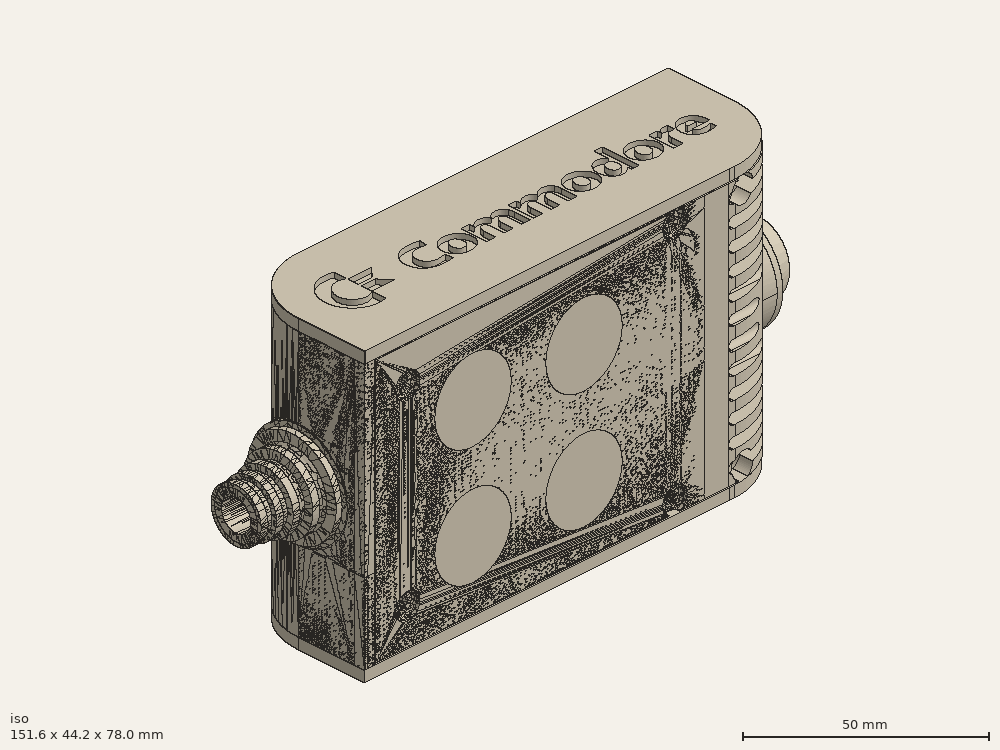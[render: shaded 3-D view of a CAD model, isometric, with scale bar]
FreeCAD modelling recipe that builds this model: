
FCSTD DOCUMENT  (FreeCAD 0.19R0.19.2)
Label: enclosure_224FCStd
License: All rights reserved
LicenseURL: http://en.wikipedia.org/wiki/All_rights_reserved
objects: Part::Revolution×152, Part::MultiFuse×148, Part::Feature×146, Sketcher::SketchObject×94, Part::Extrusion×79, Part::Cut×74, Part::Cylinder×70, Part::Fillet×58, Part::Box×38, App::MeasureDistance×4, Part::Chamfer×4, Part::FeaturePython×2, Image::ImagePlane×1, PartDesign::Body×1, Part::Mirroring×1
note: 867 computed .brp shape members not serialized (recipe doc carries the construction recipe); baked Part::Feature solids carry a one-line shape summary decoded from their .brp

FEATURE [Sketcher::SketchObject] Sketch  label="topSketch"
  FullyConstrained = true
  sketch-geometry (20):
    g0: LineSegment StartX=5.21097e-06 StartY=3 StartZ=0 EndX=5.21097e-06 EndY=19 EndZ=0
    g1: ArcOfCircle CenterX=19 CenterY=19 CenterZ=0 NormalX=0 NormalY=0 NormalZ=1 AngleXU=0 Radius=19 StartAngle=1.5708 EndAngle=3.14159
    g2: ArcOfCircle CenterX=19 CenterY=19 CenterZ=0 NormalX=0 NormalY=0 NormalZ=1 AngleXU=0 Radius=16 StartAngle=1.5708 EndAngle=3.14159
    g3: LineSegment StartX=114 StartY=35 StartZ=0 EndX=19 EndY=35 EndZ=0
    g4: LineSegment StartX=5.21097e-06 StartY=3 StartZ=0 EndX=5.21097e-06 EndY=0 EndZ=0
    g5: LineSegment StartX=3 StartY=0 StartZ=0 EndX=5.21097e-06 EndY=0 EndZ=0
    g6: LineSegment StartX=3 StartY=19 StartZ=0 EndX=3 EndY=0 EndZ=0
    g7: LineSegment StartX=19 StartY=38 StartZ=0 EndX=124 EndY=38 EndZ=0
    g8: Circle CenterX=119 CenterY=35 CenterZ=0 NormalX=0 NormalY=0 NormalZ=1 AngleXU=0 Radius=1
    g9: Circle CenterX=121 CenterY=35 CenterZ=0 NormalX=0 NormalY=0 NormalZ=1 AngleXU=0 Radius=1
    g10: Circle CenterX=121 CenterY=33 CenterZ=0 NormalX=0 NormalY=0 NormalZ=1 AngleXU=0 Radius=1
    g11: BSplineCurve PolesCount=3 KnotsCount=2 Degree=2 IsPeriodic=0
    g12: GeomPoint X=119 Y=35 Z=0
    g13: GeomPoint X=121 Y=33 Z=0
    g14: LineSegment StartX=119 StartY=35 StartZ=0 EndX=114 EndY=35 EndZ=0
    g15: ArcOfCircle CenterX=105 CenterY=19 CenterZ=0 NormalX=0 NormalY=0 NormalZ=1 AngleXU=0 Radius=19 StartAngle=5.7297 EndAngle=6.28319
    g16: ArcOfCircle CenterX=105 CenterY=19 CenterZ=0 NormalX=0 NormalY=0 NormalZ=1 AngleXU=0 Radius=16 StartAngle=5.60905 EndAngle=6.28319
    g17: LineSegment StartX=121 StartY=33 StartZ=0 EndX=121 EndY=19 EndZ=0
    g18: LineSegment StartX=124 StartY=38 StartZ=0 EndX=124 EndY=19 EndZ=0
    g19: LineSegment StartX=117.5 StartY=9.01251 StartZ=0 EndX=121.163 EndY=9.0125 EndZ=0
  constraints (46):
    c: Vertical(g0)
    c: Block(g0)
    c: Coincident(g1,g0)
    c: Block(g1)
    c: Coincident(g2,g1)
    c: Block(g2)
    c: Coincident(g3,g2)
    c: Horizontal(g3)
    c: Tangent(g3,g2)
    c: Coincident(g4,g0)
    c: Distance(g4) = 3
    c: Vertical(g4)
    c: Coincident(g5,g4)
    c: Horizontal(g5)
    c: Coincident(g6,g2)
    c: Coincident(g6,g5)
    c: Vertical(g6)
    c: Horizontal(g7)
    c: Distance(g7) = 105
    c: Coincident(g7,g1)
    c: Block(g3)
    c: Weight(g8) = 1
    c: Equal(g8,g9)
    c: Equal(g8,g10)
    c: InternalAlignment(g8,g11)
    c: InternalAlignment(g9,g11)
    c: InternalAlignment(g10,g11)
    c: InternalAlignment(g12,g11)
    c: InternalAlignment(g13,g11)
    c: Block(g11)
    c: Coincident(g14,g11)
    c: Coincident(g14,g3)
    c: Horizontal(g14)
    c: Block(g15)
    c: Coincident(g16,g15)
    c: Block(g16)
    c: Coincident(g17,g11)
    c: Coincident(g17,g16)
    c: Vertical(g17)
    c: Distance(g17) = 14
    c: Coincident(g18,g7)
    c: Coincident(g18,g15)
    c: Vertical(g18)
    c: Distance(g18) = 19
    c: Coincident(g19,g16)
    c: Coincident(g19,g15)
FEATURE [Sketcher::SketchObject] Sketch001  label="bottomSketch"
  FullyConstrained = true
  sketch-geometry (32):
    g0: LineSegment StartX=3.3 StartY=-6.03275e-07 StartZ=0 EndX=98 EndY=-6.03275e-07 EndZ=0
    g1: ArcOfCircle CenterX=98 CenterY=19 CenterZ=0 NormalX=0 NormalY=0 NormalZ=1 AngleXU=0 Radius=19 StartAngle=4.71239 EndAngle=5.71103
    g2: LineSegment StartX=6.3 StartY=8 StartZ=0 EndX=3.3 EndY=8 EndZ=0
    g3: LineSegment StartX=3.3 StartY=8 StartZ=0 EndX=3.3 EndY=-6.03275e-07 EndZ=0
    g4: ArcOfCircle CenterX=8.3 CenterY=5 CenterZ=0 NormalX=0 NormalY=0 NormalZ=1 AngleXU=0 Radius=2 StartAngle=3.14159 EndAngle=4.71239
    g5: LineSegment StartX=6.3 StartY=8 StartZ=0 EndX=6.3 EndY=5 EndZ=0
    g6: ArcOfCircle CenterX=98 CenterY=19 CenterZ=0 NormalX=0 NormalY=0 NormalZ=1 AngleXU=0 Radius=12.7 StartAngle=4.71239 EndAngle=6.28319
    g7: LineSegment StartX=94.7 StartY=3 StartZ=0 EndX=8.3 EndY=3 EndZ=0
    g8-g12: Circle x5 (B-spline internal-alignment scaffolding for g13; pole/knot coordinates omitted)
    g13: BSplineCurve PolesCount=5 KnotsCount=3 Degree=3 IsPeriodic=0
    g14: GeomPoint X=98 Y=6.3 Z=0
    g15: GeomPoint X=96.3938 Y=4.71946 Z=0
    g16: GeomPoint X=94.7 Y=3 Z=0
    g17-g23: Circle x7 (B-spline internal-alignment scaffolding for g24; pole/knot coordinates omitted)
    g24: BSplineCurve PolesCount=7 KnotsCount=5 Degree=3 IsPeriodic=0
    g25-g29: GeomPoint x5 (B-spline internal-alignment scaffolding for g24; pole/knot coordinates omitted)
    g30: ArcOfCircle CenterX=98 CenterY=19 CenterZ=0 NormalX=0 NormalY=0 NormalZ=1 AngleXU=0 Radius=15.7 StartAngle=5.81226 EndAngle=6.28319
    g31: LineSegment StartX=110.7 StartY=19 StartZ=0 EndX=113.7 EndY=19 EndZ=0
  constraints (41):
    c: Horizontal(g0)
    c: Coincident(g1,g0)
    c: Block(g1)
    c: Horizontal(g2)
    c: Distance(g2) = 3
    c: Coincident(g3,g2)
    c: Vertical(g3)
    c: Coincident(g3,g0)
    c: Block(g4)
    c: Block(g2)
    c: Coincident(g5,g2)
    c: Coincident(g5,g4)
    c: Vertical(g5)
    c: Coincident(g6,g1)
    c: Block(g6)
    c: Coincident(g7,g4)
    c: Horizontal(g7)
    c: Block(g0)
    c: Block(g7)
    c: Block(g3)
    c: Coincident(g13,g6)
    c: Weight(g8) = 1
    c: Equal(g8, g9-g12) x4
    c: Coincident(g13,g7)
    c: InternalAlignment(g8-g12 -> g13) x5
    c: InternalAlignment(g14,g13)
    c: InternalAlignment(g15,g13)
    c: InternalAlignment(g16,g13)
    c: Block(g13)
    c: Weight(g17) = 1
    c: Equal(g17, g18-g23) x6
    c: Coincident(g24,g1)
    c: InternalAlignment(g17-g23 -> g24) x7
    c: InternalAlignment(g25-g29 -> g24) x5
    c: Block(g24)
    c: Coincident(g30,g24)
    c: Coincident(g31,g6)
    c: Coincident(g31,g30)
    c: Horizontal(g31)
    c: Block(g31)
    c: Block(g30)
FEATURE [Part::Extrusion] Extrude  label="top"
  Base = -> Sketch
  Dir = (0,0,1)
  DirMode = 2
  FaceMakerClass = Part::FaceMakerBullseye
  LengthFwd = 72
  LengthRev = 0
  Solid = true
  Symmetric = false
FEATURE [Part::Extrusion] Extrude001  label="bottom"
  Base = -> Sketch001
  Dir = (0,0,1)
  DirMode = 2
  FaceMakerClass = Part::FaceMakerBullseye
  LengthFwd = 71.4
  LengthRev = 0
  Placement = pos=(0,0,0.3) rot=(0,0,1;0rad)
  Solid = true
  Symmetric = false
FEATURE [Sketcher::SketchObject] Sketch002  label="topSketch001"
  FullyConstrained = true
  sketch-geometry (8):
    g0: ArcOfCircle CenterX=19 CenterY=19.0975 CenterZ=0 NormalX=0 NormalY=0 NormalZ=1 AngleXU=0 Radius=18.9025 StartAngle=1.5708 EndAngle=3.14674
    g1: LineSegment StartX=0.0977805 StartY=19.0003 StartZ=0 EndX=0.0977805 EndY=0.000251602 EndZ=0
    g2: LineSegment StartX=19 StartY=38 StartZ=0 EndX=124 EndY=38 EndZ=0
    g3: LineSegment StartX=0.0977805 StartY=0.000251602 StartZ=0 EndX=105.098 EndY=0.000251602 EndZ=0
    g4: LineSegment StartX=124 StartY=38 StartZ=0 EndX=125.616 EndY=38 EndZ=0
    g5: LineSegment StartX=105.098 StartY=0.000251602 StartZ=0 EndX=106.713 EndY=0.000251602 EndZ=0
    g6: ArcOfCircle CenterX=106.616 CenterY=19 CenterZ=0 NormalX=0 NormalY=0 NormalZ=1 AngleXU=0 Radius=19 StartAngle=4.71754 EndAngle=6.28319
    g7: LineSegment StartX=125.616 StartY=38 StartZ=0 EndX=125.616 EndY=19 EndZ=0
  constraints (21):
    c: Block(g0)
    c: Coincident(g1,g0)
    c: Vertical(g1)
    c: Horizontal(g2)
    c: Distance(g2) = 105
    c: Coincident(g2,g0)
    c: Distance(g1) = 19
    c: Coincident(g3,g1)
    c: Horizontal(g3)
    c: Distance(g3) = 105
    c: Coincident(g4,g2)
    c: Horizontal(g4)
    c: Distance(g4) = 1.61553
    c: Horizontal(g5)
    c: Equal(g4,g5) = 1.61553
    c: Coincident(g5,g3)
    c: Block(g6)
    c: Coincident(g6,g5)
    c: Coincident(g7,g4)
    c: Coincident(g7,g6)
    c: Vertical(g7)
FEATURE [Part::Extrusion] Extrude002  label="sideA"
  Base = -> Sketch002
  Dir = (0,0,1)
  DirMode = 2
  FaceMakerClass = Part::FaceMakerBullseye
  LengthFwd = 3
  LengthRev = 0
  Placement = pos=(0,0,-3) rot=(0,0,1;0rad)
  Solid = true
  Symmetric = false
FEATURE [Sketcher::SketchObject] Sketch003  label="topSketch002"
  FullyConstrained = true
  sketch-geometry (6):
    g0: LineSegment StartX=19 StartY=38 StartZ=0 EndX=117 EndY=38 EndZ=0
    g1: ArcOfCircle CenterX=19 CenterY=19 CenterZ=0 NormalX=0 NormalY=0 NormalZ=1 AngleXU=0 Radius=19 StartAngle=1.5708 EndAngle=3.14159
    g2: LineSegment StartX=117 StartY=38 StartZ=0 EndX=117 EndY=19 EndZ=0
    g3: LineSegment StartX=98 StartY=1.0161e-12 StartZ=0 EndX=5.22862e-06 EndY=1.0161e-12 EndZ=0
    g4: LineSegment StartX=5.22862e-06 StartY=19 StartZ=0 EndX=5.22862e-06 EndY=1.0161e-12 EndZ=0
    g5: ArcOfCircle CenterX=98 CenterY=19 CenterZ=0 NormalX=0 NormalY=0 NormalZ=1 AngleXU=0 Radius=19 StartAngle=4.71239 EndAngle=6.28319
  constraints (16):
    c: Horizontal(g0)
    c: Distance(g0) = 98
    c: Coincident(g1,g0)
    c: Block(g1)
    c: Coincident(g2,g0)
    c: Vertical(g2)
    c: Distance(g2) = 19
    c: Horizontal(g3)
    c: Coincident(g4,g1)
    c: Vertical(g4)
    c: Coincident(g3,g4)
    c: Block(g3)
    c: Coincident(g5,g2)
    c: Coincident(g5,g3)
    c: Block(g0)
    c: Block(g5)
FEATURE [Sketcher::SketchObject] Sketch004
  FullyConstrained = true
  MapMode = 3
  Placement = pos=(0,0,0) rot=(1,0,0;1.5708rad)
  Support = -> [Extrude]
  sketch-geometry (8):
    g0: Circle CenterX=80.351 CenterY=-67.6202 CenterZ=0 NormalX=0 NormalY=0 NormalZ=1 AngleXU=0 Radius=2
    g1: Circle CenterX=80.351 CenterY=-67.6202 CenterZ=0 NormalX=0 NormalY=0 NormalZ=1 AngleXU=0 Radius=3
    g2: Circle CenterX=80.351 CenterY=-4.92017 CenterZ=0 NormalX=0 NormalY=0 NormalZ=1 AngleXU=0 Radius=2
    g3: Circle CenterX=80.351 CenterY=-4.92017 CenterZ=0 NormalX=0 NormalY=0 NormalZ=1 AngleXU=0 Radius=3
    g4: Circle CenterX=23.851 CenterY=-4.92017 CenterZ=0 NormalX=0 NormalY=0 NormalZ=1 AngleXU=0 Radius=2
    g5: Circle CenterX=23.851 CenterY=-4.92017 CenterZ=0 NormalX=0 NormalY=0 NormalZ=1 AngleXU=0 Radius=3
    g6: Circle CenterX=23.851 CenterY=-67.6202 CenterZ=0 NormalX=0 NormalY=0 NormalZ=1 AngleXU=0 Radius=2
    g7: Circle CenterX=23.851 CenterY=-67.6202 CenterZ=0 NormalX=0 NormalY=0 NormalZ=1 AngleXU=0 Radius=3
  constraints (8):
    c: Block(g3)
    c: Block(g2)
    c: Block(g1)
    c: Block(g0)
    c: Block(g6)
    c: Block(g7)
    c: Block(g4)
    c: Block(g5)
FEATURE [Part::Extrusion] Extrude004
  Base = -> Sketch004
  Dir = (0,-1,2e-16)
  DirMode = 2
  FaceMakerClass = Part::FaceMakerBullseye
  LengthFwd = 6
  LengthRev = 0
  Placement = pos=(0,9,0) rot=(0,0,1;0rad)
  Solid = true
  Symmetric = false
FEATURE [Sketcher::SketchObject] Sketch005
  FullyConstrained = true
  MapMode = 3
  Placement = pos=(0,0,0) rot=(1,0,0;1.5708rad)
  Support = -> [Extrude]
  sketch-geometry (8):
    g0: Circle CenterX=80.351 CenterY=-67.6202 CenterZ=0 NormalX=0 NormalY=0 NormalZ=1 AngleXU=0 Radius=3
    g1: Circle CenterX=80.351 CenterY=-4.92017 CenterZ=0 NormalX=0 NormalY=0 NormalZ=1 AngleXU=0 Radius=3
    g2: Circle CenterX=23.851 CenterY=-4.92017 CenterZ=0 NormalX=0 NormalY=0 NormalZ=1 AngleXU=0 Radius=3
    g3: Circle CenterX=23.851 CenterY=-67.6202 CenterZ=0 NormalX=0 NormalY=0 NormalZ=1 AngleXU=0 Radius=3
    g4: Circle CenterX=23.851 CenterY=-67.6202 CenterZ=0 NormalX=0 NormalY=0 NormalZ=1 AngleXU=0 Radius=5
    g5: Circle CenterX=80.351 CenterY=-67.6202 CenterZ=0 NormalX=0 NormalY=0 NormalZ=1 AngleXU=0 Radius=5
    g6: Circle CenterX=23.851 CenterY=-4.92017 CenterZ=0 NormalX=0 NormalY=0 NormalZ=1 AngleXU=0 Radius=5
    g7: Circle CenterX=80.351 CenterY=-4.92017 CenterZ=0 NormalX=0 NormalY=0 NormalZ=1 AngleXU=0 Radius=5
  constraints (8):
    c: Block(g1)
    c: Block(g0)
    c: Block(g3)
    c: Block(g2)
    c: Block(g5)
    c: Block(g4)
    c: Block(g6)
    c: Block(g7)
FEATURE [Part::Extrusion] Extrude005
  Base = -> Sketch005
  Dir = (0,-1,2e-16)
  DirMode = 2
  FaceMakerClass = Part::FaceMakerBullseye
  LengthFwd = 2
  LengthRev = 0
  Solid = true
  Symmetric = false
FEATURE [Sketcher::SketchObject] Sketch006
  FullyConstrained = true
  MapMode = 3
  Placement = pos=(0,0,0) rot=(1,0,0;1.5708rad)
  sketch-geometry (8):
    g0: Circle CenterX=80.351 CenterY=-67.6202 CenterZ=0 NormalX=0 NormalY=0 NormalZ=1 AngleXU=0 Radius=3
    g1: Circle CenterX=80.351 CenterY=-4.92017 CenterZ=0 NormalX=0 NormalY=0 NormalZ=1 AngleXU=0 Radius=3
    g2: Circle CenterX=23.851 CenterY=-4.92017 CenterZ=0 NormalX=0 NormalY=0 NormalZ=1 AngleXU=0 Radius=3
    g3: Circle CenterX=23.851 CenterY=-67.6202 CenterZ=0 NormalX=0 NormalY=0 NormalZ=1 AngleXU=0 Radius=3
    g4: Circle CenterX=23.851 CenterY=-67.6202 CenterZ=0 NormalX=0 NormalY=0 NormalZ=1 AngleXU=0 Radius=5
    g5: Circle CenterX=80.351 CenterY=-67.6202 CenterZ=0 NormalX=0 NormalY=0 NormalZ=1 AngleXU=0 Radius=5
    g6: Circle CenterX=23.851 CenterY=-4.92017 CenterZ=0 NormalX=0 NormalY=0 NormalZ=1 AngleXU=0 Radius=5
    g7: Circle CenterX=80.351 CenterY=-4.92017 CenterZ=0 NormalX=0 NormalY=0 NormalZ=1 AngleXU=0 Radius=5
  constraints (8):
    c: Block(g1)
    c: Block(g0)
    c: Block(g3)
    c: Block(g2)
    c: Block(g5)
    c: Block(g4)
    c: Block(g6)
    c: Block(g7)
FEATURE [Part::Extrusion] Extrude007
  Base = -> Sketch006
  Dir = (0,-1,2e-16)
  DirMode = 2
  FaceMakerClass = Part::FaceMakerBullseye
  LengthFwd = 2
  LengthRev = 0
  Solid = true
  Symmetric = false
FEATURE [Part::Fillet] Fillet
  Base = -> Extrude007
  Edges = 4 edges r=1.99: [Edge6,Edge12,Edge18,Edge24]
FEATURE [Part::Cut] Cut
  Base = -> Extrude005
  Placement = pos=(0,5,0) rot=(0,0,1;0rad)
  Tool = -> Fillet
FEATURE [Part::MultiFuse] Fusion  label="pCBScrews"
  Placement = pos=(-2.5,0,72.3) rot=(0,0,1;0rad)
  Shapes = -> [Extrude004,Cut]
FEATURE [App::MeasureDistance] Distance  label="Distance: 0.69 mm"
  Distance = 0.685967
  P1 = (24.0138,2.9647,0.3)
  P2 = (23.8901,3,-0.373787)
FEATURE [App::MeasureDistance] Distance001  label="Distance: 0.53 mm"
  Distance = 0.533607
  P1 = (80.2939,3,72.2334)
  P2 = (80.281,2.99661,71.7)
FEATURE [Part::Fillet] Fillet001
  Base = -> Extrude001
  Edges = 1 edges r=2.4: [Edge17]
FEATURE [Part::Fillet] Fillet002  label="bottom001"
  Base = -> Fillet001
  Edges = 1 edges r=2.4: [Edge36]
FEATURE [Part::Fillet] Fillet003  label="top001"
  Base = -> Extrude
  Edges = 1 edges r=2: [Edge1]
FEATURE [Sketcher::SketchObject] Sketch007
  FullyConstrained = true
  sketch-geometry (16):
    g0: LineSegment StartX=4 StartY=0 StartZ=0 EndX=4 EndY=2.4 EndZ=0
    g1: LineSegment StartX=4 StartY=2.4 StartZ=0 EndX=7 EndY=2.4 EndZ=0
    g2: LineSegment StartX=4 StartY=0 StartZ=0 EndX=5.7 EndY=0 EndZ=0
    g3: LineSegment StartX=5.7 StartY=0 StartZ=0 EndX=5.7 EndY=-5.6 EndZ=0
    g4-g8: Circle x5 (B-spline internal-alignment scaffolding for g9; pole/knot coordinates omitted)
    g9: BSplineCurve PolesCount=5 KnotsCount=3 Degree=3 IsPeriodic=0
    g10: GeomPoint X=7 Y=2.4 Z=0
    g11: GeomPoint X=10.4582 Y=-1.55472 Z=0
    g12: GeomPoint X=14 Y=-5.6 Z=0
    g13: LineSegment StartX=14 StartY=-5.6 StartZ=0 EndX=14 EndY=-14.1 EndZ=0
    g14: LineSegment StartX=14 StartY=-14.1 StartZ=0 EndX=6.5 EndY=-14.1 EndZ=0
    g15: LineSegment StartX=5.7 StartY=-5.6 StartZ=0 EndX=6.5 EndY=-14.1 EndZ=0
  constraints (28):
    c: Distance(g0) = 2.4
    c: Vertical(g0)
    c: Block(g0)
    c: Coincident(g1,g0)
    c: Horizontal(g1)
    c: Distance(g1) = 3
    c: Coincident(g2,g0)
    c: Horizontal(g2)
    c: Distance(g2) = 1.7
    c: Coincident(g3,g2)
    c: Vertical(g3)
    c: Distance(g3) = 5.6
    c: Coincident(g9,g1)
    c: Weight(g4) = 1
    c: Equal(g4, g5-g8) x4
    c: InternalAlignment(g4-g8 -> g9) x5
    c: InternalAlignment(g10,g9)
    c: InternalAlignment(g11,g9)
    c: InternalAlignment(g12,g9)
    c: Block(g9)
    c: Coincident(g13,g9)
    c: Vertical(g13)
    c: Distance(g13) = 8.5
    c: Coincident(g14,g13)
    c: Horizontal(g14)
    c: Distance(g14) = 7.5
    c: Coincident(g15,g3)
    c: Coincident(g15,g14)
FEATURE [Part::Feature] Face
  shape: bbox 10 x 16.5 x 2e-07 mm, 1 faces, 0 solids (baked)
FEATURE [Part::Revolution] Revolve  label="plugHousing"
  Angle = 360
  Axis = (0,1,0)
  Base = (0,0,0)
  FaceMakerClass = Part::FaceMakerBullseye
  Placement = pos=(0,0,36.15) rot=(0,0,1;0rad)
  Solid = false
  Source = -> Face
  Symmetric = false
FEATURE [Part::Feature] Face001
  shape: bbox 10 x 16.5 x 2e-07 mm, 1 faces, 0 solids (baked)
FEATURE [Part::Revolution] Revolve001  label="plugHousing001"
  Angle = 360
  Axis = (0,1,0)
  Base = (0,0,0)
  FaceMakerClass = Part::FaceMakerBullseye
  Placement = pos=(0,0,36.15) rot=(0,0,1;0rad)
  Solid = false
  Source = -> Face001
  Symmetric = false
FEATURE [Part::MultiFuse] Fusion001  label="plugHousing002"
  Placement = pos=(0,0,0) rot=(0,0,1;1.5708rad)
  Shapes = -> [Revolve001,Revolve]
FEATURE [Part::Feature] Face002
  shape: bbox 10 x 16.5 x 2e-07 mm, 1 faces, 0 solids (baked)
FEATURE [Part::Revolution] Revolve003  label="plugHousing005"
  Angle = 360
  Axis = (0,1,0)
  Base = (0,0,0)
  FaceMakerClass = Part::FaceMakerBullseye
  Placement = pos=(0,0,36.15) rot=(0,0,1;0rad)
  Solid = false
  Source = -> Face002
  Symmetric = false
FEATURE [Part::Feature] Face003
  shape: bbox 10 x 16.5 x 2e-07 mm, 1 faces, 0 solids (baked)
FEATURE [Part::Revolution] Revolve002  label="plugHousing003"
  Angle = 360
  Axis = (0,1,0)
  Base = (0,0,0)
  FaceMakerClass = Part::FaceMakerBullseye
  Placement = pos=(0,0,36.15) rot=(0,0,1;0rad)
  Solid = false
  Source = -> Face003
  Symmetric = false
FEATURE [Part::MultiFuse] Fusion002  label="plugHousing004"
  Placement = pos=(0,0,0) rot=(0,0,1;1.5708rad)
  Shapes = -> [Revolve002,Revolve003]
FEATURE [Part::MultiFuse] Fusion003  label="plugHousing006"
  Placement = pos=(0,19,0) rot=(0,0,1;3.14159rad)
  Shapes = -> [Fusion002,Fusion001]
FEATURE [Part::Feature] Face004
  shape: bbox 10 x 16.5 x 2e-07 mm, 1 faces, 0 solids (baked)
FEATURE [Part::Revolution] Revolve006  label="plugHousing010"
  Angle = 360
  Axis = (0,1,0)
  Base = (0,0,0)
  FaceMakerClass = Part::FaceMakerBullseye
  Placement = pos=(0,0,36.15) rot=(0,0,1;0rad)
  Solid = false
  Source = -> Face004
  Symmetric = false
FEATURE [Part::Feature] Face005
  shape: bbox 10 x 16.5 x 2e-07 mm, 1 faces, 0 solids (baked)
FEATURE [Part::Revolution] Revolve007  label="plugHousing011"
  Angle = 360
  Axis = (0,1,0)
  Base = (0,0,0)
  FaceMakerClass = Part::FaceMakerBullseye
  Placement = pos=(0,0,36.15) rot=(0,0,1;0rad)
  Solid = false
  Source = -> Face005
  Symmetric = false
FEATURE [Part::Feature] Face006
  shape: bbox 10 x 16.5 x 2e-07 mm, 1 faces, 0 solids (baked)
FEATURE [Part::Revolution] Revolve004  label="plugHousing007"
  Angle = 360
  Axis = (0,1,0)
  Base = (0,0,0)
  FaceMakerClass = Part::FaceMakerBullseye
  Placement = pos=(0,0,36.15) rot=(0,0,1;0rad)
  Solid = false
  Source = -> Face006
  Symmetric = false
FEATURE [Part::MultiFuse] Fusion004  label="plugHousing009"
  Placement = pos=(0,0,0) rot=(0,0,1;1.5708rad)
  Shapes = -> [Revolve004,Revolve007]
FEATURE [Part::Feature] Face007
  shape: bbox 10 x 16.5 x 2e-07 mm, 1 faces, 0 solids (baked)
FEATURE [Part::Revolution] Revolve005  label="plugHousing008"
  Angle = 360
  Axis = (0,1,0)
  Base = (0,0,0)
  FaceMakerClass = Part::FaceMakerBullseye
  Placement = pos=(0,0,36.15) rot=(0,0,1;0rad)
  Solid = false
  Source = -> Face007
  Symmetric = false
FEATURE [Part::MultiFuse] Fusion005  label="plugHousing012"
  Placement = pos=(0,0,0) rot=(0,0,1;1.5708rad)
  Shapes = -> [Revolve006,Revolve005]
FEATURE [Part::MultiFuse] Fusion006  label="plugHousing013"
  Placement = pos=(0,19,0) rot=(0,0,1;3.14159rad)
  Shapes = -> [Fusion005,Fusion004]
FEATURE [Part::MultiFuse] Fusion007  label="plugHousing014"
  Placement = pos=(122.621,0,-0.15) rot=(0,0,1;0rad)
  Shapes = -> [Fusion003,Fusion006]
FEATURE [Part::Cylinder] Cylinder002
  Angle = 360
  AttacherType = Attacher::AttachEngine3D
  Height = 20
  Placement = pos=(0,0,36.15) rot=(0,0,1;0rad)
  Radius = 4
FEATURE [Part::Cylinder] Cylinder003
  Angle = 360
  AttacherType = Attacher::AttachEngine3D
  Height = 10
  Placement = pos=(0,0,36.15) rot=(0,0,1;0rad)
  Radius = 4
FEATURE [Part::MultiFuse] Fusion009  label="removeToCreateHoleForPlugHousing"
  Placement = pos=(70,19,36.15) rot=(0,1,0;1.5708rad)
  Shapes = -> [Cylinder002,Cylinder003]
FEATURE [Part::Cylinder] Cylinder004
  Angle = 360
  AttacherType = Attacher::AttachEngine3D
  Height = 20
  Placement = pos=(0,0,36.15) rot=(0,0,1;0rad)
  Radius = 4
FEATURE [Part::Cylinder] Cylinder005
  Angle = 360
  AttacherType = Attacher::AttachEngine3D
  Height = 10
  Placement = pos=(0,0,36.15) rot=(0,0,1;0rad)
  Radius = 4
FEATURE [Part::MultiFuse] Fusion010  label="removeToCreateHoleForPlugHousing001"
  Placement = pos=(70,19,36.15) rot=(0,1,0;1.5708rad)
  Shapes = -> [Cylinder004,Cylinder005]
FEATURE [Part::Cut] Cut001
  Base = -> Fillet003
  Tool = -> Fusion010
FEATURE [Part::Cut] Cut002  label="Bottom"
  Base = -> Fillet002
  Tool = -> Fusion009
FEATURE [Part::Feature] Face008
  shape: bbox 10 x 16.5 x 2e-07 mm, 1 faces, 0 solids (baked)
FEATURE [Part::Revolution] Revolve011  label="plugHousing021"
  Angle = 360
  Axis = (0,1,0)
  Base = (0,0,0)
  FaceMakerClass = Part::FaceMakerBullseye
  Placement = pos=(0,0,36.15) rot=(0,0,1;0rad)
  Solid = false
  Source = -> Face008
  Symmetric = false
FEATURE [Part::Feature] Face009
  shape: bbox 10 x 16.5 x 2e-07 mm, 1 faces, 0 solids (baked)
FEATURE [Part::Revolution] Revolve012  label="plugHousing022"
  Angle = 360
  Axis = (0,1,0)
  Base = (0,0,0)
  FaceMakerClass = Part::FaceMakerBullseye
  Placement = pos=(0,0,36.15) rot=(0,0,1;0rad)
  Solid = false
  Source = -> Face009
  Symmetric = false
FEATURE [Part::Feature] Face010 .. Face013  x4 (patterned run collapsed; names and placements below)
  shape: bbox 10 x 16.5 x 2e-07 mm, 1 faces, 0 solids (baked)
FEATURE [Part::Revolution] Revolve015  label="plugHousing027"
  Angle = 360
  Axis = (0,1,0)
  Base = (0,0,0)
  FaceMakerClass = Part::FaceMakerBullseye
  Placement = pos=(0,0,36.15) rot=(0,0,1;0rad)
  Solid = false
  Source = -> Face013
  Symmetric = false
FEATURE [Part::Feature] Face014
  shape: bbox 10 x 16.5 x 2e-07 mm, 1 faces, 0 solids (baked)
FEATURE [Part::Feature] Face015
  shape: bbox 10 x 16.5 x 2e-07 mm, 1 faces, 0 solids (baked)
FEATURE [Part::Feature] Face016
  shape: bbox 10 x 16.5 x 2e-07 mm, 1 faces, 0 solids (baked)
FEATURE [Part::Revolution] Revolve019  label="plugHousing033"
  Angle = 360
  Axis = (0,1,0)
  Base = (0,0,0)
  FaceMakerClass = Part::FaceMakerBullseye
  Placement = pos=(0,0,36.15) rot=(0,0,1;0rad)
  Solid = false
  Source = -> Face016
  Symmetric = false
FEATURE [Part::Feature] Face017
  shape: bbox 10 x 16.5 x 2e-07 mm, 1 faces, 0 solids (baked)
FEATURE [Part::Revolution] Revolve020  label="plugHousing034"
  Angle = 360
  Axis = (0,1,0)
  Base = (0,0,0)
  FaceMakerClass = Part::FaceMakerBullseye
  Placement = pos=(0,0,36.15) rot=(0,0,1;0rad)
  Solid = false
  Source = -> Face017
  Symmetric = false
FEATURE [Part::Feature] Face018
  shape: bbox 10 x 16.5 x 2e-07 mm, 1 faces, 0 solids (baked)
FEATURE [Part::Revolution] Revolve016  label="plugHousing030"
  Angle = 360
  Axis = (0,1,0)
  Base = (0,0,0)
  FaceMakerClass = Part::FaceMakerBullseye
  Placement = pos=(0,0,36.15) rot=(0,0,1;0rad)
  Solid = false
  Source = -> Face018
  Symmetric = false
FEATURE [Part::MultiFuse] Fusion020  label="plugHousing038"
  Placement = pos=(0,0,0) rot=(0,0,1;1.5708rad)
  Shapes = -> [Revolve016,Revolve020]
FEATURE [Part::Feature] Face019
  shape: bbox 10 x 16.5 x 2e-07 mm, 1 faces, 0 solids (baked)
FEATURE [Part::Feature] Face020
  shape: bbox 10 x 16.5 x 2e-07 mm, 1 faces, 0 solids (baked)
FEATURE [Part::Revolution] Revolve017  label="plugHousing031"
  Angle = 360
  Axis = (0,1,0)
  Base = (0,0,0)
  FaceMakerClass = Part::FaceMakerBullseye
  Placement = pos=(0,0,36.15) rot=(0,0,1;0rad)
  Solid = false
  Source = -> Face020
  Symmetric = false
FEATURE [Part::MultiFuse] Fusion021  label="plugHousing039"
  Placement = pos=(0,0,0) rot=(0,0,1;1.5708rad)
  Shapes = -> [Revolve019,Revolve017]
FEATURE [Part::MultiFuse] Fusion023  label="plugHousing041"
  Placement = pos=(0,19,0) rot=(0,0,1;3.14159rad)
  Shapes = -> [Fusion021,Fusion020]
FEATURE [Part::Revolution] Revolve022  label="plugHousing043"
  Angle = 360
  Axis = (0,1,0)
  Base = (0,0,0)
  FaceMakerClass = Part::FaceMakerBullseye
  Placement = pos=(0,0,36.15) rot=(0,0,1;0rad)
  Solid = false
  Source = -> Face019
  Symmetric = false
FEATURE [Part::Feature] Face021
  shape: bbox 10 x 16.5 x 2e-07 mm, 1 faces, 0 solids (baked)
FEATURE [Part::Revolution] Revolve023  label="plugHousing044"
  Angle = 360
  Axis = (0,1,0)
  Base = (0,0,0)
  FaceMakerClass = Part::FaceMakerBullseye
  Placement = pos=(0,0,36.15) rot=(0,0,1;0rad)
  Solid = false
  Source = -> Face021
  Symmetric = false
FEATURE [Part::Feature] Face022
  shape: bbox 10 x 16.5 x 2e-07 mm, 1 faces, 0 solids (baked)
FEATURE [Part::Revolution] Revolve018  label="plugHousing032"
  Angle = 360
  Axis = (0,1,0)
  Base = (0,0,0)
  FaceMakerClass = Part::FaceMakerBullseye
  Placement = pos=(0,0,36.15) rot=(0,0,1;0rad)
  Solid = false
  Source = -> Face022
  Symmetric = false
FEATURE [Part::MultiFuse] Fusion022  label="plugHousing040"
  Placement = pos=(0,0,0) rot=(0,0,1;1.5708rad)
  Shapes = -> [Revolve018,Revolve023]
FEATURE [Part::Feature] Face023
  shape: bbox 10 x 16.5 x 2e-07 mm, 1 faces, 0 solids (baked)
FEATURE [Part::Revolution] Revolve021  label="plugHousing035"
  Angle = 360
  Axis = (0,1,0)
  Base = (0,0,0)
  FaceMakerClass = Part::FaceMakerBullseye
  Placement = pos=(0,0,36.15) rot=(0,0,1;0rad)
  Solid = false
  Source = -> Face023
  Symmetric = false
FEATURE [Part::MultiFuse] Fusion018  label="plugHousing036"
  Placement = pos=(0,0,0) rot=(0,0,1;1.5708rad)
  Shapes = -> [Revolve022,Revolve021]
FEATURE [Part::MultiFuse] Fusion019  label="plugHousing037"
  Placement = pos=(0,19,0) rot=(0,0,1;3.14159rad)
  Shapes = -> [Fusion018,Fusion022]
FEATURE [Part::MultiFuse] Fusion024  label="plugHousing042"
  Placement = pos=(122.621,0,-0.15) rot=(0,0,1;0rad)
  Shapes = -> [Fusion023,Fusion019]
FEATURE [Part::Cylinder] Cylinder006
  Angle = 360
  AttacherType = Attacher::AttachEngine3D
  Height = 20
  Placement = pos=(0,0,36.15) rot=(0,0,1;0rad)
  Radius = 14.3
FEATURE [Part::Cylinder] Cylinder007
  Angle = 360
  AttacherType = Attacher::AttachEngine3D
  Height = 10
  Placement = pos=(0,0,36.15) rot=(0,0,1;0rad)
  Radius = 4
FEATURE [Part::MultiFuse] Fusion026  label="removeToCreteHoleForPlugHousing"
  Placement = pos=(70,19,36) rot=(0,1,0;1.5708rad)
  Shapes = -> [Cylinder006,Cylinder007]
FEATURE [Part::Box] Box001  label="Cube001"
  AttacherType = Attacher::AttachEngine3D
  Height = 28
  Length = 3
  Placement = pos=(110.7,19,22) rot=(0,0,1;0rad)
  Width = 15.7
FEATURE [Part::Cut] Cut003  label="top002"
  Base = -> Cut001
  Tool = -> Fusion007
FEATURE [Part::Revolution] Revolve008  label="plugHousing015"
  Angle = 360
  Axis = (0,1,0)
  Base = (0,0,0)
  FaceMakerClass = Part::FaceMakerBullseye
  Placement = pos=(0,0,36.15) rot=(0,0,1;0rad)
  Solid = false
  Source = -> Face010
  Symmetric = false
FEATURE [Part::MultiFuse] Fusion013  label="plugHousing020"
  Placement = pos=(0,0,0) rot=(0,0,1;1.5708rad)
  Shapes = -> [Revolve008,Revolve012]
FEATURE [Part::Cut] Cut004  label="top003"
  Base = -> Cut003
  Placement = pos=(1,0,0) rot=(0,0,1;0rad)
  Tool = -> Fusion026
FEATURE [Part::Cylinder] Cylinder008
  Angle = 360
  AttacherType = Attacher::AttachEngine3D
  Height = 20
  Placement = pos=(0,0,36.15) rot=(0,0,1;0rad)
  Radius = 10.3
FEATURE [Part::Cylinder] Cylinder009
  Angle = 360
  AttacherType = Attacher::AttachEngine3D
  Height = 10
  Placement = pos=(0,0,36.15) rot=(0,0,1;0rad)
  Radius = 4
FEATURE [Part::MultiFuse] Fusion027  label="removeToCreteHoleForPlugHousing001"
  Placement = pos=(70,19,36) rot=(0,1,0;1.5708rad)
  Shapes = -> [Cylinder008,Cylinder009]
FEATURE [Part::Cut] Cut005  label="plugHousingTab"
  Base = -> Box001
  Tool = -> Fusion027
FEATURE [Part::MultiFuse] Fusion028  label="plugHousing045"
  Shapes = -> [Fusion024,Cut005]
FEATURE [Part::Box] Box002  label="Cube002"
  AttacherType = Attacher::AttachEngine3D
  Height = 28.8
  Length = 3
  Placement = pos=(107.3,28,21.6) rot=(0,0,1;0rad)
  Width = 7
FEATURE [Part::Box] Box003  label="Cube003"
  AttacherType = Attacher::AttachEngine3D
  Height = 3
  Length = 6.4
  Placement = pos=(107.3,28,18.6) rot=(0,0,1;0rad)
  Width = 7
FEATURE [Part::Box] Box004  label="Cube004"
  AttacherType = Attacher::AttachEngine3D
  Height = 3
  Length = 6.4
  Placement = pos=(107.3,28,50.4) rot=(0,0,1;0rad)
  Width = 7
FEATURE [Part::MultiFuse] Fusion029  label="plugHousingBracketHolder"
  Shapes = -> [Box004,Box002,Box003]
FEATURE [Part::Cylinder] Cylinder010
  Angle = 360
  AttacherType = Attacher::AttachEngine3D
  Height = 20
  Placement = pos=(0,0,36.15) rot=(0,0,1;0rad)
  Radius = 14.3
FEATURE [Part::Cylinder] Cylinder011
  Angle = 360
  AttacherType = Attacher::AttachEngine3D
  Height = 10
  Placement = pos=(0,0,36.15) rot=(0,0,1;0rad)
  Radius = 4
FEATURE [Part::MultiFuse] Fusion030  label="removeToCreteHoleForPlugHousing002"
  Placement = pos=(70,19,36) rot=(0,1,0;1.5708rad)
  Shapes = -> [Cylinder010,Cylinder011]
FEATURE [Part::Cut] Cut006  label="plugHousingBracketHolder001"
  Base = -> Fusion029
  Tool = -> Fusion030
FEATURE [Part::Cylinder] Cylinder012
  Angle = 360
  AttacherType = Attacher::AttachEngine3D
  Height = 20
  Placement = pos=(0,0,36.15) rot=(0,0,1;0rad)
  Radius = 7
FEATURE [Part::Cylinder] Cylinder013
  Angle = 360
  AttacherType = Attacher::AttachEngine3D
  Height = 10
  Placement = pos=(0,0,36.15) rot=(0,0,1;0rad)
  Radius = 4
FEATURE [Part::MultiFuse] Fusion032  label="removeToCreteHoleForPlugHousing003"
  Placement = pos=(70,19,36) rot=(0,1,0;1.5708rad)
  Shapes = -> [Cylinder012,Cylinder013]
FEATURE [Part::Cut] Cut007  label="bottom002"
  Base = -> Cut002
  Tool = -> Fusion032
FEATURE [Sketcher::SketchObject] Sketch008
  FullyConstrained = true
  sketch-geometry (54):
    g0: LineSegment StartX=-4.2 StartY=0 StartZ=0 EndX=-6.2 EndY=0 EndZ=0
    g1: LineSegment StartX=-14 StartY=-18 StartZ=0 EndX=-14 EndY=-26.5 EndZ=0
    g2: LineSegment StartX=-4.2 StartY=0 StartZ=0 EndX=-4.2 EndY=-13.4877 EndZ=0
    g3: Circle CenterX=-4.2 CenterY=-13.4877 CenterZ=0 NormalX=0 NormalY=0 NormalZ=1 AngleXU=0 Radius=1
    g4: Circle CenterX=-4.2 CenterY=-26.5 CenterZ=0 NormalX=0 NormalY=0 NormalZ=1 AngleXU=0 Radius=1
    g5: Circle CenterX=-8.2 CenterY=-26.5 CenterZ=0 NormalX=0 NormalY=0 NormalZ=1 AngleXU=0 Radius=1
    g6: BSplineCurve PolesCount=3 KnotsCount=2 Degree=2 IsPeriodic=0
    g7: GeomPoint X=-4.2 Y=-13.4877 Z=0
    g8: GeomPoint X=-8.2 Y=-26.5 Z=0
    g9: LineSegment StartX=-14 StartY=-26.5 StartZ=0 EndX=-8.2 EndY=-26.5 EndZ=0
    g10: LineSegment StartX=-10.15 StartY=-12 StartZ=0 EndX=-10.15 EndY=-14 EndZ=0
    g11: LineSegment StartX=-12.8401 StartY=-16 StartZ=0 EndX=-10.1571 EndY=-16 EndZ=0
    g12: LineSegment StartX=-10.15 StartY=-14 StartZ=0 EndX=-8.70761 EndY=-14 EndZ=0
    g13: LineSegment StartX=-12.8401 StartY=-16 StartZ=0 EndX=-12.8401 EndY=-17.6958 EndZ=0
    g14: LineSegment StartX=-10.15 StartY=-12 StartZ=0 EndX=-7.79258 EndY=-12 EndZ=0
    g15: Circle CenterX=-6.2215 CenterY=-2 CenterZ=0 NormalX=0 NormalY=0 NormalZ=1 AngleXU=0 Radius=1
    g16: Circle CenterX=-6.22762 CenterY=-2.58724 CenterZ=0 NormalX=0 NormalY=0 NormalZ=1 AngleXU=0 Radius=1
    g17: Circle CenterX=-6.32538 CenterY=-4 CenterZ=0 NormalX=0 NormalY=0 NormalZ=1 AngleXU=0 Radius=1
    g18: BSplineCurve PolesCount=3 KnotsCount=2 Degree=2 IsPeriodic=0
    g19: GeomPoint X=-6.2215 Y=-2 Z=0
    g20: GeomPoint X=-6.32538 Y=-4 Z=0
    g21: Circle CenterX=-6.48644 CenterY=-5.99526 CenterZ=0 NormalX=0 NormalY=0 NormalZ=1 AngleXU=0 Radius=1
    g22: Circle CenterX=-6.58486 CenterY=-6.99526 CenterZ=0 NormalX=0 NormalY=0 NormalZ=1 AngleXU=0 Radius=1
    g23: Circle CenterX=-6.77343 CenterY=-8 CenterZ=0 NormalX=0 NormalY=0 NormalZ=1 AngleXU=0 Radius=1
    g24: BSplineCurve PolesCount=3 KnotsCount=2 Degree=2 IsPeriodic=0
    g25: GeomPoint X=-6.48644 Y=-5.99526 Z=0
    g26: GeomPoint X=-6.77343 Y=-8 Z=0
    g27: Circle CenterX=-7.19003 CenterY=-10 CenterZ=0 NormalX=0 NormalY=0 NormalZ=1 AngleXU=0 Radius=1
    g28: Circle CenterX=-7.44407 CenterY=-11.0915 CenterZ=0 NormalX=0 NormalY=0 NormalZ=1 AngleXU=0 Radius=1
    g29: Circle CenterX=-7.79258 CenterY=-12 CenterZ=0 NormalX=0 NormalY=0 NormalZ=1 AngleXU=0 Radius=1
    g30: BSplineCurve PolesCount=3 KnotsCount=2 Degree=2 IsPeriodic=0
    g31: GeomPoint X=-7.19003 Y=-10 Z=0
    g32: GeomPoint X=-7.79258 Y=-12 Z=0
    g33: Circle CenterX=-8.70761 CenterY=-14 CenterZ=0 NormalX=0 NormalY=0 NormalZ=1 AngleXU=0 Radius=1
    g34: Circle CenterX=-9.33087 CenterY=-15.1837 CenterZ=0 NormalX=0 NormalY=0 NormalZ=1 AngleXU=0 Radius=1
    g35: Circle CenterX=-10.1571 CenterY=-16 CenterZ=0 NormalX=0 NormalY=0 NormalZ=1 AngleXU=0 Radius=1
    g36: BSplineCurve PolesCount=3 KnotsCount=2 Degree=2 IsPeriodic=0
    g37: GeomPoint X=-8.70761 Y=-14 Z=0
    g38: GeomPoint X=-10.1571 Y=-16 Z=0
    g39: Circle CenterX=-12.8401 CenterY=-17.6958 CenterZ=0 NormalX=0 NormalY=0 NormalZ=1 AngleXU=0 Radius=1
    g40: Circle CenterX=-13.3521 CenterY=-17.9027 CenterZ=0 NormalX=0 NormalY=0 NormalZ=1 AngleXU=0 Radius=1
    g41: Circle CenterX=-14 CenterY=-18 CenterZ=0 NormalX=0 NormalY=0 NormalZ=1 AngleXU=0 Radius=1
    g42: BSplineCurve PolesCount=3 KnotsCount=2 Degree=2 IsPeriodic=0
    g43: GeomPoint X=-12.8401 Y=-17.6958 Z=0
    g44: GeomPoint X=-14 Y=-18 Z=0
    g45: LineSegment StartX=-6.2 StartY=0 StartZ=0 EndX=-7.2 EndY=0 EndZ=0
    g46: LineSegment StartX=-7.2 StartY=0 StartZ=0 EndX=-7.2 EndY=-2 EndZ=0
    g47: LineSegment StartX=-7.2 StartY=-2 StartZ=0 EndX=-6.2215 EndY=-2 EndZ=0
    g48: LineSegment StartX=-6.32538 StartY=-4 StartZ=0 EndX=-7.65538 EndY=-4 EndZ=0
    g49: LineSegment StartX=-7.65538 StartY=-4 StartZ=0 EndX=-7.65538 EndY=-5.99526 EndZ=0
    g50: LineSegment StartX=-7.65538 StartY=-5.99526 StartZ=0 EndX=-6.48644 EndY=-5.99526 EndZ=0
    g51: LineSegment StartX=-6.77343 StartY=-8 StartZ=0 EndX=-8.43343 EndY=-8 EndZ=0
    g52: LineSegment StartX=-8.43343 StartY=-8 StartZ=0 EndX=-8.43343 EndY=-10 EndZ=0
    g53: LineSegment StartX=-8.43343 StartY=-10 StartZ=0 EndX=-7.19003 EndY=-10 EndZ=0
  constraints (112):
    c: Horizontal(g0)
    c: Distance(g0) = 2
    c: Block(g0)
    c: Vertical(g1)
    c: Coincident(g2,g0)
    c: Vertical(g2)
    c: Block(g2)
    c: Coincident(g6,g2)
    c: Weight(g3) = 1
    c: Equal(g3,g4)
    c: Equal(g3,g5)
    c: InternalAlignment(g3,g6)
    c: InternalAlignment(g4,g6)
    c: InternalAlignment(g5,g6)
    c: InternalAlignment(g7,g6)
    c: InternalAlignment(g8,g6)
    c: Block(g6)
    c: Coincident(g9,g1)
    c: Coincident(g9,g6)
    c: Horizontal(g9)
    c: Vertical(g10)
    c: Block(g10)
    c: Horizontal(g11)
    c: Block(g11)
    c: Coincident(g12,g10)
    c: Horizontal(g12)
    c: Block(g12)
    c: Coincident(g13,g11)
    c: Vertical(g13)
    c: Block(g13)
    c: Coincident(g14,g10)
    c: Horizontal(g14)
    c: Block(g14)
    c: Block(g9)
    c: Block(g1)
    c: Weight(g15) = 1
    c: Equal(g15,g16)
    c: Equal(g15,g17)
    c: InternalAlignment(g15,g18)
    c: InternalAlignment(g16,g18)
    c: InternalAlignment(g17,g18)
    c: InternalAlignment(g19,g18)
    c: InternalAlignment(g20,g18)
    c: Weight(g21) = 1
    c: Equal(g21,g22)
    c: Equal(g21,g23)
    c: InternalAlignment(g21,g24)
    c: InternalAlignment(g22,g24)
    c: InternalAlignment(g23,g24)
    c: InternalAlignment(g25,g24)
    c: InternalAlignment(g26,g24)
    c: Weight(g27) = 1
    c: Equal(g27,g28)
    c: Equal(g27,g29)
    c: Coincident(g30,g14)
    c: InternalAlignment(g27,g30)
    c: InternalAlignment(g28,g30)
    c: InternalAlignment(g29,g30)
    c: InternalAlignment(g31,g30)
    c: InternalAlignment(g32,g30)
    c: Coincident(g36,g12)
    c: Weight(g33) = 1
    c: Equal(g33,g34)
    c: Equal(g33,g35)
    c: Coincident(g36,g11)
    c: InternalAlignment(g33,g36)
    c: InternalAlignment(g34,g36)
    c: InternalAlignment(g35,g36)
    c: InternalAlignment(g37,g36)
    c: InternalAlignment(g38,g36)
    c: Coincident(g42,g13)
    c: Weight(g39) = 1
    c: Equal(g39,g40)
    c: Equal(g39,g41)
    c: Coincident(g42,g1)
    c: InternalAlignment(g39,g42)
    c: InternalAlignment(g40,g42)
    c: InternalAlignment(g41,g42)
    c: InternalAlignment(g43,g42)
    c: InternalAlignment(g44,g42)
    c: Block(g18)
    c: Block(g24)
    c: Block(g30)
    c: Block(g36)
    c: Block(g42)
    c: Horizontal(g45)
    c: Coincident(g45,g0)
    c: Vertical(g46)
    c: Coincident(g46,g45)
    c: Coincident(g47,g46)
    c: Coincident(g47,g18)
    c: Horizontal(g47)
    c: Block(g46)
    c: Coincident(g48,g18)
    c: Horizontal(g48)
    c: Distance(g48) = 1.33
    c: Vertical(g49)
    c: Coincident(g49,g48)
    c: Coincident(g50,g49)
    c: Coincident(g50,g24)
    c: Horizontal(g50)
    c: Tangent(g50,g22)
    c: Horizontal(g51)
    c: Coincident(g51,g24)
    c: Block(g51)
    c: Vertical(g52)
    c: Block(g52)
    c: Coincident(g52,g51)
    c: Coincident(g53,g52)
    c: Coincident(g53,g30)
    c: Horizontal(g53)
    c: Distance(g1) = 8.5
FEATURE [Part::Feature] Face024
  shape: bbox 9.8 x 26.5 x 2e-07 mm, 1 faces, 0 solids (baked)
FEATURE [Part::Revolution] Revolve024
  Angle = 360
  Axis = (0,1,0)
  Base = (0,0,0)
  FaceMakerClass = Part::FaceMakerBullseye
  Placement = pos=(0,0,0) rot=(0,0,1;1.5708rad)
  Solid = false
  Source = -> Face024
  Symmetric = false
FEATURE [Part::Feature] Face025
  shape: bbox 9.8 x 26.5 x 2e-07 mm, 1 faces, 0 solids (baked)
FEATURE [Part::Revolution] Revolve025
  Angle = 360
  Axis = (0,1,0)
  Base = (0,0,0)
  FaceMakerClass = Part::FaceMakerBullseye
  Placement = pos=(0,0,0) rot=(0,0,1;1.5708rad)
  Solid = false
  Source = -> Face025
  Symmetric = false
FEATURE [Part::MultiFuse] Fusion033
  Placement = pos=(-18,19,36) rot=(0,0,1;0rad)
  Shapes = -> [Revolve025,Revolve024]
FEATURE [Part::Cylinder] Cylinder014
  Angle = 360
  AttacherType = Attacher::AttachEngine3D
  Height = 20
  Placement = pos=(0,0,36.15) rot=(0,0,1;0rad)
  Radius = 14.3
FEATURE [Part::Cylinder] Cylinder015
  Angle = 360
  AttacherType = Attacher::AttachEngine3D
  Height = 10
  Placement = pos=(0,0,36.15) rot=(0,0,1;0rad)
  Radius = 4
FEATURE [Part::MultiFuse] Fusion034  label="removeToCreteHoleForPlugHousing004"
  Placement = pos=(-42,19,36) rot=(0,1,0;1.5708rad)
  Shapes = -> [Cylinder014,Cylinder015]
FEATURE [Part::Cut] Cut008  label="top004"
  Base = -> Cut004
  Placement = pos=(-1,0,0) rot=(0,0,1;0rad)
  Tool = -> Fusion034
FEATURE [Part::Box] Box005  label="Cube005"
  AttacherType = Attacher::AttachEngine3D
  Height = 28
  Length = 3
  Placement = pos=(110.7,19,22) rot=(0,0,1;0rad)
  Width = 15.7
FEATURE [Part::Cylinder] Cylinder016
  Angle = 360
  AttacherType = Attacher::AttachEngine3D
  Height = 10
  Placement = pos=(0,0,36.15) rot=(0,0,1;0rad)
  Radius = 4
FEATURE [Part::Cylinder] Cylinder017
  Angle = 360
  AttacherType = Attacher::AttachEngine3D
  Height = 20
  Placement = pos=(0,0,36.15) rot=(0,0,1;0rad)
  Radius = 10.3
FEATURE [Part::MultiFuse] Fusion035  label="removeToCreteHoleForPlugHousing005"
  Placement = pos=(70,19,36) rot=(0,1,0;1.5708rad)
  Shapes = -> [Cylinder017,Cylinder016]
FEATURE [Part::Cut] Cut009  label="plugHousingTab001"
  Base = -> Box005
  Placement = pos=(-107.4,-14,0) rot=(0,0,1;0rad)
  Tool = -> Fusion035
FEATURE [Part::Box] Box006  label="Cube006"
  AttacherType = Attacher::AttachEngine3D
  Height = 28
  Length = 3
  Placement = pos=(110.7,19,22) rot=(0,0,1;0rad)
  Width = 15.7
FEATURE [Part::Cylinder] Cylinder018
  Angle = 360
  AttacherType = Attacher::AttachEngine3D
  Height = 10
  Placement = pos=(0,0,36.15) rot=(0,0,1;0rad)
  Radius = 4
FEATURE [Part::Cylinder] Cylinder019
  Angle = 360
  AttacherType = Attacher::AttachEngine3D
  Height = 20
  Placement = pos=(0,0,36.15) rot=(0,0,1;0rad)
  Radius = 10.3
FEATURE [Part::MultiFuse] Fusion036  label="removeToCreteHoleForPlugHousing006"
  Placement = pos=(70,19,36) rot=(0,1,0;1.5708rad)
  Shapes = -> [Cylinder019,Cylinder018]
FEATURE [Part::Cut] Cut010  label="plugHousingTab002"
  Base = -> Box006
  Placement = pos=(-107.4,-14,0) rot=(0,0,1;0rad)
  Tool = -> Fusion036
FEATURE [Part::MultiFuse] Fusion037
  Placement = pos=(9.6,23,0) rot=(0,0,1;3.14159rad)
  Shapes = -> [Cut009,Cut010]
FEATURE [Part::Box] Box  label="Cube"
  AttacherType = Attacher::AttachEngine3D
  Height = 10
  Length = 3
  Placement = pos=(3.3,4,12) rot=(0,0,1;0rad)
  Width = 10
FEATURE [Part::Fillet] Fillet004
  Base = -> Fusion028
  Edges = 1 edges r=2: [Edge25]
FEATURE [Part::Fillet] Fillet005  label="plugHousing046"
  Base = -> Fillet004
  Edges = 1 edges r=2: [Edge8]
FEATURE [Part::Fillet] Fillet006
  Base = -> Box
  Edges = 1 edges r=2: [Edge11]
FEATURE [Part::Box] Box007  label="Cube007"
  AttacherType = Attacher::AttachEngine3D
  Height = 10
  Length = 3
  Placement = pos=(3.3,4,50) rot=(0,0,1;0rad)
  Width = 10
FEATURE [Part::Fillet] Fillet007
  Base = -> Box007
  Edges = 1 edges r=2: [Edge12]
FEATURE [Part::Box] Box008  label="Cube008"
  AttacherType = Attacher::AttachEngine3D
  Height = 28
  Length = 4
  Placement = pos=(5,0,22) rot=(0,0,1;0rad)
  Width = 10
FEATURE [Part::Fillet] Fillet008
  Base = -> Box008
  Edges = 1 edges r=1: [Edge7]
FEATURE [Part::Fillet] Fillet009
  Base = -> Fillet008
  Edges = 1 edges r=2: [Edge5]
FEATURE [Part::Fillet] Fillet010
  Base = -> Fillet009
  Edges = 1 edges r=2: [Edge2]
FEATURE [Sketcher::SketchObject] Sketch009  label="topSketch003"
  FullyConstrained = true
  sketch-geometry (4):
    g0: LineSegment StartX=16.8446 StartY=31.512 StartZ=0 EndX=16.3251 EndY=34.4666 EndZ=0
    g1: ArcOfCircle CenterX=19 CenterY=19.2524 CenterZ=0 NormalX=0 NormalY=0 NormalZ=1 AngleXU=0 Radius=15.4476 StartAngle=1.74483 EndAngle=2.72717
    g2: ArcOfCircle CenterX=19 CenterY=19.2524 CenterZ=0 NormalX=0 NormalY=0 NormalZ=1 AngleXU=0 Radius=12.4476 StartAngle=1.74483 EndAngle=2.73189
    g3: LineSegment StartX=4.86004 StartY=25.4725 StartZ=0 EndX=7.58253 EndY=24.2107 EndZ=0
  constraints (7):
    c: Block(g0)
    c: Coincident(g1,g0)
    c: Coincident(g2,g0)
    c: Coincident(g3,g1)
    c: Coincident(g3,g2)
    c: Block(g1)
    c: Block(g2)
FEATURE [Part::Extrusion] Extrude008
  Base = -> Sketch009
  Dir = (0,0,1)
  DirMode = 2
  FaceMakerClass = Part::FaceMakerBullseye
  LengthFwd = 10
  LengthRev = 0
  Placement = pos=(0,0,31) rot=(0,0,1;0rad)
  Solid = true
  Symmetric = false
FEATURE [Part::Cylinder] Cylinder020
  Angle = 360
  AttacherType = Attacher::AttachEngine3D
  Height = 20
  Placement = pos=(0,0,36.15) rot=(0,0,1;0rad)
  Radius = 8.2
FEATURE [Part::Cylinder] Cylinder021
  Angle = 360
  AttacherType = Attacher::AttachEngine3D
  Height = 10
  Placement = pos=(0,0,36.15) rot=(0,0,1;0rad)
  Radius = 4
FEATURE [Part::MultiFuse] Fusion038  label="removeToCreteHoleForPlugHousing007"
  Placement = pos=(-42,19,36) rot=(0,1,0;1.5708rad)
  Shapes = -> [Cylinder020,Cylinder021]
FEATURE [Part::Cut] Cut011
  Base = -> Extrude008
  Tool = -> Fusion038
FEATURE [Part::Fillet] Fillet011
  Base = -> Cut011
  Edges = 1 edges r=2: [Edge1]
FEATURE [Part::Fillet] Fillet012
  Base = -> Fillet011
  Edges = 1 edges r=2.5: [Edge1]
FEATURE [Part::Fillet] Fillet013
  Base = -> Fillet012
  Edges = 1 edges r=2.5: [Edge2]
FEATURE [Part::Box] Box010  label="Cube010"
  AttacherType = Attacher::AttachEngine3D
  Height = 16
  Length = 8
  Placement = pos=(12.7,31.52,28) rot=(0,0,1;0rad)
  Width = 4
FEATURE [Sketcher::SketchObject] Sketch010  label="topSketch004"
  FullyConstrained = true
  sketch-geometry (4):
    g0: LineSegment StartX=16.8446 StartY=31.512 StartZ=0 EndX=16.3251 EndY=34.4666 EndZ=0
    g1: ArcOfCircle CenterX=19 CenterY=19.2524 CenterZ=0 NormalX=0 NormalY=0 NormalZ=1 AngleXU=0 Radius=15.4476 StartAngle=1.74483 EndAngle=2.72717
    g2: ArcOfCircle CenterX=19 CenterY=19.2524 CenterZ=0 NormalX=0 NormalY=0 NormalZ=1 AngleXU=0 Radius=12.4476 StartAngle=1.74483 EndAngle=2.73189
    g3: LineSegment StartX=4.86004 StartY=25.4725 StartZ=0 EndX=7.58253 EndY=24.2107 EndZ=0
  constraints (7):
    c: Block(g0)
    c: Coincident(g1,g0)
    c: Coincident(g2,g0)
    c: Coincident(g3,g1)
    c: Coincident(g3,g2)
    c: Block(g1)
    c: Block(g2)
FEATURE [Part::Cylinder] Cylinder022
  Angle = 360
  AttacherType = Attacher::AttachEngine3D
  Height = 10
  Placement = pos=(0,0,36.15) rot=(0,0,1;0rad)
  Radius = 4
FEATURE [Sketcher::SketchObject] Sketch011  label="topSketch005"
  FullyConstrained = true
  sketch-geometry (4):
    g0: LineSegment StartX=16.8446 StartY=31.512 StartZ=0 EndX=16.3251 EndY=34.4666 EndZ=0
    g1: ArcOfCircle CenterX=19 CenterY=19.2524 CenterZ=0 NormalX=0 NormalY=0 NormalZ=1 AngleXU=0 Radius=15.4476 StartAngle=1.74483 EndAngle=2.72717
    g2: ArcOfCircle CenterX=19 CenterY=19.2524 CenterZ=0 NormalX=0 NormalY=0 NormalZ=1 AngleXU=0 Radius=12.4476 StartAngle=1.74483 EndAngle=2.73189
    g3: LineSegment StartX=4.86004 StartY=25.4725 StartZ=0 EndX=7.58253 EndY=24.2107 EndZ=0
  constraints (7):
    c: Block(g0)
    c: Coincident(g1,g0)
    c: Coincident(g2,g0)
    c: Coincident(g3,g1)
    c: Coincident(g3,g2)
    c: Block(g1)
    c: Block(g2)
FEATURE [Part::Extrusion] Extrude010
  Base = -> Sketch011
  Dir = (0,0,1)
  DirMode = 2
  FaceMakerClass = Part::FaceMakerBullseye
  LengthFwd = 10.6
  LengthRev = 0
  Placement = pos=(0,0,31) rot=(0,0,1;0rad)
  Solid = true
  Symmetric = false
FEATURE [Part::Cylinder] Cylinder023
  Angle = 360
  AttacherType = Attacher::AttachEngine3D
  Height = 20
  Placement = pos=(0,0,36.15) rot=(0,0,1;0rad)
  Radius = 8.2
FEATURE [Part::MultiFuse] Fusion039  label="removeToCreteHoleForPlugHousing008"
  Placement = pos=(-42,19,36) rot=(0,1,0;1.5708rad)
  Shapes = -> [Cylinder023,Cylinder022]
FEATURE [Part::Cut] Cut012
  Base = -> Extrude010
  Placement = pos=(0,0,-0.3) rot=(0,0,1;0rad)
  Tool = -> Fusion039
FEATURE [Part::Cut] Cut013
  Base = -> Box010
  Tool = -> Cut012
FEATURE [Part::Fillet] Fillet014
  Base = -> Cut013
  Edges = 1 edges r=0.7: [Edge13]
FEATURE [Part::Fillet] Fillet015
  Base = -> Fillet014
  Edges = 1 edges r=0.7: [Edge13]
FEATURE [Part::Fillet] Fillet016
  Base = -> Fillet015
  Edges = 1 edges r=0.7: [Edge16]
FEATURE [Part::Fillet] Fillet017
  Base = -> Fillet016
  Edges = 1 edges r=0.7: [Edge11]
FEATURE [Part::Fillet] Fillet018
  Base = -> Fillet017
  Edges = 1 edges r=0.7: [Edge10]
FEATURE [Part::Fillet] Fillet019
  Base = -> Fillet018
  Edges = 1 edges r=1.2: [Edge5]
FEATURE [Part::Fillet] Fillet020
  Base = -> Fillet019
  Edges = 1 edges r=1.2: [Edge12]
FEATURE [Part::Fillet] Fillet021
  Base = -> Fillet020
  Edges = 1 edges r=2: [Edge1]
  Placement = pos=(0.3,0,0) rot=(0,0,1;0rad)
FEATURE [Part::MultiFuse] Fusion040  label="top005"
  Shapes = -> [Cut008,Fillet021]
FEATURE [Part::MultiFuse] Fusion041  label="wireHolder"
  Shapes = -> [Fusion033,Fillet013]
FEATURE [Part::MultiFuse] Fusion042
  Shapes = -> [Fillet007,Fusion041]
FEATURE [Part::MultiFuse] Fusion043  label="wireHolder001"
  Shapes = -> [Fusion042,Fillet010]
FEATURE [Part::MultiFuse] Fusion044  label="wireHolder002"
  Shapes = -> [Fillet006,Fusion037,Fusion043]
FEATURE [Part::Feature] Face026
  shape: bbox 11 x 6 x 2e-07 mm, 1 faces, 0 solids (baked)
FEATURE [Part::Revolution] Revolve026
  Angle = 360
  Axis = (0,1,0)
  Base = (0,0,0)
  FaceMakerClass = Part::FaceMakerBullseye
  Placement = pos=(30.3,-1,19.7) rot=(0,0,1;0rad)
  Solid = false
  Source = -> Face026
  Symmetric = false
FEATURE [Sketcher::SketchObject] Sketch013  label="topSketch006"
  FullyConstrained = true
  sketch-geometry (13):
    g0: LineSegment StartX=117 StartY=19 StartZ=0 EndX=117 EndY=38 EndZ=0
    g1: ArcOfCircle CenterX=98 CenterY=19 CenterZ=0 NormalX=0 NormalY=0 NormalZ=1 AngleXU=0 Radius=19 StartAngle=5.7297 EndAngle=6.28319
    g2: LineSegment StartX=0 StartY=3 StartZ=0 EndX=0 EndY=19 EndZ=0
    g3: LineSegment StartX=19 StartY=38 StartZ=0 EndX=117 EndY=38 EndZ=0
    g4: ArcOfCircle CenterX=19 CenterY=19 CenterZ=0 NormalX=0 NormalY=0 NormalZ=1 AngleXU=0 Radius=19 StartAngle=1.5708 EndAngle=3.14159
    g5: ArcOfCircle CenterX=19 CenterY=19 CenterZ=0 NormalX=0 NormalY=0 NormalZ=1 AngleXU=0 Radius=16 StartAngle=1.5708 EndAngle=3.14159
    g6: ArcOfCircle CenterX=98 CenterY=19 CenterZ=0 NormalX=0 NormalY=0 NormalZ=1 AngleXU=0 Radius=16 StartAngle=5.60905 EndAngle=6.28319
    g7: LineSegment StartX=114 StartY=19 StartZ=0 EndX=114 EndY=35 EndZ=0
    g8: LineSegment StartX=110.5 StartY=9.01251 StartZ=0 EndX=114.163 EndY=9.01251 EndZ=0
    g9: LineSegment StartX=114 StartY=35 StartZ=0 EndX=19 EndY=35 EndZ=0
    g10: LineSegment StartX=0 StartY=3 StartZ=0 EndX=0 EndY=0 EndZ=0
    g11: LineSegment StartX=3 StartY=0 StartZ=0 EndX=0 EndY=0 EndZ=0
    g12: LineSegment StartX=3 StartY=19 StartZ=0 EndX=3 EndY=0 EndZ=0
  constraints (33):
    c: Vertical(g0)
    c: Distance(g0) = 19
    c: Block(g0)
    c: Coincident(g1,g0)
    c: Block(g1)
    c: Vertical(g2)
    c: Block(g2)
    c: Coincident(g3,g0)
    c: Horizontal(g3)
    c: Distance(g3) = 98
    c: Coincident(g4,g3)
    c: Coincident(g4,g2)
    c: Block(g4)
    c: Coincident(g5,g4)
    c: Coincident(g6,g1)
    c: Block(g6)
    c: Block(g5)
    c: Coincident(g7,g6)
    c: Vertical(g7)
    c: Coincident(g8,g6)
    c: Coincident(g8,g1)
    c: Coincident(g9,g7)
    c: Coincident(g9,g5)
    c: Horizontal(g9)
    c: Tangent(g9,g5)
    c: Coincident(g10,g2)
    c: Distance(g10) = 3
    c: Vertical(g10)
    c: Coincident(g11,g10)
    c: Horizontal(g11)
    c: Coincident(g12,g5)
    c: Coincident(g12,g11)
    c: Vertical(g12)
FEATURE [Part::Extrusion] Extrude011  label="top006"
  Base = -> Sketch013
  Dir = (0,0,1)
  DirMode = 2
  FaceMakerClass = Part::FaceMakerBullseye
  LengthFwd = 72
  LengthRev = 0
  Solid = true
  Symmetric = false
FEATURE [Sketcher::SketchObject] Sketch014
  FullyConstrained = true
  MapMode = 3
  Placement = pos=(0,0,0) rot=(1,0,0;1.5708rad)
  Support = -> [Extrude011]
  sketch-geometry (8):
    g0: Circle CenterX=80.351 CenterY=-67.6202 CenterZ=0 NormalX=0 NormalY=0 NormalZ=1 AngleXU=0 Radius=2
    g1: Circle CenterX=80.351 CenterY=-67.6202 CenterZ=0 NormalX=0 NormalY=0 NormalZ=1 AngleXU=0 Radius=3
    g2: Circle CenterX=80.351 CenterY=-4.92017 CenterZ=0 NormalX=0 NormalY=0 NormalZ=1 AngleXU=0 Radius=2
    g3: Circle CenterX=80.351 CenterY=-4.92017 CenterZ=0 NormalX=0 NormalY=0 NormalZ=1 AngleXU=0 Radius=3
    g4: Circle CenterX=23.851 CenterY=-4.92017 CenterZ=0 NormalX=0 NormalY=0 NormalZ=1 AngleXU=0 Radius=2
    g5: Circle CenterX=23.851 CenterY=-4.92017 CenterZ=0 NormalX=0 NormalY=0 NormalZ=1 AngleXU=0 Radius=3
    g6: Circle CenterX=23.851 CenterY=-67.6202 CenterZ=0 NormalX=0 NormalY=0 NormalZ=1 AngleXU=0 Radius=2
    g7: Circle CenterX=23.851 CenterY=-67.6202 CenterZ=0 NormalX=0 NormalY=0 NormalZ=1 AngleXU=0 Radius=3
  constraints (8):
    c: Block(g3)
    c: Block(g2)
    c: Block(g1)
    c: Block(g0)
    c: Block(g6)
    c: Block(g7)
    c: Block(g4)
    c: Block(g5)
FEATURE [Part::Feature] Face027
  shape: bbox 11 x 6 x 2e-07 mm, 1 faces, 0 solids (baked)
FEATURE [Part::Revolution] Revolve027
  Angle = 360
  Axis = (0,1,0)
  Base = (0,0,0)
  FaceMakerClass = Part::FaceMakerBullseye
  Placement = pos=(30.3,-1,51.7) rot=(0,0,1;0rad)
  Solid = false
  Source = -> Face027
  Symmetric = false
FEATURE [Part::Feature] Face028
  shape: bbox 11 x 6 x 2e-07 mm, 1 faces, 0 solids (baked)
FEATURE [Part::Revolution] Revolve028
  Angle = 360
  Axis = (0,1,0)
  Base = (0,0,0)
  FaceMakerClass = Part::FaceMakerBullseye
  Placement = pos=(62.3,-1,19.7) rot=(0,0,1;0rad)
  Solid = false
  Source = -> Face028
  Symmetric = false
FEATURE [Part::Feature] Face029
  shape: bbox 11 x 6 x 2e-07 mm, 1 faces, 0 solids (baked)
FEATURE [Part::Revolution] Revolve029
  Angle = 360
  Axis = (0,1,0)
  Base = (0,0,0)
  FaceMakerClass = Part::FaceMakerBullseye
  Placement = pos=(62.3,-1,51.7) rot=(0,0,1;0rad)
  Solid = false
  Source = -> Face029
  Symmetric = false
FEATURE [Part::Feature] Wire
  shape: bbox 11 x 5.2 x 2e-07 mm, 0 faces, 0 solids (baked)
FEATURE [Part::Revolution] Revolve030
  Angle = 360
  Axis = (0,1,0)
  Base = (0,0,0)
  FaceMakerClass = Part::FaceMakerBullseye
  Placement = pos=(30.3,38,19.7) rot=(0,0,1;0rad)
  Solid = true
  Source = -> Wire
  Symmetric = false
FEATURE [Part::Feature] Wire001
  shape: bbox 11 x 5.2 x 2e-07 mm, 0 faces, 0 solids (baked)
FEATURE [Part::Revolution] Revolve031
  Angle = 360
  Axis = (0,1,0)
  Base = (0,0,0)
  FaceMakerClass = Part::FaceMakerBullseye
  Placement = pos=(30.3,38,51.7) rot=(0,0,1;0rad)
  Solid = true
  Source = -> Wire001
  Symmetric = false
FEATURE [Part::Feature] Wire002
  shape: bbox 11 x 5.2 x 2e-07 mm, 0 faces, 0 solids (baked)
FEATURE [Part::Revolution] Revolve032
  Angle = 360
  Axis = (0,1,0)
  Base = (0,0,0)
  FaceMakerClass = Part::FaceMakerBullseye
  Placement = pos=(62.3,38,51.7) rot=(0,0,1;0rad)
  Solid = true
  Source = -> Wire002
  Symmetric = false
FEATURE [Part::Feature] Wire003
  shape: bbox 11 x 5.2 x 2e-07 mm, 0 faces, 0 solids (baked)
FEATURE [Part::Revolution] Revolve033
  Angle = 360
  Axis = (0,1,0)
  Base = (0,0,0)
  FaceMakerClass = Part::FaceMakerBullseye
  Placement = pos=(62.3,38,19.7) rot=(0,0,1;0rad)
  Solid = true
  Source = -> Wire003
  Symmetric = false
FEATURE [Part::MultiFuse] Fusion045  label="altRandScrewHousing"
  Shapes = -> [Revolve029,Revolve027,Revolve028,Revolve026]
FEATURE [Part::MultiFuse] Fusion046  label="fanScrewHousing"
  Shapes = -> [Revolve033,Revolve032,Revolve031,Revolve030]
FEATURE [Sketcher::SketchObject] Sketch015
  FullyConstrained = true
  sketch-geometry (17):
    g0: Circle CenterX=-3.5 CenterY=23.5 CenterZ=0 NormalX=0 NormalY=0 NormalZ=1 AngleXU=0 Radius=1
    g1: Circle CenterX=-1 CenterY=15.25 CenterZ=0 NormalX=0 NormalY=0 NormalZ=1 AngleXU=0 Radius=1
    g2: Circle CenterX=-3.5 CenterY=7 CenterZ=0 NormalX=0 NormalY=0 NormalZ=1 AngleXU=0 Radius=1
    g3: BSplineCurve PolesCount=3 KnotsCount=2 Degree=2 IsPeriodic=0
    g4: GeomPoint X=-3.5 Y=23.5 Z=0
    g5: GeomPoint X=-3.5 Y=7 Z=0
    g6: Circle CenterX=-4.8 CenterY=30.5 CenterZ=0 NormalX=0 NormalY=0 NormalZ=1 AngleXU=0 Radius=1
    g7: Circle CenterX=-3.5 CenterY=30.5 CenterZ=0 NormalX=0 NormalY=0 NormalZ=1 AngleXU=0 Radius=1
    g8: Circle CenterX=-3.5 CenterY=29.2 CenterZ=0 NormalX=0 NormalY=0 NormalZ=1 AngleXU=0 Radius=1
    g9: BSplineCurve PolesCount=3 KnotsCount=2 Degree=2 IsPeriodic=0
    g10: GeomPoint X=-4.8 Y=30.5 Z=0
    g11: GeomPoint X=-3.5 Y=29.2 Z=0
    g12: LineSegment StartX=-3.5 StartY=29.2 StartZ=0 EndX=-3.5 EndY=23.5 EndZ=0
    g13: LineSegment StartX=-4.8 StartY=30.5 StartZ=0 EndX=0 EndY=30.5 EndZ=0
    g14: LineSegment StartX=-3.5 StartY=0.3 StartZ=0 EndX=0 EndY=0.3 EndZ=0
    g15: LineSegment StartX=-3.5 StartY=0.3 StartZ=0 EndX=-3.5 EndY=7 EndZ=0
    g16: LineSegment StartX=0 StartY=0.3 StartZ=0 EndX=0 EndY=30.5 EndZ=0
  constraints (34):
    c: Weight(g0) = 1
    c: Equal(g0,g1)
    c: Equal(g0,g2)
    c: InternalAlignment(g0,g3)
    c: InternalAlignment(g1,g3)
    c: InternalAlignment(g2,g3)
    c: InternalAlignment(g4,g3)
    c: InternalAlignment(g5,g3)
    c: Block(g3)
    c: Weight(g6) = 1
    c: Equal(g6,g7)
    c: Equal(g6,g8)
    c: InternalAlignment(g6,g9)
    c: InternalAlignment(g7,g9)
    c: InternalAlignment(g8,g9)
    c: InternalAlignment(g10,g9)
    c: InternalAlignment(g11,g9)
    c: Block(g9)
    c: Coincident(g12,g9)
    c: Coincident(g12,g3)
    c: Vertical(g12)
    c: Coincident(g13,g9)
    c: Horizontal(g13)
    c: Distance(g13) = 4.8
    c: Horizontal(g14)
    c: Block(g14)
    c: Coincident(g15,g14)
    c: Coincident(g15,g3)
    c: Vertical(g15)
    c: Coincident(g16,g14)
    c: Coincident(g16,g13)
    c: Vertical(g16)
    c: Tangent(g16,g1)
    c: Distance(g14) = 3.5
FEATURE [Sketcher::SketchObject] Sketch016
  FullyConstrained = true
  sketch-geometry (16):
    g0: Circle CenterX=-3.5 CenterY=23.5 CenterZ=0 NormalX=0 NormalY=0 NormalZ=1 AngleXU=0 Radius=1
    g1: Circle CenterX=-1 CenterY=15.25 CenterZ=0 NormalX=0 NormalY=0 NormalZ=1 AngleXU=0 Radius=1
    g2: Circle CenterX=-3.5 CenterY=7 CenterZ=0 NormalX=0 NormalY=0 NormalZ=1 AngleXU=0 Radius=1
    g3: BSplineCurve PolesCount=3 KnotsCount=2 Degree=2 IsPeriodic=0
    g4: GeomPoint X=-3.5 Y=23.5 Z=0
    g5: GeomPoint X=-3.5 Y=7 Z=0
    g6: LineSegment StartX=-3.5 StartY=28.2 StartZ=0 EndX=-3.5 EndY=23.5 EndZ=0
    g7: LineSegment StartX=0 StartY=29.5 StartZ=0 EndX=0 EndY=30 EndZ=0
    g8: LineSegment StartX=-3.5 StartY=28.2 StartZ=0 EndX=-3.5 EndY=30 EndZ=0
    g9: LineSegment StartX=0 StartY=30 StartZ=0 EndX=0 EndY=30.5 EndZ=0
    g10: LineSegment StartX=0 StartY=30.5 StartZ=0 EndX=-3.5 EndY=30.5 EndZ=0
    g11: LineSegment StartX=-3.5 StartY=30.5 StartZ=0 EndX=-3.5 EndY=30 EndZ=0
    g12: LineSegment StartX=0 StartY=29.5 StartZ=0 EndX=0 EndY=5 EndZ=0
    g13: LineSegment StartX=-3.5 StartY=0.3 StartZ=0 EndX=-3.5 EndY=7 EndZ=0
    g14: LineSegment StartX=-3.5 StartY=0.3 StartZ=0 EndX=0 EndY=0.3 EndZ=0
    g15: LineSegment StartX=0 StartY=5 StartZ=0 EndX=0 EndY=0.3 EndZ=0
  constraints (39):
    c: Weight(g0) = 1
    c: Equal(g0,g1)
    c: Equal(g0,g2)
    c: InternalAlignment(g0,g3)
    c: InternalAlignment(g1,g3)
    c: InternalAlignment(g2,g3)
    c: InternalAlignment(g4,g3)
    c: InternalAlignment(g5,g3)
    c: Block(g3)
    c: Coincident(g6,g3)
    c: Vertical(g6)
    c: Vertical(g7)
    c: Distance(g7) = 0.5
    c: Coincident(g8,g6)
    c: Vertical(g8)
    c: Block(g6)
    c: Block(g7)
    c: Vertical(g9)
    c: Equal(g7,g9) = 0.5
    c: Block(g9)
    c: Coincident(g9,g7)
    c: Horizontal(g10)
    c: Coincident(g10,g9)
    c: Coincident(g11,g10)
    c: Coincident(g11,g8)
    c: Vertical(g11)
    c: Block(g11)
    c: Coincident(g12,g7)
    c: Vertical(g12)
    c: Coincident(g13,g3)
    c: Vertical(g13)
    c: Distance(g13) = 6.7
    c: Coincident(g14,g13)
    c: Horizontal(g14)
    c: Block(g14)
    c: Coincident(g15,g12)
    c: Coincident(g15,g14)
    c: Vertical(g15)
    c: Block(g15)
FEATURE [Sketcher::SketchObject] Sketch017
  FullyConstrained = true
  sketch-geometry (11):
    g0: LineSegment StartX=-3.5 StartY=1e-16 StartZ=0 EndX=-1.6 EndY=1e-16 EndZ=0
    g1: LineSegment StartX=-1.6 StartY=1e-16 StartZ=0 EndX=-1.6 EndY=1.5 EndZ=0
    g2: LineSegment StartX=-3.5 StartY=1.5 StartZ=0 EndX=-1.6 EndY=1.5 EndZ=0
    g3: LineSegment StartX=-3.5 StartY=1e-16 StartZ=0 EndX=-4.8 EndY=1e-16 EndZ=0
    g4: Circle CenterX=-3.5 CenterY=1.3 CenterZ=0 NormalX=0 NormalY=0 NormalZ=1 AngleXU=0 Radius=1
    g5: Circle CenterX=-3.5 CenterY=1e-16 CenterZ=0 NormalX=0 NormalY=0 NormalZ=1 AngleXU=0 Radius=1
    g6: Circle CenterX=-4.8 CenterY=1e-16 CenterZ=0 NormalX=0 NormalY=0 NormalZ=1 AngleXU=0 Radius=1
    g7: BSplineCurve PolesCount=3 KnotsCount=2 Degree=2 IsPeriodic=0
    g8: GeomPoint X=-3.5 Y=1.3 Z=0
    g9: GeomPoint X=-4.8 Y=1e-16 Z=0
    g10: LineSegment StartX=-3.5 StartY=1.3 StartZ=0 EndX=-3.5 EndY=1.5 EndZ=0
  constraints (24):
    c: Horizontal(g0)
    c: Distance(g0) = 1.9
    c: Block(g0)
    c: Coincident(g1,g0)
    c: Vertical(g1)
    c: Coincident(g2,g1)
    c: Horizontal(g2)
    c: Coincident(g3,g0)
    c: Horizontal(g3)
    c: Distance(g3) = 1.3
    c: Weight(g4) = 1
    c: Equal(g4,g5)
    c: Coincident(g5,g0)
    c: Equal(g4,g6)
    c: Coincident(g7,g3)
    c: InternalAlignment(g4,g7)
    c: InternalAlignment(g5,g7)
    c: InternalAlignment(g6,g7)
    c: InternalAlignment(g8,g7)
    c: InternalAlignment(g9,g7)
    c: Coincident(g10,g7)
    c: Coincident(g10,g2)
    c: Vertical(g10)
    c: Block(g10)
FEATURE [Part::Feature] Face035
  shape: bbox 3.2 x 1.5 x 2e-07 mm, 1 faces, 0 solids (baked)
FEATURE [Part::Revolution] Revolve039  label="backCaseScrewRetainer"
  Angle = 360
  Axis = (0,1,0)
  Base = (0,0,0)
  FaceMakerClass = Part::FaceMakerBullseye
  Placement = pos=(12.5,3,62) rot=(0,0,1;0rad)
  Solid = false
  Source = -> Face035
  Symmetric = false
FEATURE [Part::Feature] Face036
  shape: bbox 3.2 x 1.5 x 2e-07 mm, 1 faces, 0 solids (baked)
FEATURE [Part::Feature] Face039
  shape: bbox 4.8 x 30.2 x 2e-07 mm, 1 faces, 0 solids (baked)
FEATURE [Part::Revolution] Revolve043  label="frontCaseScrewPost002"
  Angle = 360
  Axis = (0,1,0)
  Base = (0,0,0)
  FaceMakerClass = Part::FaceMakerBullseye
  Placement = pos=(89.5,4.5,3.5) rot=(0,0,1;0rad)
  Solid = false
  Source = -> Face039
  Symmetric = false
FEATURE [Part::Feature] Face042
  shape: bbox 4.8 x 30.2 x 2e-07 mm, 1 faces, 0 solids (baked)
FEATURE [Part::Revolution] Revolve046  label="frontCaseScrewPost003"
  Angle = 360
  Axis = (0,1,0)
  Base = (0,0,0)
  FaceMakerClass = Part::FaceMakerBullseye
  Placement = pos=(89.5,4.5,68.5) rot=(0,0,1;0rad)
  Solid = false
  Source = -> Face042
  Symmetric = false
FEATURE [Part::Feature] Face043
  shape: bbox 3.2 x 1.5 x 2e-07 mm, 1 faces, 0 solids (baked)
FEATURE [Part::Revolution] Revolve047  label="frontCaseScrewRetainer002"
  Angle = 360
  Axis = (0,1,0)
  Base = (0,0,0)
  FaceMakerClass = Part::FaceMakerBullseye
  Placement = pos=(89.5,3,68.5) rot=(0,0,1;0rad)
  Solid = false
  Source = -> Face043
  Symmetric = false
FEATURE [Part::Feature] Face044
  shape: bbox 3.2 x 1.5 x 2e-07 mm, 1 faces, 0 solids (baked)
FEATURE [Part::Revolution] Revolve048  label="frontCaseScrewRetainer003"
  Angle = 360
  Axis = (0,1,0)
  Base = (0,0,0)
  FaceMakerClass = Part::FaceMakerBullseye
  Placement = pos=(89.5,3,3.5) rot=(0,0,1;0rad)
  Solid = false
  Source = -> Face044
  Symmetric = false
FEATURE [App::MeasureDistance] Distance002  label="Distance: 1.67 mm"
  Distance = 1.66921
  P1 = (99.2361,4.7524,71.7)
  P2 = (99.2347,6.42161,71.7)
FEATURE [Sketcher::SketchObject] Sketch018
  FullyConstrained = true
  sketch-geometry (7):
    g0: LineSegment StartX=0 StartY=0 StartZ=0 EndX=0 EndY=6 EndZ=0
    g1: Circle CenterX=0 CenterY=0 CenterZ=0 NormalX=0 NormalY=0 NormalZ=1 AngleXU=0 Radius=1
    g2: Circle CenterX=8 CenterY=6 CenterZ=0 NormalX=0 NormalY=0 NormalZ=1 AngleXU=0 Radius=1
    g3: BSplineCurve PolesCount=3 KnotsCount=2 Degree=2 IsPeriodic=0
    g4: GeomPoint X=0 Y=0 Z=0
    g5: GeomPoint X=8 Y=6 Z=0
    g6: LineSegment StartX=0 StartY=6 StartZ=0 EndX=8 EndY=6 EndZ=0
  constraints (14):
    c: Coincident(g0,g-1)
    c: Distance(g0) = 6
    c: Vertical(g0)
    c: Coincident(g3,g0)
    c: Weight(g1) = 1
    c: Equal(g1,g2)
    c: InternalAlignment(g1,g3)
    c: InternalAlignment(g2,g3)
    c: InternalAlignment(g4,g3)
    c: InternalAlignment(g5,g3)
    c: Block(g3)
    c: Coincident(g6,g0)
    c: Coincident(g6,g3)
    c: Horizontal(g6)
FEATURE [Part::Extrusion] Extrude012  label="caseScrewPillarBracket"
  Base = -> Sketch018
  Dir = (0,0,1)
  DirMode = 2
  FaceMakerClass = Part::FaceMakerBullseye
  LengthFwd = 2.4
  LengthRev = 0
  Placement = pos=(15.76,29,8.8) rot=(0,1,0;0rad)
  Solid = true
  Symmetric = false
FEATURE [Sketcher::SketchObject] Sketch019
  FullyConstrained = true
  sketch-geometry (7):
    g0: LineSegment StartX=0 StartY=0 StartZ=0 EndX=0 EndY=6 EndZ=0
    g1: Circle CenterX=0 CenterY=0 CenterZ=0 NormalX=0 NormalY=0 NormalZ=1 AngleXU=0 Radius=1
    g2: Circle CenterX=8 CenterY=6 CenterZ=0 NormalX=0 NormalY=0 NormalZ=1 AngleXU=0 Radius=1
    g3: BSplineCurve PolesCount=3 KnotsCount=2 Degree=2 IsPeriodic=0
    g4: GeomPoint X=0 Y=0 Z=0
    g5: GeomPoint X=8 Y=6 Z=0
    g6: LineSegment StartX=0 StartY=6 StartZ=0 EndX=8 EndY=6 EndZ=0
  constraints (14):
    c: Coincident(g0,g-1)
    c: Distance(g0) = 6
    c: Vertical(g0)
    c: Coincident(g3,g0)
    c: Weight(g1) = 1
    c: Equal(g1,g2)
    c: InternalAlignment(g1,g3)
    c: InternalAlignment(g2,g3)
    c: InternalAlignment(g4,g3)
    c: InternalAlignment(g5,g3)
    c: Block(g3)
    c: Coincident(g6,g0)
    c: Coincident(g6,g3)
    c: Horizontal(g6)
FEATURE [Part::Extrusion] Extrude013  label="caseScrewPillarBracket001"
  Base = -> Sketch019
  Dir = (0,0,1)
  DirMode = 2
  FaceMakerClass = Part::FaceMakerBullseye
  LengthFwd = 2.4
  LengthRev = 0
  Placement = pos=(15.76,29,60.8) rot=(0,0,1;0rad)
  Solid = true
  Symmetric = false
FEATURE [Sketcher::SketchObject] Sketch020
  FullyConstrained = true
  sketch-geometry (7):
    g0: LineSegment StartX=0 StartY=0 StartZ=0 EndX=0 EndY=6 EndZ=0
    g1: Circle CenterX=0 CenterY=0 CenterZ=0 NormalX=0 NormalY=0 NormalZ=1 AngleXU=0 Radius=1
    g2: Circle CenterX=8 CenterY=6 CenterZ=0 NormalX=0 NormalY=0 NormalZ=1 AngleXU=0 Radius=1
    g3: BSplineCurve PolesCount=3 KnotsCount=2 Degree=2 IsPeriodic=0
    g4: GeomPoint X=0 Y=0 Z=0
    g5: GeomPoint X=8 Y=6 Z=0
    g6: LineSegment StartX=0 StartY=6 StartZ=0 EndX=8 EndY=6 EndZ=0
  constraints (14):
    c: Coincident(g0,g-1)
    c: Distance(g0) = 6
    c: Vertical(g0)
    c: Coincident(g3,g0)
    c: Weight(g1) = 1
    c: Equal(g1,g2)
    c: InternalAlignment(g1,g3)
    c: InternalAlignment(g2,g3)
    c: InternalAlignment(g4,g3)
    c: InternalAlignment(g5,g3)
    c: Block(g3)
    c: Coincident(g6,g0)
    c: Coincident(g6,g3)
    c: Horizontal(g6)
FEATURE [Part::Extrusion] Extrude014  label="caseScrewPillarBracket002"
  Base = -> Sketch020
  Dir = (0,0,1)
  DirMode = 2
  FaceMakerClass = Part::FaceMakerBullseye
  LengthFwd = 2.4
  LengthRev = 0
  Placement = pos=(13.7,29,13.26) rot=(0,-1,0;1.5708rad)
  Solid = true
  Symmetric = false
FEATURE [Sketcher::SketchObject] Sketch021
  FullyConstrained = true
  sketch-geometry (7):
    g0: LineSegment StartX=0 StartY=0 StartZ=0 EndX=0 EndY=6 EndZ=0
    g1: Circle CenterX=0 CenterY=0 CenterZ=0 NormalX=0 NormalY=0 NormalZ=1 AngleXU=0 Radius=1
    g2: Circle CenterX=8 CenterY=6 CenterZ=0 NormalX=0 NormalY=0 NormalZ=1 AngleXU=0 Radius=1
    g3: BSplineCurve PolesCount=3 KnotsCount=2 Degree=2 IsPeriodic=0
    g4: GeomPoint X=0 Y=0 Z=0
    g5: GeomPoint X=8 Y=6 Z=0
    g6: LineSegment StartX=0 StartY=6 StartZ=0 EndX=8 EndY=6 EndZ=0
  constraints (14):
    c: Coincident(g0,g-1)
    c: Distance(g0) = 6
    c: Vertical(g0)
    c: Coincident(g3,g0)
    c: Weight(g1) = 1
    c: Equal(g1,g2)
    c: InternalAlignment(g1,g3)
    c: InternalAlignment(g2,g3)
    c: InternalAlignment(g4,g3)
    c: InternalAlignment(g5,g3)
    c: Block(g3)
    c: Coincident(g6,g0)
    c: Coincident(g6,g3)
    c: Horizontal(g6)
FEATURE [Part::Extrusion] Extrude015  label="caseScrewPillarBracket003"
  Base = -> Sketch021
  Dir = (0,0,1)
  DirMode = 2
  FaceMakerClass = Part::FaceMakerBullseye
  LengthFwd = 2.4
  LengthRev = 0
  Placement = pos=(11.3,29,58.74) rot=(0,1,0;1.5708rad)
  Solid = true
  Symmetric = false
FEATURE [Sketcher::SketchObject] Sketch022
  FullyConstrained = true
  sketch-geometry (7):
    g0: LineSegment StartX=0 StartY=0 StartZ=0 EndX=0 EndY=6 EndZ=0
    g1: Circle CenterX=0 CenterY=0 CenterZ=0 NormalX=0 NormalY=0 NormalZ=1 AngleXU=0 Radius=1
    g2: Circle CenterX=8 CenterY=6 CenterZ=0 NormalX=0 NormalY=0 NormalZ=1 AngleXU=0 Radius=1
    g3: BSplineCurve PolesCount=3 KnotsCount=2 Degree=2 IsPeriodic=0
    g4: GeomPoint X=0 Y=0 Z=0
    g5: GeomPoint X=8 Y=6 Z=0
    g6: LineSegment StartX=0 StartY=6 StartZ=0 EndX=8 EndY=6 EndZ=0
  constraints (14):
    c: Coincident(g0,g-1)
    c: Distance(g0) = 6
    c: Vertical(g0)
    c: Coincident(g3,g0)
    c: Weight(g1) = 1
    c: Equal(g1,g2)
    c: InternalAlignment(g1,g3)
    c: InternalAlignment(g2,g3)
    c: InternalAlignment(g4,g3)
    c: InternalAlignment(g5,g3)
    c: Block(g3)
    c: Coincident(g6,g0)
    c: Coincident(g6,g3)
    c: Horizontal(g6)
FEATURE [Part::Extrusion] Extrude016  label="caseScrewPillarBracket004"
  Base = -> Sketch022
  Dir = (0,0,1)
  DirMode = 2
  FaceMakerClass = Part::FaceMakerBullseye
  LengthFwd = 2.4
  LengthRev = 0
  Placement = pos=(88.3,29,65.23) rot=(0,1,0;1.5708rad)
  Solid = true
  Symmetric = false
FEATURE [Sketcher::SketchObject] Sketch023
  FullyConstrained = true
  sketch-geometry (7):
    g0: LineSegment StartX=0 StartY=0 StartZ=0 EndX=0 EndY=6 EndZ=0
    g1: Circle CenterX=0 CenterY=0 CenterZ=0 NormalX=0 NormalY=0 NormalZ=1 AngleXU=0 Radius=1
    g2: Circle CenterX=8 CenterY=6 CenterZ=0 NormalX=0 NormalY=0 NormalZ=1 AngleXU=0 Radius=1
    g3: BSplineCurve PolesCount=3 KnotsCount=2 Degree=2 IsPeriodic=0
    g4: GeomPoint X=0 Y=0 Z=0
    g5: GeomPoint X=8 Y=6 Z=0
    g6: LineSegment StartX=0 StartY=6 StartZ=0 EndX=8 EndY=6 EndZ=0
  constraints (14):
    c: Coincident(g0,g-1)
    c: Distance(g0) = 6
    c: Vertical(g0)
    c: Coincident(g3,g0)
    c: Weight(g1) = 1
    c: Equal(g1,g2)
    c: InternalAlignment(g1,g3)
    c: InternalAlignment(g2,g3)
    c: InternalAlignment(g4,g3)
    c: InternalAlignment(g5,g3)
    c: Block(g3)
    c: Coincident(g6,g0)
    c: Coincident(g6,g3)
    c: Horizontal(g6)
FEATURE [Part::Extrusion] Extrude017  label="caseScrewPillarBracket005"
  Base = -> Sketch023
  Dir = (0,0,1)
  DirMode = 2
  FaceMakerClass = Part::FaceMakerBullseye
  LengthFwd = 2.4
  LengthRev = 0
  Placement = pos=(90.7,29,6.77) rot=(0,-1,0;1.5708rad)
  Solid = true
  Symmetric = false
FEATURE [Sketcher::SketchObject] Sketch024
  FullyConstrained = true
  sketch-geometry (7):
    g0: LineSegment StartX=0 StartY=0 StartZ=0 EndX=0 EndY=6 EndZ=0
    g1: Circle CenterX=0 CenterY=0 CenterZ=0 NormalX=0 NormalY=0 NormalZ=1 AngleXU=0 Radius=1
    g2: Circle CenterX=8 CenterY=6 CenterZ=0 NormalX=0 NormalY=0 NormalZ=1 AngleXU=0 Radius=1
    g3: BSplineCurve PolesCount=3 KnotsCount=2 Degree=2 IsPeriodic=0
    g4: GeomPoint X=0 Y=0 Z=0
    g5: GeomPoint X=8 Y=6 Z=0
    g6: LineSegment StartX=0 StartY=6 StartZ=0 EndX=8 EndY=6 EndZ=0
  constraints (14):
    c: Coincident(g0,g-1)
    c: Distance(g0) = 6
    c: Vertical(g0)
    c: Coincident(g3,g0)
    c: Weight(g1) = 1
    c: Equal(g1,g2)
    c: InternalAlignment(g1,g3)
    c: InternalAlignment(g2,g3)
    c: InternalAlignment(g4,g3)
    c: InternalAlignment(g5,g3)
    c: Block(g3)
    c: Coincident(g6,g0)
    c: Coincident(g6,g3)
    c: Horizontal(g6)
FEATURE [Part::Extrusion] Extrude018  label="caseScrewPillarBracket006"
  Base = -> Sketch024
  Dir = (0,0,1)
  DirMode = 2
  FaceMakerClass = Part::FaceMakerBullseye
  LengthFwd = 2.4
  LengthRev = 0
  Placement = pos=(103.7,29,6.77) rot=(0,-1,0;1.5708rad)
  Solid = true
  Symmetric = false
FEATURE [Sketcher::SketchObject] Sketch025
  FullyConstrained = true
  sketch-geometry (7):
    g0: LineSegment StartX=0 StartY=0 StartZ=0 EndX=0 EndY=6 EndZ=0
    g1: Circle CenterX=0 CenterY=0 CenterZ=0 NormalX=0 NormalY=0 NormalZ=1 AngleXU=0 Radius=1
    g2: Circle CenterX=8 CenterY=6 CenterZ=0 NormalX=0 NormalY=0 NormalZ=1 AngleXU=0 Radius=1
    g3: BSplineCurve PolesCount=3 KnotsCount=2 Degree=2 IsPeriodic=0
    g4: GeomPoint X=0 Y=0 Z=0
    g5: GeomPoint X=8 Y=6 Z=0
    g6: LineSegment StartX=0 StartY=6 StartZ=0 EndX=8 EndY=6 EndZ=0
  constraints (14):
    c: Coincident(g0,g-1)
    c: Distance(g0) = 6
    c: Vertical(g0)
    c: Coincident(g3,g0)
    c: Weight(g1) = 1
    c: Equal(g1,g2)
    c: InternalAlignment(g1,g3)
    c: InternalAlignment(g2,g3)
    c: InternalAlignment(g4,g3)
    c: InternalAlignment(g5,g3)
    c: Block(g3)
    c: Coincident(g6,g0)
    c: Coincident(g6,g3)
    c: Horizontal(g6)
FEATURE [Part::Extrusion] Extrude019  label="caseScrewPillarBracket007"
  Base = -> Sketch025
  Dir = (0,0,1)
  DirMode = 2
  FaceMakerClass = Part::FaceMakerBullseye
  LengthFwd = 2.4
  LengthRev = 0
  Placement = pos=(101.3,29,65.23) rot=(0,1,0;1.5708rad)
  Solid = true
  Symmetric = false
FEATURE [Part::Box] Box011  label="frontCaseScrewPillarBracket"
  AttacherType = Attacher::AttachEngine3D
  Height = 2.4
  Length = 16
  Placement = pos=(87,28,2.3) rot=(0,0,1;0rad)
  Width = 7
FEATURE [Part::Box] Box012  label="frontCaseScrewPillarBracket001"
  AttacherType = Attacher::AttachEngine3D
  Height = 2.4
  Length = 16
  Placement = pos=(87,28,67.3) rot=(0,0,1;0rad)
  Width = 7
FEATURE [Sketcher::SketchObject] Sketch026
  FullyConstrained = true
  sketch-geometry (17):
    g0: Circle CenterX=-3.5 CenterY=23.5 CenterZ=0 NormalX=0 NormalY=0 NormalZ=1 AngleXU=0 Radius=1
    g1: Circle CenterX=-1 CenterY=15.25 CenterZ=0 NormalX=0 NormalY=0 NormalZ=1 AngleXU=0 Radius=1
    g2: Circle CenterX=-3.5 CenterY=7 CenterZ=0 NormalX=0 NormalY=0 NormalZ=1 AngleXU=0 Radius=1
    g3: BSplineCurve PolesCount=3 KnotsCount=2 Degree=2 IsPeriodic=0
    g4: GeomPoint X=-3.5 Y=23.5 Z=0
    g5: GeomPoint X=-3.5 Y=7 Z=0
    g6: Circle CenterX=-4.8 CenterY=30.5 CenterZ=0 NormalX=0 NormalY=0 NormalZ=1 AngleXU=0 Radius=1
    g7: Circle CenterX=-3.5 CenterY=30.5 CenterZ=0 NormalX=0 NormalY=0 NormalZ=1 AngleXU=0 Radius=1
    g8: Circle CenterX=-3.5 CenterY=29.2 CenterZ=0 NormalX=0 NormalY=0 NormalZ=1 AngleXU=0 Radius=1
    g9: BSplineCurve PolesCount=3 KnotsCount=2 Degree=2 IsPeriodic=0
    g10: GeomPoint X=-4.8 Y=30.5 Z=0
    g11: GeomPoint X=-3.5 Y=29.2 Z=0
    g12: LineSegment StartX=-3.5 StartY=29.2 StartZ=0 EndX=-3.5 EndY=23.5 EndZ=0
    g13: LineSegment StartX=-4.8 StartY=30.5 StartZ=0 EndX=0 EndY=30.5 EndZ=0
    g14: LineSegment StartX=-3.5 StartY=5 StartZ=0 EndX=-3.5 EndY=7 EndZ=0
    g15: LineSegment StartX=0 StartY=5 StartZ=0 EndX=0 EndY=30.5 EndZ=0
    g16: LineSegment StartX=-3.5 StartY=5 StartZ=0 EndX=0 EndY=5 EndZ=0
  constraints (33):
    c: Weight(g0) = 1
    c: Equal(g0,g1)
    c: Equal(g0,g2)
    c: InternalAlignment(g0,g3)
    c: InternalAlignment(g1,g3)
    c: InternalAlignment(g2,g3)
    c: InternalAlignment(g4,g3)
    c: InternalAlignment(g5,g3)
    c: Block(g3)
    c: Weight(g6) = 1
    c: Equal(g6,g7)
    c: Equal(g6,g8)
    c: InternalAlignment(g6,g9)
    c: InternalAlignment(g7,g9)
    c: InternalAlignment(g8,g9)
    c: InternalAlignment(g10,g9)
    c: InternalAlignment(g11,g9)
    c: Block(g9)
    c: Coincident(g12,g9)
    c: Coincident(g12,g3)
    c: Vertical(g12)
    c: Coincident(g13,g9)
    c: Horizontal(g13)
    c: Distance(g13) = 4.8
    c: Coincident(g14,g3)
    c: Vertical(g14)
    c: Coincident(g15,g13)
    c: Vertical(g15)
    c: Tangent(g15,g1)
    c: Distance(g14) = 2
    c: Coincident(g16,g14)
    c: Horizontal(g16)
    c: Coincident(g15,g16)
FEATURE [Part::Feature] Face050
  shape: bbox 4.8 x 25.5 x 2e-07 mm, 1 faces, 0 solids (baked)
FEATURE [Part::Revolution] Revolve054  label="moreFrontCaseScrewPost001"
  Angle = 360
  Axis = (0,1,0)
  Base = (0,0,0)
  FaceMakerClass = Part::FaceMakerBullseye
  Placement = pos=(102.5,4.5,3.5) rot=(0,0,1;0rad)
  Solid = false
  Source = -> Face050
  Symmetric = false
FEATURE [Part::Feature] Face051
  shape: bbox 4.8 x 25.5 x 2e-07 mm, 1 faces, 0 solids (baked)
FEATURE [Part::Revolution] Revolve055  label="moreFrontCaseScrewPost002"
  Angle = 360
  Axis = (0,1,0)
  Base = (0,0,0)
  FaceMakerClass = Part::FaceMakerBullseye
  Placement = pos=(102.5,4.5,68.5) rot=(0,0,1;0rad)
  Solid = false
  Source = -> Face051
  Symmetric = false
FEATURE [Sketcher::SketchObject] Sketch027
  FullyConstrained = true
  sketch-geometry (10):
    g0: LineSegment StartX=-1.6 StartY=4.7 StartZ=0 EndX=-1.6 EndY=1.7 EndZ=0
    g1: LineSegment StartX=-3.5 StartY=4.7 StartZ=0 EndX=-1.6 EndY=4.7 EndZ=0
    g2: LineSegment StartX=-1.6 StartY=1.7 StartZ=0 EndX=-1.6 EndY=1.5 EndZ=0
    g3: LineSegment StartX=-1.6 StartY=1.5 StartZ=0 EndX=-5.2 EndY=1.5 EndZ=0
    g4: Circle CenterX=-3.5 CenterY=4.7 CenterZ=0 NormalX=0 NormalY=0 NormalZ=1 AngleXU=0 Radius=1
    g5: Circle CenterX=-3.59627 CenterY=2.99743 CenterZ=0 NormalX=0 NormalY=0 NormalZ=1 AngleXU=0 Radius=1
    g6: Circle CenterX=-5.2 CenterY=1.5 CenterZ=0 NormalX=0 NormalY=0 NormalZ=1 AngleXU=0 Radius=1
    g7: BSplineCurve PolesCount=3 KnotsCount=2 Degree=2 IsPeriodic=0
    g8: GeomPoint X=-3.5 Y=4.7 Z=0
    g9: GeomPoint X=-5.2 Y=1.5 Z=0
  constraints (23):
    c: Vertical(g0)
    c: Distance(g0) = 3
    c: Coincident(g1,g0)
    c: Horizontal(g1)
    c: Block(g0)
    c: Block(g1)
    c: Coincident(g2,g0)
    c: Vertical(g2)
    c: Distance(g2) = 0.2
    c: Coincident(g3,g2)
    c: Horizontal(g3)
    c: Block(g3)
    c: Coincident(g7,g1)
    c: Weight(g4) = 1
    c: Equal(g4,g5)
    c: Equal(g4,g6)
    c: Coincident(g7,g3)
    c: InternalAlignment(g4,g7)
    c: InternalAlignment(g5,g7)
    c: InternalAlignment(g6,g7)
    c: InternalAlignment(g8,g7)
    c: InternalAlignment(g9,g7)
    c: Block(g7)
FEATURE [Sketcher::SketchObject] Sketch028
  FullyConstrained = true
  sketch-geometry (18):
    g0: LineSegment StartX=0 StartY=3e-16 StartZ=0 EndX=0 EndY=1.7 EndZ=0
    g1: LineSegment StartX=-3.5 StartY=0 StartZ=0 EndX=-3.5 EndY=0.9 EndZ=0
    g2: Circle CenterX=-2.7 CenterY=1.7 CenterZ=0 NormalX=0 NormalY=0 NormalZ=1 AngleXU=0 Radius=1
    g3: Circle CenterX=-3.5 CenterY=1.7 CenterZ=0 NormalX=0 NormalY=0 NormalZ=1 AngleXU=0 Radius=1
    g4: Circle CenterX=-3.5 CenterY=0.9 CenterZ=0 NormalX=0 NormalY=0 NormalZ=1 AngleXU=0 Radius=1
    g5: BSplineCurve PolesCount=3 KnotsCount=2 Degree=2 IsPeriodic=0
    g6: GeomPoint X=-2.7 Y=1.7 Z=0
    g7: GeomPoint X=-3.5 Y=0.9 Z=0
    g8: LineSegment StartX=-3.5 StartY=0 StartZ=0 EndX=-3.5 EndY=-7 EndZ=0
    g9: LineSegment StartX=0 StartY=3e-16 StartZ=0 EndX=0 EndY=-7 EndZ=0
    g10: LineSegment StartX=-3.5 StartY=-7 StartZ=0 EndX=0 EndY=-7 EndZ=0
    g11: LineSegment StartX=-2.7 StartY=1.7 StartZ=0 EndX=-1.6 EndY=1.7 EndZ=0
    g12: LineSegment StartX=0 StartY=1.7 StartZ=0 EndX=0 EndY=4.5 EndZ=0
    g13: LineSegment StartX=0 StartY=4.5 StartZ=0 EndX=0 EndY=10.8 EndZ=0
    g14: LineSegment StartX=0 StartY=10.8 StartZ=0 EndX=-2 EndY=10.8 EndZ=0
    g15: LineSegment StartX=-1.6 StartY=4.7 StartZ=0 EndX=-1.6 EndY=1.7 EndZ=0
    g16: LineSegment StartX=-1.6 StartY=4.7 StartZ=0 EndX=-2 EndY=4.7 EndZ=0
    g17: LineSegment StartX=-2 StartY=4.7 StartZ=0 EndX=-2 EndY=10.8 EndZ=0
  constraints (44):
    c: Vertical(g0)
    c: Vertical(g1)
    c: Distance(g1) = 0.9
    c: Block(g0)
    c: Distance(g0) = 1.7
    c: Weight(g2) = 1
    c: Equal(g2,g3)
    c: Equal(g2,g4)
    c: Coincident(g5,g1)
    c: InternalAlignment(g2,g5)
    c: InternalAlignment(g3,g5)
    c: InternalAlignment(g4,g5)
    c: InternalAlignment(g6,g5)
    c: InternalAlignment(g7,g5)
    c: Block(g5)
    c: Coincident(g8,g1)
    c: Vertical(g8)
    c: Distance(g8) = 7
    c: Vertical(g9)
    c: Equal(g8,g9) = 7
    c: Coincident(g9,g0)
    c: Coincident(g10,g8)
    c: Coincident(g10,g9)
    c: Horizontal(g10)
    c: Coincident(g11,g5)
    c: Horizontal(g11)
    c: Coincident(g12,g0)
    c: Vertical(g12)
    c: Distance(g12) = 2.8
    c: Coincident(g13,g12)
    c: Vertical(g13)
    c: Distance(g13) = 6.3
    c: Coincident(g14,g13)
    c: Horizontal(g14)
    c: Distance(g14) = 2
    c: Vertical(g15)
    c: Distance(g15) = 3
    c: Block(g11)
    c: Coincident(g15,g11)
    c: Coincident(g16,g15)
    c: Horizontal(g16)
    c: Coincident(g17,g16)
    c: Coincident(g17,g14)
    c: Vertical(g17)
FEATURE [Part::Revolution] Revolve040  label="backCaseScrewRetainer001"
  Angle = 360
  Axis = (0,1,0)
  Base = (0,0,0)
  FaceMakerClass = Part::FaceMakerBullseye
  Placement = pos=(12.5,3,10) rot=(0,0,1;0rad)
  Solid = false
  Source = -> Face036
  Symmetric = false
FEATURE [Part::Feature] Face055
  shape: bbox 3.5 x 30.2 x 2e-07 mm, 1 faces, 0 solids (baked)
FEATURE [Part::Revolution] Revolve059  label="backCaseScrewPost"
  Angle = 360
  Axis = (0,1,0)
  Base = (0,0,0)
  FaceMakerClass = Part::FaceMakerBullseye
  Placement = pos=(12.5,4.5,10) rot=(0,0,1;0rad)
  Solid = false
  Source = -> Face055
  Symmetric = false
FEATURE [Part::Feature] Face056
  shape: bbox 3.5 x 30.2 x 2e-07 mm, 1 faces, 0 solids (baked)
FEATURE [Part::Revolution] Revolve060  label="backCaseScrewPost001"
  Angle = 360
  Axis = (0,1,0)
  Base = (0,0,0)
  FaceMakerClass = Part::FaceMakerBullseye
  Placement = pos=(12.5,4.5,62) rot=(0,0,1;0rad)
  Solid = false
  Source = -> Face056
  Symmetric = false
FEATURE [Part::Feature] Face057
  shape: bbox 3.5 x 17.8 x 2e-07 mm, 1 faces, 0 solids (baked)
FEATURE [Part::Revolution] Revolve061  label="removeToCreateScrewAndThreadedInsertHole"
  Angle = 360
  Axis = (0,1,0)
  Base = (0,0,0)
  FaceMakerClass = Part::FaceMakerBullseye
  Placement = pos=(12.5,0,10) rot=(0,0,1;0rad)
  Solid = false
  Source = -> Face057
  Symmetric = false
FEATURE [Part::Feature] Face058
  shape: bbox 3.5 x 17.8 x 2e-07 mm, 1 faces, 0 solids (baked)
FEATURE [Part::Revolution] Revolve062  label="removeToCreateScrewAndThreadedInsertHole001"
  Angle = 360
  Axis = (0,1,0)
  Base = (0,0,0)
  FaceMakerClass = Part::FaceMakerBullseye
  Placement = pos=(12.5,0,62) rot=(0,0,1;0rad)
  Solid = false
  Source = -> Face058
  Symmetric = false
FEATURE [Part::Feature] Face059
  shape: bbox 3.5 x 17.8 x 2e-07 mm, 1 faces, 0 solids (baked)
FEATURE [Part::Revolution] Revolve063  label="removeToCreateScrewAndThreadedInsertHole002"
  Angle = 360
  Axis = (0,1,0)
  Base = (0,0,0)
  FaceMakerClass = Part::FaceMakerBullseye
  Placement = pos=(89.5,0,68.5) rot=(0,0,1;0rad)
  Solid = false
  Source = -> Face059
  Symmetric = false
FEATURE [Part::Feature] Face060
  shape: bbox 3.5 x 17.8 x 2e-07 mm, 1 faces, 0 solids (baked)
FEATURE [Part::Revolution] Revolve064  label="removeToCreateScrewAndThreadedInsertHole003"
  Angle = 360
  Axis = (0,1,0)
  Base = (0,0,0)
  FaceMakerClass = Part::FaceMakerBullseye
  Placement = pos=(89.5,0,3.5) rot=(0,0,1;0rad)
  Solid = false
  Source = -> Face060
  Symmetric = false
FEATURE [Part::Feature] Face061
  shape: bbox 3.5 x 17.8 x 2e-07 mm, 1 faces, 0 solids (baked)
FEATURE [Part::Revolution] Revolve065  label="removeToCreateScrewAndThreadedInsertHole004"
  Angle = 360
  Axis = (0,1,0)
  Base = (0,0,0)
  FaceMakerClass = Part::FaceMakerBullseye
  Placement = pos=(102.5,4.7,3.5) rot=(0,0,1;0rad)
  Solid = false
  Source = -> Face061
  Symmetric = false
FEATURE [Part::Feature] Face062
  shape: bbox 3.5 x 17.8 x 2e-07 mm, 1 faces, 0 solids (baked)
FEATURE [Part::Revolution] Revolve066  label="removeToCreateScrewAndThreadedInsertHole005"
  Angle = 360
  Axis = (0,1,0)
  Base = (0,0,0)
  FaceMakerClass = Part::FaceMakerBullseye
  Placement = pos=(102.5,4.7,68.5) rot=(0,0,1;0rad)
  Solid = false
  Source = -> Face062
  Symmetric = false
FEATURE [Part::MultiFuse] Fusion047  label="makeHoles"
  Shapes = -> [Revolve066,Revolve065,Revolve064,Revolve063,Revolve062,Revolve061]
FEATURE [Part::Feature] Face063
  shape: bbox 3.6 x 3.2 x 2e-07 mm, 1 faces, 0 solids (baked)
FEATURE [Part::Revolution] Revolve067  label="moreFrontCaseScrewRetainer002"
  Angle = 360
  Axis = (0,1,0)
  Base = (0,0,0)
  FaceMakerClass = Part::FaceMakerBullseye
  Placement = pos=(102.5,4.5,68.5) rot=(0,0,1;0rad)
  Solid = false
  Source = -> Face063
  Symmetric = false
FEATURE [Part::Feature] Face064
  shape: bbox 3.6 x 3.2 x 2e-07 mm, 1 faces, 0 solids (baked)
FEATURE [Part::Revolution] Revolve068  label="moreFrontCaseScrewRetainer003"
  Angle = 360
  Axis = (0,1,0)
  Base = (0,0,0)
  FaceMakerClass = Part::FaceMakerBullseye
  Placement = pos=(102.5,4.5,3.5) rot=(0,0,1;0rad)
  Solid = false
  Source = -> Face064
  Symmetric = false
FEATURE [Part::Feature] Face065
  shape: bbox 3.5 x 17.8 x 2e-07 mm, 1 faces, 0 solids (baked)
FEATURE [Part::Revolution] Revolve069  label="removeToCreateScrewAndThreadedInsertHole006"
  Angle = 360
  Axis = (0,1,0)
  Base = (0,0,0)
  FaceMakerClass = Part::FaceMakerBullseye
  Placement = pos=(12.5,0,10) rot=(0,0,1;0rad)
  Solid = false
  Source = -> Face065
  Symmetric = false
FEATURE [Part::Feature] Face066
  shape: bbox 3.5 x 17.8 x 2e-07 mm, 1 faces, 0 solids (baked)
FEATURE [Part::Revolution] Revolve070  label="removeToCreateScrewAndThreadedInsertHole007"
  Angle = 360
  Axis = (0,1,0)
  Base = (0,0,0)
  FaceMakerClass = Part::FaceMakerBullseye
  Placement = pos=(12.5,0,62) rot=(0,0,1;0rad)
  Solid = false
  Source = -> Face066
  Symmetric = false
FEATURE [Part::Feature] Face067
  shape: bbox 3.5 x 17.8 x 2e-07 mm, 1 faces, 0 solids (baked)
FEATURE [Part::Revolution] Revolve071  label="removeToCreateScrewAndThreadedInsertHole008"
  Angle = 360
  Axis = (0,1,0)
  Base = (0,0,0)
  FaceMakerClass = Part::FaceMakerBullseye
  Placement = pos=(89.5,0,68.5) rot=(0,0,1;0rad)
  Solid = false
  Source = -> Face067
  Symmetric = false
FEATURE [Part::Feature] Face068
  shape: bbox 3.5 x 17.8 x 2e-07 mm, 1 faces, 0 solids (baked)
FEATURE [Part::Revolution] Revolve072  label="removeToCreateScrewAndThreadedInsertHole009"
  Angle = 360
  Axis = (0,1,0)
  Base = (0,0,0)
  FaceMakerClass = Part::FaceMakerBullseye
  Placement = pos=(89.5,0,3.5) rot=(0,0,1;0rad)
  Solid = false
  Source = -> Face068
  Symmetric = false
FEATURE [Part::Feature] Face069
  shape: bbox 3.5 x 17.8 x 2e-07 mm, 1 faces, 0 solids (baked)
FEATURE [Part::Feature] Face070
  shape: bbox 3.5 x 17.8 x 2e-07 mm, 1 faces, 0 solids (baked)
FEATURE [Part::Revolution] Revolve073  label="removeToCreateScrewAndThreadedInsertHole010"
  Angle = 360
  Axis = (0,1,0)
  Base = (0,0,0)
  FaceMakerClass = Part::FaceMakerBullseye
  Placement = pos=(102.5,4.7,3.5) rot=(0,0,1;0rad)
  Solid = false
  Source = -> Face069
  Symmetric = false
FEATURE [Part::Revolution] Revolve074  label="removeToCreateScrewAndThreadedInsertHole011"
  Angle = 360
  Axis = (0,1,0)
  Base = (0,0,0)
  FaceMakerClass = Part::FaceMakerBullseye
  Placement = pos=(102.5,4.7,68.5) rot=(0,0,1;0rad)
  Solid = false
  Source = -> Face070
  Symmetric = false
FEATURE [Part::MultiFuse] Fusion048  label="makeHoles001"
  Shapes = -> [Revolve074,Revolve073,Revolve072,Revolve071,Revolve070,Revolve069]
FEATURE [Part::MultiFuse] Fusion049  label="caseScrewRetainers"
  Shapes = -> [Revolve067,Revolve068,Revolve048,Revolve047,Revolve039,Revolve040]
FEATURE [Part::Cut] Cut015  label="caseScrewRetainers001"
  Base = -> Fusion049
  Tool = -> Fusion048
FEATURE [Part::MultiFuse] Fusion050  label="casePillars"
  Shapes = -> [Revolve055,Revolve054,Revolve043,Revolve046,Revolve059,Revolve060]
FEATURE [Part::Feature] Face071 .. Face076  x6 (patterned run collapsed; names and placements below)
  shape: bbox 3.5 x 17.8 x 2e-07 mm, 1 faces, 0 solids (baked)
FEATURE [Part::Revolution] Revolve075  label="removeToCreateScrewAndThreadedInsertHole012"
  Angle = 360
  Axis = (0,1,0)
  Base = (0,0,0)
  FaceMakerClass = Part::FaceMakerBullseye
  Placement = pos=(12.5,0,10) rot=(0,0,1;0rad)
  Solid = false
  Source = -> Face071
  Symmetric = false
FEATURE [Part::Revolution] Revolve076  label="removeToCreateScrewAndThreadedInsertHole013"
  Angle = 360
  Axis = (0,1,0)
  Base = (0,0,0)
  FaceMakerClass = Part::FaceMakerBullseye
  Placement = pos=(12.5,0,62) rot=(0,0,1;0rad)
  Solid = false
  Source = -> Face072
  Symmetric = false
FEATURE [Part::Revolution] Revolve077  label="removeToCreateScrewAndThreadedInsertHole014"
  Angle = 360
  Axis = (0,1,0)
  Base = (0,0,0)
  FaceMakerClass = Part::FaceMakerBullseye
  Placement = pos=(89.5,0,68.5) rot=(0,0,1;0rad)
  Solid = false
  Source = -> Face073
  Symmetric = false
FEATURE [Part::Revolution] Revolve078  label="removeToCreateScrewAndThreadedInsertHole015"
  Angle = 360
  Axis = (0,1,0)
  Base = (0,0,0)
  FaceMakerClass = Part::FaceMakerBullseye
  Placement = pos=(89.5,0,3.5) rot=(0,0,1;0rad)
  Solid = false
  Source = -> Face074
  Symmetric = false
FEATURE [Part::Revolution] Revolve079  label="removeToCreateScrewAndThreadedInsertHole016"
  Angle = 360
  Axis = (0,1,0)
  Base = (0,0,0)
  FaceMakerClass = Part::FaceMakerBullseye
  Placement = pos=(102.5,4.7,3.5) rot=(0,0,1;0rad)
  Solid = false
  Source = -> Face075
  Symmetric = false
FEATURE [Part::Revolution] Revolve080  label="removeToCreateScrewAndThreadedInsertHole017"
  Angle = 360
  Axis = (0,1,0)
  Base = (0,0,0)
  FaceMakerClass = Part::FaceMakerBullseye
  Placement = pos=(102.5,4.7,68.5) rot=(0,0,1;0rad)
  Solid = false
  Source = -> Face076
  Symmetric = false
FEATURE [Part::MultiFuse] Fusion051  label="makeHoles002"
  Shapes = -> [Revolve080,Revolve079,Revolve078,Revolve077,Revolve076,Revolve075]
FEATURE [Part::Cut] Cut016  label="caesPillars"
  Base = -> Fusion050
  Tool = -> Fusion051
FEATURE [Part::Revolution] Revolve009  label="plugHousing016"
  Angle = 360
  Axis = (0,1,0)
  Base = (0,0,0)
  FaceMakerClass = Part::FaceMakerBullseye
  Placement = pos=(0,0,36.15) rot=(0,0,1;0rad)
  Solid = false
  Source = -> Face012
  Symmetric = false
FEATURE [Part::MultiFuse] Fusion014  label="plugHousing023"
  Placement = pos=(0,0,0) rot=(0,0,1;1.5708rad)
  Shapes = -> [Revolve011,Revolve009]
FEATURE [Part::Revolution] Revolve010  label="plugHousing017"
  Angle = 360
  Axis = (0,1,0)
  Base = (0,0,0)
  FaceMakerClass = Part::FaceMakerBullseye
  Placement = pos=(0,0,36.15) rot=(0,0,1;0rad)
  Solid = false
  Source = -> Face014
  Symmetric = false
FEATURE [Part::MultiFuse] Fusion015  label="plugHousing024"
  Placement = pos=(0,0,0) rot=(0,0,1;1.5708rad)
  Shapes = -> [Revolve010,Revolve015]
FEATURE [Part::Revolution] Revolve014  label="plugHousing026"
  Angle = 360
  Axis = (0,1,0)
  Base = (0,0,0)
  FaceMakerClass = Part::FaceMakerBullseye
  Placement = pos=(0,0,36.15) rot=(0,0,1;0rad)
  Solid = false
  Source = -> Face011
  Symmetric = false
FEATURE [Part::Revolution] Revolve013  label="plugHousing025"
  Angle = 360
  Axis = (0,1,0)
  Base = (0,0,0)
  FaceMakerClass = Part::FaceMakerBullseye
  Placement = pos=(0,0,36.15) rot=(0,0,1;0rad)
  Solid = false
  Source = -> Face015
  Symmetric = false
FEATURE [Part::MultiFuse] Fusion016  label="plugHousing028"
  Placement = pos=(0,19,0) rot=(0,0,1;3.14159rad)
  Shapes = -> [Fusion014,Fusion013]
FEATURE [Part::MultiFuse] Fusion011  label="plugHousing018"
  Placement = pos=(0,0,0) rot=(0,0,1;1.5708rad)
  Shapes = -> [Revolve014,Revolve013]
FEATURE [Part::MultiFuse] Fusion012  label="plugHousing019"
  Placement = pos=(0,19,0) rot=(0,0,1;3.14159rad)
  Shapes = -> [Fusion011,Fusion015]
FEATURE [Part::MultiFuse] Fusion017  label="plugHousing029"
  Placement = pos=(122.621,0,-0.15) rot=(0,0,1;0rad)
  Shapes = -> [Fusion016,Fusion012]
FEATURE [Part::MultiFuse] Fusion052  label="casePillarRetainers"
  Shapes = -> [Extrude012,Extrude013,Extrude014,Extrude015,Extrude016,Extrude017,Extrude018,Extrude019,Box011,Box012]
FEATURE [Part::Feature] Face077
  shape: bbox 3.5 x 17.8 x 2e-07 mm, 1 faces, 0 solids (baked)
FEATURE [Part::Revolution] Revolve081  label="removeToCreateScrewAndThreadedInsertHole018"
  Angle = 360
  Axis = (0,1,0)
  Base = (0,0,0)
  FaceMakerClass = Part::FaceMakerBullseye
  Placement = pos=(62.3,30.3,19.7) rot=(0,0,1;0rad)
  Solid = false
  Source = -> Face077
  Symmetric = false
FEATURE [Part::Feature] Face078
  shape: bbox 3.5 x 17.8 x 2e-07 mm, 1 faces, 0 solids (baked)
FEATURE [Part::Revolution] Revolve082  label="removeToCreateScrewAndThreadedInsertHole019"
  Angle = 360
  Axis = (0,1,0)
  Base = (0,0,0)
  FaceMakerClass = Part::FaceMakerBullseye
  Placement = pos=(62.3,30.3,51.7) rot=(0,0,1;0rad)
  Solid = false
  Source = -> Face078
  Symmetric = false
FEATURE [Part::Feature] Face079
  shape: bbox 3.5 x 17.8 x 2e-07 mm, 1 faces, 0 solids (baked)
FEATURE [Part::Revolution] Revolve083  label="removeToCreateScrewAndThreadedInsertHole020"
  Angle = 360
  Axis = (0,1,0)
  Base = (0,0,0)
  FaceMakerClass = Part::FaceMakerBullseye
  Placement = pos=(30.3,30.3,19.7) rot=(0,0,1;0rad)
  Solid = false
  Source = -> Face079
  Symmetric = false
FEATURE [Part::Feature] Face080
  shape: bbox 3.5 x 17.8 x 2e-07 mm, 1 faces, 0 solids (baked)
FEATURE [Part::Revolution] Revolve084  label="removeToCreateScrewAndThreadedInsertHole021"
  Angle = 360
  Axis = (0,1,0)
  Base = (0,0,0)
  FaceMakerClass = Part::FaceMakerBullseye
  Placement = pos=(30.3,30.3,51.7) rot=(0,0,1;0rad)
  Solid = false
  Source = -> Face080
  Symmetric = false
FEATURE [Part::MultiFuse] Fusion053  label="createThreadedInsertHolesForFan"
  Shapes = -> [Revolve081,Revolve082,Revolve083,Revolve084]
FEATURE [Part::Cut] Cut017  label="fanScrewHousing001"
  Base = -> Fusion046
  Tool = -> Fusion053
FEATURE [Part::Feature] Face081
  shape: bbox 3.5 x 17.8 x 2e-07 mm, 1 faces, 0 solids (baked)
FEATURE [Part::Revolution] Revolve085  label="removeToCreateScrewAndThreadedInsertHole022"
  Angle = 360
  Axis = (0,1,0)
  Base = (0,0,0)
  FaceMakerClass = Part::FaceMakerBullseye
  Placement = pos=(62.3,30.3,19.7) rot=(0,0,1;0rad)
  Solid = false
  Source = -> Face081
  Symmetric = false
FEATURE [Part::Feature] Face082
  shape: bbox 3.5 x 17.8 x 2e-07 mm, 1 faces, 0 solids (baked)
FEATURE [Part::Revolution] Revolve086  label="removeToCreateScrewAndThreadedInsertHole023"
  Angle = 360
  Axis = (0,1,0)
  Base = (0,0,0)
  FaceMakerClass = Part::FaceMakerBullseye
  Placement = pos=(62.3,30.3,51.7) rot=(0,0,1;0rad)
  Solid = false
  Source = -> Face082
  Symmetric = false
FEATURE [Part::Feature] Face083
  shape: bbox 3.5 x 17.8 x 2e-07 mm, 1 faces, 0 solids (baked)
FEATURE [Part::Revolution] Revolve087  label="removeToCreateScrewAndThreadedInsertHole024"
  Angle = 360
  Axis = (0,1,0)
  Base = (0,0,0)
  FaceMakerClass = Part::FaceMakerBullseye
  Placement = pos=(30.3,30.3,19.7) rot=(0,0,1;0rad)
  Solid = false
  Source = -> Face083
  Symmetric = false
FEATURE [Part::Feature] Face084
  shape: bbox 3.5 x 17.8 x 2e-07 mm, 1 faces, 0 solids (baked)
FEATURE [Part::Revolution] Revolve088  label="removeToCreateScrewAndThreadedInsertHole025"
  Angle = 360
  Axis = (0,1,0)
  Base = (0,0,0)
  FaceMakerClass = Part::FaceMakerBullseye
  Placement = pos=(30.3,30.3,51.7) rot=(0,0,1;0rad)
  Solid = false
  Source = -> Face084
  Symmetric = false
FEATURE [Part::MultiFuse] Fusion054  label="createThreadedInsertHolesForFan001"
  Shapes = -> [Revolve085,Revolve086,Revolve087,Revolve088]
FEATURE [Part::Cut] Cut018  label="top007"
  Base = -> Fusion040
  Tool = -> Fusion054
FEATURE [Sketcher::SketchObject] Sketch029
  FullyConstrained = false
  Placement = pos=(0,0,0) rot=(1,0,0;1.5708rad)
  sketch-geometry (24):
    g0: ArcOfCircle CenterX=-4 CenterY=-10.5 CenterZ=0 NormalX=0 NormalY=0 NormalZ=1 AngleXU=0 Radius=1.5 StartAngle=6e-16 EndAngle=3.14159
    g1: ArcOfCircle CenterX=-34.2 CenterY=-10.5 CenterZ=0 NormalX=0 NormalY=0 NormalZ=1 AngleXU=0 Radius=1.5 StartAngle=0 EndAngle=3.14159
    g2: ArcOfCircle CenterX=-34.2 CenterY=-27.7 CenterZ=0 NormalX=0 NormalY=0 NormalZ=1 AngleXU=0 Radius=1.5 StartAngle=3.14159 EndAngle=6.28319
    g3: ArcOfCircle CenterX=-4 CenterY=-27.7 CenterZ=0 NormalX=0 NormalY=0 NormalZ=1 AngleXU=0 Radius=1.5 StartAngle=3.1416 EndAngle=6.28319
    g4: ArcOfCircle CenterX=-10 CenterY=-4.3 CenterZ=0 NormalX=0 NormalY=0 NormalZ=1 AngleXU=0 Radius=1.5 StartAngle=2e-16 EndAngle=3.14159
    g5: ArcOfCircle CenterX=-16.1 CenterY=-1.8 CenterZ=0 NormalX=0 NormalY=0 NormalZ=1 AngleXU=0 Radius=1.5 StartAngle=5e-16 EndAngle=3.14159
    g6: ArcOfCircle CenterX=-22.1 CenterY=-1.8 CenterZ=0 NormalX=0 NormalY=0 NormalZ=1 AngleXU=0 Radius=1.5 StartAngle=5e-16 EndAngle=3.14159
    g7: ArcOfCircle CenterX=-28.2 CenterY=-4.3 CenterZ=0 NormalX=0 NormalY=0 NormalZ=1 AngleXU=0 Radius=1.5 StartAngle=2e-16 EndAngle=3.14159
    g8: ArcOfCircle CenterX=-10 CenterY=-33.9 CenterZ=0 NormalX=0 NormalY=0 NormalZ=1 AngleXU=0 Radius=1.5 StartAngle=3.14159 EndAngle=6.28319
    g9: ArcOfCircle CenterX=-16.1 CenterY=-36.4 CenterZ=0 NormalX=0 NormalY=0 NormalZ=1 AngleXU=0 Radius=1.5 StartAngle=3.14159 EndAngle=6.28319
    g10: ArcOfCircle CenterX=-22.1 CenterY=-36.4 CenterZ=0 NormalX=0 NormalY=0 NormalZ=1 AngleXU=0 Radius=1.5 StartAngle=3.14159 EndAngle=6.28319
    g11: ArcOfCircle CenterX=-28.2 CenterY=-33.9 CenterZ=0 NormalX=0 NormalY=0 NormalZ=1 AngleXU=0 Radius=1.5 StartAngle=3.14159 EndAngle=6.28319
    g12: LineSegment StartX=-35.7 StartY=-10.5 StartZ=0 EndX=-35.7 EndY=-27.7 EndZ=0
    g13: LineSegment StartX=-32.7 StartY=-10.5 StartZ=0 EndX=-32.7 EndY=-27.7 EndZ=0
    g14: LineSegment StartX=-29.7 StartY=-33.9 StartZ=0 EndX=-29.7 EndY=-4.3 EndZ=0
    g15: LineSegment StartX=-26.7 StartY=-33.9 StartZ=0 EndX=-26.7 EndY=-4.3 EndZ=0
    g16: LineSegment StartX=-2.5 StartY=-10.5 StartZ=0 EndX=-2.5 EndY=-27.7 EndZ=0
    g17: LineSegment StartX=-8.5 StartY=-4.3 StartZ=0 EndX=-8.5 EndY=-33.9 EndZ=0
    g18: LineSegment StartX=-5.5 StartY=-10.5 StartZ=0 EndX=-5.5 EndY=-27.7 EndZ=0
    g19: LineSegment StartX=-11.5 StartY=-4.3 StartZ=0 EndX=-11.5 EndY=-33.9 EndZ=0
    g20: LineSegment StartX=-14.6 StartY=-1.8 StartZ=0 EndX=-14.6 EndY=-36.4 EndZ=0
    g21: LineSegment StartX=-17.6 StartY=-1.8 StartZ=0 EndX=-17.6 EndY=-36.4 EndZ=0
    g22: LineSegment StartX=-20.6 StartY=-36.4 StartZ=0 EndX=-20.6 EndY=-1.8 EndZ=0
    g23: LineSegment StartX=-23.6 StartY=-1.8 StartZ=0 EndX=-23.6 EndY=-36.4 EndZ=0
  constraints (48):
    c: Block(g0)
    c: Block(g1)
    c: Block(g2)
    c: Block(g3)
    c: Block(g4)
    c: Block(g5)
    c: Block(g6)
    c: Block(g7)
    c: Block(g8)
    c: Block(g9)
    c: Block(g10)
    c: Block(g11)
    c: Coincident(g12,g1)
    c: Coincident(g12,g2)
    c: Vertical(g12)
    c: Coincident(g13,g1)
    c: Coincident(g13,g2)
    c: Vertical(g13)
    c: Coincident(g14,g11)
    c: Coincident(g14,g7)
    c: Vertical(g14)
    c: Coincident(g15,g11)
    c: Coincident(g15,g7)
    c: Vertical(g15)
    c: Coincident(g16,g0)
    c: Coincident(g16,g3)
    c: Vertical(g16)
    c: Coincident(g17,g4)
    c: Coincident(g17,g8)
    c: Vertical(g17)
    c: Coincident(g18,g0)
    c: Coincident(g18,g3)
    c: Vertical(g18)
    c: Coincident(g19,g4)
    c: Coincident(g19,g8)
    c: Vertical(g19)
    c: Coincident(g20,g5)
    c: Coincident(g20,g9)
    c: Vertical(g20)
    c: Coincident(g21,g5)
    c: Coincident(g21,g9)
    c: Vertical(g21)
    c: Coincident(g22,g10)
    c: Coincident(g22,g6)
    c: Vertical(g22)
    c: Coincident(g23,g6)
    c: Coincident(g23,g10)
    c: Vertical(g23)
FEATURE [Part::Extrusion] Extrude020  label="removeToCreateFanGrillHoles"
  Base = -> Sketch029
  Dir = (0,-1,6e-16)
  DirMode = 2
  FaceMakerClass = Part::FaceMakerBullseye
  LengthFwd = 10
  LengthRev = 0
  Placement = pos=(65.4,44,54.82) rot=(0,0,1;0rad)
  Solid = true
  Symmetric = false
FEATURE [Part::MultiFuse] Fusion055  label="top008"
  Shapes = -> [Cut017,Cut018]
FEATURE [Part::Cut] Cut019  label="top009"
  Base = -> Fusion055
  Tool = -> Extrude020
FEATURE [App::MeasureDistance] Distance003  label="Distance: 71.95 mm"
  Distance = 71.9513
  P1 = (117,38,72)
  P2 = (117,38,0.0487319)
FEATURE [Sketcher::SketchObject] Sketch030
  FullyConstrained = true
  Placement = pos=(117,19,0) rot=(0.57735,0.57735,0.57735;2.0944rad)
  sketch-geometry (48):
    g0: LineSegment StartX=-49.19 StartY=69.25 StartZ=0 EndX=-49.19 EndY=66.25 EndZ=0
    g1: LineSegment StartX=-49.19 StartY=63.5 StartZ=0 EndX=-49.19 EndY=60.5 EndZ=0
    g2: LineSegment StartX=-49.19 StartY=57.75 StartZ=0 EndX=-49.19 EndY=54.75 EndZ=0
    g3: LineSegment StartX=-49.19 StartY=52 StartZ=0 EndX=-49.19 EndY=49 EndZ=0
    g4: LineSegment StartX=-49.19 StartY=46.25 StartZ=0 EndX=-49.19 EndY=43.25 EndZ=0
    g5: LineSegment StartX=-49.19 StartY=40.5 StartZ=0 EndX=-49.19 EndY=37.5 EndZ=0
    g6: LineSegment StartX=-49.19 StartY=34.5 StartZ=0 EndX=-49.19 EndY=31.5 EndZ=0
    g7: LineSegment StartX=-49.19 StartY=28.75 StartZ=0 EndX=-49.19 EndY=25.75 EndZ=0
    g8: LineSegment StartX=-49.19 StartY=23 StartZ=0 EndX=-49.19 EndY=20 EndZ=0
    g9: LineSegment StartX=-49.19 StartY=17.25 StartZ=0 EndX=-49.19 EndY=14.25 EndZ=0
    g10: LineSegment StartX=-49.19 StartY=11.5 StartZ=0 EndX=-49.19 EndY=8.5 EndZ=0
    g11: LineSegment StartX=-49.19 StartY=5.75 StartZ=0 EndX=-49.19 EndY=2.75 EndZ=0
    g12: ArcOfCircle CenterX=-1.5 CenterY=67.75 CenterZ=0 NormalX=0 NormalY=0 NormalZ=1 AngleXU=0 Radius=1.5 StartAngle=4.71239 EndAngle=7.85398
    g13: ArcOfCircle CenterX=-1.5 CenterY=62 CenterZ=0 NormalX=0 NormalY=0 NormalZ=1 AngleXU=0 Radius=1.5 StartAngle=4.71239 EndAngle=7.85398
    g14: ArcOfCircle CenterX=-1.5 CenterY=56.25 CenterZ=0 NormalX=0 NormalY=0 NormalZ=1 AngleXU=0 Radius=1.5 StartAngle=4.71239 EndAngle=7.85398
    g15: ArcOfCircle CenterX=-11.49 CenterY=50.5 CenterZ=0 NormalX=0 NormalY=0 NormalZ=1 AngleXU=0 Radius=1.5 StartAngle=4.71239 EndAngle=7.85398
    g16: ArcOfCircle CenterX=-16.28 CenterY=44.75 CenterZ=0 NormalX=0 NormalY=0 NormalZ=1 AngleXU=0 Radius=1.5 StartAngle=4.71239 EndAngle=7.85398
    g17: ArcOfCircle CenterX=-18.2337 CenterY=39 CenterZ=0 NormalX=0 NormalY=0 NormalZ=1 AngleXU=0 Radius=1.5 StartAngle=4.71485 EndAngle=7.85398
    g18: ArcOfCircle CenterX=-16.2837 CenterY=27.25 CenterZ=0 NormalX=0 NormalY=0 NormalZ=1 AngleXU=0 Radius=1.5 StartAngle=4.71485 EndAngle=7.85398
    g19: ArcOfCircle CenterX=-18.2337 CenterY=33 CenterZ=0 NormalX=0 NormalY=0 NormalZ=1 AngleXU=0 Radius=1.5 StartAngle=4.71485 EndAngle=7.85398
    g20: ArcOfCircle CenterX=-11.49 CenterY=21.5 CenterZ=0 NormalX=0 NormalY=0 NormalZ=1 AngleXU=0 Radius=1.5 StartAngle=4.71239 EndAngle=7.85398
    g21: ArcOfCircle CenterX=-1.5 CenterY=4.25 CenterZ=0 NormalX=0 NormalY=0 NormalZ=1 AngleXU=0 Radius=1.5 StartAngle=4.71239 EndAngle=7.85398
    g22: ArcOfCircle CenterX=-1.5 CenterY=10 CenterZ=0 NormalX=0 NormalY=0 NormalZ=1 AngleXU=0 Radius=1.5 StartAngle=4.71239 EndAngle=7.85398
    g23: ArcOfCircle CenterX=-1.5 CenterY=15.75 CenterZ=0 NormalX=0 NormalY=0 NormalZ=1 AngleXU=0 Radius=1.5 StartAngle=4.71239 EndAngle=7.85398
    g24: LineSegment StartX=-49.19 StartY=69.25 StartZ=0 EndX=-1.5 EndY=69.25 EndZ=0
    g25: LineSegment StartX=-49.19 StartY=66.25 StartZ=0 EndX=-1.5 EndY=66.25 EndZ=0
    g26: LineSegment StartX=-49.19 StartY=63.5 StartZ=0 EndX=-1.5 EndY=63.5 EndZ=0
    g27: LineSegment StartX=-49.19 StartY=60.5 StartZ=0 EndX=-1.5 EndY=60.5 EndZ=0
    g28: LineSegment StartX=-49.19 StartY=57.75 StartZ=0 EndX=-1.5 EndY=57.75 EndZ=0
    g29: LineSegment StartX=-49.19 StartY=54.75 StartZ=0 EndX=-1.5 EndY=54.75 EndZ=0
    g30: LineSegment StartX=-49.19 StartY=52 StartZ=0 EndX=-11.49 EndY=52 EndZ=0
    g31: LineSegment StartX=-49.19 StartY=49 StartZ=0 EndX=-11.49 EndY=49 EndZ=0
    g32: LineSegment StartX=-49.19 StartY=46.25 StartZ=0 EndX=-16.28 EndY=46.25 EndZ=0
    g33: LineSegment StartX=-49.19 StartY=43.25 StartZ=0 EndX=-16.28 EndY=43.25 EndZ=0
    g34: LineSegment StartX=-49.19 StartY=40.5 StartZ=0 EndX=-18.2337 EndY=40.5 EndZ=0
    g35: LineSegment StartX=-49.19 StartY=37.5 StartZ=0 EndX=-18.23 EndY=37.5 EndZ=0
    g36: LineSegment StartX=-49.19 StartY=34.5 StartZ=0 EndX=-18.2337 EndY=34.5 EndZ=0
    g37: LineSegment StartX=-49.19 StartY=31.5 StartZ=0 EndX=-18.23 EndY=31.5 EndZ=0
    g38: LineSegment StartX=-49.19 StartY=28.75 StartZ=0 EndX=-16.2837 EndY=28.75 EndZ=0
    g39: LineSegment StartX=-49.19 StartY=25.75 StartZ=0 EndX=-16.28 EndY=25.75 EndZ=0
    g40: LineSegment StartX=-49.19 StartY=23 StartZ=0 EndX=-11.49 EndY=23 EndZ=0
    g41: LineSegment StartX=-49.19 StartY=20 StartZ=0 EndX=-11.49 EndY=20 EndZ=0
    g42: LineSegment StartX=-49.19 StartY=17.25 StartZ=0 EndX=-1.5 EndY=17.25 EndZ=0
    g43: LineSegment StartX=-49.19 StartY=14.25 StartZ=0 EndX=-1.5 EndY=14.25 EndZ=0
    g44: LineSegment StartX=-49.19 StartY=11.5 StartZ=0 EndX=-1.5 EndY=11.5 EndZ=0
    g45: LineSegment StartX=-49.19 StartY=8.5 StartZ=0 EndX=-1.5 EndY=8.5 EndZ=0
    g46: LineSegment StartX=-49.19 StartY=5.75 StartZ=0 EndX=-1.5 EndY=5.75 EndZ=0
    g47: LineSegment StartX=-49.19 StartY=2.75 StartZ=0 EndX=-1.5 EndY=2.75 EndZ=0
  constraints (120):
    c: Vertical(g0)
    c: Distance(g0) = 3
    c: Block(g0)
    c: Vertical(g1)
    c: Distance(g1) = 3
    c: Vertical(g2)
    c: Equal(g0,g2) = 3
    c: Block(g2)
    c: Vertical(g3)
    c: Equal(g1,g3) = 3
    c: Vertical(g4)
    c: Equal(g0,g4) = 3
    c: Block(g4)
    c: Vertical(g5)
    c: Equal(g1,g5) = 3
    c: Vertical(g6)
    c: Equal(g0,g6) = 3
    c: Block(g6)
    c: Vertical(g7)
    c: Equal(g1,g7) = 3
    c: Vertical(g8)
    c: Equal(g0,g8) = 3
    c: Block(g8)
    c: Vertical(g9)
    c: Equal(g1,g9) = 3
    c: Vertical(g10)
    c: Equal(g0,g10) = 3
    c: Block(g10)
    c: Vertical(g11)
    c: Equal(g1,g11) = 3
    c: Block(g12)
    c: Block(g13)
    c: Block(g14)
    c: Block(g15)
    c: Block(g16)
    c: Block(g17)
    c: Block(g18)
    c: Block(g19)
    c: Block(g20)
    c: Block(g21)
    c: Block(g22)
    c: Block(g23)
    c: Block(g11)
    c: Block(g9)
    c: Block(g7)
    c: Block(g5)
    c: Block(g3)
    c: Block(g1)
    c: Coincident(g24,g0)
    c: Coincident(g24,g12)
    c: Horizontal(g24)
    c: Coincident(g25,g0)
    c: Coincident(g25,g12)
    c: Horizontal(g25)
    c: Coincident(g26,g1)
    c: Coincident(g26,g13)
    c: Horizontal(g26)
    c: Coincident(g27,g1)
    c: Coincident(g27,g13)
    c: Horizontal(g27)
    c: Coincident(g28,g2)
    c: Coincident(g28,g14)
    c: Horizontal(g28)
    c: Coincident(g29,g2)
    c: Coincident(g29,g14)
    c: Horizontal(g29)
    c: Coincident(g30,g3)
    c: Coincident(g30,g15)
    c: Horizontal(g30)
    c: Coincident(g31,g3)
    c: Coincident(g31,g15)
    c: Horizontal(g31)
    c: Coincident(g32,g4)
    c: Coincident(g32,g16)
    c: Horizontal(g32)
    c: Coincident(g33,g4)
    c: Coincident(g33,g16)
    c: Horizontal(g33)
    c: Coincident(g34,g5)
    c: Coincident(g34,g17)
    c: Horizontal(g34)
    c: Coincident(g35,g5)
    c: Coincident(g35,g17)
    c: Horizontal(g35)
    c: Coincident(g36,g6)
    c: Coincident(g36,g19)
    c: Horizontal(g36)
    c: Coincident(g37,g6)
    c: Coincident(g37,g19)
    c: Horizontal(g37)
    c: Coincident(g38,g7)
    c: Coincident(g38,g18)
    c: Horizontal(g38)
    c: Coincident(g39,g7)
    c: Coincident(g39,g18)
    c: Horizontal(g39)
    c: Coincident(g40,g8)
    c: Coincident(g40,g20)
    c: Horizontal(g40)
    c: Coincident(g41,g8)
    c: Coincident(g41,g20)
    c: Horizontal(g41)
    c: Coincident(g42,g9)
    c: Coincident(g42,g23)
    c: Horizontal(g42)
    c: Coincident(g43,g9)
    c: Coincident(g43,g23)
    c: Horizontal(g43)
    c: Coincident(g44,g10)
    c: Coincident(g44,g22)
    c: Horizontal(g44)
    c: Coincident(g45,g10)
    c: Coincident(g45,g22)
    c: Horizontal(g45)
    c: Coincident(g46,g11)
    c: Coincident(g46,g21)
    c: Horizontal(g46)
    c: Coincident(g47,g11)
    c: Coincident(g47,g21)
    c: Horizontal(g47)
FEATURE [Sketcher::SketchObject] Sketch031
  FullyConstrained = true
  Placement = pos=(117,19,0) rot=(0.57735,0.57735,0.57735;2.0944rad)
  sketch-geometry (24):
    g0: ArcOfCircle CenterX=-49.19 CenterY=67.75 CenterZ=0 NormalX=0 NormalY=0 NormalZ=1 AngleXU=0 Radius=1.5 StartAngle=1.5708 EndAngle=4.71239
    g1: ArcOfCircle CenterX=-49.19 CenterY=62 CenterZ=0 NormalX=0 NormalY=0 NormalZ=1 AngleXU=0 Radius=1.5 StartAngle=1.5708 EndAngle=4.71239
    g2: ArcOfCircle CenterX=-49.19 CenterY=56.25 CenterZ=0 NormalX=0 NormalY=0 NormalZ=1 AngleXU=0 Radius=1.5 StartAngle=1.5708 EndAngle=4.71239
    g3: ArcOfCircle CenterX=-49.19 CenterY=50.5 CenterZ=0 NormalX=0 NormalY=0 NormalZ=1 AngleXU=0 Radius=1.5 StartAngle=1.5708 EndAngle=4.71239
    g4: ArcOfCircle CenterX=-49.19 CenterY=44.75 CenterZ=0 NormalX=0 NormalY=0 NormalZ=1 AngleXU=0 Radius=1.5 StartAngle=1.5708 EndAngle=4.71239
    g5: ArcOfCircle CenterX=-49.19 CenterY=39 CenterZ=0 NormalX=0 NormalY=0 NormalZ=1 AngleXU=0 Radius=1.5 StartAngle=1.5708 EndAngle=4.71239
    g6: ArcOfCircle CenterX=-49.19 CenterY=33 CenterZ=0 NormalX=0 NormalY=0 NormalZ=1 AngleXU=0 Radius=1.5 StartAngle=1.5708 EndAngle=4.71239
    g7: ArcOfCircle CenterX=-49.19 CenterY=27.25 CenterZ=0 NormalX=0 NormalY=0 NormalZ=1 AngleXU=0 Radius=1.5 StartAngle=1.5708 EndAngle=4.71239
    g8: ArcOfCircle CenterX=-49.19 CenterY=21.5 CenterZ=0 NormalX=0 NormalY=0 NormalZ=1 AngleXU=0 Radius=1.5 StartAngle=1.5708 EndAngle=4.71239
    g9: ArcOfCircle CenterX=-49.19 CenterY=15.75 CenterZ=0 NormalX=0 NormalY=0 NormalZ=1 AngleXU=0 Radius=1.5 StartAngle=1.5708 EndAngle=4.71239
    g10: ArcOfCircle CenterX=-49.19 CenterY=10 CenterZ=0 NormalX=0 NormalY=0 NormalZ=1 AngleXU=0 Radius=1.5 StartAngle=1.5708 EndAngle=4.71239
    g11: ArcOfCircle CenterX=-49.19 CenterY=4.25 CenterZ=0 NormalX=0 NormalY=0 NormalZ=1 AngleXU=0 Radius=1.5 StartAngle=1.5708 EndAngle=4.71239
    g12: LineSegment StartX=-49.19 StartY=69.25 StartZ=0 EndX=-49.19 EndY=66.25 EndZ=0
    g13: LineSegment StartX=-49.19 StartY=63.5 StartZ=0 EndX=-49.19 EndY=60.5 EndZ=0
    g14: LineSegment StartX=-49.19 StartY=57.75 StartZ=0 EndX=-49.19 EndY=54.75 EndZ=0
    g15: LineSegment StartX=-49.19 StartY=52 StartZ=0 EndX=-49.19 EndY=49 EndZ=0
    g16: LineSegment StartX=-49.19 StartY=46.25 StartZ=0 EndX=-49.19 EndY=43.25 EndZ=0
    g17: LineSegment StartX=-49.19 StartY=40.5 StartZ=0 EndX=-49.19 EndY=37.5 EndZ=0
    g18: LineSegment StartX=-49.19 StartY=34.5 StartZ=0 EndX=-49.19 EndY=31.5 EndZ=0
    g19: LineSegment StartX=-49.19 StartY=28.75 StartZ=0 EndX=-49.19 EndY=25.75 EndZ=0
    g20: LineSegment StartX=-49.19 StartY=23 StartZ=0 EndX=-49.19 EndY=20 EndZ=0
    g21: LineSegment StartX=-49.19 StartY=17.25 StartZ=0 EndX=-49.19 EndY=14.25 EndZ=0
    g22: LineSegment StartX=-49.19 StartY=11.5 StartZ=0 EndX=-49.19 EndY=8.5 EndZ=0
    g23: LineSegment StartX=-49.19 StartY=5.75 StartZ=0 EndX=-49.19 EndY=2.75 EndZ=0
  constraints (48):
    c: Block(g0)
    c: Block(g1)
    c: Block(g2)
    c: Block(g3)
    c: Block(g4)
    c: Block(g5)
    c: Block(g6)
    c: Block(g7)
    c: Block(g8)
    c: Block(g9)
    c: Block(g10)
    c: Block(g11)
    c: Coincident(g12,g0)
    c: Coincident(g12,g0)
    c: Vertical(g12)
    c: Vertical(g13)
    c: Coincident(g13,g1)
    c: Vertical(g14)
    c: Coincident(g14,g2)
    c: Vertical(g15)
    c: Coincident(g15,g3)
    c: Vertical(g16)
    c: Coincident(g16,g4)
    c: Vertical(g17)
    c: Coincident(g17,g5)
    c: Vertical(g18)
    c: Coincident(g18,g6)
    c: Vertical(g19)
    c: Coincident(g19,g7)
    c: Vertical(g20)
    c: Coincident(g20,g8)
    c: Vertical(g21)
    c: Coincident(g21,g9)
    c: Vertical(g22)
    c: Coincident(g22,g10)
    c: Vertical(g23)
    c: Coincident(g23,g11)
    c: Block(g23)
    c: Block(g22)
    c: Block(g21)
    c: Block(g20)
    c: Block(g13)
    c: Block(g14)
    c: Block(g15)
    c: Block(g16)
    c: Block(g17)
    c: Block(g18)
    c: Block(g19)
FEATURE [Part::Extrusion] Extrude022
  Base = -> Sketch030
  Dir = (1,-2e-16,2e-16)
  DirMode = 2
  FaceMakerClass = Part::FaceMakerBullseye
  LengthFwd = 19
  LengthRev = 0
  Placement = pos=(-19,0,0) rot=(0,0,1;0rad)
  Solid = true
  Symmetric = false
FEATURE [Part::Fillet] Fillet022
  Base = -> Extrude022
  Edges = 24 edges r=1.49: [Edge6,Edge11,Edge18,Edge23,Edge30,Edge35,Edge42,Edge47,Edge54,Edge59,Edge66,Edge71,Edge78,Edge83,Edge90,Edge95,Edge102,Edge107,Edge114,Edge119,Edge126,Edge131,Edge138,Edge143]
FEATURE [Part::Cut] Cut020  label="top010"
  Base = -> Cut019
  Tool = -> Fillet022
FEATURE [Sketcher::SketchObject] Sketch032
  FullyConstrained = true
  Placement = pos=(117,19,0) rot=(0.57735,0.57735,0.57735;2.0944rad)
  sketch-geometry (48):
    g0: LineSegment StartX=-49.19 StartY=69.25 StartZ=0 EndX=-49.19 EndY=66.25 EndZ=0
    g1: LineSegment StartX=-49.19 StartY=63.5 StartZ=0 EndX=-49.19 EndY=60.5 EndZ=0
    g2: LineSegment StartX=-49.19 StartY=57.75 StartZ=0 EndX=-49.19 EndY=54.75 EndZ=0
    g3: LineSegment StartX=-49.19 StartY=52 StartZ=0 EndX=-49.19 EndY=49 EndZ=0
    g4: LineSegment StartX=-49.19 StartY=46.25 StartZ=0 EndX=-49.19 EndY=43.25 EndZ=0
    g5: LineSegment StartX=-49.19 StartY=40.5 StartZ=0 EndX=-49.19 EndY=37.5 EndZ=0
    g6: LineSegment StartX=-49.19 StartY=34.5 StartZ=0 EndX=-49.19 EndY=31.5 EndZ=0
    g7: LineSegment StartX=-49.19 StartY=28.75 StartZ=0 EndX=-49.19 EndY=25.75 EndZ=0
    g8: LineSegment StartX=-49.19 StartY=23 StartZ=0 EndX=-49.19 EndY=20 EndZ=0
    g9: LineSegment StartX=-49.19 StartY=17.25 StartZ=0 EndX=-49.19 EndY=14.25 EndZ=0
    g10: LineSegment StartX=-49.19 StartY=11.5 StartZ=0 EndX=-49.19 EndY=8.5 EndZ=0
    g11: LineSegment StartX=-49.19 StartY=5.75 StartZ=0 EndX=-49.19 EndY=2.75 EndZ=0
    g12: ArcOfCircle CenterX=-1.5 CenterY=67.75 CenterZ=0 NormalX=0 NormalY=0 NormalZ=1 AngleXU=0 Radius=1.5 StartAngle=4.71239 EndAngle=7.85398
    g13: ArcOfCircle CenterX=-1.5 CenterY=62 CenterZ=0 NormalX=0 NormalY=0 NormalZ=1 AngleXU=0 Radius=1.5 StartAngle=4.71239 EndAngle=7.85398
    g14: ArcOfCircle CenterX=-1.5 CenterY=56.25 CenterZ=0 NormalX=0 NormalY=0 NormalZ=1 AngleXU=0 Radius=1.5 StartAngle=4.71239 EndAngle=7.85398
    g15: ArcOfCircle CenterX=-11.49 CenterY=50.5 CenterZ=0 NormalX=0 NormalY=0 NormalZ=1 AngleXU=0 Radius=1.5 StartAngle=4.71239 EndAngle=7.85398
    g16: ArcOfCircle CenterX=-16.28 CenterY=44.75 CenterZ=0 NormalX=0 NormalY=0 NormalZ=1 AngleXU=0 Radius=1.5 StartAngle=4.71239 EndAngle=7.85398
    g17: ArcOfCircle CenterX=-18.2337 CenterY=39 CenterZ=0 NormalX=0 NormalY=0 NormalZ=1 AngleXU=0 Radius=1.5 StartAngle=4.71485 EndAngle=7.85398
    g18: ArcOfCircle CenterX=-16.2837 CenterY=27.25 CenterZ=0 NormalX=0 NormalY=0 NormalZ=1 AngleXU=0 Radius=1.5 StartAngle=4.71485 EndAngle=7.85398
    g19: ArcOfCircle CenterX=-18.2337 CenterY=33 CenterZ=0 NormalX=0 NormalY=0 NormalZ=1 AngleXU=0 Radius=1.5 StartAngle=4.71485 EndAngle=7.85398
    g20: ArcOfCircle CenterX=-11.49 CenterY=21.5 CenterZ=0 NormalX=0 NormalY=0 NormalZ=1 AngleXU=0 Radius=1.5 StartAngle=4.71239 EndAngle=7.85398
    g21: ArcOfCircle CenterX=-1.5 CenterY=4.25 CenterZ=0 NormalX=0 NormalY=0 NormalZ=1 AngleXU=0 Radius=1.5 StartAngle=4.71239 EndAngle=7.85398
    g22: ArcOfCircle CenterX=-1.5 CenterY=10 CenterZ=0 NormalX=0 NormalY=0 NormalZ=1 AngleXU=0 Radius=1.5 StartAngle=4.71239 EndAngle=7.85398
    g23: ArcOfCircle CenterX=-1.5 CenterY=15.75 CenterZ=0 NormalX=0 NormalY=0 NormalZ=1 AngleXU=0 Radius=1.5 StartAngle=4.71239 EndAngle=7.85398
    g24: LineSegment StartX=-49.19 StartY=69.25 StartZ=0 EndX=-1.5 EndY=69.25 EndZ=0
    g25: LineSegment StartX=-49.19 StartY=66.25 StartZ=0 EndX=-1.5 EndY=66.25 EndZ=0
    g26: LineSegment StartX=-49.19 StartY=63.5 StartZ=0 EndX=-1.5 EndY=63.5 EndZ=0
    g27: LineSegment StartX=-49.19 StartY=60.5 StartZ=0 EndX=-1.5 EndY=60.5 EndZ=0
    g28: LineSegment StartX=-49.19 StartY=57.75 StartZ=0 EndX=-1.5 EndY=57.75 EndZ=0
    g29: LineSegment StartX=-49.19 StartY=54.75 StartZ=0 EndX=-1.5 EndY=54.75 EndZ=0
    g30: LineSegment StartX=-49.19 StartY=52 StartZ=0 EndX=-11.49 EndY=52 EndZ=0
    g31: LineSegment StartX=-49.19 StartY=49 StartZ=0 EndX=-11.49 EndY=49 EndZ=0
    g32: LineSegment StartX=-49.19 StartY=46.25 StartZ=0 EndX=-16.28 EndY=46.25 EndZ=0
    g33: LineSegment StartX=-49.19 StartY=43.25 StartZ=0 EndX=-16.28 EndY=43.25 EndZ=0
    g34: LineSegment StartX=-49.19 StartY=40.5 StartZ=0 EndX=-18.2337 EndY=40.5 EndZ=0
    g35: LineSegment StartX=-49.19 StartY=37.5 StartZ=0 EndX=-18.23 EndY=37.5 EndZ=0
    g36: LineSegment StartX=-49.19 StartY=34.5 StartZ=0 EndX=-18.2337 EndY=34.5 EndZ=0
    g37: LineSegment StartX=-49.19 StartY=31.5 StartZ=0 EndX=-18.23 EndY=31.5 EndZ=0
    g38: LineSegment StartX=-49.19 StartY=28.75 StartZ=0 EndX=-16.2837 EndY=28.75 EndZ=0
    g39: LineSegment StartX=-49.19 StartY=25.75 StartZ=0 EndX=-16.28 EndY=25.75 EndZ=0
    g40: LineSegment StartX=-49.19 StartY=23 StartZ=0 EndX=-11.49 EndY=23 EndZ=0
    g41: LineSegment StartX=-49.19 StartY=20 StartZ=0 EndX=-11.49 EndY=20 EndZ=0
    g42: LineSegment StartX=-49.19 StartY=17.25 StartZ=0 EndX=-1.5 EndY=17.25 EndZ=0
    g43: LineSegment StartX=-49.19 StartY=14.25 StartZ=0 EndX=-1.5 EndY=14.25 EndZ=0
    g44: LineSegment StartX=-49.19 StartY=11.5 StartZ=0 EndX=-1.5 EndY=11.5 EndZ=0
    g45: LineSegment StartX=-49.19 StartY=8.5 StartZ=0 EndX=-1.5 EndY=8.5 EndZ=0
    g46: LineSegment StartX=-49.19 StartY=5.75 StartZ=0 EndX=-1.5 EndY=5.75 EndZ=0
    g47: LineSegment StartX=-49.19 StartY=2.75 StartZ=0 EndX=-1.5 EndY=2.75 EndZ=0
  constraints (120):
    c: Vertical(g0)
    c: Distance(g0) = 3
    c: Block(g0)
    c: Vertical(g1)
    c: Distance(g1) = 3
    c: Vertical(g2)
    c: Equal(g0,g2) = 3
    c: Block(g2)
    c: Vertical(g3)
    c: Equal(g1,g3) = 3
    c: Vertical(g4)
    c: Equal(g0,g4) = 3
    c: Block(g4)
    c: Vertical(g5)
    c: Equal(g1,g5) = 3
    c: Vertical(g6)
    c: Equal(g0,g6) = 3
    c: Block(g6)
    c: Vertical(g7)
    c: Equal(g1,g7) = 3
    c: Vertical(g8)
    c: Equal(g0,g8) = 3
    c: Block(g8)
    c: Vertical(g9)
    c: Equal(g1,g9) = 3
    c: Vertical(g10)
    c: Equal(g0,g10) = 3
    c: Block(g10)
    c: Vertical(g11)
    c: Equal(g1,g11) = 3
    c: Block(g12)
    c: Block(g13)
    c: Block(g14)
    c: Block(g15)
    c: Block(g16)
    c: Block(g17)
    c: Block(g18)
    c: Block(g19)
    c: Block(g20)
    c: Block(g21)
    c: Block(g22)
    c: Block(g23)
    c: Block(g11)
    c: Block(g9)
    c: Block(g7)
    c: Block(g5)
    c: Block(g3)
    c: Block(g1)
    c: Coincident(g24,g0)
    c: Coincident(g24,g12)
    c: Horizontal(g24)
    c: Coincident(g25,g0)
    c: Coincident(g25,g12)
    c: Horizontal(g25)
    c: Coincident(g26,g1)
    c: Coincident(g26,g13)
    c: Horizontal(g26)
    c: Coincident(g27,g1)
    c: Coincident(g27,g13)
    c: Horizontal(g27)
    c: Coincident(g28,g2)
    c: Coincident(g28,g14)
    c: Horizontal(g28)
    c: Coincident(g29,g2)
    c: Coincident(g29,g14)
    c: Horizontal(g29)
    c: Coincident(g30,g3)
    c: Coincident(g30,g15)
    c: Horizontal(g30)
    c: Coincident(g31,g3)
    c: Coincident(g31,g15)
    c: Horizontal(g31)
    c: Coincident(g32,g4)
    c: Coincident(g32,g16)
    c: Horizontal(g32)
    c: Coincident(g33,g4)
    c: Coincident(g33,g16)
    c: Horizontal(g33)
    c: Coincident(g34,g5)
    c: Coincident(g34,g17)
    c: Horizontal(g34)
    c: Coincident(g35,g5)
    c: Coincident(g35,g17)
    c: Horizontal(g35)
    c: Coincident(g36,g6)
    c: Coincident(g36,g19)
    c: Horizontal(g36)
    c: Coincident(g37,g6)
    c: Coincident(g37,g19)
    c: Horizontal(g37)
    c: Coincident(g38,g7)
    c: Coincident(g38,g18)
    c: Horizontal(g38)
    c: Coincident(g39,g7)
    c: Coincident(g39,g18)
    c: Horizontal(g39)
    c: Coincident(g40,g8)
    c: Coincident(g40,g20)
    c: Horizontal(g40)
    c: Coincident(g41,g8)
    c: Coincident(g41,g20)
    c: Horizontal(g41)
    c: Coincident(g42,g9)
    c: Coincident(g42,g23)
    c: Horizontal(g42)
    c: Coincident(g43,g9)
    c: Coincident(g43,g23)
    c: Horizontal(g43)
    c: Coincident(g44,g10)
    c: Coincident(g44,g22)
    c: Horizontal(g44)
    c: Coincident(g45,g10)
    c: Coincident(g45,g22)
    c: Horizontal(g45)
    c: Coincident(g46,g11)
    c: Coincident(g46,g21)
    c: Horizontal(g46)
    c: Coincident(g47,g11)
    c: Coincident(g47,g21)
    c: Horizontal(g47)
FEATURE [Part::Extrusion] Extrude023
  Base = -> Sketch032
  Dir = (1,-2e-16,2e-16)
  DirMode = 2
  FaceMakerClass = Part::FaceMakerBullseye
  LengthFwd = 19
  LengthRev = 0
  Placement = pos=(-19,0,0) rot=(0,0,1;0rad)
  Solid = true
  Symmetric = false
FEATURE [Part::Fillet] Fillet023
  Base = -> Extrude023
  Edges = <same value as first occurrence — deduplicated (x6 in doc)>
  Placement = pos=(0,0.05,0) rot=(0,0,1;0rad)
FEATURE [Part::Cut] Cut014  label="bottom003"
  Base = -> Cut007
  Tool = -> Fusion047
FEATURE [Part::Cut] Cut021  label="bottom004"
  Base = -> Cut014
  Tool = -> Fillet023
FEATURE [Sketcher::SketchObject] Sketch033
  FullyConstrained = true
  Placement = pos=(117,19,0) rot=(0.57735,0.57735,0.57735;2.0944rad)
  sketch-geometry (8):
    g0: LineSegment StartX=-49.19 StartY=69.25 StartZ=0 EndX=-49.19 EndY=66.25 EndZ=0
    g1: LineSegment StartX=-49.19 StartY=5.75 StartZ=0 EndX=-49.19 EndY=2.75 EndZ=0
    g2: ArcOfCircle CenterX=-1.5 CenterY=67.75 CenterZ=0 NormalX=0 NormalY=0 NormalZ=1 AngleXU=0 Radius=1.5 StartAngle=4.71239 EndAngle=7.85398
    g3: ArcOfCircle CenterX=-1.5 CenterY=4.25 CenterZ=0 NormalX=0 NormalY=0 NormalZ=1 AngleXU=0 Radius=1.5 StartAngle=4.71239 EndAngle=7.85398
    g4: LineSegment StartX=-49.19 StartY=69.25 StartZ=0 EndX=-1.5 EndY=69.25 EndZ=0
    g5: LineSegment StartX=-49.19 StartY=66.25 StartZ=0 EndX=-1.5 EndY=66.25 EndZ=0
    g6: LineSegment StartX=-49.19 StartY=5.75 StartZ=0 EndX=-1.5 EndY=5.75 EndZ=0
    g7: LineSegment StartX=-49.19 StartY=2.75 StartZ=0 EndX=-1.5 EndY=2.75 EndZ=0
  constraints (19):
    c: Vertical(g0)
    c: Distance(g0) = 3
    c: Block(g0)
    c: Vertical(g1)
    c: Block(g2)
    c: Block(g3)
    c: Block(g1)
    c: Coincident(g4,g0)
    c: Coincident(g4,g2)
    c: Horizontal(g4)
    c: Coincident(g5,g0)
    c: Coincident(g5,g2)
    c: Horizontal(g5)
    c: Coincident(g6,g1)
    c: Coincident(g6,g3)
    c: Horizontal(g6)
    c: Coincident(g7,g1)
    c: Coincident(g7,g3)
    c: Horizontal(g7)
FEATURE [Sketcher::SketchObject] Sketch034
  FullyConstrained = true
  Placement = pos=(117,19,0) rot=(0.57735,0.57735,0.57735;2.0944rad)
  sketch-geometry (8):
    g0: LineSegment StartX=-49.19 StartY=63.5 StartZ=0 EndX=-49.19 EndY=60.5 EndZ=0
    g1: LineSegment StartX=-49.19 StartY=11.5 StartZ=0 EndX=-49.19 EndY=8.5 EndZ=0
    g2: ArcOfCircle CenterX=-1.5 CenterY=62 CenterZ=0 NormalX=0 NormalY=0 NormalZ=1 AngleXU=0 Radius=1.5 StartAngle=4.71239 EndAngle=7.85398
    g3: ArcOfCircle CenterX=-1.5 CenterY=10 CenterZ=0 NormalX=0 NormalY=0 NormalZ=1 AngleXU=0 Radius=1.5 StartAngle=4.71239 EndAngle=7.85398
    g4: LineSegment StartX=-49.19 StartY=63.5 StartZ=0 EndX=-1.5 EndY=63.5 EndZ=0
    g5: LineSegment StartX=-49.19 StartY=60.5 StartZ=0 EndX=-1.5 EndY=60.5 EndZ=0
    g6: LineSegment StartX=-49.19 StartY=11.5 StartZ=0 EndX=-1.5 EndY=11.5 EndZ=0
    g7: LineSegment StartX=-49.19 StartY=8.5 StartZ=0 EndX=-1.5 EndY=8.5 EndZ=0
  constraints (19):
    c: Vertical(g0)
    c: Distance(g0) = 3
    c: Vertical(g1)
    c: Block(g1)
    c: Block(g2)
    c: Block(g3)
    c: Block(g0)
    c: Coincident(g4,g0)
    c: Coincident(g4,g2)
    c: Horizontal(g4)
    c: Coincident(g5,g0)
    c: Coincident(g5,g2)
    c: Horizontal(g5)
    c: Coincident(g6,g1)
    c: Coincident(g6,g3)
    c: Horizontal(g6)
    c: Coincident(g7,g1)
    c: Coincident(g7,g3)
    c: Horizontal(g7)
FEATURE [Part::Extrusion] Extrude024
  Base = -> Sketch033
  Dir = (1,0,0)
  DirMode = 2
  FaceMakerClass = Part::FaceMakerBullseye
  LengthFwd = 10
  LengthRev = 0
  Solid = true
  Symmetric = false
FEATURE [Part::Extrusion] Extrude025
  Base = -> Sketch034
  Dir = (1,0,0)
  DirMode = 2
  FaceMakerClass = Part::FaceMakerBullseye
  LengthFwd = 10
  LengthRev = 0
  Solid = true
  Symmetric = false
FEATURE [Part::Fillet] Fillet024  label="removeFromtMoreFrontCaseScrewRetainers"
  Base = -> Extrude024
  Edges = 4 edges r=1.49: [Edge6,Edge11,Edge18,Edge23]
  Placement = pos=(-11,0,0) rot=(0,0,1;0rad)
FEATURE [Part::Fillet] Fillet025  label="removeFromtMoreFrontCaseScrewRetainers001"
  Base = -> Extrude025
  Edges = 4 edges r=1.49: [Edge6,Edge11,Edge18,Edge23]
  Placement = pos=(-19,0,0) rot=(0,0,1;0rad)
FEATURE [Part::Cut] Cut022
  Base = -> Cut015
  Tool = -> Fillet025
FEATURE [Part::Cut] Cut023  label="screwRetainers"
  Base = -> Cut022
  Tool = -> Fillet024
FEATURE [Part::MultiFuse] Fusion056  label="bottom005"
  Shapes = -> [Fusion044,Cut021]
FEATURE [Part::MultiFuse] Fusion057  label="casePillars001"
  Shapes = -> [Cut016,Fusion052]
FEATURE [Part::MultiFuse] Fusion058  label="bottom006"
  Shapes = -> [Fusion056,Cut023]
FEATURE [Part::MultiFuse] Fusion059  label="bottom007"
  Shapes = -> [Fusion058,Fillet005]
FEATURE [Part::MultiFuse] Fusion060  label="bottom008"
  Shapes = -> [Fusion059,Fusion]
FEATURE [Part::MultiFuse] Fusion061  label="top011"
  Shapes = -> [Cut006,Cut020]
FEATURE [Part::MultiFuse] Fusion062  label="top012"
  Shapes = -> [Fusion057,Fusion061]
FEATURE [Sketcher::SketchObject] Sketch035  label="topSketch007"
  FullyConstrained = true
  sketch-geometry (6):
    g0: LineSegment StartX=19 StartY=38 StartZ=0 EndX=117 EndY=38 EndZ=0
    g1: ArcOfCircle CenterX=19 CenterY=19 CenterZ=0 NormalX=0 NormalY=0 NormalZ=1 AngleXU=0 Radius=19 StartAngle=1.5708 EndAngle=3.14159
    g2: LineSegment StartX=117 StartY=38 StartZ=0 EndX=117 EndY=19 EndZ=0
    g3: LineSegment StartX=98 StartY=1.0161e-12 StartZ=0 EndX=5.22862e-06 EndY=1.0161e-12 EndZ=0
    g4: LineSegment StartX=5.22862e-06 StartY=19 StartZ=0 EndX=5.22862e-06 EndY=1.0161e-12 EndZ=0
    g5: ArcOfCircle CenterX=98 CenterY=19 CenterZ=0 NormalX=0 NormalY=0 NormalZ=1 AngleXU=0 Radius=19 StartAngle=4.71239 EndAngle=6.28319
  constraints (16):
    c: Horizontal(g0)
    c: Distance(g0) = 98
    c: Coincident(g1,g0)
    c: Block(g1)
    c: Coincident(g2,g0)
    c: Vertical(g2)
    c: Distance(g2) = 19
    c: Horizontal(g3)
    c: Coincident(g4,g1)
    c: Vertical(g4)
    c: Coincident(g3,g4)
    c: Block(g3)
    c: Coincident(g5,g2)
    c: Coincident(g5,g3)
    c: Block(g0)
    c: Block(g5)
FEATURE [Part::Extrusion] Extrude026  label="sideA001"
  Base = -> Sketch035
  Dir = (0,0,1)
  DirMode = 2
  FaceMakerClass = Part::FaceMakerBullseye
  LengthFwd = 3
  LengthRev = 0
  Placement = pos=(0,0,-2.7) rot=(0,0,1;0rad)
  Solid = true
  Symmetric = false
FEATURE [Sketcher::SketchObject] Sketch036  label="topSketch008"
  FullyConstrained = true
  sketch-geometry (6):
    g0: LineSegment StartX=19 StartY=38 StartZ=0 EndX=117 EndY=38 EndZ=0
    g1: ArcOfCircle CenterX=19 CenterY=19 CenterZ=0 NormalX=0 NormalY=0 NormalZ=1 AngleXU=0 Radius=19 StartAngle=1.5708 EndAngle=3.14159
    g2: LineSegment StartX=117 StartY=38 StartZ=0 EndX=117 EndY=19 EndZ=0
    g3: LineSegment StartX=98 StartY=1.0161e-12 StartZ=0 EndX=5.22862e-06 EndY=1.0161e-12 EndZ=0
    g4: LineSegment StartX=5.22862e-06 StartY=19 StartZ=0 EndX=5.22862e-06 EndY=1.0161e-12 EndZ=0
    g5: ArcOfCircle CenterX=98 CenterY=19 CenterZ=0 NormalX=0 NormalY=0 NormalZ=1 AngleXU=0 Radius=19 StartAngle=4.71239 EndAngle=6.28319
  constraints (16):
    c: Horizontal(g0)
    c: Distance(g0) = 98
    c: Coincident(g1,g0)
    c: Block(g1)
    c: Coincident(g2,g0)
    c: Vertical(g2)
    c: Distance(g2) = 19
    c: Horizontal(g3)
    c: Coincident(g4,g1)
    c: Vertical(g4)
    c: Coincident(g3,g4)
    c: Block(g3)
    c: Coincident(g5,g2)
    c: Coincident(g5,g3)
    c: Block(g0)
    c: Block(g5)
FEATURE [Part::Extrusion] Extrude027  label="sideB001"
  Base = -> Sketch036
  Dir = (0,0,1)
  DirMode = 2
  FaceMakerClass = Part::FaceMakerBullseye
  LengthFwd = 3
  LengthRev = 0
  Placement = pos=(0,0,71.7) rot=(0,0,1;0rad)
  Solid = true
  Symmetric = false
FEATURE [Part::MultiFuse] Fusion064  label="removeFromBottom"
  Shapes = -> [Extrude026,Extrude027]
FEATURE [Part::Cut] Cut024  label="bottom009"
  Base = -> Fusion060
  Tool = -> Fusion064
FEATURE [Sketcher::SketchObject] Sketch037  label="topSketch009"
  FullyConstrained = true
  sketch-geometry (8):
    g0: ArcOfCircle CenterX=19 CenterY=19.1201 CenterZ=0 NormalX=0 NormalY=0 NormalZ=1 AngleXU=0 Radius=18.8799 StartAngle=1.5708 EndAngle=3.14793
    g1: LineSegment StartX=0.120501 StartY=19.0004 StartZ=0 EndX=0.120501 EndY=0.000382114 EndZ=0
    g2: LineSegment StartX=19 StartY=38 StartZ=0 EndX=124 EndY=38 EndZ=0
    g3: LineSegment StartX=0.120501 StartY=0.000382114 StartZ=0 EndX=105.121 EndY=0.000382114 EndZ=0
    g4: LineSegment StartX=124 StartY=38 StartZ=0 EndX=125.616 EndY=38 EndZ=0
    g5: LineSegment StartX=105.121 StartY=0.000382114 StartZ=0 EndX=106.736 EndY=0.000382114 EndZ=0
    g6: ArcOfCircle CenterX=106.616 CenterY=19 CenterZ=0 NormalX=0 NormalY=0 NormalZ=1 AngleXU=0 Radius=19 StartAngle=4.71873 EndAngle=6.28319
    g7: LineSegment StartX=125.616 StartY=38 StartZ=0 EndX=125.616 EndY=19 EndZ=0
  constraints (21):
    c: Block(g0)
    c: Coincident(g1,g0)
    c: Vertical(g1)
    c: Horizontal(g2)
    c: Distance(g2) = 105
    c: Coincident(g2,g0)
    c: Distance(g1) = 19
    c: Coincident(g3,g1)
    c: Horizontal(g3)
    c: Distance(g3) = 105
    c: Coincident(g4,g2)
    c: Horizontal(g4)
    c: Distance(g4) = 1.61553
    c: Horizontal(g5)
    c: Equal(g4,g5) = 1.61553
    c: Coincident(g5,g3)
    c: Block(g6)
    c: Coincident(g6,g5)
    c: Coincident(g7,g4)
    c: Coincident(g7,g6)
    c: Vertical(g7)
FEATURE [Part::Extrusion] Extrude028  label="sideB"
  Base = -> Sketch037
  Dir = (0,0,1)
  DirMode = 2
  FaceMakerClass = Part::FaceMakerBullseye
  LengthFwd = 3
  LengthRev = 0
  Placement = pos=(0,0,72) rot=(0,0,1;0rad)
  Solid = true
  Symmetric = false
FEATURE [Sketcher::SketchObject] Sketch038  label="topSketch010"
  FullyConstrained = true
  sketch-geometry (22):
    g0: LineSegment StartX=5.21097e-06 StartY=3 StartZ=0 EndX=5.21097e-06 EndY=19 EndZ=0
    g1: ArcOfCircle CenterX=19 CenterY=19 CenterZ=0 NormalX=0 NormalY=0 NormalZ=1 AngleXU=0 Radius=19 StartAngle=1.5708 EndAngle=3.14159
    g2: ArcOfCircle CenterX=19 CenterY=19 CenterZ=0 NormalX=0 NormalY=0 NormalZ=1 AngleXU=0 Radius=16 StartAngle=1.5708 EndAngle=3.14159
    g3: LineSegment StartX=114 StartY=35 StartZ=0 EndX=19 EndY=35 EndZ=0
    g4: LineSegment StartX=5.21097e-06 StartY=3 StartZ=0 EndX=5.21097e-06 EndY=0 EndZ=0
    g5: LineSegment StartX=3 StartY=0 StartZ=0 EndX=5.21097e-06 EndY=0 EndZ=0
    g6: LineSegment StartX=3 StartY=19 StartZ=0 EndX=3 EndY=0 EndZ=0
    g7: LineSegment StartX=19 StartY=38 StartZ=0 EndX=124 EndY=38 EndZ=0
    g8: Circle CenterX=119 CenterY=35 CenterZ=0 NormalX=0 NormalY=0 NormalZ=1 AngleXU=0 Radius=1
    g9: Circle CenterX=121 CenterY=35 CenterZ=0 NormalX=0 NormalY=0 NormalZ=1 AngleXU=0 Radius=1
    g10: Circle CenterX=121 CenterY=33 CenterZ=0 NormalX=0 NormalY=0 NormalZ=1 AngleXU=0 Radius=1
    g11: BSplineCurve PolesCount=3 KnotsCount=2 Degree=2 IsPeriodic=0
    g12: GeomPoint X=119 Y=35 Z=0
    g13: GeomPoint X=121 Y=33 Z=0
    g14: LineSegment StartX=119 StartY=35 StartZ=0 EndX=114 EndY=35 EndZ=0
    g15: ArcOfCircle CenterX=105 CenterY=19 CenterZ=0 NormalX=0 NormalY=0 NormalZ=1 AngleXU=0 Radius=16 StartAngle=5.60905 EndAngle=6.28319
    g16: LineSegment StartX=121 StartY=33 StartZ=0 EndX=121 EndY=19 EndZ=0
    g17: LineSegment StartX=117.5 StartY=9.01251 StartZ=0 EndX=121.163 EndY=9.0125 EndZ=0
    g18: ArcOfCircle CenterX=105 CenterY=19 CenterZ=0 NormalX=0 NormalY=0 NormalZ=1 AngleXU=0 Radius=20.6155 StartAngle=5.7297 EndAngle=6.28319
    g19: LineSegment StartX=121.163 StartY=9.0125 StartZ=0 EndX=122.538 EndY=8.16329 EndZ=0
    g20: LineSegment StartX=124 StartY=38 StartZ=0 EndX=125.616 EndY=38 EndZ=0
    g21: LineSegment StartX=125.616 StartY=19 StartZ=0 EndX=125.616 EndY=38 EndZ=0
  constraints (49):
    c: Vertical(g0)
    c: Block(g0)
    c: Coincident(g1,g0)
    c: Block(g1)
    c: Coincident(g2,g1)
    c: Block(g2)
    c: Coincident(g3,g2)
    c: Horizontal(g3)
    c: Tangent(g3,g2)
    c: Coincident(g4,g0)
    c: Distance(g4) = 3
    c: Vertical(g4)
    c: Coincident(g5,g4)
    c: Horizontal(g5)
    c: Coincident(g6,g2)
    c: Coincident(g6,g5)
    c: Vertical(g6)
    c: Horizontal(g7)
    c: Distance(g7) = 105
    c: Coincident(g7,g1)
    c: Block(g3)
    c: Weight(g8) = 1
    c: Equal(g8,g9)
    c: Equal(g8,g10)
    c: InternalAlignment(g8,g11)
    c: InternalAlignment(g9,g11)
    c: InternalAlignment(g10,g11)
    c: InternalAlignment(g12,g11)
    c: InternalAlignment(g13,g11)
    c: Block(g11)
    c: Coincident(g14,g11)
    c: Coincident(g14,g3)
    c: Horizontal(g14)
    c: Block(g15)
    c: Coincident(g16,g11)
    c: Coincident(g16,g15)
    c: Vertical(g16)
    c: Distance(g16) = 14
    c: Coincident(g17,g15)
    c: Block(g18)
    c: Coincident(g19,g18)
    c: Coincident(g20,g7)
    c: Horizontal(g20)
    c: Vertical(g21)
    c: Coincident(g20,g21)
    c: Block(g20)
    c: Block(g21)
    c: Block(g19)
    c: Block(g17)
FEATURE [Part::Extrusion] Extrude029
  Base = -> Sketch038
  Dir = (0,0,1)
  DirMode = 2
  FaceMakerClass = Part::FaceMakerBullseye
  LengthFwd = 72
  LengthRev = 0
  Solid = true
  Symmetric = false
FEATURE [Part::Feature] Face085
  shape: bbox 4.8 x 25.5 x 2e-07 mm, 1 faces, 0 solids (baked)
FEATURE [Part::Revolution] Revolve089  label="moreFrontCaseScrewPost003"
  Angle = 360
  Axis = (0,1,0)
  Base = (0,0,0)
  FaceMakerClass = Part::FaceMakerBullseye
  Placement = pos=(109.5,4.5,3.5) rot=(0,0,1;0rad)
  Solid = false
  Source = -> Face085
  Symmetric = false
FEATURE [Part::Feature] Face086
  shape: bbox 4.8 x 25.5 x 2e-07 mm, 1 faces, 0 solids (baked)
FEATURE [Part::Revolution] Revolve090  label="moreFrontCaseScrewPost004"
  Angle = 360
  Axis = (0,1,0)
  Base = (0,0,0)
  FaceMakerClass = Part::FaceMakerBullseye
  Placement = pos=(109.5,4.5,68.5) rot=(0,0,1;0rad)
  Solid = false
  Source = -> Face086
  Symmetric = false
FEATURE [Part::Fillet] Fillet026  label="top013"
  Base = -> Extrude029
  Edges = 1 edges r=2: [Edge35]
FEATURE [Sketcher::SketchObject] Sketch039
  FullyConstrained = true
  sketch-geometry (7):
    g0: LineSegment StartX=0 StartY=0 StartZ=0 EndX=0 EndY=6 EndZ=0
    g1: Circle CenterX=0 CenterY=0 CenterZ=0 NormalX=0 NormalY=0 NormalZ=1 AngleXU=0 Radius=1
    g2: Circle CenterX=8 CenterY=6 CenterZ=0 NormalX=0 NormalY=0 NormalZ=1 AngleXU=0 Radius=1
    g3: BSplineCurve PolesCount=3 KnotsCount=2 Degree=2 IsPeriodic=0
    g4: GeomPoint X=0 Y=0 Z=0
    g5: GeomPoint X=8 Y=6 Z=0
    g6: LineSegment StartX=0 StartY=6 StartZ=0 EndX=8 EndY=6 EndZ=0
  constraints (14):
    c: Coincident(g0,g-1)
    c: Distance(g0) = 6
    c: Vertical(g0)
    c: Coincident(g3,g0)
    c: Weight(g1) = 1
    c: Equal(g1,g2)
    c: InternalAlignment(g1,g3)
    c: InternalAlignment(g2,g3)
    c: InternalAlignment(g4,g3)
    c: InternalAlignment(g5,g3)
    c: Block(g3)
    c: Coincident(g6,g0)
    c: Coincident(g6,g3)
    c: Horizontal(g6)
FEATURE [Sketcher::SketchObject] Sketch040
  FullyConstrained = true
  sketch-geometry (7):
    g0: LineSegment StartX=0 StartY=0 StartZ=0 EndX=0 EndY=6 EndZ=0
    g1: Circle CenterX=0 CenterY=0 CenterZ=0 NormalX=0 NormalY=0 NormalZ=1 AngleXU=0 Radius=1
    g2: Circle CenterX=8 CenterY=6 CenterZ=0 NormalX=0 NormalY=0 NormalZ=1 AngleXU=0 Radius=1
    g3: BSplineCurve PolesCount=3 KnotsCount=2 Degree=2 IsPeriodic=0
    g4: GeomPoint X=0 Y=0 Z=0
    g5: GeomPoint X=8 Y=6 Z=0
    g6: LineSegment StartX=0 StartY=6 StartZ=0 EndX=8 EndY=6 EndZ=0
  constraints (14):
    c: Coincident(g0,g-1)
    c: Distance(g0) = 6
    c: Vertical(g0)
    c: Coincident(g3,g0)
    c: Weight(g1) = 1
    c: Equal(g1,g2)
    c: InternalAlignment(g1,g3)
    c: InternalAlignment(g2,g3)
    c: InternalAlignment(g4,g3)
    c: InternalAlignment(g5,g3)
    c: Block(g3)
    c: Coincident(g6,g0)
    c: Coincident(g6,g3)
    c: Horizontal(g6)
FEATURE [Sketcher::SketchObject] Sketch041
  FullyConstrained = true
  sketch-geometry (7):
    g0: LineSegment StartX=0 StartY=0 StartZ=0 EndX=0 EndY=6 EndZ=0
    g1: Circle CenterX=0 CenterY=0 CenterZ=0 NormalX=0 NormalY=0 NormalZ=1 AngleXU=0 Radius=1
    g2: Circle CenterX=8 CenterY=6 CenterZ=0 NormalX=0 NormalY=0 NormalZ=1 AngleXU=0 Radius=1
    g3: BSplineCurve PolesCount=3 KnotsCount=2 Degree=2 IsPeriodic=0
    g4: GeomPoint X=0 Y=0 Z=0
    g5: GeomPoint X=8 Y=6 Z=0
    g6: LineSegment StartX=0 StartY=6 StartZ=0 EndX=8 EndY=6 EndZ=0
  constraints (14):
    c: Coincident(g0,g-1)
    c: Distance(g0) = 6
    c: Vertical(g0)
    c: Coincident(g3,g0)
    c: Weight(g1) = 1
    c: Equal(g1,g2)
    c: InternalAlignment(g1,g3)
    c: InternalAlignment(g2,g3)
    c: InternalAlignment(g4,g3)
    c: InternalAlignment(g5,g3)
    c: Block(g3)
    c: Coincident(g6,g0)
    c: Coincident(g6,g3)
    c: Horizontal(g6)
FEATURE [Sketcher::SketchObject] Sketch042
  FullyConstrained = true
  sketch-geometry (7):
    g0: LineSegment StartX=0 StartY=0 StartZ=0 EndX=0 EndY=6 EndZ=0
    g1: Circle CenterX=0 CenterY=0 CenterZ=0 NormalX=0 NormalY=0 NormalZ=1 AngleXU=0 Radius=1
    g2: Circle CenterX=8 CenterY=6 CenterZ=0 NormalX=0 NormalY=0 NormalZ=1 AngleXU=0 Radius=1
    g3: BSplineCurve PolesCount=3 KnotsCount=2 Degree=2 IsPeriodic=0
    g4: GeomPoint X=0 Y=0 Z=0
    g5: GeomPoint X=8 Y=6 Z=0
    g6: LineSegment StartX=0 StartY=6 StartZ=0 EndX=8 EndY=6 EndZ=0
  constraints (14):
    c: Coincident(g0,g-1)
    c: Distance(g0) = 6
    c: Vertical(g0)
    c: Coincident(g3,g0)
    c: Weight(g1) = 1
    c: Equal(g1,g2)
    c: InternalAlignment(g1,g3)
    c: InternalAlignment(g2,g3)
    c: InternalAlignment(g4,g3)
    c: InternalAlignment(g5,g3)
    c: Block(g3)
    c: Coincident(g6,g0)
    c: Coincident(g6,g3)
    c: Horizontal(g6)
FEATURE [Part::Extrusion] Extrude030  label="caseScrewPillarBracket008"
  Base = -> Sketch039
  Dir = (0,0,1)
  DirMode = 2
  FaceMakerClass = Part::FaceMakerBullseye
  LengthFwd = 2.4
  LengthRev = 0
  Placement = pos=(15.76,29,8.8) rot=(0,1,0;0rad)
  Solid = true
  Symmetric = false
FEATURE [Part::Extrusion] Extrude031  label="caseScrewPillarBracket009"
  Base = -> Sketch040
  Dir = (0,0,1)
  DirMode = 2
  FaceMakerClass = Part::FaceMakerBullseye
  LengthFwd = 2.4
  LengthRev = 0
  Placement = pos=(15.76,29,60.8) rot=(0,0,1;0rad)
  Solid = true
  Symmetric = false
FEATURE [Part::Extrusion] Extrude032  label="caseScrewPillarBracket010"
  Base = -> Sketch041
  Dir = (0,0,1)
  DirMode = 2
  FaceMakerClass = Part::FaceMakerBullseye
  LengthFwd = 2.4
  LengthRev = 0
  Placement = pos=(13.7,29,13.26) rot=(0,-1,0;1.5708rad)
  Solid = true
  Symmetric = false
FEATURE [Part::Extrusion] Extrude033  label="caseScrewPillarBracket011"
  Base = -> Sketch042
  Dir = (0,0,1)
  DirMode = 2
  FaceMakerClass = Part::FaceMakerBullseye
  LengthFwd = 2.4
  LengthRev = 0
  Placement = pos=(11.3,29,58.74) rot=(0,1,0;1.5708rad)
  Solid = true
  Symmetric = false
FEATURE [Sketcher::SketchObject] Sketch043
  FullyConstrained = true
  sketch-geometry (7):
    g0: LineSegment StartX=0 StartY=0 StartZ=0 EndX=0 EndY=6 EndZ=0
    g1: Circle CenterX=0 CenterY=0 CenterZ=0 NormalX=0 NormalY=0 NormalZ=1 AngleXU=0 Radius=1
    g2: Circle CenterX=8 CenterY=6 CenterZ=0 NormalX=0 NormalY=0 NormalZ=1 AngleXU=0 Radius=1
    g3: BSplineCurve PolesCount=3 KnotsCount=2 Degree=2 IsPeriodic=0
    g4: GeomPoint X=0 Y=0 Z=0
    g5: GeomPoint X=8 Y=6 Z=0
    g6: LineSegment StartX=0 StartY=6 StartZ=0 EndX=8 EndY=6 EndZ=0
  constraints (14):
    c: Coincident(g0,g-1)
    c: Distance(g0) = 6
    c: Vertical(g0)
    c: Coincident(g3,g0)
    c: Weight(g1) = 1
    c: Equal(g1,g2)
    c: InternalAlignment(g1,g3)
    c: InternalAlignment(g2,g3)
    c: InternalAlignment(g4,g3)
    c: InternalAlignment(g5,g3)
    c: Block(g3)
    c: Coincident(g6,g0)
    c: Coincident(g6,g3)
    c: Horizontal(g6)
FEATURE [Part::Extrusion] Extrude034  label="caseScrewPillarBracket012"
  Base = -> Sketch043
  Dir = (0,0,1)
  DirMode = 2
  FaceMakerClass = Part::FaceMakerBullseye
  LengthFwd = 2.4
  LengthRev = 0
  Placement = pos=(88.3,29,65.23) rot=(0,1,0;1.5708rad)
  Solid = true
  Symmetric = false
FEATURE [Sketcher::SketchObject] Sketch044
  FullyConstrained = true
  sketch-geometry (7):
    g0: LineSegment StartX=0 StartY=0 StartZ=0 EndX=0 EndY=6 EndZ=0
    g1: Circle CenterX=0 CenterY=0 CenterZ=0 NormalX=0 NormalY=0 NormalZ=1 AngleXU=0 Radius=1
    g2: Circle CenterX=8 CenterY=6 CenterZ=0 NormalX=0 NormalY=0 NormalZ=1 AngleXU=0 Radius=1
    g3: BSplineCurve PolesCount=3 KnotsCount=2 Degree=2 IsPeriodic=0
    g4: GeomPoint X=0 Y=0 Z=0
    g5: GeomPoint X=8 Y=6 Z=0
    g6: LineSegment StartX=0 StartY=6 StartZ=0 EndX=8 EndY=6 EndZ=0
  constraints (14):
    c: Coincident(g0,g-1)
    c: Distance(g0) = 6
    c: Vertical(g0)
    c: Coincident(g3,g0)
    c: Weight(g1) = 1
    c: Equal(g1,g2)
    c: InternalAlignment(g1,g3)
    c: InternalAlignment(g2,g3)
    c: InternalAlignment(g4,g3)
    c: InternalAlignment(g5,g3)
    c: Block(g3)
    c: Coincident(g6,g0)
    c: Coincident(g6,g3)
    c: Horizontal(g6)
FEATURE [Part::Extrusion] Extrude035  label="caseScrewPillarBracket013"
  Base = -> Sketch044
  Dir = (0,0,1)
  DirMode = 2
  FaceMakerClass = Part::FaceMakerBullseye
  LengthFwd = 2.4
  LengthRev = 0
  Placement = pos=(90.7,29,6.77) rot=(0,-1,0;1.5708rad)
  Solid = true
  Symmetric = false
FEATURE [Sketcher::SketchObject] Sketch045
  FullyConstrained = true
  sketch-geometry (7):
    g0: LineSegment StartX=0 StartY=0 StartZ=0 EndX=0 EndY=6 EndZ=0
    g1: Circle CenterX=0 CenterY=0 CenterZ=0 NormalX=0 NormalY=0 NormalZ=1 AngleXU=0 Radius=1
    g2: Circle CenterX=8 CenterY=6 CenterZ=0 NormalX=0 NormalY=0 NormalZ=1 AngleXU=0 Radius=1
    g3: BSplineCurve PolesCount=3 KnotsCount=2 Degree=2 IsPeriodic=0
    g4: GeomPoint X=0 Y=0 Z=0
    g5: GeomPoint X=8 Y=6 Z=0
    g6: LineSegment StartX=0 StartY=6 StartZ=0 EndX=8 EndY=6 EndZ=0
  constraints (14):
    c: Coincident(g0,g-1)
    c: Distance(g0) = 6
    c: Vertical(g0)
    c: Coincident(g3,g0)
    c: Weight(g1) = 1
    c: Equal(g1,g2)
    c: InternalAlignment(g1,g3)
    c: InternalAlignment(g2,g3)
    c: InternalAlignment(g4,g3)
    c: InternalAlignment(g5,g3)
    c: Block(g3)
    c: Coincident(g6,g0)
    c: Coincident(g6,g3)
    c: Horizontal(g6)
FEATURE [Sketcher::SketchObject] Sketch046
  FullyConstrained = true
  sketch-geometry (7):
    g0: LineSegment StartX=0 StartY=0 StartZ=0 EndX=0 EndY=6 EndZ=0
    g1: Circle CenterX=0 CenterY=0 CenterZ=0 NormalX=0 NormalY=0 NormalZ=1 AngleXU=0 Radius=1
    g2: Circle CenterX=8 CenterY=6 CenterZ=0 NormalX=0 NormalY=0 NormalZ=1 AngleXU=0 Radius=1
    g3: BSplineCurve PolesCount=3 KnotsCount=2 Degree=2 IsPeriodic=0
    g4: GeomPoint X=0 Y=0 Z=0
    g5: GeomPoint X=8 Y=6 Z=0
    g6: LineSegment StartX=0 StartY=6 StartZ=0 EndX=8 EndY=6 EndZ=0
  constraints (14):
    c: Coincident(g0,g-1)
    c: Distance(g0) = 6
    c: Vertical(g0)
    c: Coincident(g3,g0)
    c: Weight(g1) = 1
    c: Equal(g1,g2)
    c: InternalAlignment(g1,g3)
    c: InternalAlignment(g2,g3)
    c: InternalAlignment(g4,g3)
    c: InternalAlignment(g5,g3)
    c: Block(g3)
    c: Coincident(g6,g0)
    c: Coincident(g6,g3)
    c: Horizontal(g6)
FEATURE [Part::Extrusion] Extrude036  label="caseScrewPillarBracket014"
  Base = -> Sketch045
  Dir = (0,0,1)
  DirMode = 2
  FaceMakerClass = Part::FaceMakerBullseye
  LengthFwd = 2.4
  LengthRev = 0
  Placement = pos=(110.7,29,6.77) rot=(0,-1,0;1.5708rad)
  Solid = true
  Symmetric = false
FEATURE [Part::Extrusion] Extrude037  label="caseScrewPillarBracket015"
  Base = -> Sketch046
  Dir = (0,0,1)
  DirMode = 2
  FaceMakerClass = Part::FaceMakerBullseye
  LengthFwd = 2.4
  LengthRev = 0
  Placement = pos=(108.3,29,65.23) rot=(0,1,0;1.5708rad)
  Solid = true
  Symmetric = false
FEATURE [Part::Box] Box013  label="frontCaseScrewPillarBracket002"
  AttacherType = Attacher::AttachEngine3D
  Height = 2.4
  Length = 22
  Placement = pos=(87,28,2.3) rot=(0,0,1;0rad)
  Width = 7
FEATURE [Part::Box] Box014  label="frontCaseScrewPillarBracket003"
  AttacherType = Attacher::AttachEngine3D
  Height = 2.4
  Length = 22
  Placement = pos=(87,28,67.3) rot=(0,0,1;0rad)
  Width = 7
FEATURE [Part::Feature] Face087
  shape: bbox 4.8 x 30.2 x 2e-07 mm, 1 faces, 0 solids (baked)
FEATURE [Part::Revolution] Revolve091  label="frontCaseScrewPost004"
  Angle = 360
  Axis = (0,1,0)
  Base = (0,0,0)
  FaceMakerClass = Part::FaceMakerBullseye
  Placement = pos=(89.5,4.5,3.5) rot=(0,0,1;0rad)
  Solid = false
  Source = -> Face087
  Symmetric = false
FEATURE [Part::Feature] Face088
  shape: bbox 4.8 x 30.2 x 2e-07 mm, 1 faces, 0 solids (baked)
FEATURE [Part::Revolution] Revolve092  label="frontCaseScrewPost005"
  Angle = 360
  Axis = (0,1,0)
  Base = (0,0,0)
  FaceMakerClass = Part::FaceMakerBullseye
  Placement = pos=(89.5,4.5,68.5) rot=(0,0,1;0rad)
  Solid = false
  Source = -> Face088
  Symmetric = false
FEATURE [Part::Feature] Face089
  shape: bbox 3.5 x 30.2 x 2e-07 mm, 1 faces, 0 solids (baked)
FEATURE [Part::Revolution] Revolve093  label="backCaseScrewPost002"
  Angle = 360
  Axis = (0,1,0)
  Base = (0,0,0)
  FaceMakerClass = Part::FaceMakerBullseye
  Placement = pos=(12.5,4.5,10) rot=(0,0,1;0rad)
  Solid = false
  Source = -> Face089
  Symmetric = false
FEATURE [Part::Feature] Face090
  shape: bbox 3.5 x 30.2 x 2e-07 mm, 1 faces, 0 solids (baked)
FEATURE [Part::Revolution] Revolve094  label="backCaseScrewPost003"
  Angle = 360
  Axis = (0,1,0)
  Base = (0,0,0)
  FaceMakerClass = Part::FaceMakerBullseye
  Placement = pos=(12.5,4.5,62) rot=(0,0,1;0rad)
  Solid = false
  Source = -> Face090
  Symmetric = false
FEATURE [Part::Box] Box015  label="Cube011"
  AttacherType = Attacher::AttachEngine3D
  Height = 28.8
  Length = 3
  Placement = pos=(107.3,28,21.6) rot=(0,0,1;0rad)
  Width = 7
FEATURE [Part::Box] Box016  label="Cube012"
  AttacherType = Attacher::AttachEngine3D
  Height = 3
  Length = 7.4
  Placement = pos=(107.3,28,18.6) rot=(0,0,1;0rad)
  Width = 7
FEATURE [Part::Box] Box017  label="Cube013"
  AttacherType = Attacher::AttachEngine3D
  Height = 3
  Length = 7.4
  Placement = pos=(107.3,28,50.4) rot=(0,0,1;0rad)
  Width = 7
FEATURE [Part::Cylinder] Cylinder024
  Angle = 360
  AttacherType = Attacher::AttachEngine3D
  Height = 20
  Placement = pos=(0,0,36.15) rot=(0,0,1;0rad)
  Radius = 14.3
FEATURE [Part::Cylinder] Cylinder025
  Angle = 360
  AttacherType = Attacher::AttachEngine3D
  Height = 10
  Placement = pos=(0,0,36.15) rot=(0,0,1;0rad)
  Radius = 4
FEATURE [Part::MultiFuse] Fusion066  label="removeToCreteHoleForPlugHousing009"
  Placement = pos=(70,19,36) rot=(0,1,0;1.5708rad)
  Shapes = -> [Cylinder024,Cylinder025]
FEATURE [Part::MultiFuse] Fusion065  label="plugHousingBracketHolder002"
  Shapes = -> [Box017,Box015,Box016]
FEATURE [Part::Cut] Cut025  label="plugHousingBracketHolder003"
  Base = -> Fusion065
  Placement = pos=(7,0,0) rot=(0,0,1;0rad)
  Tool = -> Fusion066
FEATURE [Sketcher::SketchObject] Sketch047
  FullyConstrained = false
  Placement = pos=(0,0,0) rot=(1,0,0;1.5708rad)
  sketch-geometry (24):
    g0: ArcOfCircle CenterX=-4 CenterY=-10.5 CenterZ=0 NormalX=0 NormalY=0 NormalZ=1 AngleXU=0 Radius=1.5 StartAngle=6e-16 EndAngle=3.14159
    g1: ArcOfCircle CenterX=-34.2 CenterY=-10.5 CenterZ=0 NormalX=0 NormalY=0 NormalZ=1 AngleXU=0 Radius=1.5 StartAngle=0 EndAngle=3.14159
    g2: ArcOfCircle CenterX=-34.2 CenterY=-27.7 CenterZ=0 NormalX=0 NormalY=0 NormalZ=1 AngleXU=0 Radius=1.5 StartAngle=3.14159 EndAngle=6.28319
    g3: ArcOfCircle CenterX=-4 CenterY=-27.7 CenterZ=0 NormalX=0 NormalY=0 NormalZ=1 AngleXU=0 Radius=1.5 StartAngle=3.1416 EndAngle=6.28319
    g4: ArcOfCircle CenterX=-10 CenterY=-4.3 CenterZ=0 NormalX=0 NormalY=0 NormalZ=1 AngleXU=0 Radius=1.5 StartAngle=2e-16 EndAngle=3.14159
    g5: ArcOfCircle CenterX=-16.1 CenterY=-1.8 CenterZ=0 NormalX=0 NormalY=0 NormalZ=1 AngleXU=0 Radius=1.5 StartAngle=5e-16 EndAngle=3.14159
    g6: ArcOfCircle CenterX=-22.1 CenterY=-1.8 CenterZ=0 NormalX=0 NormalY=0 NormalZ=1 AngleXU=0 Radius=1.5 StartAngle=5e-16 EndAngle=3.14159
    g7: ArcOfCircle CenterX=-28.2 CenterY=-4.3 CenterZ=0 NormalX=0 NormalY=0 NormalZ=1 AngleXU=0 Radius=1.5 StartAngle=2e-16 EndAngle=3.14159
    g8: ArcOfCircle CenterX=-10 CenterY=-33.9 CenterZ=0 NormalX=0 NormalY=0 NormalZ=1 AngleXU=0 Radius=1.5 StartAngle=3.14159 EndAngle=6.28319
    g9: ArcOfCircle CenterX=-16.1 CenterY=-36.4 CenterZ=0 NormalX=0 NormalY=0 NormalZ=1 AngleXU=0 Radius=1.5 StartAngle=3.14159 EndAngle=6.28319
    g10: ArcOfCircle CenterX=-22.1 CenterY=-36.4 CenterZ=0 NormalX=0 NormalY=0 NormalZ=1 AngleXU=0 Radius=1.5 StartAngle=3.14159 EndAngle=6.28319
    g11: ArcOfCircle CenterX=-28.2 CenterY=-33.9 CenterZ=0 NormalX=0 NormalY=0 NormalZ=1 AngleXU=0 Radius=1.5 StartAngle=3.14159 EndAngle=6.28319
    g12: LineSegment StartX=-35.7 StartY=-10.5 StartZ=0 EndX=-35.7 EndY=-27.7 EndZ=0
    g13: LineSegment StartX=-32.7 StartY=-10.5 StartZ=0 EndX=-32.7 EndY=-27.7 EndZ=0
    g14: LineSegment StartX=-29.7 StartY=-33.9 StartZ=0 EndX=-29.7 EndY=-4.3 EndZ=0
    g15: LineSegment StartX=-26.7 StartY=-33.9 StartZ=0 EndX=-26.7 EndY=-4.3 EndZ=0
    g16: LineSegment StartX=-2.5 StartY=-10.5 StartZ=0 EndX=-2.5 EndY=-27.7 EndZ=0
    g17: LineSegment StartX=-8.5 StartY=-4.3 StartZ=0 EndX=-8.5 EndY=-33.9 EndZ=0
    g18: LineSegment StartX=-5.5 StartY=-10.5 StartZ=0 EndX=-5.5 EndY=-27.7 EndZ=0
    g19: LineSegment StartX=-11.5 StartY=-4.3 StartZ=0 EndX=-11.5 EndY=-33.9 EndZ=0
    g20: LineSegment StartX=-14.6 StartY=-1.8 StartZ=0 EndX=-14.6 EndY=-36.4 EndZ=0
    g21: LineSegment StartX=-17.6 StartY=-1.8 StartZ=0 EndX=-17.6 EndY=-36.4 EndZ=0
    g22: LineSegment StartX=-20.6 StartY=-36.4 StartZ=0 EndX=-20.6 EndY=-1.8 EndZ=0
    g23: LineSegment StartX=-23.6 StartY=-1.8 StartZ=0 EndX=-23.6 EndY=-36.4 EndZ=0
  constraints (48):
    c: Block(g0)
    c: Block(g1)
    c: Block(g2)
    c: Block(g3)
    c: Block(g4)
    c: Block(g5)
    c: Block(g6)
    c: Block(g7)
    c: Block(g8)
    c: Block(g9)
    c: Block(g10)
    c: Block(g11)
    c: Coincident(g12,g1)
    c: Coincident(g12,g2)
    c: Vertical(g12)
    c: Coincident(g13,g1)
    c: Coincident(g13,g2)
    c: Vertical(g13)
    c: Coincident(g14,g11)
    c: Coincident(g14,g7)
    c: Vertical(g14)
    c: Coincident(g15,g11)
    c: Coincident(g15,g7)
    c: Vertical(g15)
    c: Coincident(g16,g0)
    c: Coincident(g16,g3)
    c: Vertical(g16)
    c: Coincident(g17,g4)
    c: Coincident(g17,g8)
    c: Vertical(g17)
    c: Coincident(g18,g0)
    c: Coincident(g18,g3)
    c: Vertical(g18)
    c: Coincident(g19,g4)
    c: Coincident(g19,g8)
    c: Vertical(g19)
    c: Coincident(g20,g5)
    c: Coincident(g20,g9)
    c: Vertical(g20)
    c: Coincident(g21,g5)
    c: Coincident(g21,g9)
    c: Vertical(g21)
    c: Coincident(g22,g10)
    c: Coincident(g22,g6)
    c: Vertical(g22)
    c: Coincident(g23,g6)
    c: Coincident(g23,g10)
    c: Vertical(g23)
FEATURE [Part::Extrusion] Extrude038  label="removeToCreateFanGrillHoles001"
  Base = -> Sketch047
  Dir = (0,-1,6e-16)
  DirMode = 2
  FaceMakerClass = Part::FaceMakerBullseye
  LengthFwd = 10
  LengthRev = 0
  Placement = pos=(65.4,44,54.82) rot=(0,0,1;0rad)
  Solid = true
  Symmetric = false
FEATURE [Part::Feature] Wire004
  shape: bbox 11 x 5.2 x 2e-07 mm, 0 faces, 0 solids (baked)
FEATURE [Part::Revolution] Revolve095
  Angle = 360
  Axis = (0,1,0)
  Base = (0,0,0)
  FaceMakerClass = Part::FaceMakerBullseye
  Placement = pos=(30.3,38,19.7) rot=(0,0,1;0rad)
  Solid = true
  Source = -> Wire004
  Symmetric = false
FEATURE [Part::Feature] Wire005
  shape: bbox 11 x 5.2 x 2e-07 mm, 0 faces, 0 solids (baked)
FEATURE [Part::Revolution] Revolve096
  Angle = 360
  Axis = (0,1,0)
  Base = (0,0,0)
  FaceMakerClass = Part::FaceMakerBullseye
  Placement = pos=(30.3,38,51.7) rot=(0,0,1;0rad)
  Solid = true
  Source = -> Wire005
  Symmetric = false
FEATURE [Part::Feature] Wire006
  shape: bbox 11 x 5.2 x 2e-07 mm, 0 faces, 0 solids (baked)
FEATURE [Part::Revolution] Revolve097
  Angle = 360
  Axis = (0,1,0)
  Base = (0,0,0)
  FaceMakerClass = Part::FaceMakerBullseye
  Placement = pos=(62.3,38,51.7) rot=(0,0,1;0rad)
  Solid = true
  Source = -> Wire006
  Symmetric = false
FEATURE [Part::Feature] Wire007
  shape: bbox 11 x 5.2 x 2e-07 mm, 0 faces, 0 solids (baked)
FEATURE [Part::Revolution] Revolve098
  Angle = 360
  Axis = (0,1,0)
  Base = (0,0,0)
  FaceMakerClass = Part::FaceMakerBullseye
  Placement = pos=(62.3,38,19.7) rot=(0,0,1;0rad)
  Solid = true
  Source = -> Wire007
  Symmetric = false
FEATURE [Part::MultiFuse] Fusion067  label="fanScrewHousing002"
  Shapes = -> [Revolve098,Revolve097,Revolve096,Revolve095]
FEATURE [Part::Feature] Face091 .. Face094  x4 (patterned run collapsed; names and placements below)
  shape: bbox 3.5 x 17.8 x 2e-07 mm, 1 faces, 0 solids (baked)
FEATURE [Part::Revolution] Revolve099  label="removeToCreateScrewAndThreadedInsertHole026"
  Angle = 360
  Axis = (0,1,0)
  Base = (0,0,0)
  FaceMakerClass = Part::FaceMakerBullseye
  Placement = pos=(62.3,30.3,19.7) rot=(0,0,1;0rad)
  Solid = false
  Source = -> Face091
  Symmetric = false
FEATURE [Part::Revolution] Revolve100  label="removeToCreateScrewAndThreadedInsertHole027"
  Angle = 360
  Axis = (0,1,0)
  Base = (0,0,0)
  FaceMakerClass = Part::FaceMakerBullseye
  Placement = pos=(62.3,30.3,51.7) rot=(0,0,1;0rad)
  Solid = false
  Source = -> Face092
  Symmetric = false
FEATURE [Part::Revolution] Revolve101  label="removeToCreateScrewAndThreadedInsertHole028"
  Angle = 360
  Axis = (0,1,0)
  Base = (0,0,0)
  FaceMakerClass = Part::FaceMakerBullseye
  Placement = pos=(30.3,30.3,19.7) rot=(0,0,1;0rad)
  Solid = false
  Source = -> Face093
  Symmetric = false
FEATURE [Part::Revolution] Revolve102  label="removeToCreateScrewAndThreadedInsertHole029"
  Angle = 360
  Axis = (0,1,0)
  Base = (0,0,0)
  FaceMakerClass = Part::FaceMakerBullseye
  Placement = pos=(30.3,30.3,51.7) rot=(0,0,1;0rad)
  Solid = false
  Source = -> Face094
  Symmetric = false
FEATURE [Part::MultiFuse] Fusion068  label="createThreadedInsertHolesForFan002"
  Shapes = -> [Revolve099,Revolve100,Revolve101,Revolve102]
FEATURE [Part::Cut] Cut026  label="fanScrewHousing003"
  Base = -> Fusion067
  Tool = -> Fusion068
FEATURE [Sketcher::SketchObject] Sketch048
  FullyConstrained = false
  Placement = pos=(0,0,0) rot=(1,0,0;1.5708rad)
  sketch-geometry (24):
    g0: ArcOfCircle CenterX=-4 CenterY=-10.5 CenterZ=0 NormalX=0 NormalY=0 NormalZ=1 AngleXU=0 Radius=1.5 StartAngle=6e-16 EndAngle=3.14159
    g1: ArcOfCircle CenterX=-34.2 CenterY=-10.5 CenterZ=0 NormalX=0 NormalY=0 NormalZ=1 AngleXU=0 Radius=1.5 StartAngle=0 EndAngle=3.14159
    g2: ArcOfCircle CenterX=-34.2 CenterY=-27.7 CenterZ=0 NormalX=0 NormalY=0 NormalZ=1 AngleXU=0 Radius=1.5 StartAngle=3.14159 EndAngle=6.28319
    g3: ArcOfCircle CenterX=-4 CenterY=-27.7 CenterZ=0 NormalX=0 NormalY=0 NormalZ=1 AngleXU=0 Radius=1.5 StartAngle=3.1416 EndAngle=6.28319
    g4: ArcOfCircle CenterX=-10 CenterY=-4.3 CenterZ=0 NormalX=0 NormalY=0 NormalZ=1 AngleXU=0 Radius=1.5 StartAngle=2e-16 EndAngle=3.14159
    g5: ArcOfCircle CenterX=-16.1 CenterY=-1.8 CenterZ=0 NormalX=0 NormalY=0 NormalZ=1 AngleXU=0 Radius=1.5 StartAngle=5e-16 EndAngle=3.14159
    g6: ArcOfCircle CenterX=-22.1 CenterY=-1.8 CenterZ=0 NormalX=0 NormalY=0 NormalZ=1 AngleXU=0 Radius=1.5 StartAngle=5e-16 EndAngle=3.14159
    g7: ArcOfCircle CenterX=-28.2 CenterY=-4.3 CenterZ=0 NormalX=0 NormalY=0 NormalZ=1 AngleXU=0 Radius=1.5 StartAngle=2e-16 EndAngle=3.14159
    g8: ArcOfCircle CenterX=-10 CenterY=-33.9 CenterZ=0 NormalX=0 NormalY=0 NormalZ=1 AngleXU=0 Radius=1.5 StartAngle=3.14159 EndAngle=6.28319
    g9: ArcOfCircle CenterX=-16.1 CenterY=-36.4 CenterZ=0 NormalX=0 NormalY=0 NormalZ=1 AngleXU=0 Radius=1.5 StartAngle=3.14159 EndAngle=6.28319
    g10: ArcOfCircle CenterX=-22.1 CenterY=-36.4 CenterZ=0 NormalX=0 NormalY=0 NormalZ=1 AngleXU=0 Radius=1.5 StartAngle=3.14159 EndAngle=6.28319
    g11: ArcOfCircle CenterX=-28.2 CenterY=-33.9 CenterZ=0 NormalX=0 NormalY=0 NormalZ=1 AngleXU=0 Radius=1.5 StartAngle=3.14159 EndAngle=6.28319
    g12: LineSegment StartX=-35.7 StartY=-10.5 StartZ=0 EndX=-35.7 EndY=-27.7 EndZ=0
    g13: LineSegment StartX=-32.7 StartY=-10.5 StartZ=0 EndX=-32.7 EndY=-27.7 EndZ=0
    g14: LineSegment StartX=-29.7 StartY=-33.9 StartZ=0 EndX=-29.7 EndY=-4.3 EndZ=0
    g15: LineSegment StartX=-26.7 StartY=-33.9 StartZ=0 EndX=-26.7 EndY=-4.3 EndZ=0
    g16: LineSegment StartX=-2.5 StartY=-10.5 StartZ=0 EndX=-2.5 EndY=-27.7 EndZ=0
    g17: LineSegment StartX=-8.5 StartY=-4.3 StartZ=0 EndX=-8.5 EndY=-33.9 EndZ=0
    g18: LineSegment StartX=-5.5 StartY=-10.5 StartZ=0 EndX=-5.5 EndY=-27.7 EndZ=0
    g19: LineSegment StartX=-11.5 StartY=-4.3 StartZ=0 EndX=-11.5 EndY=-33.9 EndZ=0
    g20: LineSegment StartX=-14.6 StartY=-1.8 StartZ=0 EndX=-14.6 EndY=-36.4 EndZ=0
    g21: LineSegment StartX=-17.6 StartY=-1.8 StartZ=0 EndX=-17.6 EndY=-36.4 EndZ=0
    g22: LineSegment StartX=-20.6 StartY=-36.4 StartZ=0 EndX=-20.6 EndY=-1.8 EndZ=0
    g23: LineSegment StartX=-23.6 StartY=-1.8 StartZ=0 EndX=-23.6 EndY=-36.4 EndZ=0
  constraints (48):
    c: Block(g0)
    c: Block(g1)
    c: Block(g2)
    c: Block(g3)
    c: Block(g4)
    c: Block(g5)
    c: Block(g6)
    c: Block(g7)
    c: Block(g8)
    c: Block(g9)
    c: Block(g10)
    c: Block(g11)
    c: Coincident(g12,g1)
    c: Coincident(g12,g2)
    c: Vertical(g12)
    c: Coincident(g13,g1)
    c: Coincident(g13,g2)
    c: Vertical(g13)
    c: Coincident(g14,g11)
    c: Coincident(g14,g7)
    c: Vertical(g14)
    c: Coincident(g15,g11)
    c: Coincident(g15,g7)
    c: Vertical(g15)
    c: Coincident(g16,g0)
    c: Coincident(g16,g3)
    c: Vertical(g16)
    c: Coincident(g17,g4)
    c: Coincident(g17,g8)
    c: Vertical(g17)
    c: Coincident(g18,g0)
    c: Coincident(g18,g3)
    c: Vertical(g18)
    c: Coincident(g19,g4)
    c: Coincident(g19,g8)
    c: Vertical(g19)
    c: Coincident(g20,g5)
    c: Coincident(g20,g9)
    c: Vertical(g20)
    c: Coincident(g21,g5)
    c: Coincident(g21,g9)
    c: Vertical(g21)
    c: Coincident(g22,g10)
    c: Coincident(g22,g6)
    c: Vertical(g22)
    c: Coincident(g23,g6)
    c: Coincident(g23,g10)
    c: Vertical(g23)
FEATURE [Part::Extrusion] Extrude039  label="removeToCreateFanGrillHoles002"
  Base = -> Sketch048
  Dir = (0,-1,6e-16)
  DirMode = 2
  FaceMakerClass = Part::FaceMakerBullseye
  LengthFwd = 10
  LengthRev = 0
  Placement = pos=(65.4,44,54.82) rot=(0,0,1;0rad)
  Solid = true
  Symmetric = false
FEATURE [Part::Cut] Cut027  label="fanScrewHousing004"
  Base = -> Cut026
  Tool = -> Extrude038
FEATURE [Part::Cut] Cut028  label="top014"
  Base = -> Fillet026
  Tool = -> Extrude039
FEATURE [Part::Feature] Face095 .. Face098  x4 (patterned run collapsed; names and placements below)
  shape: bbox 3.5 x 17.8 x 2e-07 mm, 1 faces, 0 solids (baked)
FEATURE [Part::Revolution] Revolve103  label="removeToCreateScrewAndThreadedInsertHole030"
  Angle = 360
  Axis = (0,1,0)
  Base = (0,0,0)
  FaceMakerClass = Part::FaceMakerBullseye
  Placement = pos=(62.3,30.3,19.7) rot=(0,0,1;0rad)
  Solid = false
  Source = -> Face095
  Symmetric = false
FEATURE [Part::Revolution] Revolve104  label="removeToCreateScrewAndThreadedInsertHole031"
  Angle = 360
  Axis = (0,1,0)
  Base = (0,0,0)
  FaceMakerClass = Part::FaceMakerBullseye
  Placement = pos=(62.3,30.3,51.7) rot=(0,0,1;0rad)
  Solid = false
  Source = -> Face096
  Symmetric = false
FEATURE [Part::Revolution] Revolve105  label="removeToCreateScrewAndThreadedInsertHole032"
  Angle = 360
  Axis = (0,1,0)
  Base = (0,0,0)
  FaceMakerClass = Part::FaceMakerBullseye
  Placement = pos=(30.3,30.3,19.7) rot=(0,0,1;0rad)
  Solid = false
  Source = -> Face097
  Symmetric = false
FEATURE [Part::Revolution] Revolve106  label="removeToCreateScrewAndThreadedInsertHole033"
  Angle = 360
  Axis = (0,1,0)
  Base = (0,0,0)
  FaceMakerClass = Part::FaceMakerBullseye
  Placement = pos=(30.3,30.3,51.7) rot=(0,0,1;0rad)
  Solid = false
  Source = -> Face098
  Symmetric = false
FEATURE [Part::MultiFuse] Fusion069  label="createThreadedInsertHolesForFan003"
  Shapes = -> [Revolve103,Revolve104,Revolve105,Revolve106]
FEATURE [Part::Cut] Cut029  label="top015"
  Base = -> Cut028
  Tool = -> Fusion054
FEATURE [Part::Cut] Cut030  label="fanScrewHousing005"
  Base = -> Cut027
  Tool = -> Fusion069
FEATURE [Part::Cylinder] Cylinder026  label="removeToCreteHoleForPlugHousing010"
  Angle = 360
  AttacherType = Attacher::AttachEngine3D
  Height = 20
  Placement = pos=(-2,19,36) rot=(0,1,0;1.5708rad)
  Radius = 14.3
FEATURE [Part::Box] Box018  label="removeToCreteHoleForPlugHousing011"
  AttacherType = Attacher::AttachEngine3D
  Height = 28.6
  Length = 10
  Placement = pos=(-2,0,21.7) rot=(0,0,1;0rad)
  Width = 19
FEATURE [Part::Box] Box019  label="wireHolderBottomCaseBit"
  AttacherType = Attacher::AttachEngine3D
  Height = 28
  Length = 3
  Placement = pos=(0,0,22) rot=(0,0,1;0rad)
  Width = 21
FEATURE [Part::Cylinder] Cylinder027  label="removeToCreteHoleForPlugHousing012"
  Angle = 360
  AttacherType = Attacher::AttachEngine3D
  Height = 20
  Placement = pos=(-2,19,36) rot=(0,1,0;1.5708rad)
  Radius = 14.3
FEATURE [Part::Cut] Cut031  label="wireHolderBottomCaseBit001"
  Base = -> Box019
  Tool = -> Cylinder027
FEATURE [Part::MultiFuse] Fusion070  label="removeToCreteHoleForPlugHousing013"
  Shapes = -> [Box018,Cylinder026]
FEATURE [Part::Cut] Cut032  label="top016"
  Base = -> Cut029
  Tool = -> Fusion070
FEATURE [Part::Cylinder] Cylinder028
  Angle = 360
  AttacherType = Attacher::AttachEngine3D
  Height = 20
  Placement = pos=(0,0,36.15) rot=(0,0,1;0rad)
  Radius = 14.3
FEATURE [Part::Cylinder] Cylinder029
  Angle = 360
  AttacherType = Attacher::AttachEngine3D
  Height = 10
  Placement = pos=(0,0,36.15) rot=(0,0,1;0rad)
  Radius = 4
FEATURE [Part::MultiFuse] Fusion071  label="removeToCreteHoleForPlugHousing014"
  Placement = pos=(70,19,36) rot=(0,1,0;1.5708rad)
  Shapes = -> [Cylinder028,Cylinder029]
FEATURE [Sketcher::SketchObject] Sketch049  label="topSketch011"
  FullyConstrained = true
  sketch-geometry (4):
    g0: ArcOfCircle CenterX=105 CenterY=19 CenterZ=0 NormalX=0 NormalY=0 NormalZ=1 AngleXU=0 Radius=20.6155 StartAngle=5.54125 EndAngle=6.28319
    g1: ArcOfCircle CenterX=105 CenterY=19 CenterZ=0 NormalX=0 NormalY=0 NormalZ=1 AngleXU=0 Radius=13 StartAngle=5.54125 EndAngle=6.28319
    g2: LineSegment StartX=118 StartY=19 StartZ=0 EndX=125.616 EndY=19 EndZ=0
    g3: LineSegment StartX=114.583 StartY=10.2157 StartZ=0 EndX=120.197 EndY=5.06982 EndZ=0
  constraints (7):
    c: Block(g0)
    c: Block(g1)
    c: Coincident(g2,g1)
    c: Coincident(g2,g0)
    c: Horizontal(g2)
    c: Coincident(g3,g1)
    c: Coincident(g3,g0)
FEATURE [Part::Box] Box020  label="removeToCreteHoleForPlugHousing015"
  AttacherType = Attacher::AttachEngine3D
  Height = 28.6
  Length = 20
  Placement = pos=(106.15,0,21.7) rot=(0,0,1;0rad)
  Width = 19
FEATURE [Part::MultiFuse] Fusion072  label="removeToCreteHoleForPlugHousing016"
  Shapes = -> [Box020,Fusion071]
FEATURE [Part::Cut] Cut033  label="removeToCreteHoleForPlugHousing017"
  Base = -> Cut032
  Tool = -> Fusion072
FEATURE [Part::Cylinder] Cylinder030
  Angle = 360
  AttacherType = Attacher::AttachEngine3D
  Height = 20
  Placement = pos=(0,0,36.15) rot=(0,0,1;0rad)
  Radius = 14.3
FEATURE [Part::Cylinder] Cylinder031
  Angle = 360
  AttacherType = Attacher::AttachEngine3D
  Height = 10
  Placement = pos=(0,0,36.15) rot=(0,0,1;0rad)
  Radius = 4
FEATURE [Part::Box] Box021  label="removeToCreteHoleForPlugHousing019"
  AttacherType = Attacher::AttachEngine3D
  Height = 28.6
  Length = 20
  Placement = pos=(106.15,0,21.7) rot=(0,0,1;0rad)
  Width = 19
FEATURE [Part::MultiFuse] Fusion074  label="removeToCreteHoleForPlugHousing020"
  Placement = pos=(70,19,36) rot=(0,1,0;1.5708rad)
  Shapes = -> [Cylinder030,Cylinder031]
FEATURE [Part::MultiFuse] Fusion073  label="removeToCreteHoleForPlugHousing018"
  Placement = pos=(0,0,28.3) rot=(0,0,1;0rad)
  Shapes = -> [Box021,Fusion074]
FEATURE [Part::Cylinder] Cylinder032
  Angle = 360
  AttacherType = Attacher::AttachEngine3D
  Height = 20
  Placement = pos=(0,0,36.15) rot=(0,0,1;0rad)
  Radius = 14.3
FEATURE [Part::Cylinder] Cylinder033
  Angle = 360
  AttacherType = Attacher::AttachEngine3D
  Height = 10
  Placement = pos=(0,0,36.15) rot=(0,0,1;0rad)
  Radius = 4
FEATURE [Part::Box] Box022  label="removeToCreteHoleForPlugHousing021"
  AttacherType = Attacher::AttachEngine3D
  Height = 28.6
  Length = 20
  Placement = pos=(106.15,0,21.7) rot=(0,0,1;0rad)
  Width = 19
FEATURE [Part::MultiFuse] Fusion076  label="removeToCreteHoleForPlugHousing023"
  Placement = pos=(70,19,36) rot=(0,1,0;1.5708rad)
  Shapes = -> [Cylinder032,Cylinder033]
FEATURE [Part::MultiFuse] Fusion075  label="removeToCreteHoleForPlugHousing022"
  Placement = pos=(0,0,-28.3) rot=(0,0,1;0rad)
  Shapes = -> [Box022,Fusion076]
FEATURE [Part::MultiFuse] Fusion077  label="removeToCreatePlugHousingBottomBit"
  Shapes = -> [Fusion075,Fusion073]
FEATURE [Part::Cylinder] Cylinder034
  Angle = 360
  AttacherType = Attacher::AttachEngine3D
  Height = 20
  Placement = pos=(0,0,36.15) rot=(0,0,1;0rad)
  Radius = 14
FEATURE [Part::Cylinder] Cylinder035
  Angle = 360
  AttacherType = Attacher::AttachEngine3D
  Height = 10
  Placement = pos=(0,0,36.15) rot=(0,0,1;0rad)
  Radius = 4
FEATURE [Part::MultiFuse] Fusion078  label="removeToCreteHoleForPlugHousing024"
  Placement = pos=(70,19,36) rot=(0,1,0;1.5708rad)
  Shapes = -> [Cylinder034,Cylinder035]
FEATURE [Part::MultiFuse] Fusion079  label="removeToCreatePlugHousingBottomBit001"
  Shapes = -> [Fusion078,Fusion077]
FEATURE [Part::Extrusion] Extrude040  label="bottomPlugHousingBit"
  Base = -> Sketch049
  Dir = (0,0,1)
  DirMode = 2
  FaceMakerClass = Part::FaceMakerBullseye
  LengthFwd = 72
  LengthRev = 0
  Solid = true
  Symmetric = false
FEATURE [Part::Cut] Cut034  label="bottomPlugHousingBit001"
  Base = -> Extrude040
  Placement = pos=(-0.09,0,0) rot=(0,0,1;0rad)
  Tool = -> Fusion079
FEATURE [Part::Box] Box023  label="Cube014"
  AttacherType = Attacher::AttachEngine3D
  Height = 16
  Length = 8
  Placement = pos=(12.7,31.52,28) rot=(0,0,1;0rad)
  Width = 4
FEATURE [Part::Cylinder] Cylinder036
  Angle = 360
  AttacherType = Attacher::AttachEngine3D
  Height = 10
  Placement = pos=(0,0,36.15) rot=(0,0,1;0rad)
  Radius = 4
FEATURE [Part::Cylinder] Cylinder037
  Angle = 360
  AttacherType = Attacher::AttachEngine3D
  Height = 20
  Placement = pos=(0,0,36.15) rot=(0,0,1;0rad)
  Radius = 8.2
FEATURE [Part::MultiFuse] Fusion080  label="removeToCreteHoleForPlugHousing025"
  Placement = pos=(-42,19,36) rot=(0,1,0;1.5708rad)
  Shapes = -> [Cylinder037,Cylinder036]
FEATURE [Sketcher::SketchObject] Sketch050  label="topSketch012"
  FullyConstrained = true
  sketch-geometry (4):
    g0: LineSegment StartX=16.8446 StartY=31.512 StartZ=0 EndX=16.3251 EndY=34.4666 EndZ=0
    g1: ArcOfCircle CenterX=19 CenterY=19.2524 CenterZ=0 NormalX=0 NormalY=0 NormalZ=1 AngleXU=0 Radius=15.4476 StartAngle=1.74483 EndAngle=2.72717
    g2: ArcOfCircle CenterX=19 CenterY=19.2524 CenterZ=0 NormalX=0 NormalY=0 NormalZ=1 AngleXU=0 Radius=12.4476 StartAngle=1.74483 EndAngle=2.73189
    g3: LineSegment StartX=4.86004 StartY=25.4725 StartZ=0 EndX=7.58253 EndY=24.2107 EndZ=0
  constraints (7):
    c: Block(g0)
    c: Coincident(g1,g0)
    c: Coincident(g2,g0)
    c: Coincident(g3,g1)
    c: Coincident(g3,g2)
    c: Block(g1)
    c: Block(g2)
FEATURE [Part::Extrusion] Extrude041
  Base = -> Sketch050
  Dir = (0,0,1)
  DirMode = 2
  FaceMakerClass = Part::FaceMakerBullseye
  LengthFwd = 10.6
  LengthRev = 0
  Placement = pos=(0,0,31) rot=(0,0,1;0rad)
  Solid = true
  Symmetric = false
FEATURE [Part::Cut] Cut035
  Base = -> Extrude041
  Placement = pos=(0,0,-0.3) rot=(0,0,1;0rad)
  Tool = -> Fusion080
FEATURE [Part::Cut] Cut036
  Base = -> Box023
  Tool = -> Cut035
FEATURE [Part::Fillet] Fillet027
  Base = -> Cut036
  Edges = 1 edges r=0.7: [Edge13]
FEATURE [Part::Fillet] Fillet028
  Base = -> Fillet027
  Edges = 1 edges r=0.7: [Edge13]
FEATURE [Part::Fillet] Fillet029
  Base = -> Fillet028
  Edges = 1 edges r=0.7: [Edge16]
FEATURE [Part::Fillet] Fillet030
  Base = -> Fillet029
  Edges = 1 edges r=0.7: [Edge11]
FEATURE [Part::Fillet] Fillet031
  Base = -> Fillet030
  Edges = 1 edges r=0.7: [Edge10]
FEATURE [Part::Fillet] Fillet032
  Base = -> Fillet031
  Edges = 1 edges r=1.2: [Edge5]
FEATURE [Part::Fillet] Fillet033
  Base = -> Fillet032
  Edges = 1 edges r=1.2: [Edge12]
FEATURE [Part::Fillet] Fillet034  label="wireHousingRetainer"
  Base = -> Fillet033
  Edges = 1 edges r=2: [Edge1]
  Placement = pos=(0.3,0,0) rot=(0,0,1;0rad)
FEATURE [Part::Feature] Face099
  shape: bbox 3.5 x 17.8 x 2e-07 mm, 1 faces, 0 solids (baked)
FEATURE [Part::Revolution] Revolve107  label="removeToCreateScrewAndThreadedInsertHole034"
  Angle = 360
  Axis = (0,1,0)
  Base = (0,0,0)
  FaceMakerClass = Part::FaceMakerBullseye
  Placement = pos=(12.5,0,10) rot=(0,0,1;0rad)
  Solid = false
  Source = -> Face099
  Symmetric = false
FEATURE [Part::Feature] Face100
  shape: bbox 3.5 x 17.8 x 2e-07 mm, 1 faces, 0 solids (baked)
FEATURE [Part::Revolution] Revolve108  label="removeToCreateScrewAndThreadedInsertHole035"
  Angle = 360
  Axis = (0,1,0)
  Base = (0,0,0)
  FaceMakerClass = Part::FaceMakerBullseye
  Placement = pos=(12.5,0,62) rot=(0,0,1;0rad)
  Solid = false
  Source = -> Face100
  Symmetric = false
FEATURE [Part::Feature] Face101
  shape: bbox 3.5 x 17.8 x 2e-07 mm, 1 faces, 0 solids (baked)
FEATURE [Part::Revolution] Revolve109  label="removeToCreateScrewAndThreadedInsertHole036"
  Angle = 360
  Axis = (0,1,0)
  Base = (0,0,0)
  FaceMakerClass = Part::FaceMakerBullseye
  Placement = pos=(89.5,0,68.5) rot=(0,0,1;0rad)
  Solid = false
  Source = -> Face101
  Symmetric = false
FEATURE [Part::Feature] Face102
  shape: bbox 3.5 x 17.8 x 2e-07 mm, 1 faces, 0 solids (baked)
FEATURE [Part::Revolution] Revolve110  label="removeToCreateScrewAndThreadedInsertHole037"
  Angle = 360
  Axis = (0,1,0)
  Base = (0,0,0)
  FaceMakerClass = Part::FaceMakerBullseye
  Placement = pos=(89.5,0,3.5) rot=(0,0,1;0rad)
  Solid = false
  Source = -> Face102
  Symmetric = false
FEATURE [Part::Feature] Face103
  shape: bbox 3.5 x 17.8 x 2e-07 mm, 1 faces, 0 solids (baked)
FEATURE [Part::Revolution] Revolve111  label="removeToCreateScrewAndThreadedInsertHole038"
  Angle = 360
  Axis = (0,1,0)
  Base = (0,0,0)
  FaceMakerClass = Part::FaceMakerBullseye
  Placement = pos=(109.5,4.7,3.5) rot=(0,0,1;0rad)
  Solid = false
  Source = -> Face103
  Symmetric = false
FEATURE [Part::Feature] Face104
  shape: bbox 3.5 x 17.8 x 2e-07 mm, 1 faces, 0 solids (baked)
FEATURE [Part::Revolution] Revolve112  label="removeToCreateScrewAndThreadedInsertHole039"
  Angle = 360
  Axis = (0,1,0)
  Base = (0,0,0)
  FaceMakerClass = Part::FaceMakerBullseye
  Placement = pos=(109.5,4.7,68.5) rot=(0,0,1;0rad)
  Solid = false
  Source = -> Face104
  Symmetric = false
FEATURE [Part::MultiFuse] Fusion081  label="removeToCreateScrewAndThreadedInsertHole040"
  Shapes = -> [Revolve107,Revolve108,Revolve109,Revolve110,Revolve111,Revolve112]
FEATURE [Part::MultiFuse] Fusion082  label="casePillars002"
  Shapes = -> [Revolve094,Revolve092,Revolve090,Revolve089,Revolve091,Revolve093]
FEATURE [Part::Cut] Cut037  label="casePillars003"
  Base = -> Fusion082
  Tool = -> Fusion081
FEATURE [Sketcher::SketchObject] Sketch051
  FullyConstrained = true
  Placement = pos=(117,19,0) rot=(0.57735,0.57735,0.57735;2.0944rad)
  sketch-geometry (48):
    g0: LineSegment StartX=-49.19 StartY=69.25 StartZ=0 EndX=-49.19 EndY=66.25 EndZ=0
    g1: LineSegment StartX=-49.19 StartY=63.5 StartZ=0 EndX=-49.19 EndY=60.5 EndZ=0
    g2: LineSegment StartX=-49.19 StartY=57.75 StartZ=0 EndX=-49.19 EndY=54.75 EndZ=0
    g3: LineSegment StartX=-49.19 StartY=52 StartZ=0 EndX=-49.19 EndY=49 EndZ=0
    g4: LineSegment StartX=-49.19 StartY=46.25 StartZ=0 EndX=-49.19 EndY=43.25 EndZ=0
    g5: LineSegment StartX=-49.19 StartY=40.5 StartZ=0 EndX=-49.19 EndY=37.5 EndZ=0
    g6: LineSegment StartX=-49.19 StartY=34.5 StartZ=0 EndX=-49.19 EndY=31.5 EndZ=0
    g7: LineSegment StartX=-49.19 StartY=28.75 StartZ=0 EndX=-49.19 EndY=25.75 EndZ=0
    g8: LineSegment StartX=-49.19 StartY=23 StartZ=0 EndX=-49.19 EndY=20 EndZ=0
    g9: LineSegment StartX=-49.19 StartY=17.25 StartZ=0 EndX=-49.19 EndY=14.25 EndZ=0
    g10: LineSegment StartX=-49.19 StartY=11.5 StartZ=0 EndX=-49.19 EndY=8.5 EndZ=0
    g11: LineSegment StartX=-49.19 StartY=5.75 StartZ=0 EndX=-49.19 EndY=2.75 EndZ=0
    g12: ArcOfCircle CenterX=-1.5 CenterY=67.75 CenterZ=0 NormalX=0 NormalY=0 NormalZ=1 AngleXU=0 Radius=1.5 StartAngle=4.71239 EndAngle=7.85398
    g13: ArcOfCircle CenterX=-1.5 CenterY=62 CenterZ=0 NormalX=0 NormalY=0 NormalZ=1 AngleXU=0 Radius=1.5 StartAngle=4.71239 EndAngle=7.85398
    g14: ArcOfCircle CenterX=-1.5 CenterY=56.25 CenterZ=0 NormalX=0 NormalY=0 NormalZ=1 AngleXU=0 Radius=1.5 StartAngle=4.71239 EndAngle=7.85398
    g15: ArcOfCircle CenterX=-11.49 CenterY=50.5 CenterZ=0 NormalX=0 NormalY=0 NormalZ=1 AngleXU=0 Radius=1.5 StartAngle=4.71239 EndAngle=7.85398
    g16: ArcOfCircle CenterX=-16.28 CenterY=44.75 CenterZ=0 NormalX=0 NormalY=0 NormalZ=1 AngleXU=0 Radius=1.5 StartAngle=4.71239 EndAngle=7.85398
    g17: ArcOfCircle CenterX=-18.2337 CenterY=39 CenterZ=0 NormalX=0 NormalY=0 NormalZ=1 AngleXU=0 Radius=1.5 StartAngle=4.71485 EndAngle=7.85398
    g18: ArcOfCircle CenterX=-16.2837 CenterY=27.25 CenterZ=0 NormalX=0 NormalY=0 NormalZ=1 AngleXU=0 Radius=1.5 StartAngle=4.71485 EndAngle=7.85398
    g19: ArcOfCircle CenterX=-18.2337 CenterY=33 CenterZ=0 NormalX=0 NormalY=0 NormalZ=1 AngleXU=0 Radius=1.5 StartAngle=4.71485 EndAngle=7.85398
    g20: ArcOfCircle CenterX=-11.49 CenterY=21.5 CenterZ=0 NormalX=0 NormalY=0 NormalZ=1 AngleXU=0 Radius=1.5 StartAngle=4.71239 EndAngle=7.85398
    g21: ArcOfCircle CenterX=-1.5 CenterY=4.25 CenterZ=0 NormalX=0 NormalY=0 NormalZ=1 AngleXU=0 Radius=1.5 StartAngle=4.71239 EndAngle=7.85398
    g22: ArcOfCircle CenterX=-1.5 CenterY=10 CenterZ=0 NormalX=0 NormalY=0 NormalZ=1 AngleXU=0 Radius=1.5 StartAngle=4.71239 EndAngle=7.85398
    g23: ArcOfCircle CenterX=-1.5 CenterY=15.75 CenterZ=0 NormalX=0 NormalY=0 NormalZ=1 AngleXU=0 Radius=1.5 StartAngle=4.71239 EndAngle=7.85398
    g24: LineSegment StartX=-49.19 StartY=69.25 StartZ=0 EndX=-1.5 EndY=69.25 EndZ=0
    g25: LineSegment StartX=-49.19 StartY=66.25 StartZ=0 EndX=-1.5 EndY=66.25 EndZ=0
    g26: LineSegment StartX=-49.19 StartY=63.5 StartZ=0 EndX=-1.5 EndY=63.5 EndZ=0
    g27: LineSegment StartX=-49.19 StartY=60.5 StartZ=0 EndX=-1.5 EndY=60.5 EndZ=0
    g28: LineSegment StartX=-49.19 StartY=57.75 StartZ=0 EndX=-1.5 EndY=57.75 EndZ=0
    g29: LineSegment StartX=-49.19 StartY=54.75 StartZ=0 EndX=-1.5 EndY=54.75 EndZ=0
    g30: LineSegment StartX=-49.19 StartY=52 StartZ=0 EndX=-11.49 EndY=52 EndZ=0
    g31: LineSegment StartX=-49.19 StartY=49 StartZ=0 EndX=-11.49 EndY=49 EndZ=0
    g32: LineSegment StartX=-49.19 StartY=46.25 StartZ=0 EndX=-16.28 EndY=46.25 EndZ=0
    g33: LineSegment StartX=-49.19 StartY=43.25 StartZ=0 EndX=-16.28 EndY=43.25 EndZ=0
    g34: LineSegment StartX=-49.19 StartY=40.5 StartZ=0 EndX=-18.2337 EndY=40.5 EndZ=0
    g35: LineSegment StartX=-49.19 StartY=37.5 StartZ=0 EndX=-18.23 EndY=37.5 EndZ=0
    g36: LineSegment StartX=-49.19 StartY=34.5 StartZ=0 EndX=-18.2337 EndY=34.5 EndZ=0
    g37: LineSegment StartX=-49.19 StartY=31.5 StartZ=0 EndX=-18.23 EndY=31.5 EndZ=0
    g38: LineSegment StartX=-49.19 StartY=28.75 StartZ=0 EndX=-16.2837 EndY=28.75 EndZ=0
    g39: LineSegment StartX=-49.19 StartY=25.75 StartZ=0 EndX=-16.28 EndY=25.75 EndZ=0
    g40: LineSegment StartX=-49.19 StartY=23 StartZ=0 EndX=-11.49 EndY=23 EndZ=0
    g41: LineSegment StartX=-49.19 StartY=20 StartZ=0 EndX=-11.49 EndY=20 EndZ=0
    g42: LineSegment StartX=-49.19 StartY=17.25 StartZ=0 EndX=-1.5 EndY=17.25 EndZ=0
    g43: LineSegment StartX=-49.19 StartY=14.25 StartZ=0 EndX=-1.5 EndY=14.25 EndZ=0
    g44: LineSegment StartX=-49.19 StartY=11.5 StartZ=0 EndX=-1.5 EndY=11.5 EndZ=0
    g45: LineSegment StartX=-49.19 StartY=8.5 StartZ=0 EndX=-1.5 EndY=8.5 EndZ=0
    g46: LineSegment StartX=-49.19 StartY=5.75 StartZ=0 EndX=-1.5 EndY=5.75 EndZ=0
    g47: LineSegment StartX=-49.19 StartY=2.75 StartZ=0 EndX=-1.5 EndY=2.75 EndZ=0
  constraints (120):
    c: Vertical(g0)
    c: Distance(g0) = 3
    c: Block(g0)
    c: Vertical(g1)
    c: Distance(g1) = 3
    c: Vertical(g2)
    c: Equal(g0,g2) = 3
    c: Block(g2)
    c: Vertical(g3)
    c: Equal(g1,g3) = 3
    c: Vertical(g4)
    c: Equal(g0,g4) = 3
    c: Block(g4)
    c: Vertical(g5)
    c: Equal(g1,g5) = 3
    c: Vertical(g6)
    c: Equal(g0,g6) = 3
    c: Block(g6)
    c: Vertical(g7)
    c: Equal(g1,g7) = 3
    c: Vertical(g8)
    c: Equal(g0,g8) = 3
    c: Block(g8)
    c: Vertical(g9)
    c: Equal(g1,g9) = 3
    c: Vertical(g10)
    c: Equal(g0,g10) = 3
    c: Block(g10)
    c: Vertical(g11)
    c: Equal(g1,g11) = 3
    c: Block(g12)
    c: Block(g13)
    c: Block(g14)
    c: Block(g15)
    c: Block(g16)
    c: Block(g17)
    c: Block(g18)
    c: Block(g19)
    c: Block(g20)
    c: Block(g21)
    c: Block(g22)
    c: Block(g23)
    c: Block(g11)
    c: Block(g9)
    c: Block(g7)
    c: Block(g5)
    c: Block(g3)
    c: Block(g1)
    c: Coincident(g24,g0)
    c: Coincident(g24,g12)
    c: Horizontal(g24)
    c: Coincident(g25,g0)
    c: Coincident(g25,g12)
    c: Horizontal(g25)
    c: Coincident(g26,g1)
    c: Coincident(g26,g13)
    c: Horizontal(g26)
    c: Coincident(g27,g1)
    c: Coincident(g27,g13)
    c: Horizontal(g27)
    c: Coincident(g28,g2)
    c: Coincident(g28,g14)
    c: Horizontal(g28)
    c: Coincident(g29,g2)
    c: Coincident(g29,g14)
    c: Horizontal(g29)
    c: Coincident(g30,g3)
    c: Coincident(g30,g15)
    c: Horizontal(g30)
    c: Coincident(g31,g3)
    c: Coincident(g31,g15)
    c: Horizontal(g31)
    c: Coincident(g32,g4)
    c: Coincident(g32,g16)
    c: Horizontal(g32)
    c: Coincident(g33,g4)
    c: Coincident(g33,g16)
    c: Horizontal(g33)
    c: Coincident(g34,g5)
    c: Coincident(g34,g17)
    c: Horizontal(g34)
    c: Coincident(g35,g5)
    c: Coincident(g35,g17)
    c: Horizontal(g35)
    c: Coincident(g36,g6)
    c: Coincident(g36,g19)
    c: Horizontal(g36)
    c: Coincident(g37,g6)
    c: Coincident(g37,g19)
    c: Horizontal(g37)
    c: Coincident(g38,g7)
    c: Coincident(g38,g18)
    c: Horizontal(g38)
    c: Coincident(g39,g7)
    c: Coincident(g39,g18)
    c: Horizontal(g39)
    c: Coincident(g40,g8)
    c: Coincident(g40,g20)
    c: Horizontal(g40)
    c: Coincident(g41,g8)
    c: Coincident(g41,g20)
    c: Horizontal(g41)
    c: Coincident(g42,g9)
    c: Coincident(g42,g23)
    c: Horizontal(g42)
    c: Coincident(g43,g9)
    c: Coincident(g43,g23)
    c: Horizontal(g43)
    c: Coincident(g44,g10)
    c: Coincident(g44,g22)
    c: Horizontal(g44)
    c: Coincident(g45,g10)
    c: Coincident(g45,g22)
    c: Horizontal(g45)
    c: Coincident(g46,g11)
    c: Coincident(g46,g21)
    c: Horizontal(g46)
    c: Coincident(g47,g11)
    c: Coincident(g47,g21)
    c: Horizontal(g47)
FEATURE [Part::Extrusion] Extrude042
  Base = -> Sketch051
  Dir = (1,-2e-16,2e-16)
  DirMode = 2
  FaceMakerClass = Part::FaceMakerBullseye
  LengthFwd = 19
  LengthRev = 0
  Placement = pos=(-19,0,0) rot=(0,0,1;0rad)
  Solid = true
  Symmetric = false
FEATURE [Part::Fillet] Fillet035  label="removeToCreateVentalationHoles"
  Base = -> Extrude042
  Edges = <same value as first occurrence — deduplicated (x6 in doc)>
  Placement = pos=(7,0,0) rot=(0,0,1;0rad)
FEATURE [Part::Cut] Cut038  label="top017"
  Base = -> Cut033
  Tool = -> Fillet035
FEATURE [Sketcher::SketchObject] Sketch052  label="bottomSketch001"
  FullyConstrained = true
  sketch-geometry (45):
    g0: LineSegment StartX=6.29999 StartY=8 StartZ=0 EndX=3.29999 EndY=8 EndZ=0
    g1: LineSegment StartX=3.29999 StartY=8 StartZ=0 EndX=3.29999 EndY=-6.03275e-07 EndZ=0
    g2: ArcOfCircle CenterX=8.29999 CenterY=5 CenterZ=0 NormalX=0 NormalY=0 NormalZ=1 AngleXU=0 Radius=2 StartAngle=3.14159 EndAngle=4.71239
    g3: LineSegment StartX=6.29999 StartY=8 StartZ=0 EndX=6.29999 EndY=5 EndZ=0
    g4: ArcOfCircle CenterX=105 CenterY=19 CenterZ=0 NormalX=0 NormalY=0 NormalZ=1 AngleXU=0 Radius=12.7 StartAngle=4.71239 EndAngle=5.94289
    g5-g11: Circle x7 (B-spline internal-alignment scaffolding for g12; pole/knot coordinates omitted)
    g12: BSplineCurve PolesCount=7 KnotsCount=5 Degree=3 IsPeriodic=0
    g13-g17: GeomPoint x5 (B-spline internal-alignment scaffolding for g12; pole/knot coordinates omitted)
    g18: ArcOfCircle CenterX=105 CenterY=19 CenterZ=0 NormalX=0 NormalY=0 NormalZ=1 AngleXU=0 Radius=15.7 StartAngle=5.81226 EndAngle=6.28319
    g19: BSplineCurve PolesCount=5 KnotsCount=3 Degree=3 IsPeriodic=0
    g20: LineSegment StartX=8.29999 StartY=3 StartZ=0 EndX=101.7 EndY=3 EndZ=0
    g21: LineSegment StartX=3.29999 StartY=-6.03275e-07 StartZ=0 EndX=105 EndY=-6.03275e-07 EndZ=0
    g22: LineSegment StartX=120.974 StartY=8.71251 StartZ=0 EndX=122.332 EndY=7.83778 EndZ=0
    g23: LineSegment StartX=105 StartY=-6.03274e-07 StartZ=0 EndX=113 EndY=-6.03274e-07 EndZ=0
    g24: ArcOfCircle CenterX=105 CenterY=19 CenterZ=0 NormalX=0 NormalY=0 NormalZ=1 AngleXU=0 Radius=20.6155 StartAngle=5.11091 EndAngle=5.71103
    g25: ArcOfCircle CenterX=117.7 CenterY=19 CenterZ=0 NormalX=0 NormalY=0 NormalZ=1 AngleXU=0 Radius=3 StartAngle=1.2e-15 EndAngle=2.10468
    g26: Circle CenterX=116.345 CenterY=16.3232 CenterZ=0 NormalX=0 NormalY=0 NormalZ=1 AngleXU=0 Radius=1
    g27: Circle CenterX=117.24 CenterY=15.7584 CenterZ=0 NormalX=0 NormalY=0 NormalZ=1 AngleXU=0 Radius=1
    g28: Circle CenterX=116.972 CenterY=14.7612 CenterZ=0 NormalX=0 NormalY=0 NormalZ=1 AngleXU=0 Radius=1
    g29: BSplineCurve PolesCount=3 KnotsCount=2 Degree=2 IsPeriodic=0
    g30: GeomPoint X=116.345 Y=16.3232 Z=0
    g31: GeomPoint X=116.972 Y=14.7612 Z=0
    g32: Circle CenterX=115.828 CenterY=17.157 CenterZ=0 NormalX=0 NormalY=0 NormalZ=1 AngleXU=0 Radius=1
    g33: Circle CenterX=115.841 CenterY=16.639 CenterZ=0 NormalX=0 NormalY=0 NormalZ=1 AngleXU=0 Radius=1
    g34: Circle CenterX=116.345 CenterY=16.3232 CenterZ=0 NormalX=0 NormalY=0 NormalZ=1 AngleXU=0 Radius=1
    g35: BSplineCurve PolesCount=3 KnotsCount=2 Degree=2 IsPeriodic=0
    g36: GeomPoint X=115.828 Y=17.157 Z=0
    g37: GeomPoint X=116.345 Y=16.3232 Z=0
    g38: LineSegment StartX=115.828 StartY=17.157 StartZ=0 EndX=115.828 EndY=20.8307 EndZ=0
    g39: Circle CenterX=115.828 CenterY=20.8307 CenterZ=0 NormalX=0 NormalY=0 NormalZ=1 AngleXU=0 Radius=1
    g40: Circle CenterX=115.831 CenterY=21.3396 CenterZ=0 NormalX=0 NormalY=0 NormalZ=1 AngleXU=0 Radius=1
    g41: Circle CenterX=116.173 CenterY=21.5825 CenterZ=0 NormalX=0 NormalY=0 NormalZ=1 AngleXU=0 Radius=1
    g42: BSplineCurve PolesCount=3 KnotsCount=2 Degree=2 IsPeriodic=0
    g43: GeomPoint X=115.828 Y=20.8307 Z=0
    g44: GeomPoint X=116.173 Y=21.5825 Z=0
  constraints (70):
    c: Horizontal(g0)
    c: Distance(g0) = 3
    c: Coincident(g1,g0)
    c: Vertical(g1)
    c: Block(g2)
    c: Block(g0)
    c: Coincident(g3,g0)
    c: Coincident(g3,g2)
    c: Vertical(g3)
    c: Block(g1)
    c: Block(g4)
    c: Coincident(g19,g4)
    c: Block(g19)
    c: Equal(g5, g6-g11) x6
    c: InternalAlignment(g5-g11 -> g12) x7
    c: InternalAlignment(g13-g17 -> g12) x5
    c: Block(g12)
    c: Coincident(g18,g12)
    c: Block(g18)
    c: Coincident(g20,g2)
    c: Coincident(g20,g19)
    c: Horizontal(g20)
    c: Distance(g20) = 93.4
    c: Coincident(g21,g1)
    c: Horizontal(g21)
    c: Distance(g21) = 101.7
    c: Horizontal(g23)
    c: Distance(g23) = 8
    c: Coincident(g24,g23)
    c: Block(g23)
    c: Coincident(g22,g24)
    c: Block(g24)
    c: Block(g22)
    c: Distance(g22) = 1.61553
    c: Coincident(g25,g18)
    c: Block(g25)
    c: Weight(g26) = 1
    c: Equal(g26,g27)
    c: Equal(g26,g28)
    c: Coincident(g29,g4)
    c: InternalAlignment(g26,g29)
    c: InternalAlignment(g27,g29)
    c: InternalAlignment(g28,g29)
    c: InternalAlignment(g30,g29)
    c: InternalAlignment(g31,g29)
    c: Block(g29)
    c: Weight(g32) = 1
    c: Equal(g32,g33)
    c: Equal(g32,g34)
    c: Coincident(g35,g29)
    c: InternalAlignment(g32,g35)
    c: InternalAlignment(g33,g35)
    c: InternalAlignment(g34,g35)
    c: InternalAlignment(g36,g35)
    c: InternalAlignment(g37,g35)
    c: Block(g35)
    c: Coincident(g38,g35)
    c: Vertical(g38)
    c: Block(g38)
    c: Coincident(g42,g38)
    c: Weight(g39) = 1
    c: Equal(g39,g40)
    c: Equal(g39,g41)
    c: Coincident(g42,g25)
    c: InternalAlignment(g39,g42)
    c: InternalAlignment(g40,g42)
    c: InternalAlignment(g41,g42)
    c: InternalAlignment(g43,g42)
    c: InternalAlignment(g44,g42)
    c: Block(g42)
FEATURE [Part::Extrusion] Extrude043  label="bottom010"
  Base = -> Sketch052
  Dir = (0,0,1)
  DirMode = 2
  FaceMakerClass = Part::FaceMakerBullseye
  LengthFwd = 71.4
  LengthRev = 0
  Placement = pos=(0,0,0.3) rot=(0,0,1;0rad)
  Solid = true
  Symmetric = false
FEATURE [Sketcher::SketchObject] Sketch053  label="topSketch013"
  FullyConstrained = true
  sketch-geometry (22):
    g0: LineSegment StartX=5.21097e-06 StartY=3 StartZ=0 EndX=5.21097e-06 EndY=19 EndZ=0
    g1: ArcOfCircle CenterX=19 CenterY=19 CenterZ=0 NormalX=0 NormalY=0 NormalZ=1 AngleXU=0 Radius=19 StartAngle=1.5708 EndAngle=3.14159
    g2: ArcOfCircle CenterX=19 CenterY=19 CenterZ=0 NormalX=0 NormalY=0 NormalZ=1 AngleXU=0 Radius=16 StartAngle=1.5708 EndAngle=3.14159
    g3: LineSegment StartX=114 StartY=35 StartZ=0 EndX=19 EndY=35 EndZ=0
    g4: LineSegment StartX=5.21097e-06 StartY=3 StartZ=0 EndX=5.21097e-06 EndY=0 EndZ=0
    g5: LineSegment StartX=3 StartY=0 StartZ=0 EndX=5.21097e-06 EndY=0 EndZ=0
    g6: LineSegment StartX=3 StartY=19 StartZ=0 EndX=3 EndY=0 EndZ=0
    g7: LineSegment StartX=19 StartY=38 StartZ=0 EndX=124 EndY=38 EndZ=0
    g8: Circle CenterX=119 CenterY=35 CenterZ=0 NormalX=0 NormalY=0 NormalZ=1 AngleXU=0 Radius=1
    g9: Circle CenterX=121 CenterY=35 CenterZ=0 NormalX=0 NormalY=0 NormalZ=1 AngleXU=0 Radius=1
    g10: Circle CenterX=121 CenterY=33 CenterZ=0 NormalX=0 NormalY=0 NormalZ=1 AngleXU=0 Radius=1
    g11: BSplineCurve PolesCount=3 KnotsCount=2 Degree=2 IsPeriodic=0
    g12: GeomPoint X=119 Y=35 Z=0
    g13: GeomPoint X=121 Y=33 Z=0
    g14: LineSegment StartX=119 StartY=35 StartZ=0 EndX=114 EndY=35 EndZ=0
    g15: ArcOfCircle CenterX=105 CenterY=19 CenterZ=0 NormalX=0 NormalY=0 NormalZ=1 AngleXU=0 Radius=16 StartAngle=5.60905 EndAngle=6.28319
    g16: LineSegment StartX=121 StartY=33 StartZ=0 EndX=121 EndY=19 EndZ=0
    g17: LineSegment StartX=117.5 StartY=9.01251 StartZ=0 EndX=121.163 EndY=9.0125 EndZ=0
    g18: ArcOfCircle CenterX=105 CenterY=19 CenterZ=0 NormalX=0 NormalY=0 NormalZ=1 AngleXU=0 Radius=20.6155 StartAngle=5.7297 EndAngle=6.28319
    g19: LineSegment StartX=121.163 StartY=9.0125 StartZ=0 EndX=122.538 EndY=8.16329 EndZ=0
    g20: LineSegment StartX=124 StartY=38 StartZ=0 EndX=125.616 EndY=38 EndZ=0
    g21: LineSegment StartX=125.616 StartY=19 StartZ=0 EndX=125.616 EndY=38 EndZ=0
  constraints (50):
    c: Vertical(g0)
    c: Block(g0)
    c: Coincident(g1,g0)
    c: Block(g1)
    c: Coincident(g2,g1)
    c: Block(g2)
    c: Coincident(g3,g2)
    c: Horizontal(g3)
    c: Tangent(g3,g2)
    c: Coincident(g4,g0)
    c: Distance(g4) = 3
    c: Vertical(g4)
    c: Coincident(g5,g4)
    c: Horizontal(g5)
    c: Coincident(g6,g2)
    c: Coincident(g6,g5)
    c: Vertical(g6)
    c: Horizontal(g7)
    c: Distance(g7) = 105
    c: Coincident(g7,g1)
    c: Block(g3)
    c: Weight(g8) = 1
    c: Equal(g8,g9)
    c: Equal(g8,g10)
    c: InternalAlignment(g8,g11)
    c: InternalAlignment(g9,g11)
    c: InternalAlignment(g10,g11)
    c: InternalAlignment(g12,g11)
    c: InternalAlignment(g13,g11)
    c: Block(g11)
    c: Coincident(g14,g11)
    c: Coincident(g14,g3)
    c: Horizontal(g14)
    c: Block(g15)
    c: Coincident(g16,g11)
    c: Coincident(g16,g15)
    c: Vertical(g16)
    c: Distance(g16) = 14
    c: Coincident(g17,g15)
    c: Block(g18)
    c: Coincident(g19,g18)
    c: Coincident(g20,g7)
    c: Horizontal(g20)
    c: Vertical(g21)
    c: Coincident(g20,g21)
    c: Block(g20)
    c: Block(g21)
    c: Block(g19)
    c: Block(g17)
    c: Distance(g20) = 1.61553
FEATURE [Part::Extrusion] Extrude044
  Base = -> Sketch053
  Dir = (0,0,1)
  DirMode = 2
  FaceMakerClass = Part::FaceMakerBullseye
  LengthFwd = 72
  LengthRev = 0
  Solid = true
  Symmetric = false
FEATURE [Part::Fillet] Fillet036  label="top018"
  Base = -> Extrude044
  Edges = 1 edges r=2: [Edge41]
FEATURE [Sketcher::SketchObject] Sketch054
  FullyConstrained = false
  Placement = pos=(0,0,0) rot=(1,0,0;1.5708rad)
  sketch-geometry (24):
    g0: ArcOfCircle CenterX=-4 CenterY=-10.5 CenterZ=0 NormalX=0 NormalY=0 NormalZ=1 AngleXU=0 Radius=1.5 StartAngle=6e-16 EndAngle=3.14159
    g1: ArcOfCircle CenterX=-34.2 CenterY=-10.5 CenterZ=0 NormalX=0 NormalY=0 NormalZ=1 AngleXU=0 Radius=1.5 StartAngle=0 EndAngle=3.14159
    g2: ArcOfCircle CenterX=-34.2 CenterY=-27.7 CenterZ=0 NormalX=0 NormalY=0 NormalZ=1 AngleXU=0 Radius=1.5 StartAngle=3.14159 EndAngle=6.28319
    g3: ArcOfCircle CenterX=-4 CenterY=-27.7 CenterZ=0 NormalX=0 NormalY=0 NormalZ=1 AngleXU=0 Radius=1.5 StartAngle=3.1416 EndAngle=6.28319
    g4: ArcOfCircle CenterX=-10 CenterY=-4.3 CenterZ=0 NormalX=0 NormalY=0 NormalZ=1 AngleXU=0 Radius=1.5 StartAngle=2e-16 EndAngle=3.14159
    g5: ArcOfCircle CenterX=-16.1 CenterY=-1.8 CenterZ=0 NormalX=0 NormalY=0 NormalZ=1 AngleXU=0 Radius=1.5 StartAngle=5e-16 EndAngle=3.14159
    g6: ArcOfCircle CenterX=-22.1 CenterY=-1.8 CenterZ=0 NormalX=0 NormalY=0 NormalZ=1 AngleXU=0 Radius=1.5 StartAngle=5e-16 EndAngle=3.14159
    g7: ArcOfCircle CenterX=-28.2 CenterY=-4.3 CenterZ=0 NormalX=0 NormalY=0 NormalZ=1 AngleXU=0 Radius=1.5 StartAngle=2e-16 EndAngle=3.14159
    g8: ArcOfCircle CenterX=-10 CenterY=-33.9 CenterZ=0 NormalX=0 NormalY=0 NormalZ=1 AngleXU=0 Radius=1.5 StartAngle=3.14159 EndAngle=6.28319
    g9: ArcOfCircle CenterX=-16.1 CenterY=-36.4 CenterZ=0 NormalX=0 NormalY=0 NormalZ=1 AngleXU=0 Radius=1.5 StartAngle=3.14159 EndAngle=6.28319
    g10: ArcOfCircle CenterX=-22.1 CenterY=-36.4 CenterZ=0 NormalX=0 NormalY=0 NormalZ=1 AngleXU=0 Radius=1.5 StartAngle=3.14159 EndAngle=6.28319
    g11: ArcOfCircle CenterX=-28.2 CenterY=-33.9 CenterZ=0 NormalX=0 NormalY=0 NormalZ=1 AngleXU=0 Radius=1.5 StartAngle=3.14159 EndAngle=6.28319
    g12: LineSegment StartX=-35.7 StartY=-10.5 StartZ=0 EndX=-35.7 EndY=-27.7 EndZ=0
    g13: LineSegment StartX=-32.7 StartY=-10.5 StartZ=0 EndX=-32.7 EndY=-27.7 EndZ=0
    g14: LineSegment StartX=-29.7 StartY=-33.9 StartZ=0 EndX=-29.7 EndY=-4.3 EndZ=0
    g15: LineSegment StartX=-26.7 StartY=-33.9 StartZ=0 EndX=-26.7 EndY=-4.3 EndZ=0
    g16: LineSegment StartX=-2.5 StartY=-10.5 StartZ=0 EndX=-2.5 EndY=-27.7 EndZ=0
    g17: LineSegment StartX=-8.5 StartY=-4.3 StartZ=0 EndX=-8.5 EndY=-33.9 EndZ=0
    g18: LineSegment StartX=-5.5 StartY=-10.5 StartZ=0 EndX=-5.5 EndY=-27.7 EndZ=0
    g19: LineSegment StartX=-11.5 StartY=-4.3 StartZ=0 EndX=-11.5 EndY=-33.9 EndZ=0
    g20: LineSegment StartX=-14.6 StartY=-1.8 StartZ=0 EndX=-14.6 EndY=-36.4 EndZ=0
    g21: LineSegment StartX=-17.6 StartY=-1.8 StartZ=0 EndX=-17.6 EndY=-36.4 EndZ=0
    g22: LineSegment StartX=-20.6 StartY=-36.4 StartZ=0 EndX=-20.6 EndY=-1.8 EndZ=0
    g23: LineSegment StartX=-23.6 StartY=-1.8 StartZ=0 EndX=-23.6 EndY=-36.4 EndZ=0
  constraints (48):
    c: Block(g0)
    c: Block(g1)
    c: Block(g2)
    c: Block(g3)
    c: Block(g4)
    c: Block(g5)
    c: Block(g6)
    c: Block(g7)
    c: Block(g8)
    c: Block(g9)
    c: Block(g10)
    c: Block(g11)
    c: Coincident(g12,g1)
    c: Coincident(g12,g2)
    c: Vertical(g12)
    c: Coincident(g13,g1)
    c: Coincident(g13,g2)
    c: Vertical(g13)
    c: Coincident(g14,g11)
    c: Coincident(g14,g7)
    c: Vertical(g14)
    c: Coincident(g15,g11)
    c: Coincident(g15,g7)
    c: Vertical(g15)
    c: Coincident(g16,g0)
    c: Coincident(g16,g3)
    c: Vertical(g16)
    c: Coincident(g17,g4)
    c: Coincident(g17,g8)
    c: Vertical(g17)
    c: Coincident(g18,g0)
    c: Coincident(g18,g3)
    c: Vertical(g18)
    c: Coincident(g19,g4)
    c: Coincident(g19,g8)
    c: Vertical(g19)
    c: Coincident(g20,g5)
    c: Coincident(g20,g9)
    c: Vertical(g20)
    c: Coincident(g21,g5)
    c: Coincident(g21,g9)
    c: Vertical(g21)
    c: Coincident(g22,g10)
    c: Coincident(g22,g6)
    c: Vertical(g22)
    c: Coincident(g23,g6)
    c: Coincident(g23,g10)
    c: Vertical(g23)
FEATURE [Part::Extrusion] Extrude045  label="removeToCreateFanGrillHoles003"
  Base = -> Sketch054
  Dir = (0,-1,6e-16)
  DirMode = 2
  FaceMakerClass = Part::FaceMakerBullseye
  LengthFwd = 10
  LengthRev = 0
  Placement = pos=(65.4,44,54.82) rot=(0,0,1;0rad)
  Solid = true
  Symmetric = false
FEATURE [Part::Feature] Face105 .. Face108  x4 (patterned run collapsed; names and placements below)
  shape: bbox 3.5 x 17.8 x 2e-07 mm, 1 faces, 0 solids (baked)
FEATURE [Part::Revolution] Revolve113  label="removeToCreateScrewAndThreadedInsertHole041"
  Angle = 360
  Axis = (0,1,0)
  Base = (0,0,0)
  FaceMakerClass = Part::FaceMakerBullseye
  Placement = pos=(62.3,30.3,19.7) rot=(0,0,1;0rad)
  Solid = false
  Source = -> Face105
  Symmetric = false
FEATURE [Part::Revolution] Revolve114  label="removeToCreateScrewAndThreadedInsertHole042"
  Angle = 360
  Axis = (0,1,0)
  Base = (0,0,0)
  FaceMakerClass = Part::FaceMakerBullseye
  Placement = pos=(62.3,30.3,51.7) rot=(0,0,1;0rad)
  Solid = false
  Source = -> Face106
  Symmetric = false
FEATURE [Part::Revolution] Revolve115  label="removeToCreateScrewAndThreadedInsertHole043"
  Angle = 360
  Axis = (0,1,0)
  Base = (0,0,0)
  FaceMakerClass = Part::FaceMakerBullseye
  Placement = pos=(30.3,30.3,19.7) rot=(0,0,1;0rad)
  Solid = false
  Source = -> Face107
  Symmetric = false
FEATURE [Part::Revolution] Revolve116  label="removeToCreateScrewAndThreadedInsertHole044"
  Angle = 360
  Axis = (0,1,0)
  Base = (0,0,0)
  FaceMakerClass = Part::FaceMakerBullseye
  Placement = pos=(30.3,30.3,51.7) rot=(0,0,1;0rad)
  Solid = false
  Source = -> Face108
  Symmetric = false
FEATURE [Part::MultiFuse] Fusion083  label="createThreadedInsertHolesForFan004"
  Shapes = -> [Revolve113,Revolve114,Revolve115,Revolve116]
FEATURE [Part::Box] Box024  label="removeToCreteHoleForPlugHousing026"
  AttacherType = Attacher::AttachEngine3D
  Height = 28.6
  Length = 10
  Placement = pos=(-2,0,21.7) rot=(0,0,1;0rad)
  Width = 19
FEATURE [Part::Cylinder] Cylinder038  label="removeToCreteHoleForPlugHousing027"
  Angle = 360
  AttacherType = Attacher::AttachEngine3D
  Height = 20
  Placement = pos=(-2,19,36) rot=(0,1,0;1.5708rad)
  Radius = 14.3
FEATURE [Part::MultiFuse] Fusion084  label="removeToCreteHoleForPlugHousing028"
  Shapes = -> [Box024,Cylinder038]
FEATURE [Part::Cylinder] Cylinder039
  Angle = 360
  AttacherType = Attacher::AttachEngine3D
  Height = 20
  Placement = pos=(0,0,36.15) rot=(0,0,1;0rad)
  Radius = 14.3
FEATURE [Part::Cylinder] Cylinder040
  Angle = 360
  AttacherType = Attacher::AttachEngine3D
  Height = 10
  Placement = pos=(0,0,36.15) rot=(0,0,1;0rad)
  Radius = 4
FEATURE [Part::Box] Box025  label="removeToCreteHoleForPlugHousing030"
  AttacherType = Attacher::AttachEngine3D
  Height = 28.6
  Length = 20
  Placement = pos=(106.15,0,21.7) rot=(0,0,1;0rad)
  Width = 19
FEATURE [Part::MultiFuse] Fusion086  label="removeToCreteHoleForPlugHousing031"
  Placement = pos=(70,19,36) rot=(0,1,0;1.5708rad)
  Shapes = -> [Cylinder039,Cylinder040]
FEATURE [Part::MultiFuse] Fusion085  label="removeToCreteHoleForPlugHousing029"
  Shapes = -> [Box025,Fusion086]
FEATURE [Sketcher::SketchObject] Sketch055
  FullyConstrained = true
  Placement = pos=(117,19,0) rot=(0.57735,0.57735,0.57735;2.0944rad)
  sketch-geometry (48):
    g0: LineSegment StartX=-49.19 StartY=69.25 StartZ=0 EndX=-49.19 EndY=66.25 EndZ=0
    g1: LineSegment StartX=-49.19 StartY=63.5 StartZ=0 EndX=-49.19 EndY=60.5 EndZ=0
    g2: LineSegment StartX=-49.19 StartY=57.75 StartZ=0 EndX=-49.19 EndY=54.75 EndZ=0
    g3: LineSegment StartX=-49.19 StartY=52 StartZ=0 EndX=-49.19 EndY=49 EndZ=0
    g4: LineSegment StartX=-49.19 StartY=46.25 StartZ=0 EndX=-49.19 EndY=43.25 EndZ=0
    g5: LineSegment StartX=-49.19 StartY=40.5 StartZ=0 EndX=-49.19 EndY=37.5 EndZ=0
    g6: LineSegment StartX=-49.19 StartY=34.5 StartZ=0 EndX=-49.19 EndY=31.5 EndZ=0
    g7: LineSegment StartX=-49.19 StartY=28.75 StartZ=0 EndX=-49.19 EndY=25.75 EndZ=0
    g8: LineSegment StartX=-49.19 StartY=23 StartZ=0 EndX=-49.19 EndY=20 EndZ=0
    g9: LineSegment StartX=-49.19 StartY=17.25 StartZ=0 EndX=-49.19 EndY=14.25 EndZ=0
    g10: LineSegment StartX=-49.19 StartY=11.5 StartZ=0 EndX=-49.19 EndY=8.5 EndZ=0
    g11: LineSegment StartX=-49.19 StartY=5.75 StartZ=0 EndX=-49.19 EndY=2.75 EndZ=0
    g12: ArcOfCircle CenterX=-1.5 CenterY=67.75 CenterZ=0 NormalX=0 NormalY=0 NormalZ=1 AngleXU=0 Radius=1.5 StartAngle=4.71239 EndAngle=7.85398
    g13: ArcOfCircle CenterX=-1.5 CenterY=62 CenterZ=0 NormalX=0 NormalY=0 NormalZ=1 AngleXU=0 Radius=1.5 StartAngle=4.71239 EndAngle=7.85398
    g14: ArcOfCircle CenterX=-1.5 CenterY=56.25 CenterZ=0 NormalX=0 NormalY=0 NormalZ=1 AngleXU=0 Radius=1.5 StartAngle=4.71239 EndAngle=7.85398
    g15: ArcOfCircle CenterX=-11.49 CenterY=50.5 CenterZ=0 NormalX=0 NormalY=0 NormalZ=1 AngleXU=0 Radius=1.5 StartAngle=4.71239 EndAngle=7.85398
    g16: ArcOfCircle CenterX=-16.28 CenterY=44.75 CenterZ=0 NormalX=0 NormalY=0 NormalZ=1 AngleXU=0 Radius=1.5 StartAngle=4.71239 EndAngle=7.85398
    g17: ArcOfCircle CenterX=-18.2337 CenterY=39 CenterZ=0 NormalX=0 NormalY=0 NormalZ=1 AngleXU=0 Radius=1.5 StartAngle=4.71485 EndAngle=7.85398
    g18: ArcOfCircle CenterX=-16.2837 CenterY=27.25 CenterZ=0 NormalX=0 NormalY=0 NormalZ=1 AngleXU=0 Radius=1.5 StartAngle=4.71485 EndAngle=7.85398
    g19: ArcOfCircle CenterX=-18.2337 CenterY=33 CenterZ=0 NormalX=0 NormalY=0 NormalZ=1 AngleXU=0 Radius=1.5 StartAngle=4.71485 EndAngle=7.85398
    g20: ArcOfCircle CenterX=-11.49 CenterY=21.5 CenterZ=0 NormalX=0 NormalY=0 NormalZ=1 AngleXU=0 Radius=1.5 StartAngle=4.71239 EndAngle=7.85398
    g21: ArcOfCircle CenterX=-1.5 CenterY=4.25 CenterZ=0 NormalX=0 NormalY=0 NormalZ=1 AngleXU=0 Radius=1.5 StartAngle=4.71239 EndAngle=7.85398
    g22: ArcOfCircle CenterX=-1.5 CenterY=10 CenterZ=0 NormalX=0 NormalY=0 NormalZ=1 AngleXU=0 Radius=1.5 StartAngle=4.71239 EndAngle=7.85398
    g23: ArcOfCircle CenterX=-1.5 CenterY=15.75 CenterZ=0 NormalX=0 NormalY=0 NormalZ=1 AngleXU=0 Radius=1.5 StartAngle=4.71239 EndAngle=7.85398
    g24: LineSegment StartX=-49.19 StartY=69.25 StartZ=0 EndX=-1.5 EndY=69.25 EndZ=0
    g25: LineSegment StartX=-49.19 StartY=66.25 StartZ=0 EndX=-1.5 EndY=66.25 EndZ=0
    g26: LineSegment StartX=-49.19 StartY=63.5 StartZ=0 EndX=-1.5 EndY=63.5 EndZ=0
    g27: LineSegment StartX=-49.19 StartY=60.5 StartZ=0 EndX=-1.5 EndY=60.5 EndZ=0
    g28: LineSegment StartX=-49.19 StartY=57.75 StartZ=0 EndX=-1.5 EndY=57.75 EndZ=0
    g29: LineSegment StartX=-49.19 StartY=54.75 StartZ=0 EndX=-1.5 EndY=54.75 EndZ=0
    g30: LineSegment StartX=-49.19 StartY=52 StartZ=0 EndX=-11.49 EndY=52 EndZ=0
    g31: LineSegment StartX=-49.19 StartY=49 StartZ=0 EndX=-11.49 EndY=49 EndZ=0
    g32: LineSegment StartX=-49.19 StartY=46.25 StartZ=0 EndX=-16.28 EndY=46.25 EndZ=0
    g33: LineSegment StartX=-49.19 StartY=43.25 StartZ=0 EndX=-16.28 EndY=43.25 EndZ=0
    g34: LineSegment StartX=-49.19 StartY=40.5 StartZ=0 EndX=-18.2337 EndY=40.5 EndZ=0
    g35: LineSegment StartX=-49.19 StartY=37.5 StartZ=0 EndX=-18.23 EndY=37.5 EndZ=0
    g36: LineSegment StartX=-49.19 StartY=34.5 StartZ=0 EndX=-18.2337 EndY=34.5 EndZ=0
    g37: LineSegment StartX=-49.19 StartY=31.5 StartZ=0 EndX=-18.23 EndY=31.5 EndZ=0
    g38: LineSegment StartX=-49.19 StartY=28.75 StartZ=0 EndX=-16.2837 EndY=28.75 EndZ=0
    g39: LineSegment StartX=-49.19 StartY=25.75 StartZ=0 EndX=-16.28 EndY=25.75 EndZ=0
    g40: LineSegment StartX=-49.19 StartY=23 StartZ=0 EndX=-11.49 EndY=23 EndZ=0
    g41: LineSegment StartX=-49.19 StartY=20 StartZ=0 EndX=-11.49 EndY=20 EndZ=0
    g42: LineSegment StartX=-49.19 StartY=17.25 StartZ=0 EndX=-1.5 EndY=17.25 EndZ=0
    g43: LineSegment StartX=-49.19 StartY=14.25 StartZ=0 EndX=-1.5 EndY=14.25 EndZ=0
    g44: LineSegment StartX=-49.19 StartY=11.5 StartZ=0 EndX=-1.5 EndY=11.5 EndZ=0
    g45: LineSegment StartX=-49.19 StartY=8.5 StartZ=0 EndX=-1.5 EndY=8.5 EndZ=0
    g46: LineSegment StartX=-49.19 StartY=5.75 StartZ=0 EndX=-1.5 EndY=5.75 EndZ=0
    g47: LineSegment StartX=-49.19 StartY=2.75 StartZ=0 EndX=-1.5 EndY=2.75 EndZ=0
  constraints (120):
    c: Vertical(g0)
    c: Distance(g0) = 3
    c: Block(g0)
    c: Vertical(g1)
    c: Distance(g1) = 3
    c: Vertical(g2)
    c: Equal(g0,g2) = 3
    c: Block(g2)
    c: Vertical(g3)
    c: Equal(g1,g3) = 3
    c: Vertical(g4)
    c: Equal(g0,g4) = 3
    c: Block(g4)
    c: Vertical(g5)
    c: Equal(g1,g5) = 3
    c: Vertical(g6)
    c: Equal(g0,g6) = 3
    c: Block(g6)
    c: Vertical(g7)
    c: Equal(g1,g7) = 3
    c: Vertical(g8)
    c: Equal(g0,g8) = 3
    c: Block(g8)
    c: Vertical(g9)
    c: Equal(g1,g9) = 3
    c: Vertical(g10)
    c: Equal(g0,g10) = 3
    c: Block(g10)
    c: Vertical(g11)
    c: Equal(g1,g11) = 3
    c: Block(g12)
    c: Block(g13)
    c: Block(g14)
    c: Block(g15)
    c: Block(g16)
    c: Block(g17)
    c: Block(g18)
    c: Block(g19)
    c: Block(g20)
    c: Block(g21)
    c: Block(g22)
    c: Block(g23)
    c: Block(g11)
    c: Block(g9)
    c: Block(g7)
    c: Block(g5)
    c: Block(g3)
    c: Block(g1)
    c: Coincident(g24,g0)
    c: Coincident(g24,g12)
    c: Horizontal(g24)
    c: Coincident(g25,g0)
    c: Coincident(g25,g12)
    c: Horizontal(g25)
    c: Coincident(g26,g1)
    c: Coincident(g26,g13)
    c: Horizontal(g26)
    c: Coincident(g27,g1)
    c: Coincident(g27,g13)
    c: Horizontal(g27)
    c: Coincident(g28,g2)
    c: Coincident(g28,g14)
    c: Horizontal(g28)
    c: Coincident(g29,g2)
    c: Coincident(g29,g14)
    c: Horizontal(g29)
    c: Coincident(g30,g3)
    c: Coincident(g30,g15)
    c: Horizontal(g30)
    c: Coincident(g31,g3)
    c: Coincident(g31,g15)
    c: Horizontal(g31)
    c: Coincident(g32,g4)
    c: Coincident(g32,g16)
    c: Horizontal(g32)
    c: Coincident(g33,g4)
    c: Coincident(g33,g16)
    c: Horizontal(g33)
    c: Coincident(g34,g5)
    c: Coincident(g34,g17)
    c: Horizontal(g34)
    c: Coincident(g35,g5)
    c: Coincident(g35,g17)
    c: Horizontal(g35)
    c: Coincident(g36,g6)
    c: Coincident(g36,g19)
    c: Horizontal(g36)
    c: Coincident(g37,g6)
    c: Coincident(g37,g19)
    c: Horizontal(g37)
    c: Coincident(g38,g7)
    c: Coincident(g38,g18)
    c: Horizontal(g38)
    c: Coincident(g39,g7)
    c: Coincident(g39,g18)
    c: Horizontal(g39)
    c: Coincident(g40,g8)
    c: Coincident(g40,g20)
    c: Horizontal(g40)
    c: Coincident(g41,g8)
    c: Coincident(g41,g20)
    c: Horizontal(g41)
    c: Coincident(g42,g9)
    c: Coincident(g42,g23)
    c: Horizontal(g42)
    c: Coincident(g43,g9)
    c: Coincident(g43,g23)
    c: Horizontal(g43)
    c: Coincident(g44,g10)
    c: Coincident(g44,g22)
    c: Horizontal(g44)
    c: Coincident(g45,g10)
    c: Coincident(g45,g22)
    c: Horizontal(g45)
    c: Coincident(g46,g11)
    c: Coincident(g46,g21)
    c: Horizontal(g46)
    c: Coincident(g47,g11)
    c: Coincident(g47,g21)
    c: Horizontal(g47)
FEATURE [Part::Extrusion] Extrude046
  Base = -> Sketch055
  Dir = (1,0,0)
  DirMode = 2
  FaceMakerClass = Part::FaceMakerBullseye
  LengthFwd = 23
  LengthRev = 0
  Placement = pos=(-19,0,0) rot=(0,0,1;0rad)
  Solid = true
  Symmetric = false
FEATURE [Part::Fillet] Fillet038  label="removeToCreateVentalationHoles001"
  Base = -> Extrude046
  Edges = <same value as first occurrence — deduplicated (x6 in doc)>
  Placement = pos=(7,0,0) rot=(0,0,1;0rad)
FEATURE [Sketcher::SketchObject] Sketch056  label="topSketch014"
  FullyConstrained = true
  sketch-geometry (22):
    g0: LineSegment StartX=5.21097e-06 StartY=3 StartZ=0 EndX=5.21097e-06 EndY=19 EndZ=0
    g1: ArcOfCircle CenterX=19 CenterY=19 CenterZ=0 NormalX=0 NormalY=0 NormalZ=1 AngleXU=0 Radius=19 StartAngle=1.5708 EndAngle=3.14159
    g2: ArcOfCircle CenterX=19 CenterY=19 CenterZ=0 NormalX=0 NormalY=0 NormalZ=1 AngleXU=0 Radius=16 StartAngle=1.5708 EndAngle=3.14159
    g3: LineSegment StartX=114 StartY=35 StartZ=0 EndX=19 EndY=35 EndZ=0
    g4: LineSegment StartX=5.21097e-06 StartY=3 StartZ=0 EndX=5.21097e-06 EndY=0 EndZ=0
    g5: LineSegment StartX=3 StartY=0 StartZ=0 EndX=5.21097e-06 EndY=0 EndZ=0
    g6: LineSegment StartX=3 StartY=19 StartZ=0 EndX=3 EndY=0 EndZ=0
    g7: LineSegment StartX=19 StartY=38 StartZ=0 EndX=124 EndY=38 EndZ=0
    g8: Circle CenterX=119 CenterY=35 CenterZ=0 NormalX=0 NormalY=0 NormalZ=1 AngleXU=0 Radius=1
    g9: Circle CenterX=121 CenterY=35 CenterZ=0 NormalX=0 NormalY=0 NormalZ=1 AngleXU=0 Radius=1
    g10: Circle CenterX=121 CenterY=33 CenterZ=0 NormalX=0 NormalY=0 NormalZ=1 AngleXU=0 Radius=1
    g11: BSplineCurve PolesCount=3 KnotsCount=2 Degree=2 IsPeriodic=0
    g12: GeomPoint X=119 Y=35 Z=0
    g13: GeomPoint X=121 Y=33 Z=0
    g14: LineSegment StartX=119 StartY=35 StartZ=0 EndX=114 EndY=35 EndZ=0
    g15: ArcOfCircle CenterX=105 CenterY=19 CenterZ=0 NormalX=0 NormalY=0 NormalZ=1 AngleXU=0 Radius=16 StartAngle=5.60905 EndAngle=6.28319
    g16: LineSegment StartX=121 StartY=33 StartZ=0 EndX=121 EndY=19 EndZ=0
    g17: LineSegment StartX=117.5 StartY=9.01251 StartZ=0 EndX=121.163 EndY=9.0125 EndZ=0
    g18: ArcOfCircle CenterX=105 CenterY=19 CenterZ=0 NormalX=0 NormalY=0 NormalZ=1 AngleXU=0 Radius=20.6155 StartAngle=5.7297 EndAngle=6.28319
    g19: LineSegment StartX=121.163 StartY=9.0125 StartZ=0 EndX=122.538 EndY=8.16329 EndZ=0
    g20: LineSegment StartX=124 StartY=38 StartZ=0 EndX=125.616 EndY=38 EndZ=0
    g21: LineSegment StartX=125.616 StartY=19 StartZ=0 EndX=125.616 EndY=38 EndZ=0
  constraints (49):
    c: Vertical(g0)
    c: Block(g0)
    c: Coincident(g1,g0)
    c: Block(g1)
    c: Coincident(g2,g1)
    c: Block(g2)
    c: Coincident(g3,g2)
    c: Horizontal(g3)
    c: Tangent(g3,g2)
    c: Coincident(g4,g0)
    c: Distance(g4) = 3
    c: Vertical(g4)
    c: Coincident(g5,g4)
    c: Horizontal(g5)
    c: Coincident(g6,g2)
    c: Coincident(g6,g5)
    c: Vertical(g6)
    c: Horizontal(g7)
    c: Distance(g7) = 105
    c: Coincident(g7,g1)
    c: Block(g3)
    c: Weight(g8) = 1
    c: Equal(g8,g9)
    c: Equal(g8,g10)
    c: InternalAlignment(g8,g11)
    c: InternalAlignment(g9,g11)
    c: InternalAlignment(g10,g11)
    c: InternalAlignment(g12,g11)
    c: InternalAlignment(g13,g11)
    c: Block(g11)
    c: Coincident(g14,g11)
    c: Coincident(g14,g3)
    c: Horizontal(g14)
    c: Block(g15)
    c: Coincident(g16,g11)
    c: Coincident(g16,g15)
    c: Vertical(g16)
    c: Distance(g16) = 14
    c: Coincident(g17,g15)
    c: Block(g18)
    c: Coincident(g19,g18)
    c: Coincident(g20,g7)
    c: Horizontal(g20)
    c: Vertical(g21)
    c: Coincident(g20,g21)
    c: Block(g20)
    c: Block(g21)
    c: Block(g19)
    c: Block(g17)
FEATURE [Part::Box] Box026  label="removeToCreteHoleForPlugHousing032"
  AttacherType = Attacher::AttachEngine3D
  Height = 28.6
  Length = 10
  Placement = pos=(-2,0,21.7) rot=(0,0,1;0rad)
  Width = 19
FEATURE [Part::Feature] Face109 .. Face112  x4 (patterned run collapsed; names and placements below)
  shape: bbox 3.5 x 17.8 x 2e-07 mm, 1 faces, 0 solids (baked)
FEATURE [Part::Revolution] Revolve117  label="removeToCreateScrewAndThreadedInsertHole045"
  Angle = 360
  Axis = (0,1,0)
  Base = (0,0,0)
  FaceMakerClass = Part::FaceMakerBullseye
  Placement = pos=(62.3,30.3,19.7) rot=(0,0,1;0rad)
  Solid = false
  Source = -> Face109
  Symmetric = false
FEATURE [Part::Revolution] Revolve118  label="removeToCreateScrewAndThreadedInsertHole046"
  Angle = 360
  Axis = (0,1,0)
  Base = (0,0,0)
  FaceMakerClass = Part::FaceMakerBullseye
  Placement = pos=(62.3,30.3,51.7) rot=(0,0,1;0rad)
  Solid = false
  Source = -> Face110
  Symmetric = false
FEATURE [Part::Revolution] Revolve119  label="removeToCreateScrewAndThreadedInsertHole047"
  Angle = 360
  Axis = (0,1,0)
  Base = (0,0,0)
  FaceMakerClass = Part::FaceMakerBullseye
  Placement = pos=(30.3,30.3,19.7) rot=(0,0,1;0rad)
  Solid = false
  Source = -> Face111
  Symmetric = false
FEATURE [Part::Revolution] Revolve120  label="removeToCreateScrewAndThreadedInsertHole048"
  Angle = 360
  Axis = (0,1,0)
  Base = (0,0,0)
  FaceMakerClass = Part::FaceMakerBullseye
  Placement = pos=(30.3,30.3,51.7) rot=(0,0,1;0rad)
  Solid = false
  Source = -> Face112
  Symmetric = false
FEATURE [Part::MultiFuse] Fusion087  label="createThreadedInsertHolesForFan005"
  Shapes = -> [Revolve117,Revolve118,Revolve119,Revolve120]
FEATURE [Part::Extrusion] Extrude047
  Base = -> Sketch056
  Dir = (0,0,1)
  DirMode = 2
  FaceMakerClass = Part::FaceMakerBullseye
  LengthFwd = 72
  LengthRev = 0
  Solid = true
  Symmetric = false
FEATURE [Part::Fillet] Fillet039  label="top019"
  Base = -> Extrude047
  Edges = 1 edges r=2: [Edge35]
FEATURE [Sketcher::SketchObject] Sketch057
  FullyConstrained = false
  Placement = pos=(0,0,0) rot=(1,0,0;1.5708rad)
  sketch-geometry (24):
    g0: ArcOfCircle CenterX=-4 CenterY=-10.5 CenterZ=0 NormalX=0 NormalY=0 NormalZ=1 AngleXU=0 Radius=1.5 StartAngle=6e-16 EndAngle=3.14159
    g1: ArcOfCircle CenterX=-34.2 CenterY=-10.5 CenterZ=0 NormalX=0 NormalY=0 NormalZ=1 AngleXU=0 Radius=1.5 StartAngle=0 EndAngle=3.14159
    g2: ArcOfCircle CenterX=-34.2 CenterY=-27.7 CenterZ=0 NormalX=0 NormalY=0 NormalZ=1 AngleXU=0 Radius=1.5 StartAngle=3.14159 EndAngle=6.28319
    g3: ArcOfCircle CenterX=-4 CenterY=-27.7 CenterZ=0 NormalX=0 NormalY=0 NormalZ=1 AngleXU=0 Radius=1.5 StartAngle=3.1416 EndAngle=6.28319
    g4: ArcOfCircle CenterX=-10 CenterY=-4.3 CenterZ=0 NormalX=0 NormalY=0 NormalZ=1 AngleXU=0 Radius=1.5 StartAngle=2e-16 EndAngle=3.14159
    g5: ArcOfCircle CenterX=-16.1 CenterY=-1.8 CenterZ=0 NormalX=0 NormalY=0 NormalZ=1 AngleXU=0 Radius=1.5 StartAngle=5e-16 EndAngle=3.14159
    g6: ArcOfCircle CenterX=-22.1 CenterY=-1.8 CenterZ=0 NormalX=0 NormalY=0 NormalZ=1 AngleXU=0 Radius=1.5 StartAngle=5e-16 EndAngle=3.14159
    g7: ArcOfCircle CenterX=-28.2 CenterY=-4.3 CenterZ=0 NormalX=0 NormalY=0 NormalZ=1 AngleXU=0 Radius=1.5 StartAngle=2e-16 EndAngle=3.14159
    g8: ArcOfCircle CenterX=-10 CenterY=-33.9 CenterZ=0 NormalX=0 NormalY=0 NormalZ=1 AngleXU=0 Radius=1.5 StartAngle=3.14159 EndAngle=6.28319
    g9: ArcOfCircle CenterX=-16.1 CenterY=-36.4 CenterZ=0 NormalX=0 NormalY=0 NormalZ=1 AngleXU=0 Radius=1.5 StartAngle=3.14159 EndAngle=6.28319
    g10: ArcOfCircle CenterX=-22.1 CenterY=-36.4 CenterZ=0 NormalX=0 NormalY=0 NormalZ=1 AngleXU=0 Radius=1.5 StartAngle=3.14159 EndAngle=6.28319
    g11: ArcOfCircle CenterX=-28.2 CenterY=-33.9 CenterZ=0 NormalX=0 NormalY=0 NormalZ=1 AngleXU=0 Radius=1.5 StartAngle=3.14159 EndAngle=6.28319
    g12: LineSegment StartX=-35.7 StartY=-10.5 StartZ=0 EndX=-35.7 EndY=-27.7 EndZ=0
    g13: LineSegment StartX=-32.7 StartY=-10.5 StartZ=0 EndX=-32.7 EndY=-27.7 EndZ=0
    g14: LineSegment StartX=-29.7 StartY=-33.9 StartZ=0 EndX=-29.7 EndY=-4.3 EndZ=0
    g15: LineSegment StartX=-26.7 StartY=-33.9 StartZ=0 EndX=-26.7 EndY=-4.3 EndZ=0
    g16: LineSegment StartX=-2.5 StartY=-10.5 StartZ=0 EndX=-2.5 EndY=-27.7 EndZ=0
    g17: LineSegment StartX=-8.5 StartY=-4.3 StartZ=0 EndX=-8.5 EndY=-33.9 EndZ=0
    g18: LineSegment StartX=-5.5 StartY=-10.5 StartZ=0 EndX=-5.5 EndY=-27.7 EndZ=0
    g19: LineSegment StartX=-11.5 StartY=-4.3 StartZ=0 EndX=-11.5 EndY=-33.9 EndZ=0
    g20: LineSegment StartX=-14.6 StartY=-1.8 StartZ=0 EndX=-14.6 EndY=-36.4 EndZ=0
    g21: LineSegment StartX=-17.6 StartY=-1.8 StartZ=0 EndX=-17.6 EndY=-36.4 EndZ=0
    g22: LineSegment StartX=-20.6 StartY=-36.4 StartZ=0 EndX=-20.6 EndY=-1.8 EndZ=0
    g23: LineSegment StartX=-23.6 StartY=-1.8 StartZ=0 EndX=-23.6 EndY=-36.4 EndZ=0
  constraints (48):
    c: Block(g0)
    c: Block(g1)
    c: Block(g2)
    c: Block(g3)
    c: Block(g4)
    c: Block(g5)
    c: Block(g6)
    c: Block(g7)
    c: Block(g8)
    c: Block(g9)
    c: Block(g10)
    c: Block(g11)
    c: Coincident(g12,g1)
    c: Coincident(g12,g2)
    c: Vertical(g12)
    c: Coincident(g13,g1)
    c: Coincident(g13,g2)
    c: Vertical(g13)
    c: Coincident(g14,g11)
    c: Coincident(g14,g7)
    c: Vertical(g14)
    c: Coincident(g15,g11)
    c: Coincident(g15,g7)
    c: Vertical(g15)
    c: Coincident(g16,g0)
    c: Coincident(g16,g3)
    c: Vertical(g16)
    c: Coincident(g17,g4)
    c: Coincident(g17,g8)
    c: Vertical(g17)
    c: Coincident(g18,g0)
    c: Coincident(g18,g3)
    c: Vertical(g18)
    c: Coincident(g19,g4)
    c: Coincident(g19,g8)
    c: Vertical(g19)
    c: Coincident(g20,g5)
    c: Coincident(g20,g9)
    c: Vertical(g20)
    c: Coincident(g21,g5)
    c: Coincident(g21,g9)
    c: Vertical(g21)
    c: Coincident(g22,g10)
    c: Coincident(g22,g6)
    c: Vertical(g22)
    c: Coincident(g23,g6)
    c: Coincident(g23,g10)
    c: Vertical(g23)
FEATURE [Part::Extrusion] Extrude048  label="removeToCreateFanGrillHoles004"
  Base = -> Sketch057
  Dir = (0,-1,6e-16)
  DirMode = 2
  FaceMakerClass = Part::FaceMakerBullseye
  LengthFwd = 10
  LengthRev = 0
  Placement = pos=(65.4,44,54.82) rot=(0,0,1;0rad)
  Solid = true
  Symmetric = false
FEATURE [Part::Cut] Cut040  label="top021"
  Base = -> Fillet039
  Tool = -> Extrude048
FEATURE [Part::Cylinder] Cylinder041  label="removeToCreteHoleForPlugHousing034"
  Angle = 360
  AttacherType = Attacher::AttachEngine3D
  Height = 20
  Placement = pos=(-2,19,36) rot=(0,1,0;1.5708rad)
  Radius = 14.3
FEATURE [Part::MultiFuse] Fusion089  label="removeToCreteHoleForPlugHousing035"
  Shapes = -> [Box026,Cylinder041]
FEATURE [Part::Cylinder] Cylinder042
  Angle = 360
  AttacherType = Attacher::AttachEngine3D
  Height = 20
  Placement = pos=(0,0,36.15) rot=(0,0,1;0rad)
  Radius = 14.3
FEATURE [Part::Cylinder] Cylinder043
  Angle = 360
  AttacherType = Attacher::AttachEngine3D
  Height = 10
  Placement = pos=(0,0,36.15) rot=(0,0,1;0rad)
  Radius = 4
FEATURE [Part::Box] Box027  label="removeToCreteHoleForPlugHousing036"
  AttacherType = Attacher::AttachEngine3D
  Height = 28.6
  Length = 20
  Placement = pos=(106.15,0,21.7) rot=(0,0,1;0rad)
  Width = 19
FEATURE [Part::Cut] Cut041  label="top022"
  Base = -> Cut040
  Tool = -> Fusion087
FEATURE [Part::Cut] Cut039  label="top020"
  Base = -> Cut041
  Tool = -> Fusion089
FEATURE [Part::MultiFuse] Fusion090  label="removeToCreteHoleForPlugHousing037"
  Placement = pos=(70,19,36) rot=(0,1,0;1.5708rad)
  Shapes = -> [Cylinder042,Cylinder043]
FEATURE [Part::MultiFuse] Fusion088  label="removeToCreteHoleForPlugHousing033"
  Shapes = -> [Box027,Fusion090]
FEATURE [Part::Cut] Cut042  label="removeToCreteHoleForPlugHousing038"
  Base = -> Cut039
  Tool = -> Fusion088
FEATURE [Part::MultiFuse] Fusion091  label="removeFromTop"
  Shapes = -> [Fillet038,Fusion085,Fusion084,Fusion083,Extrude045]
FEATURE [Part::Cut] Cut043  label="REAL TOP ====="
  Base = -> Fillet036
  Tool = -> Fusion091
FEATURE [Part::MultiFuse] Fusion092  label="caseScrewPillarBracket016"
  Shapes = -> [Extrude030,Extrude031,Extrude032,Extrude033,Extrude034,Extrude035,Extrude036,Extrude037,Box013,Box014]
FEATURE [Sketcher::SketchObject] Sketch058  label="topSketch015"
  FullyConstrained = true
  sketch-geometry (20):
    g0: LineSegment StartX=5.21097e-06 StartY=3 StartZ=0 EndX=5.21097e-06 EndY=19 EndZ=0
    g1: ArcOfCircle CenterX=19 CenterY=19 CenterZ=0 NormalX=0 NormalY=0 NormalZ=1 AngleXU=0 Radius=19 StartAngle=1.5708 EndAngle=3.14159
    g2: ArcOfCircle CenterX=19 CenterY=19 CenterZ=0 NormalX=0 NormalY=0 NormalZ=1 AngleXU=0 Radius=16 StartAngle=1.5708 EndAngle=3.14159
    g3: LineSegment StartX=114 StartY=35 StartZ=0 EndX=19 EndY=35 EndZ=0
    g4: LineSegment StartX=5.21097e-06 StartY=3 StartZ=0 EndX=5.21097e-06 EndY=0 EndZ=0
    g5: LineSegment StartX=3 StartY=0 StartZ=0 EndX=5.21097e-06 EndY=0 EndZ=0
    g6: LineSegment StartX=3 StartY=19 StartZ=0 EndX=3 EndY=0 EndZ=0
    g7: LineSegment StartX=19 StartY=38 StartZ=0 EndX=124 EndY=38 EndZ=0
    g8: Circle CenterX=119 CenterY=35 CenterZ=0 NormalX=0 NormalY=0 NormalZ=1 AngleXU=0 Radius=1
    g9: Circle CenterX=121 CenterY=35 CenterZ=0 NormalX=0 NormalY=0 NormalZ=1 AngleXU=0 Radius=1
    g10: Circle CenterX=121 CenterY=33 CenterZ=0 NormalX=0 NormalY=0 NormalZ=1 AngleXU=0 Radius=1
    g11: BSplineCurve PolesCount=3 KnotsCount=2 Degree=2 IsPeriodic=0
    g12: GeomPoint X=119 Y=35 Z=0
    g13: GeomPoint X=121 Y=33 Z=0
    g14: LineSegment StartX=119 StartY=35 StartZ=0 EndX=114 EndY=35 EndZ=0
    g15: ArcOfCircle CenterX=105 CenterY=19 CenterZ=0 NormalX=0 NormalY=0 NormalZ=1 AngleXU=0 Radius=19 StartAngle=5.7297 EndAngle=6.28319
    g16: ArcOfCircle CenterX=105 CenterY=19 CenterZ=0 NormalX=0 NormalY=0 NormalZ=1 AngleXU=0 Radius=16 StartAngle=5.60905 EndAngle=6.28319
    g17: LineSegment StartX=121 StartY=33 StartZ=0 EndX=121 EndY=19 EndZ=0
    g18: LineSegment StartX=124 StartY=38 StartZ=0 EndX=124 EndY=19 EndZ=0
    g19: LineSegment StartX=117.5 StartY=9.01251 StartZ=0 EndX=121.163 EndY=9.0125 EndZ=0
  constraints (46):
    c: Vertical(g0)
    c: Block(g0)
    c: Coincident(g1,g0)
    c: Block(g1)
    c: Coincident(g2,g1)
    c: Block(g2)
    c: Coincident(g3,g2)
    c: Horizontal(g3)
    c: Tangent(g3,g2)
    c: Coincident(g4,g0)
    c: Distance(g4) = 3
    c: Vertical(g4)
    c: Coincident(g5,g4)
    c: Horizontal(g5)
    c: Coincident(g6,g2)
    c: Coincident(g6,g5)
    c: Vertical(g6)
    c: Horizontal(g7)
    c: Distance(g7) = 105
    c: Coincident(g7,g1)
    c: Block(g3)
    c: Weight(g8) = 1
    c: Equal(g8,g9)
    c: Equal(g8,g10)
    c: InternalAlignment(g8,g11)
    c: InternalAlignment(g9,g11)
    c: InternalAlignment(g10,g11)
    c: InternalAlignment(g12,g11)
    c: InternalAlignment(g13,g11)
    c: Block(g11)
    c: Coincident(g14,g11)
    c: Coincident(g14,g3)
    c: Horizontal(g14)
    c: Block(g15)
    c: Coincident(g16,g15)
    c: Block(g16)
    c: Coincident(g17,g11)
    c: Coincident(g17,g16)
    c: Vertical(g17)
    c: Distance(g17) = 14
    c: Coincident(g18,g7)
    c: Coincident(g18,g15)
    c: Vertical(g18)
    c: Distance(g18) = 19
    c: Coincident(g19,g16)
    c: Coincident(g19,g15)
FEATURE [Part::Extrusion] Extrude049  label="top023"
  Base = -> Sketch058
  Dir = (0,0,1)
  DirMode = 2
  FaceMakerClass = Part::FaceMakerBullseye
  LengthFwd = 72
  LengthRev = 0
  Solid = true
  Symmetric = false
FEATURE [Sketcher::SketchObject] Sketch059
  FullyConstrained = true
  MapMode = 3
  Placement = pos=(0,0,0) rot=(1,0,0;1.5708rad)
  Support = -> [Extrude049]
  sketch-geometry (8):
    g0: Circle CenterX=80.351 CenterY=-67.6202 CenterZ=0 NormalX=0 NormalY=0 NormalZ=1 AngleXU=0 Radius=2
    g1: Circle CenterX=80.351 CenterY=-67.6202 CenterZ=0 NormalX=0 NormalY=0 NormalZ=1 AngleXU=0 Radius=3
    g2: Circle CenterX=80.351 CenterY=-4.92017 CenterZ=0 NormalX=0 NormalY=0 NormalZ=1 AngleXU=0 Radius=2
    g3: Circle CenterX=80.351 CenterY=-4.92017 CenterZ=0 NormalX=0 NormalY=0 NormalZ=1 AngleXU=0 Radius=3
    g4: Circle CenterX=23.851 CenterY=-4.92017 CenterZ=0 NormalX=0 NormalY=0 NormalZ=1 AngleXU=0 Radius=2
    g5: Circle CenterX=23.851 CenterY=-4.92017 CenterZ=0 NormalX=0 NormalY=0 NormalZ=1 AngleXU=0 Radius=3
    g6: Circle CenterX=23.851 CenterY=-67.6202 CenterZ=0 NormalX=0 NormalY=0 NormalZ=1 AngleXU=0 Radius=2
    g7: Circle CenterX=23.851 CenterY=-67.6202 CenterZ=0 NormalX=0 NormalY=0 NormalZ=1 AngleXU=0 Radius=3
  constraints (8):
    c: Block(g3)
    c: Block(g2)
    c: Block(g1)
    c: Block(g0)
    c: Block(g6)
    c: Block(g7)
    c: Block(g4)
    c: Block(g5)
FEATURE [Sketcher::SketchObject] Sketch060
  FullyConstrained = true
  MapMode = 3
  Placement = pos=(0,0,0) rot=(1,0,0;1.5708rad)
  Support = -> [Extrude049]
  sketch-geometry (8):
    g0: Circle CenterX=80.351 CenterY=-67.6202 CenterZ=0 NormalX=0 NormalY=0 NormalZ=1 AngleXU=0 Radius=3
    g1: Circle CenterX=80.351 CenterY=-4.92017 CenterZ=0 NormalX=0 NormalY=0 NormalZ=1 AngleXU=0 Radius=3
    g2: Circle CenterX=23.851 CenterY=-4.92017 CenterZ=0 NormalX=0 NormalY=0 NormalZ=1 AngleXU=0 Radius=3
    g3: Circle CenterX=23.851 CenterY=-67.6202 CenterZ=0 NormalX=0 NormalY=0 NormalZ=1 AngleXU=0 Radius=3
    g4: Circle CenterX=23.851 CenterY=-67.6202 CenterZ=0 NormalX=0 NormalY=0 NormalZ=1 AngleXU=0 Radius=5
    g5: Circle CenterX=80.351 CenterY=-67.6202 CenterZ=0 NormalX=0 NormalY=0 NormalZ=1 AngleXU=0 Radius=5
    g6: Circle CenterX=23.851 CenterY=-4.92017 CenterZ=0 NormalX=0 NormalY=0 NormalZ=1 AngleXU=0 Radius=5
    g7: Circle CenterX=80.351 CenterY=-4.92017 CenterZ=0 NormalX=0 NormalY=0 NormalZ=1 AngleXU=0 Radius=5
  constraints (8):
    c: Block(g1)
    c: Block(g0)
    c: Block(g3)
    c: Block(g2)
    c: Block(g5)
    c: Block(g4)
    c: Block(g6)
    c: Block(g7)
FEATURE [Sketcher::SketchObject] Sketch061
  FullyConstrained = true
  MapMode = 3
  Placement = pos=(0,0,0) rot=(1,0,0;1.5708rad)
  sketch-geometry (8):
    g0: Circle CenterX=80.351 CenterY=-67.6202 CenterZ=0 NormalX=0 NormalY=0 NormalZ=1 AngleXU=0 Radius=3
    g1: Circle CenterX=80.351 CenterY=-4.92017 CenterZ=0 NormalX=0 NormalY=0 NormalZ=1 AngleXU=0 Radius=3
    g2: Circle CenterX=23.851 CenterY=-4.92017 CenterZ=0 NormalX=0 NormalY=0 NormalZ=1 AngleXU=0 Radius=3
    g3: Circle CenterX=23.851 CenterY=-67.6202 CenterZ=0 NormalX=0 NormalY=0 NormalZ=1 AngleXU=0 Radius=3
    g4: Circle CenterX=23.851 CenterY=-67.6202 CenterZ=0 NormalX=0 NormalY=0 NormalZ=1 AngleXU=0 Radius=5
    g5: Circle CenterX=80.351 CenterY=-67.6202 CenterZ=0 NormalX=0 NormalY=0 NormalZ=1 AngleXU=0 Radius=5
    g6: Circle CenterX=23.851 CenterY=-4.92017 CenterZ=0 NormalX=0 NormalY=0 NormalZ=1 AngleXU=0 Radius=5
    g7: Circle CenterX=80.351 CenterY=-4.92017 CenterZ=0 NormalX=0 NormalY=0 NormalZ=1 AngleXU=0 Radius=5
  constraints (8):
    c: Block(g1)
    c: Block(g0)
    c: Block(g3)
    c: Block(g2)
    c: Block(g5)
    c: Block(g4)
    c: Block(g6)
    c: Block(g7)
FEATURE [Sketcher::SketchObject] Sketch062  label="topSketch016"
  FullyConstrained = true
  sketch-geometry (20):
    g0: LineSegment StartX=5.21097e-06 StartY=3 StartZ=0 EndX=5.21097e-06 EndY=19 EndZ=0
    g1: ArcOfCircle CenterX=19 CenterY=19 CenterZ=0 NormalX=0 NormalY=0 NormalZ=1 AngleXU=0 Radius=19 StartAngle=1.5708 EndAngle=3.14159
    g2: ArcOfCircle CenterX=19 CenterY=19 CenterZ=0 NormalX=0 NormalY=0 NormalZ=1 AngleXU=0 Radius=16 StartAngle=1.5708 EndAngle=3.14159
    g3: LineSegment StartX=114 StartY=35 StartZ=0 EndX=19 EndY=35 EndZ=0
    g4: LineSegment StartX=5.21097e-06 StartY=3 StartZ=0 EndX=5.21097e-06 EndY=0 EndZ=0
    g5: LineSegment StartX=3 StartY=0 StartZ=0 EndX=5.21097e-06 EndY=0 EndZ=0
    g6: LineSegment StartX=3 StartY=19 StartZ=0 EndX=3 EndY=0 EndZ=0
    g7: LineSegment StartX=19 StartY=38 StartZ=0 EndX=124 EndY=38 EndZ=0
    g8: Circle CenterX=119 CenterY=35 CenterZ=0 NormalX=0 NormalY=0 NormalZ=1 AngleXU=0 Radius=1
    g9: Circle CenterX=121 CenterY=35 CenterZ=0 NormalX=0 NormalY=0 NormalZ=1 AngleXU=0 Radius=1
    g10: Circle CenterX=121 CenterY=33 CenterZ=0 NormalX=0 NormalY=0 NormalZ=1 AngleXU=0 Radius=1
    g11: BSplineCurve PolesCount=3 KnotsCount=2 Degree=2 IsPeriodic=0
    g12: GeomPoint X=119 Y=35 Z=0
    g13: GeomPoint X=121 Y=33 Z=0
    g14: LineSegment StartX=119 StartY=35 StartZ=0 EndX=114 EndY=35 EndZ=0
    g15: ArcOfCircle CenterX=105 CenterY=19 CenterZ=0 NormalX=0 NormalY=0 NormalZ=1 AngleXU=0 Radius=19 StartAngle=5.7297 EndAngle=6.28319
    g16: ArcOfCircle CenterX=105 CenterY=19 CenterZ=0 NormalX=0 NormalY=0 NormalZ=1 AngleXU=0 Radius=16 StartAngle=5.60905 EndAngle=6.28319
    g17: LineSegment StartX=121 StartY=33 StartZ=0 EndX=121 EndY=19 EndZ=0
    g18: LineSegment StartX=124 StartY=38 StartZ=0 EndX=124 EndY=19 EndZ=0
    g19: LineSegment StartX=117.5 StartY=9.01251 StartZ=0 EndX=121.163 EndY=9.0125 EndZ=0
  constraints (46):
    c: Vertical(g0)
    c: Block(g0)
    c: Coincident(g1,g0)
    c: Block(g1)
    c: Coincident(g2,g1)
    c: Block(g2)
    c: Coincident(g3,g2)
    c: Horizontal(g3)
    c: Tangent(g3,g2)
    c: Coincident(g4,g0)
    c: Distance(g4) = 3
    c: Vertical(g4)
    c: Coincident(g5,g4)
    c: Horizontal(g5)
    c: Coincident(g6,g2)
    c: Coincident(g6,g5)
    c: Vertical(g6)
    c: Horizontal(g7)
    c: Distance(g7) = 105
    c: Coincident(g7,g1)
    c: Block(g3)
    c: Weight(g8) = 1
    c: Equal(g8,g9)
    c: Equal(g8,g10)
    c: InternalAlignment(g8,g11)
    c: InternalAlignment(g9,g11)
    c: InternalAlignment(g10,g11)
    c: InternalAlignment(g12,g11)
    c: InternalAlignment(g13,g11)
    c: Block(g11)
    c: Coincident(g14,g11)
    c: Coincident(g14,g3)
    c: Horizontal(g14)
    c: Block(g15)
    c: Coincident(g16,g15)
    c: Block(g16)
    c: Coincident(g17,g11)
    c: Coincident(g17,g16)
    c: Vertical(g17)
    c: Distance(g17) = 14
    c: Coincident(g18,g7)
    c: Coincident(g18,g15)
    c: Vertical(g18)
    c: Distance(g18) = 19
    c: Coincident(g19,g16)
    c: Coincident(g19,g15)
FEATURE [Part::Extrusion] Extrude053  label="top024"
  Base = -> Sketch062
  Dir = (0,0,1)
  DirMode = 2
  FaceMakerClass = Part::FaceMakerBullseye
  LengthFwd = 72
  LengthRev = 0
  Solid = true
  Symmetric = false
FEATURE [Sketcher::SketchObject] Sketch063
  FullyConstrained = true
  MapMode = 3
  Placement = pos=(0,0,0) rot=(1,0,0;1.5708rad)
  Support = -> [Extrude053]
  sketch-geometry (8):
    g0: Circle CenterX=80.351 CenterY=-67.6202 CenterZ=0 NormalX=0 NormalY=0 NormalZ=1 AngleXU=0 Radius=2
    g1: Circle CenterX=80.351 CenterY=-67.6202 CenterZ=0 NormalX=0 NormalY=0 NormalZ=1 AngleXU=0 Radius=3
    g2: Circle CenterX=80.351 CenterY=-4.92017 CenterZ=0 NormalX=0 NormalY=0 NormalZ=1 AngleXU=0 Radius=2
    g3: Circle CenterX=80.351 CenterY=-4.92017 CenterZ=0 NormalX=0 NormalY=0 NormalZ=1 AngleXU=0 Radius=3
    g4: Circle CenterX=23.851 CenterY=-4.92017 CenterZ=0 NormalX=0 NormalY=0 NormalZ=1 AngleXU=0 Radius=2
    g5: Circle CenterX=23.851 CenterY=-4.92017 CenterZ=0 NormalX=0 NormalY=0 NormalZ=1 AngleXU=0 Radius=3
    g6: Circle CenterX=23.851 CenterY=-67.6202 CenterZ=0 NormalX=0 NormalY=0 NormalZ=1 AngleXU=0 Radius=2
    g7: Circle CenterX=23.851 CenterY=-67.6202 CenterZ=0 NormalX=0 NormalY=0 NormalZ=1 AngleXU=0 Radius=3
  constraints (8):
    c: Block(g3)
    c: Block(g2)
    c: Block(g1)
    c: Block(g0)
    c: Block(g6)
    c: Block(g7)
    c: Block(g4)
    c: Block(g5)
FEATURE [Part::Extrusion] Extrude054
  Base = -> Sketch063
  Dir = (0,-1,2e-16)
  DirMode = 2
  FaceMakerClass = Part::FaceMakerBullseye
  LengthFwd = 6
  LengthRev = 0
  Placement = pos=(0,9,0) rot=(0,0,1;0rad)
  Solid = true
  Symmetric = false
FEATURE [Sketcher::SketchObject] Sketch064  label="topSketch017"
  FullyConstrained = true
  sketch-geometry (20):
    g0: LineSegment StartX=5.21097e-06 StartY=3 StartZ=0 EndX=5.21097e-06 EndY=19 EndZ=0
    g1: ArcOfCircle CenterX=19 CenterY=19 CenterZ=0 NormalX=0 NormalY=0 NormalZ=1 AngleXU=0 Radius=19 StartAngle=1.5708 EndAngle=3.14159
    g2: ArcOfCircle CenterX=19 CenterY=19 CenterZ=0 NormalX=0 NormalY=0 NormalZ=1 AngleXU=0 Radius=16 StartAngle=1.5708 EndAngle=3.14159
    g3: LineSegment StartX=114 StartY=35 StartZ=0 EndX=19 EndY=35 EndZ=0
    g4: LineSegment StartX=5.21097e-06 StartY=3 StartZ=0 EndX=5.21097e-06 EndY=0 EndZ=0
    g5: LineSegment StartX=3 StartY=0 StartZ=0 EndX=5.21097e-06 EndY=0 EndZ=0
    g6: LineSegment StartX=3 StartY=19 StartZ=0 EndX=3 EndY=0 EndZ=0
    g7: LineSegment StartX=19 StartY=38 StartZ=0 EndX=124 EndY=38 EndZ=0
    g8: Circle CenterX=119 CenterY=35 CenterZ=0 NormalX=0 NormalY=0 NormalZ=1 AngleXU=0 Radius=1
    g9: Circle CenterX=121 CenterY=35 CenterZ=0 NormalX=0 NormalY=0 NormalZ=1 AngleXU=0 Radius=1
    g10: Circle CenterX=121 CenterY=33 CenterZ=0 NormalX=0 NormalY=0 NormalZ=1 AngleXU=0 Radius=1
    g11: BSplineCurve PolesCount=3 KnotsCount=2 Degree=2 IsPeriodic=0
    g12: GeomPoint X=119 Y=35 Z=0
    g13: GeomPoint X=121 Y=33 Z=0
    g14: LineSegment StartX=119 StartY=35 StartZ=0 EndX=114 EndY=35 EndZ=0
    g15: ArcOfCircle CenterX=105 CenterY=19 CenterZ=0 NormalX=0 NormalY=0 NormalZ=1 AngleXU=0 Radius=19 StartAngle=5.7297 EndAngle=6.28319
    g16: ArcOfCircle CenterX=105 CenterY=19 CenterZ=0 NormalX=0 NormalY=0 NormalZ=1 AngleXU=0 Radius=16 StartAngle=5.60905 EndAngle=6.28319
    g17: LineSegment StartX=121 StartY=33 StartZ=0 EndX=121 EndY=19 EndZ=0
    g18: LineSegment StartX=124 StartY=38 StartZ=0 EndX=124 EndY=19 EndZ=0
    g19: LineSegment StartX=117.5 StartY=9.01251 StartZ=0 EndX=121.163 EndY=9.0125 EndZ=0
  constraints (46):
    c: Vertical(g0)
    c: Block(g0)
    c: Coincident(g1,g0)
    c: Block(g1)
    c: Coincident(g2,g1)
    c: Block(g2)
    c: Coincident(g3,g2)
    c: Horizontal(g3)
    c: Tangent(g3,g2)
    c: Coincident(g4,g0)
    c: Distance(g4) = 3
    c: Vertical(g4)
    c: Coincident(g5,g4)
    c: Horizontal(g5)
    c: Coincident(g6,g2)
    c: Coincident(g6,g5)
    c: Vertical(g6)
    c: Horizontal(g7)
    c: Distance(g7) = 105
    c: Coincident(g7,g1)
    c: Block(g3)
    c: Weight(g8) = 1
    c: Equal(g8,g9)
    c: Equal(g8,g10)
    c: InternalAlignment(g8,g11)
    c: InternalAlignment(g9,g11)
    c: InternalAlignment(g10,g11)
    c: InternalAlignment(g12,g11)
    c: InternalAlignment(g13,g11)
    c: Block(g11)
    c: Coincident(g14,g11)
    c: Coincident(g14,g3)
    c: Horizontal(g14)
    c: Block(g15)
    c: Coincident(g16,g15)
    c: Block(g16)
    c: Coincident(g17,g11)
    c: Coincident(g17,g16)
    c: Vertical(g17)
    c: Distance(g17) = 14
    c: Coincident(g18,g7)
    c: Coincident(g18,g15)
    c: Vertical(g18)
    c: Distance(g18) = 19
    c: Coincident(g19,g16)
    c: Coincident(g19,g15)
FEATURE [Sketcher::SketchObject] Sketch065
  FullyConstrained = true
  MapMode = 3
  Placement = pos=(0,0,0) rot=(1,0,0;1.5708rad)
  sketch-geometry (8):
    g0: Circle CenterX=80.351 CenterY=-67.6202 CenterZ=0 NormalX=0 NormalY=0 NormalZ=1 AngleXU=0 Radius=3
    g1: Circle CenterX=80.351 CenterY=-4.92017 CenterZ=0 NormalX=0 NormalY=0 NormalZ=1 AngleXU=0 Radius=3
    g2: Circle CenterX=23.851 CenterY=-4.92017 CenterZ=0 NormalX=0 NormalY=0 NormalZ=1 AngleXU=0 Radius=3
    g3: Circle CenterX=23.851 CenterY=-67.6202 CenterZ=0 NormalX=0 NormalY=0 NormalZ=1 AngleXU=0 Radius=3
    g4: Circle CenterX=23.851 CenterY=-67.6202 CenterZ=0 NormalX=0 NormalY=0 NormalZ=1 AngleXU=0 Radius=5
    g5: Circle CenterX=80.351 CenterY=-67.6202 CenterZ=0 NormalX=0 NormalY=0 NormalZ=1 AngleXU=0 Radius=5
    g6: Circle CenterX=23.851 CenterY=-4.92017 CenterZ=0 NormalX=0 NormalY=0 NormalZ=1 AngleXU=0 Radius=5
    g7: Circle CenterX=80.351 CenterY=-4.92017 CenterZ=0 NormalX=0 NormalY=0 NormalZ=1 AngleXU=0 Radius=5
  constraints (8):
    c: Block(g1)
    c: Block(g0)
    c: Block(g3)
    c: Block(g2)
    c: Block(g5)
    c: Block(g4)
    c: Block(g6)
    c: Block(g7)
FEATURE [Part::Extrusion] Extrude056
  Base = -> Sketch065
  Dir = (0,-1,2e-16)
  DirMode = 2
  FaceMakerClass = Part::FaceMakerBullseye
  LengthFwd = 2
  LengthRev = 0
  Solid = true
  Symmetric = false
FEATURE [Part::Extrusion] Extrude057  label="top025"
  Base = -> Sketch064
  Dir = (0,0,1)
  DirMode = 2
  FaceMakerClass = Part::FaceMakerBullseye
  LengthFwd = 72
  LengthRev = 0
  Solid = true
  Symmetric = false
FEATURE [Sketcher::SketchObject] Sketch066
  FullyConstrained = true
  MapMode = 3
  Placement = pos=(0,0,0) rot=(1,0,0;1.5708rad)
  Support = -> [Extrude057]
  sketch-geometry (8):
    g0: Circle CenterX=80.351 CenterY=-67.6202 CenterZ=0 NormalX=0 NormalY=0 NormalZ=1 AngleXU=0 Radius=3
    g1: Circle CenterX=80.351 CenterY=-4.92017 CenterZ=0 NormalX=0 NormalY=0 NormalZ=1 AngleXU=0 Radius=3
    g2: Circle CenterX=23.851 CenterY=-4.92017 CenterZ=0 NormalX=0 NormalY=0 NormalZ=1 AngleXU=0 Radius=3
    g3: Circle CenterX=23.851 CenterY=-67.6202 CenterZ=0 NormalX=0 NormalY=0 NormalZ=1 AngleXU=0 Radius=3
    g4: Circle CenterX=23.851 CenterY=-67.6202 CenterZ=0 NormalX=0 NormalY=0 NormalZ=1 AngleXU=0 Radius=5
    g5: Circle CenterX=80.351 CenterY=-67.6202 CenterZ=0 NormalX=0 NormalY=0 NormalZ=1 AngleXU=0 Radius=5
    g6: Circle CenterX=23.851 CenterY=-4.92017 CenterZ=0 NormalX=0 NormalY=0 NormalZ=1 AngleXU=0 Radius=5
    g7: Circle CenterX=80.351 CenterY=-4.92017 CenterZ=0 NormalX=0 NormalY=0 NormalZ=1 AngleXU=0 Radius=5
  constraints (8):
    c: Block(g1)
    c: Block(g0)
    c: Block(g3)
    c: Block(g2)
    c: Block(g5)
    c: Block(g4)
    c: Block(g6)
    c: Block(g7)
FEATURE [Part::Extrusion] Extrude055
  Base = -> Sketch066
  Dir = (0,-1,2e-16)
  DirMode = 2
  FaceMakerClass = Part::FaceMakerBullseye
  LengthFwd = 2
  LengthRev = 0
  Solid = true
  Symmetric = false
FEATURE [Part::Fillet] Fillet041
  Base = -> Extrude056
  Edges = 4 edges r=1.99: [Edge6,Edge12,Edge18,Edge24]
FEATURE [Part::Cut] Cut045
  Base = -> Extrude055
  Placement = pos=(0,6,0) rot=(0,0,1;0rad)
  Tool = -> Fillet041
FEATURE [Part::MultiFuse] Fusion095  label="pcbScrewPillars"
  Placement = pos=(-3.2,-1,72.3) rot=(0,0,1;0rad)
  Shapes = -> [Cut045,Extrude054]
FEATURE [Part::Feature] Face113
  shape: bbox 3.2 x 1.5 x 2e-07 mm, 1 faces, 0 solids (baked)
FEATURE [Part::Revolution] Revolve121  label="backCaseScrewRetainer002"
  Angle = 360
  Axis = (0,1,0)
  Base = (0,0,0)
  FaceMakerClass = Part::FaceMakerBullseye
  Placement = pos=(12.5,3,62) rot=(0,0,1;0rad)
  Solid = false
  Source = -> Face113
  Symmetric = false
FEATURE [Part::Feature] Face114
  shape: bbox 3.2 x 1.5 x 2e-07 mm, 1 faces, 0 solids (baked)
FEATURE [Part::Feature] Face115
  shape: bbox 3.2 x 1.5 x 2e-07 mm, 1 faces, 0 solids (baked)
FEATURE [Part::Feature] Face116
  shape: bbox 3.2 x 1.5 x 2e-07 mm, 1 faces, 0 solids (baked)
FEATURE [Part::Revolution] Revolve122  label="frontCaseScrewRetainer004"
  Angle = 360
  Axis = (0,1,0)
  Base = (0,0,0)
  FaceMakerClass = Part::FaceMakerBullseye
  Placement = pos=(89.5,3,68.5) rot=(0,0,1;0rad)
  Solid = false
  Source = -> Face115
  Symmetric = false
FEATURE [Part::Revolution] Revolve123  label="frontCaseScrewRetainer005"
  Angle = 360
  Axis = (0,1,0)
  Base = (0,0,0)
  FaceMakerClass = Part::FaceMakerBullseye
  Placement = pos=(89.5,3,3.5) rot=(0,0,1;0rad)
  Solid = false
  Source = -> Face116
  Symmetric = false
FEATURE [Part::Revolution] Revolve124  label="backCaseScrewRetainer003"
  Angle = 360
  Axis = (0,1,0)
  Base = (0,0,0)
  FaceMakerClass = Part::FaceMakerBullseye
  Placement = pos=(12.5,3,10) rot=(0,0,1;0rad)
  Solid = false
  Source = -> Face114
  Symmetric = false
FEATURE [Part::Feature] Face117
  shape: bbox 3.6 x 3.2 x 2e-07 mm, 1 faces, 0 solids (baked)
FEATURE [Part::Revolution] Revolve125  label="moreFrontCaseScrewRetainer004"
  Angle = 360
  Axis = (0,1,0)
  Base = (0,0,0)
  FaceMakerClass = Part::FaceMakerBullseye
  Placement = pos=(109.5,4.5,68.5) rot=(0,0,1;0rad)
  Solid = false
  Source = -> Face117
  Symmetric = false
FEATURE [Part::Feature] Face118
  shape: bbox 3.6 x 3.2 x 2e-07 mm, 1 faces, 0 solids (baked)
FEATURE [Part::Revolution] Revolve126  label="moreFrontCaseScrewRetainer005"
  Angle = 360
  Axis = (0,1,0)
  Base = (0,0,0)
  FaceMakerClass = Part::FaceMakerBullseye
  Placement = pos=(109.5,4.5,3.5) rot=(0,0,1;0rad)
  Solid = false
  Source = -> Face118
  Symmetric = false
FEATURE [Part::MultiFuse] Fusion096  label="screwRetainers001"
  Shapes = -> [Revolve126,Revolve125,Revolve124,Revolve123,Revolve122,Revolve121]
FEATURE [Part::Feature] Face119
  shape: bbox 10 x 16.5 x 2e-07 mm, 1 faces, 0 solids (baked)
FEATURE [Part::Revolution] Revolve130  label="plugHousing050"
  Angle = 360
  Axis = (0,1,0)
  Base = (0,0,0)
  FaceMakerClass = Part::FaceMakerBullseye
  Placement = pos=(0,0,36.15) rot=(0,0,1;0rad)
  Solid = false
  Source = -> Face119
  Symmetric = false
FEATURE [Part::Feature] Face120
  shape: bbox 10 x 16.5 x 2e-07 mm, 1 faces, 0 solids (baked)
FEATURE [Part::Feature] Face121
  shape: bbox 10 x 16.5 x 2e-07 mm, 1 faces, 0 solids (baked)
FEATURE [Part::Revolution] Revolve127  label="plugHousing047"
  Angle = 360
  Axis = (0,1,0)
  Base = (0,0,0)
  FaceMakerClass = Part::FaceMakerBullseye
  Placement = pos=(0,0,36.15) rot=(0,0,1;0rad)
  Solid = false
  Source = -> Face121
  Symmetric = false
FEATURE [Part::Feature] Face122
  shape: bbox 10 x 16.5 x 2e-07 mm, 1 faces, 0 solids (baked)
FEATURE [Part::Feature] Face123
  shape: bbox 10 x 16.5 x 2e-07 mm, 1 faces, 0 solids (baked)
FEATURE [Part::Revolution] Revolve128  label="plugHousing048"
  Angle = 360
  Axis = (0,1,0)
  Base = (0,0,0)
  FaceMakerClass = Part::FaceMakerBullseye
  Placement = pos=(0,0,36.15) rot=(0,0,1;0rad)
  Solid = false
  Source = -> Face123
  Symmetric = false
FEATURE [Part::MultiFuse] Fusion100  label="plugHousing054"
  Placement = pos=(0,0,0) rot=(0,0,1;1.5708rad)
  Shapes = -> [Revolve130,Revolve128]
FEATURE [Part::Feature] Face124
  shape: bbox 10 x 16.5 x 2e-07 mm, 1 faces, 0 solids (baked)
FEATURE [Part::Feature] Face125
  shape: bbox 10 x 16.5 x 2e-07 mm, 1 faces, 0 solids (baked)
FEATURE [Part::Revolution] Revolve129  label="plugHousing049"
  Angle = 360
  Axis = (0,1,0)
  Base = (0,0,0)
  FaceMakerClass = Part::FaceMakerBullseye
  Placement = pos=(0,0,36.15) rot=(0,0,1;0rad)
  Solid = false
  Source = -> Face125
  Symmetric = false
FEATURE [Part::Feature] Face126
  shape: bbox 10 x 16.5 x 2e-07 mm, 1 faces, 0 solids (baked)
FEATURE [Part::Revolution] Revolve131  label="plugHousing058"
  Angle = 360
  Axis = (0,1,0)
  Base = (0,0,0)
  FaceMakerClass = Part::FaceMakerBullseye
  Placement = pos=(0,0,36.15) rot=(0,0,1;0rad)
  Solid = false
  Source = -> Face120
  Symmetric = false
FEATURE [Part::MultiFuse] Fusion099  label="plugHousing053"
  Placement = pos=(0,0,0) rot=(0,0,1;1.5708rad)
  Shapes = -> [Revolve127,Revolve131]
FEATURE [Part::MultiFuse] Fusion102  label="plugHousing056"
  Placement = pos=(0,19,0) rot=(0,0,1;3.14159rad)
  Shapes = -> [Fusion100,Fusion099]
FEATURE [Part::Revolution] Revolve132  label="plugHousing059"
  Angle = 360
  Axis = (0,1,0)
  Base = (0,0,0)
  FaceMakerClass = Part::FaceMakerBullseye
  Placement = pos=(0,0,36.15) rot=(0,0,1;0rad)
  Solid = false
  Source = -> Face126
  Symmetric = false
FEATURE [Part::Revolution] Revolve133  label="plugHousing060"
  Angle = 360
  Axis = (0,1,0)
  Base = (0,0,0)
  FaceMakerClass = Part::FaceMakerBullseye
  Placement = pos=(0,0,36.15) rot=(0,0,1;0rad)
  Solid = false
  Source = -> Face122
  Symmetric = false
FEATURE [Part::MultiFuse] Fusion097  label="plugHousing051"
  Placement = pos=(0,0,0) rot=(0,0,1;1.5708rad)
  Shapes = -> [Revolve133,Revolve132]
FEATURE [Part::Revolution] Revolve134  label="plugHousing061"
  Angle = 360
  Axis = (0,1,0)
  Base = (0,0,0)
  FaceMakerClass = Part::FaceMakerBullseye
  Placement = pos=(0,0,36.15) rot=(0,0,1;0rad)
  Solid = false
  Source = -> Face124
  Symmetric = false
FEATURE [Part::MultiFuse] Fusion101  label="plugHousing055"
  Placement = pos=(0,0,0) rot=(0,0,1;1.5708rad)
  Shapes = -> [Revolve129,Revolve134]
FEATURE [Part::MultiFuse] Fusion098  label="plugHousing052"
  Placement = pos=(0,19,0) rot=(0,0,1;3.14159rad)
  Shapes = -> [Fusion097,Fusion101]
FEATURE [Part::MultiFuse] Fusion103  label="plugHousing057"
  Placement = pos=(122.621,0,-0.15) rot=(0,0,1;0rad)
  Shapes = -> [Fusion102,Fusion098]
FEATURE [Part::Box] Box028  label="Cube015"
  AttacherType = Attacher::AttachEngine3D
  Height = 28
  Length = 3
  Placement = pos=(110.7,19,22) rot=(0,0,1;0rad)
  Width = 15.7
FEATURE [Part::Cylinder] Cylinder044
  Angle = 360
  AttacherType = Attacher::AttachEngine3D
  Height = 20
  Placement = pos=(0,0,36.15) rot=(0,0,1;0rad)
  Radius = 10.3
FEATURE [Part::Cylinder] Cylinder045
  Angle = 360
  AttacherType = Attacher::AttachEngine3D
  Height = 10
  Placement = pos=(0,0,36.15) rot=(0,0,1;0rad)
  Radius = 4
FEATURE [Part::MultiFuse] Fusion104  label="removeToCreteHoleForPlugHousing040"
  Placement = pos=(70,19,36) rot=(0,1,0;1.5708rad)
  Shapes = -> [Cylinder044,Cylinder045]
FEATURE [Part::Cut] Cut046  label="plugHousingTab003"
  Base = -> Box028
  Tool = -> Fusion104
FEATURE [Part::MultiFuse] Fusion105  label="plugHousing062"
  Shapes = -> [Fusion103,Cut046]
FEATURE [Part::Fillet] Fillet042
  Base = -> Fusion105
  Edges = 1 edges r=2: [Edge25]
FEATURE [Part::Fillet] Fillet043  label="plugHousing063"
  Base = -> Fillet042
  Edges = 1 edges r=2: [Edge8]
  Placement = pos=(7,0,0) rot=(0,0,1;0rad)
FEATURE [Part::Feature] Face127
  shape: bbox 10 x 16.5 x 2e-07 mm, 1 faces, 0 solids (baked)
FEATURE [Part::Feature] Face128
  shape: bbox 10 x 16.5 x 2e-07 mm, 1 faces, 0 solids (baked)
FEATURE [Part::Revolution] Revolve137  label="plugHousing070"
  Angle = 360
  Axis = (0,1,0)
  Base = (0,0,0)
  FaceMakerClass = Part::FaceMakerBullseye
  Placement = pos=(0,0,36.15) rot=(0,0,1;0rad)
  Solid = false
  Source = -> Face127
  Symmetric = false
FEATURE [Part::Revolution] Revolve140  label="plugHousing073"
  Angle = 360
  Axis = (0,1,0)
  Base = (0,0,0)
  FaceMakerClass = Part::FaceMakerBullseye
  Placement = pos=(0,0,36.15) rot=(0,0,1;0rad)
  Solid = false
  Source = -> Face128
  Symmetric = false
FEATURE [Part::Feature] Face129
  shape: bbox 10 x 16.5 x 2e-07 mm, 1 faces, 0 solids (baked)
FEATURE [Part::Revolution] Revolve138  label="plugHousing071"
  Angle = 360
  Axis = (0,1,0)
  Base = (0,0,0)
  FaceMakerClass = Part::FaceMakerBullseye
  Placement = pos=(0,0,36.15) rot=(0,0,1;0rad)
  Solid = false
  Source = -> Face129
  Symmetric = false
FEATURE [Part::Feature] Face130
  shape: bbox 10 x 16.5 x 2e-07 mm, 1 faces, 0 solids (baked)
FEATURE [Part::Revolution] Revolve139  label="plugHousing072"
  Angle = 360
  Axis = (0,1,0)
  Base = (0,0,0)
  FaceMakerClass = Part::FaceMakerBullseye
  Placement = pos=(0,0,36.15) rot=(0,0,1;0rad)
  Solid = false
  Source = -> Face130
  Symmetric = false
FEATURE [Part::Feature] Face131
  shape: bbox 10 x 16.5 x 2e-07 mm, 1 faces, 0 solids (baked)
FEATURE [Part::Revolution] Revolve135  label="plugHousing068"
  Angle = 360
  Axis = (0,1,0)
  Base = (0,0,0)
  FaceMakerClass = Part::FaceMakerBullseye
  Placement = pos=(0,0,36.15) rot=(0,0,1;0rad)
  Solid = false
  Source = -> Face131
  Symmetric = false
FEATURE [Part::MultiFuse] Fusion112  label="plugHousing078"
  Placement = pos=(0,0,0) rot=(0,0,1;1.5708rad)
  Shapes = -> [Revolve135,Revolve139]
FEATURE [Part::Feature] Face132
  shape: bbox 10 x 16.5 x 2e-07 mm, 1 faces, 0 solids (baked)
FEATURE [Part::Revolution] Revolve141  label="plugHousing074"
  Angle = 360
  Axis = (0,1,0)
  Base = (0,0,0)
  FaceMakerClass = Part::FaceMakerBullseye
  Placement = pos=(0,0,36.15) rot=(0,0,1;0rad)
  Solid = false
  Source = -> Face132
  Symmetric = false
FEATURE [Part::MultiFuse] Fusion110  label="plugHousing076"
  Placement = pos=(0,0,0) rot=(0,0,1;1.5708rad)
  Shapes = -> [Revolve141,Revolve140]
FEATURE [Part::Feature] Face133
  shape: bbox 10 x 16.5 x 2e-07 mm, 1 faces, 0 solids (baked)
FEATURE [Part::Revolution] Revolve136  label="plugHousing069"
  Angle = 360
  Axis = (0,1,0)
  Base = (0,0,0)
  FaceMakerClass = Part::FaceMakerBullseye
  Placement = pos=(0,0,36.15) rot=(0,0,1;0rad)
  Solid = false
  Source = -> Face133
  Symmetric = false
FEATURE [Part::MultiFuse] Fusion106  label="plugHousing064"
  Placement = pos=(0,0,0) rot=(0,0,1;1.5708rad)
  Shapes = -> [Revolve138,Revolve136]
FEATURE [Part::MultiFuse] Fusion108  label="plugHousing066"
  Placement = pos=(0,19,0) rot=(0,0,1;3.14159rad)
  Shapes = -> [Fusion106,Fusion112]
FEATURE [Part::Feature] Face134
  shape: bbox 10 x 16.5 x 2e-07 mm, 1 faces, 0 solids (baked)
FEATURE [Part::Revolution] Revolve142  label="plugHousing075"
  Angle = 360
  Axis = (0,1,0)
  Base = (0,0,0)
  FaceMakerClass = Part::FaceMakerBullseye
  Placement = pos=(0,0,36.15) rot=(0,0,1;0rad)
  Solid = false
  Source = -> Face134
  Symmetric = false
FEATURE [Part::MultiFuse] Fusion107  label="plugHousing065"
  Placement = pos=(0,0,0) rot=(0,0,1;1.5708rad)
  Shapes = -> [Revolve137,Revolve142]
FEATURE [Part::MultiFuse] Fusion111  label="plugHousing077"
  Placement = pos=(0,19,0) rot=(0,0,1;3.14159rad)
  Shapes = -> [Fusion110,Fusion107]
FEATURE [Part::MultiFuse] Fusion109  label="plugHousing067"
  Placement = pos=(131.236,0,-0.15) rot=(0,0,1;0rad)
  Shapes = -> [Fusion108,Fusion111]
FEATURE [Part::MultiFuse] Fusion113  label="plugHousing079"
  Shapes = -> [Fillet043,Fusion109]
FEATURE [Part::Feature] Face135
  shape: bbox 3.5 x 17.8 x 2e-07 mm, 1 faces, 0 solids (baked)
FEATURE [Part::Revolution] Revolve143  label="removeToCreateScrewAndThreadedInsertHole049"
  Angle = 360
  Axis = (0,1,0)
  Base = (0,0,0)
  FaceMakerClass = Part::FaceMakerBullseye
  Placement = pos=(12.5,0,10) rot=(0,0,1;0rad)
  Solid = false
  Source = -> Face135
  Symmetric = false
FEATURE [Part::Feature] Face136
  shape: bbox 3.5 x 17.8 x 2e-07 mm, 1 faces, 0 solids (baked)
FEATURE [Part::Revolution] Revolve144  label="removeToCreateScrewAndThreadedInsertHole050"
  Angle = 360
  Axis = (0,1,0)
  Base = (0,0,0)
  FaceMakerClass = Part::FaceMakerBullseye
  Placement = pos=(12.5,0,62) rot=(0,0,1;0rad)
  Solid = false
  Source = -> Face136
  Symmetric = false
FEATURE [Part::Feature] Face137
  shape: bbox 3.5 x 17.8 x 2e-07 mm, 1 faces, 0 solids (baked)
FEATURE [Part::Revolution] Revolve145  label="removeToCreateScrewAndThreadedInsertHole051"
  Angle = 360
  Axis = (0,1,0)
  Base = (0,0,0)
  FaceMakerClass = Part::FaceMakerBullseye
  Placement = pos=(89.5,0,68.5) rot=(0,0,1;0rad)
  Solid = false
  Source = -> Face137
  Symmetric = false
FEATURE [Part::Feature] Face138
  shape: bbox 3.5 x 17.8 x 2e-07 mm, 1 faces, 0 solids (baked)
FEATURE [Part::Revolution] Revolve146  label="removeToCreateScrewAndThreadedInsertHole052"
  Angle = 360
  Axis = (0,1,0)
  Base = (0,0,0)
  FaceMakerClass = Part::FaceMakerBullseye
  Placement = pos=(89.5,0,3.5) rot=(0,0,1;0rad)
  Solid = false
  Source = -> Face138
  Symmetric = false
FEATURE [Part::Feature] Face139
  shape: bbox 3.5 x 17.8 x 2e-07 mm, 1 faces, 0 solids (baked)
FEATURE [Part::Revolution] Revolve147  label="removeToCreateScrewAndThreadedInsertHole053"
  Angle = 360
  Axis = (0,1,0)
  Base = (0,0,0)
  FaceMakerClass = Part::FaceMakerBullseye
  Placement = pos=(109.5,4.7,3.5) rot=(0,0,1;0rad)
  Solid = false
  Source = -> Face139
  Symmetric = false
FEATURE [Part::Feature] Face140
  shape: bbox 3.5 x 17.8 x 2e-07 mm, 1 faces, 0 solids (baked)
FEATURE [Part::Revolution] Revolve148  label="removeToCreateScrewAndThreadedInsertHole054"
  Angle = 360
  Axis = (0,1,0)
  Base = (0,0,0)
  FaceMakerClass = Part::FaceMakerBullseye
  Placement = pos=(109.5,4.7,68.5) rot=(0,0,1;0rad)
  Solid = false
  Source = -> Face140
  Symmetric = false
FEATURE [Part::MultiFuse] Fusion114  label="removeToCreateScrewAndThreadedInsertHole055"
  Shapes = -> [Revolve148,Revolve147,Revolve146,Revolve145,Revolve144,Revolve143]
FEATURE [Part::Cut] Cut047  label="casePillars004"
  Base = -> Cut037
  Tool = -> Fusion114
FEATURE [Part::Feature] Face141
  shape: bbox 3.5 x 17.8 x 2e-07 mm, 1 faces, 0 solids (baked)
FEATURE [Part::Feature] Face142
  shape: bbox 3.5 x 17.8 x 2e-07 mm, 1 faces, 0 solids (baked)
FEATURE [Part::Feature] Face143
  shape: bbox 3.5 x 17.8 x 2e-07 mm, 1 faces, 0 solids (baked)
FEATURE [Part::Revolution] Revolve149  label="removeToCreateScrewAndThreadedInsertHole057"
  Angle = 360
  Axis = (0,1,0)
  Base = (0,0,0)
  FaceMakerClass = Part::FaceMakerBullseye
  Placement = pos=(12.5,0,10) rot=(0,0,1;0rad)
  Solid = false
  Source = -> Face141
  Symmetric = false
FEATURE [Part::Feature] Face144
  shape: bbox 3.5 x 17.8 x 2e-07 mm, 1 faces, 0 solids (baked)
FEATURE [Part::Feature] Face145
  shape: bbox 3.5 x 17.8 x 2e-07 mm, 1 faces, 0 solids (baked)
FEATURE [Part::Feature] Face146
  shape: bbox 3.5 x 17.8 x 2e-07 mm, 1 faces, 0 solids (baked)
FEATURE [Part::Revolution] Revolve150  label="removeToCreateScrewAndThreadedInsertHole058"
  Angle = 360
  Axis = (0,1,0)
  Base = (0,0,0)
  FaceMakerClass = Part::FaceMakerBullseye
  Placement = pos=(12.5,0,62) rot=(0,0,1;0rad)
  Solid = false
  Source = -> Face146
  Symmetric = false
FEATURE [Part::Revolution] Revolve151  label="removeToCreateScrewAndThreadedInsertHole059"
  Angle = 360
  Axis = (0,1,0)
  Base = (0,0,0)
  FaceMakerClass = Part::FaceMakerBullseye
  Placement = pos=(89.5,0,68.5) rot=(0,0,1;0rad)
  Solid = false
  Source = -> Face143
  Symmetric = false
FEATURE [Part::Revolution] Revolve152  label="removeToCreateScrewAndThreadedInsertHole060"
  Angle = 360
  Axis = (0,1,0)
  Base = (0,0,0)
  FaceMakerClass = Part::FaceMakerBullseye
  Placement = pos=(89.5,0,3.5) rot=(0,0,1;0rad)
  Solid = false
  Source = -> Face142
  Symmetric = false
FEATURE [Part::Revolution] Revolve153  label="removeToCreateScrewAndThreadedInsertHole061"
  Angle = 360
  Axis = (0,1,0)
  Base = (0,0,0)
  FaceMakerClass = Part::FaceMakerBullseye
  Placement = pos=(109.5,4.7,3.5) rot=(0,0,1;0rad)
  Solid = false
  Source = -> Face145
  Symmetric = false
FEATURE [Part::Revolution] Revolve154  label="removeToCreateScrewAndThreadedInsertHole062"
  Angle = 360
  Axis = (0,1,0)
  Base = (0,0,0)
  FaceMakerClass = Part::FaceMakerBullseye
  Placement = pos=(109.5,4.7,68.5) rot=(0,0,1;0rad)
  Solid = false
  Source = -> Face144
  Symmetric = false
FEATURE [Part::MultiFuse] Fusion115  label="removeToCreateScrewAndThreadedInsertHole056"
  Shapes = -> [Revolve154,Revolve153,Revolve152,Revolve151,Revolve150,Revolve149]
FEATURE [Part::Feature] Face147
  shape: bbox 9.8 x 26.5 x 2e-07 mm, 1 faces, 0 solids (baked)
FEATURE [Part::Revolution] Revolve155
  Angle = 360
  Axis = (0,1,0)
  Base = (0,0,0)
  FaceMakerClass = Part::FaceMakerBullseye
  Placement = pos=(0,0,0) rot=(0,0,1;1.5708rad)
  Solid = false
  Source = -> Face147
  Symmetric = false
FEATURE [Part::Feature] Face148
  shape: bbox 9.8 x 26.5 x 2e-07 mm, 1 faces, 0 solids (baked)
FEATURE [Part::Revolution] Revolve156
  Angle = 360
  Axis = (0,1,0)
  Base = (0,0,0)
  FaceMakerClass = Part::FaceMakerBullseye
  Placement = pos=(0,0,0) rot=(0,0,1;1.5708rad)
  Solid = false
  Source = -> Face148
  Symmetric = false
FEATURE [Part::MultiFuse] Fusion116
  Placement = pos=(-18,19,36) rot=(0,0,1;0rad)
  Shapes = -> [Revolve156,Revolve155]
FEATURE [Part::Box] Box029  label="Cube016"
  AttacherType = Attacher::AttachEngine3D
  Height = 28
  Length = 3
  Placement = pos=(110.7,19,22) rot=(0,0,1;0rad)
  Width = 15.7
FEATURE [Part::Cylinder] Cylinder046
  Angle = 360
  AttacherType = Attacher::AttachEngine3D
  Height = 10
  Placement = pos=(0,0,36.15) rot=(0,0,1;0rad)
  Radius = 4
FEATURE [Part::Cylinder] Cylinder047
  Angle = 360
  AttacherType = Attacher::AttachEngine3D
  Height = 20
  Placement = pos=(0,0,36.15) rot=(0,0,1;0rad)
  Radius = 10.3
FEATURE [Part::MultiFuse] Fusion117  label="removeToCreteHoleForPlugHousing041"
  Placement = pos=(70,19,36) rot=(0,1,0;1.5708rad)
  Shapes = -> [Cylinder047,Cylinder046]
FEATURE [Part::Cut] Cut049  label="plugHousingTab004"
  Base = -> Box029
  Placement = pos=(-107.4,-14,0) rot=(0,0,1;0rad)
  Tool = -> Fusion117
FEATURE [Part::Box] Box030  label="Cube017"
  AttacherType = Attacher::AttachEngine3D
  Height = 28
  Length = 3
  Placement = pos=(110.7,19,22) rot=(0,0,1;0rad)
  Width = 15.7
FEATURE [Part::Cylinder] Cylinder048
  Angle = 360
  AttacherType = Attacher::AttachEngine3D
  Height = 10
  Placement = pos=(0,0,36.15) rot=(0,0,1;0rad)
  Radius = 4
FEATURE [Part::Cylinder] Cylinder049
  Angle = 360
  AttacherType = Attacher::AttachEngine3D
  Height = 20
  Placement = pos=(0,0,36.15) rot=(0,0,1;0rad)
  Radius = 10.3
FEATURE [Part::MultiFuse] Fusion118  label="removeToCreteHoleForPlugHousing042"
  Placement = pos=(70,19,36) rot=(0,1,0;1.5708rad)
  Shapes = -> [Cylinder049,Cylinder048]
FEATURE [Part::Cut] Cut050  label="plugHousingTab005"
  Base = -> Box030
  Placement = pos=(-107.4,-14,0) rot=(0,0,1;0rad)
  Tool = -> Fusion118
FEATURE [Part::MultiFuse] Fusion119
  Placement = pos=(9.6,23,0) rot=(0,0,1;3.14159rad)
  Shapes = -> [Cut049,Cut050]
FEATURE [Part::Box] Box031  label="Cube018"
  AttacherType = Attacher::AttachEngine3D
  Height = 10
  Length = 3
  Placement = pos=(3.3,4,12) rot=(0,0,1;0rad)
  Width = 10
FEATURE [Part::Fillet] Fillet044
  Base = -> Box031
  Edges = 1 edges r=2: [Edge11]
FEATURE [Part::Box] Box032  label="Cube019"
  AttacherType = Attacher::AttachEngine3D
  Height = 10
  Length = 3
  Placement = pos=(3.3,4,50) rot=(0,0,1;0rad)
  Width = 10
FEATURE [Part::Fillet] Fillet045
  Base = -> Box032
  Edges = 1 edges r=2: [Edge12]
FEATURE [Part::Box] Box033  label="Cube020"
  AttacherType = Attacher::AttachEngine3D
  Height = 28
  Length = 4
  Placement = pos=(5,0,22) rot=(0,0,1;0rad)
  Width = 10
FEATURE [Part::Fillet] Fillet046
  Base = -> Box033
  Edges = 1 edges r=1: [Edge7]
FEATURE [Part::Fillet] Fillet047
  Base = -> Fillet046
  Edges = 1 edges r=2: [Edge5]
FEATURE [Part::Fillet] Fillet048
  Base = -> Fillet047
  Edges = 1 edges r=2: [Edge2]
FEATURE [Part::Cylinder] Cylinder050
  Angle = 360
  AttacherType = Attacher::AttachEngine3D
  Height = 20
  Placement = pos=(0,0,36.15) rot=(0,0,1;0rad)
  Radius = 8.2
FEATURE [Part::Cylinder] Cylinder051
  Angle = 360
  AttacherType = Attacher::AttachEngine3D
  Height = 10
  Placement = pos=(0,0,36.15) rot=(0,0,1;0rad)
  Radius = 4
FEATURE [Part::MultiFuse] Fusion120  label="removeToCreteHoleForPlugHousing043"
  Placement = pos=(-42,19,36) rot=(0,1,0;1.5708rad)
  Shapes = -> [Cylinder050,Cylinder051]
FEATURE [Sketcher::SketchObject] Sketch067  label="topSketch018"
  FullyConstrained = true
  sketch-geometry (4):
    g0: LineSegment StartX=16.8446 StartY=31.512 StartZ=0 EndX=16.3251 EndY=34.4666 EndZ=0
    g1: ArcOfCircle CenterX=19 CenterY=19.2524 CenterZ=0 NormalX=0 NormalY=0 NormalZ=1 AngleXU=0 Radius=15.4476 StartAngle=1.74483 EndAngle=2.72717
    g2: ArcOfCircle CenterX=19 CenterY=19.2524 CenterZ=0 NormalX=0 NormalY=0 NormalZ=1 AngleXU=0 Radius=12.4476 StartAngle=1.74483 EndAngle=2.73189
    g3: LineSegment StartX=4.86004 StartY=25.4725 StartZ=0 EndX=7.58253 EndY=24.2107 EndZ=0
  constraints (7):
    c: Block(g0)
    c: Coincident(g1,g0)
    c: Coincident(g2,g0)
    c: Coincident(g3,g1)
    c: Coincident(g3,g2)
    c: Block(g1)
    c: Block(g2)
FEATURE [Part::Extrusion] Extrude058
  Base = -> Sketch067
  Dir = (0,0,1)
  DirMode = 2
  FaceMakerClass = Part::FaceMakerBullseye
  LengthFwd = 10
  LengthRev = 0
  Placement = pos=(0,0,31) rot=(0,0,1;0rad)
  Solid = true
  Symmetric = false
FEATURE [Part::Cut] Cut051
  Base = -> Extrude058
  Tool = -> Fusion120
FEATURE [Part::Fillet] Fillet049
  Base = -> Cut051
  Edges = 1 edges r=2: [Edge1]
FEATURE [Part::Fillet] Fillet050
  Base = -> Fillet049
  Edges = 1 edges r=2.5: [Edge1]
FEATURE [Part::Fillet] Fillet051
  Base = -> Fillet050
  Edges = 1 edges r=2.5: [Edge2]
FEATURE [Part::MultiFuse] Fusion121  label="wireHolder003"
  Shapes = -> [Fusion116,Fillet051]
FEATURE [Part::MultiFuse] Fusion122
  Shapes = -> [Fillet045,Fusion121]
FEATURE [Part::MultiFuse] Fusion123  label="wireHolder004"
  Shapes = -> [Fusion122,Fillet048]
FEATURE [Part::MultiFuse] Fusion124  label="wireHolder005"
  Shapes = -> [Fillet044,Fusion119,Fusion123]
FEATURE [Sketcher::SketchObject] Sketch068  label="topSketch019"
  FullyConstrained = true
  sketch-geometry (6):
    g0: LineSegment StartX=19 StartY=38 StartZ=0 EndX=117 EndY=38 EndZ=0
    g1: ArcOfCircle CenterX=19 CenterY=19 CenterZ=0 NormalX=0 NormalY=0 NormalZ=1 AngleXU=0 Radius=19 StartAngle=1.5708 EndAngle=3.14159
    g2: LineSegment StartX=117 StartY=38 StartZ=0 EndX=117 EndY=19 EndZ=0
    g3: LineSegment StartX=98 StartY=1.0161e-12 StartZ=0 EndX=5.22862e-06 EndY=1.0161e-12 EndZ=0
    g4: LineSegment StartX=5.22862e-06 StartY=19 StartZ=0 EndX=5.22862e-06 EndY=1.0161e-12 EndZ=0
    g5: ArcOfCircle CenterX=98 CenterY=19 CenterZ=0 NormalX=0 NormalY=0 NormalZ=1 AngleXU=0 Radius=19 StartAngle=4.71239 EndAngle=6.28319
  constraints (16):
    c: Horizontal(g0)
    c: Distance(g0) = 98
    c: Coincident(g1,g0)
    c: Block(g1)
    c: Coincident(g2,g0)
    c: Vertical(g2)
    c: Distance(g2) = 19
    c: Horizontal(g3)
    c: Coincident(g4,g1)
    c: Vertical(g4)
    c: Coincident(g3,g4)
    c: Block(g3)
    c: Coincident(g5,g2)
    c: Coincident(g5,g3)
    c: Block(g0)
    c: Block(g5)
FEATURE [Part::Extrusion] Extrude059  label="sideA002"
  Base = -> Sketch068
  Dir = (0,0,1)
  DirMode = 2
  FaceMakerClass = Part::FaceMakerBullseye
  LengthFwd = 3
  LengthRev = 0
  Placement = pos=(0,0,-2.7) rot=(0,0,1;0rad)
  Solid = true
  Symmetric = false
FEATURE [Sketcher::SketchObject] Sketch069  label="topSketch020"
  FullyConstrained = true
  sketch-geometry (6):
    g0: LineSegment StartX=19 StartY=38 StartZ=0 EndX=117 EndY=38 EndZ=0
    g1: ArcOfCircle CenterX=19 CenterY=19 CenterZ=0 NormalX=0 NormalY=0 NormalZ=1 AngleXU=0 Radius=19 StartAngle=1.5708 EndAngle=3.14159
    g2: LineSegment StartX=117 StartY=38 StartZ=0 EndX=117 EndY=19 EndZ=0
    g3: LineSegment StartX=98 StartY=1.0161e-12 StartZ=0 EndX=5.22862e-06 EndY=1.0161e-12 EndZ=0
    g4: LineSegment StartX=5.22862e-06 StartY=19 StartZ=0 EndX=5.22862e-06 EndY=1.0161e-12 EndZ=0
    g5: ArcOfCircle CenterX=98 CenterY=19 CenterZ=0 NormalX=0 NormalY=0 NormalZ=1 AngleXU=0 Radius=19 StartAngle=4.71239 EndAngle=6.28319
  constraints (16):
    c: Horizontal(g0)
    c: Distance(g0) = 98
    c: Coincident(g1,g0)
    c: Block(g1)
    c: Coincident(g2,g0)
    c: Vertical(g2)
    c: Distance(g2) = 19
    c: Horizontal(g3)
    c: Coincident(g4,g1)
    c: Vertical(g4)
    c: Coincident(g3,g4)
    c: Block(g3)
    c: Coincident(g5,g2)
    c: Coincident(g5,g3)
    c: Block(g0)
    c: Block(g5)
FEATURE [Part::Extrusion] Extrude060  label="sideB002"
  Base = -> Sketch069
  Dir = (0,0,1)
  DirMode = 2
  FaceMakerClass = Part::FaceMakerBullseye
  LengthFwd = 3
  LengthRev = 0
  Placement = pos=(0,0,71.7) rot=(0,0,1;0rad)
  Solid = true
  Symmetric = false
FEATURE [Part::MultiFuse] Fusion127  label="removeFromBottom001"
  Placement = pos=(2,0,0) rot=(0,0,1;0rad)
  Shapes = -> [Extrude059,Extrude060]
FEATURE [Part::Cylinder] Cylinder052
  Angle = 360
  AttacherType = Attacher::AttachEngine3D
  Height = 20
  Placement = pos=(0,0,36.15) rot=(0,0,1;0rad)
  Radius = 14
FEATURE [Part::Cylinder] Cylinder053
  Angle = 360
  AttacherType = Attacher::AttachEngine3D
  Height = 10
  Placement = pos=(0,0,36.15) rot=(0,0,1;0rad)
  Radius = 4
FEATURE [Part::MultiFuse] Fusion128  label="removeToCreteHoleForPlugHousing044"
  Placement = pos=(70,19,36) rot=(0,1,0;1.5708rad)
  Shapes = -> [Cylinder052,Cylinder053]
FEATURE [Part::Cut] Cut052  label="bottom011"
  Base = -> Extrude043
  Tool = -> Fusion128
FEATURE [Part::Cut] Cut054  label="bottom012"
  Base = -> Cut052
  Tool = -> Fusion115
FEATURE [Sketcher::SketchObject] Sketch070
  FullyConstrained = true
  Placement = pos=(117,19,0) rot=(0.57735,0.57735,0.57735;2.0944rad)
  sketch-geometry (48):
    g0: LineSegment StartX=-49.19 StartY=69.25 StartZ=0 EndX=-49.19 EndY=66.25 EndZ=0
    g1: LineSegment StartX=-49.19 StartY=63.5 StartZ=0 EndX=-49.19 EndY=60.5 EndZ=0
    g2: LineSegment StartX=-49.19 StartY=57.75 StartZ=0 EndX=-49.19 EndY=54.75 EndZ=0
    g3: LineSegment StartX=-49.19 StartY=52 StartZ=0 EndX=-49.19 EndY=49 EndZ=0
    g4: LineSegment StartX=-49.19 StartY=46.25 StartZ=0 EndX=-49.19 EndY=43.25 EndZ=0
    g5: LineSegment StartX=-49.19 StartY=40.5 StartZ=0 EndX=-49.19 EndY=37.5 EndZ=0
    g6: LineSegment StartX=-49.19 StartY=34.5 StartZ=0 EndX=-49.19 EndY=31.5 EndZ=0
    g7: LineSegment StartX=-49.19 StartY=28.75 StartZ=0 EndX=-49.19 EndY=25.75 EndZ=0
    g8: LineSegment StartX=-49.19 StartY=23 StartZ=0 EndX=-49.19 EndY=20 EndZ=0
    g9: LineSegment StartX=-49.19 StartY=17.25 StartZ=0 EndX=-49.19 EndY=14.25 EndZ=0
    g10: LineSegment StartX=-49.19 StartY=11.5 StartZ=0 EndX=-49.19 EndY=8.5 EndZ=0
    g11: LineSegment StartX=-49.19 StartY=5.75 StartZ=0 EndX=-49.19 EndY=2.75 EndZ=0
    g12: ArcOfCircle CenterX=-1.5 CenterY=67.75 CenterZ=0 NormalX=0 NormalY=0 NormalZ=1 AngleXU=0 Radius=1.5 StartAngle=4.71239 EndAngle=7.85398
    g13: ArcOfCircle CenterX=-1.5 CenterY=62 CenterZ=0 NormalX=0 NormalY=0 NormalZ=1 AngleXU=0 Radius=1.5 StartAngle=4.71239 EndAngle=7.85398
    g14: ArcOfCircle CenterX=-1.5 CenterY=56.25 CenterZ=0 NormalX=0 NormalY=0 NormalZ=1 AngleXU=0 Radius=1.5 StartAngle=4.71239 EndAngle=7.85398
    g15: ArcOfCircle CenterX=-11.49 CenterY=50.5 CenterZ=0 NormalX=0 NormalY=0 NormalZ=1 AngleXU=0 Radius=1.5 StartAngle=4.71239 EndAngle=7.85398
    g16: ArcOfCircle CenterX=-16.28 CenterY=44.75 CenterZ=0 NormalX=0 NormalY=0 NormalZ=1 AngleXU=0 Radius=1.5 StartAngle=4.71239 EndAngle=7.85398
    g17: ArcOfCircle CenterX=-18.2337 CenterY=39 CenterZ=0 NormalX=0 NormalY=0 NormalZ=1 AngleXU=0 Radius=1.5 StartAngle=4.71485 EndAngle=7.85398
    g18: ArcOfCircle CenterX=-16.2837 CenterY=27.25 CenterZ=0 NormalX=0 NormalY=0 NormalZ=1 AngleXU=0 Radius=1.5 StartAngle=4.71485 EndAngle=7.85398
    g19: ArcOfCircle CenterX=-18.2337 CenterY=33 CenterZ=0 NormalX=0 NormalY=0 NormalZ=1 AngleXU=0 Radius=1.5 StartAngle=4.71485 EndAngle=7.85398
    g20: ArcOfCircle CenterX=-11.49 CenterY=21.5 CenterZ=0 NormalX=0 NormalY=0 NormalZ=1 AngleXU=0 Radius=1.5 StartAngle=4.71239 EndAngle=7.85398
    g21: ArcOfCircle CenterX=-1.5 CenterY=4.25 CenterZ=0 NormalX=0 NormalY=0 NormalZ=1 AngleXU=0 Radius=1.5 StartAngle=4.71239 EndAngle=7.85398
    g22: ArcOfCircle CenterX=-1.5 CenterY=10 CenterZ=0 NormalX=0 NormalY=0 NormalZ=1 AngleXU=0 Radius=1.5 StartAngle=4.71239 EndAngle=7.85398
    g23: ArcOfCircle CenterX=-1.5 CenterY=15.75 CenterZ=0 NormalX=0 NormalY=0 NormalZ=1 AngleXU=0 Radius=1.5 StartAngle=4.71239 EndAngle=7.85398
    g24: LineSegment StartX=-49.19 StartY=69.25 StartZ=0 EndX=-1.5 EndY=69.25 EndZ=0
    g25: LineSegment StartX=-49.19 StartY=66.25 StartZ=0 EndX=-1.5 EndY=66.25 EndZ=0
    g26: LineSegment StartX=-49.19 StartY=63.5 StartZ=0 EndX=-1.5 EndY=63.5 EndZ=0
    g27: LineSegment StartX=-49.19 StartY=60.5 StartZ=0 EndX=-1.5 EndY=60.5 EndZ=0
    g28: LineSegment StartX=-49.19 StartY=57.75 StartZ=0 EndX=-1.5 EndY=57.75 EndZ=0
    g29: LineSegment StartX=-49.19 StartY=54.75 StartZ=0 EndX=-1.5 EndY=54.75 EndZ=0
    g30: LineSegment StartX=-49.19 StartY=52 StartZ=0 EndX=-11.49 EndY=52 EndZ=0
    g31: LineSegment StartX=-49.19 StartY=49 StartZ=0 EndX=-11.49 EndY=49 EndZ=0
    g32: LineSegment StartX=-49.19 StartY=46.25 StartZ=0 EndX=-16.28 EndY=46.25 EndZ=0
    g33: LineSegment StartX=-49.19 StartY=43.25 StartZ=0 EndX=-16.28 EndY=43.25 EndZ=0
    g34: LineSegment StartX=-49.19 StartY=40.5 StartZ=0 EndX=-18.2337 EndY=40.5 EndZ=0
    g35: LineSegment StartX=-49.19 StartY=37.5 StartZ=0 EndX=-18.23 EndY=37.5 EndZ=0
    g36: LineSegment StartX=-49.19 StartY=34.5 StartZ=0 EndX=-18.2337 EndY=34.5 EndZ=0
    g37: LineSegment StartX=-49.19 StartY=31.5 StartZ=0 EndX=-18.23 EndY=31.5 EndZ=0
    g38: LineSegment StartX=-49.19 StartY=28.75 StartZ=0 EndX=-16.2837 EndY=28.75 EndZ=0
    g39: LineSegment StartX=-49.19 StartY=25.75 StartZ=0 EndX=-16.28 EndY=25.75 EndZ=0
    g40: LineSegment StartX=-49.19 StartY=23 StartZ=0 EndX=-11.49 EndY=23 EndZ=0
    g41: LineSegment StartX=-49.19 StartY=20 StartZ=0 EndX=-11.49 EndY=20 EndZ=0
    g42: LineSegment StartX=-49.19 StartY=17.25 StartZ=0 EndX=-1.5 EndY=17.25 EndZ=0
    g43: LineSegment StartX=-49.19 StartY=14.25 StartZ=0 EndX=-1.5 EndY=14.25 EndZ=0
    g44: LineSegment StartX=-49.19 StartY=11.5 StartZ=0 EndX=-1.5 EndY=11.5 EndZ=0
    g45: LineSegment StartX=-49.19 StartY=8.5 StartZ=0 EndX=-1.5 EndY=8.5 EndZ=0
    g46: LineSegment StartX=-49.19 StartY=5.75 StartZ=0 EndX=-1.5 EndY=5.75 EndZ=0
    g47: LineSegment StartX=-49.19 StartY=2.75 StartZ=0 EndX=-1.5 EndY=2.75 EndZ=0
  constraints (120):
    c: Vertical(g0)
    c: Distance(g0) = 3
    c: Block(g0)
    c: Vertical(g1)
    c: Distance(g1) = 3
    c: Vertical(g2)
    c: Equal(g0,g2) = 3
    c: Block(g2)
    c: Vertical(g3)
    c: Equal(g1,g3) = 3
    c: Vertical(g4)
    c: Equal(g0,g4) = 3
    c: Block(g4)
    c: Vertical(g5)
    c: Equal(g1,g5) = 3
    c: Vertical(g6)
    c: Equal(g0,g6) = 3
    c: Block(g6)
    c: Vertical(g7)
    c: Equal(g1,g7) = 3
    c: Vertical(g8)
    c: Equal(g0,g8) = 3
    c: Block(g8)
    c: Vertical(g9)
    c: Equal(g1,g9) = 3
    c: Vertical(g10)
    c: Equal(g0,g10) = 3
    c: Block(g10)
    c: Vertical(g11)
    c: Equal(g1,g11) = 3
    c: Block(g12)
    c: Block(g13)
    c: Block(g14)
    c: Block(g15)
    c: Block(g16)
    c: Block(g17)
    c: Block(g18)
    c: Block(g19)
    c: Block(g20)
    c: Block(g21)
    c: Block(g22)
    c: Block(g23)
    c: Block(g11)
    c: Block(g9)
    c: Block(g7)
    c: Block(g5)
    c: Block(g3)
    c: Block(g1)
    c: Coincident(g24,g0)
    c: Coincident(g24,g12)
    c: Horizontal(g24)
    c: Coincident(g25,g0)
    c: Coincident(g25,g12)
    c: Horizontal(g25)
    c: Coincident(g26,g1)
    c: Coincident(g26,g13)
    c: Horizontal(g26)
    c: Coincident(g27,g1)
    c: Coincident(g27,g13)
    c: Horizontal(g27)
    c: Coincident(g28,g2)
    c: Coincident(g28,g14)
    c: Horizontal(g28)
    c: Coincident(g29,g2)
    c: Coincident(g29,g14)
    c: Horizontal(g29)
    c: Coincident(g30,g3)
    c: Coincident(g30,g15)
    c: Horizontal(g30)
    c: Coincident(g31,g3)
    c: Coincident(g31,g15)
    c: Horizontal(g31)
    c: Coincident(g32,g4)
    c: Coincident(g32,g16)
    c: Horizontal(g32)
    c: Coincident(g33,g4)
    c: Coincident(g33,g16)
    c: Horizontal(g33)
    c: Coincident(g34,g5)
    c: Coincident(g34,g17)
    c: Horizontal(g34)
    c: Coincident(g35,g5)
    c: Coincident(g35,g17)
    c: Horizontal(g35)
    c: Coincident(g36,g6)
    c: Coincident(g36,g19)
    c: Horizontal(g36)
    c: Coincident(g37,g6)
    c: Coincident(g37,g19)
    c: Horizontal(g37)
    c: Coincident(g38,g7)
    c: Coincident(g38,g18)
    c: Horizontal(g38)
    c: Coincident(g39,g7)
    c: Coincident(g39,g18)
    c: Horizontal(g39)
    c: Coincident(g40,g8)
    c: Coincident(g40,g20)
    c: Horizontal(g40)
    c: Coincident(g41,g8)
    c: Coincident(g41,g20)
    c: Horizontal(g41)
    c: Coincident(g42,g9)
    c: Coincident(g42,g23)
    c: Horizontal(g42)
    c: Coincident(g43,g9)
    c: Coincident(g43,g23)
    c: Horizontal(g43)
    c: Coincident(g44,g10)
    c: Coincident(g44,g22)
    c: Horizontal(g44)
    c: Coincident(g45,g10)
    c: Coincident(g45,g22)
    c: Horizontal(g45)
    c: Coincident(g46,g11)
    c: Coincident(g46,g21)
    c: Horizontal(g46)
    c: Coincident(g47,g11)
    c: Coincident(g47,g21)
    c: Horizontal(g47)
FEATURE [Part::Extrusion] Extrude061
  Base = -> Sketch070
  Dir = (1,0,0)
  DirMode = 2
  FaceMakerClass = Part::FaceMakerBullseye
  LengthFwd = 23
  LengthRev = 0
  Placement = pos=(-19,0,0) rot=(0,0,1;0rad)
  Solid = true
  Symmetric = false
FEATURE [Part::Fillet] Fillet052  label="removeToCreateVentalationHoles002"
  Base = -> Extrude061
  Edges = <same value as first occurrence — deduplicated (x6 in doc)>
  Placement = pos=(7,0.02,0) rot=(0,0,1;0rad)
FEATURE [Part::MultiFuse] Fusion130  label="bottom013"
  Shapes = -> [Cut054,Cut034]
FEATURE [Part::Cut] Cut055
  Base = -> Fusion130
  Tool = -> Fillet052
FEATURE [Part::Cylinder] Cylinder054
  Angle = 360
  AttacherType = Attacher::AttachEngine3D
  Height = 20
  Placement = pos=(0,0,36.15) rot=(0,0,1;0rad)
  Radius = 4
FEATURE [Sketcher::SketchObject] Sketch071  label="bottomSketch002"
  FullyConstrained = true
  sketch-geometry (32):
    g0: LineSegment StartX=3.3 StartY=-6.03275e-07 StartZ=0 EndX=98 EndY=-6.03275e-07 EndZ=0
    g1: ArcOfCircle CenterX=98 CenterY=19 CenterZ=0 NormalX=0 NormalY=0 NormalZ=1 AngleXU=0 Radius=19 StartAngle=4.71239 EndAngle=5.71103
    g2: LineSegment StartX=6.3 StartY=8 StartZ=0 EndX=3.3 EndY=8 EndZ=0
    g3: LineSegment StartX=3.3 StartY=8 StartZ=0 EndX=3.3 EndY=-6.03275e-07 EndZ=0
    g4: ArcOfCircle CenterX=8.3 CenterY=5 CenterZ=0 NormalX=0 NormalY=0 NormalZ=1 AngleXU=0 Radius=2 StartAngle=3.14159 EndAngle=4.71239
    g5: LineSegment StartX=6.3 StartY=8 StartZ=0 EndX=6.3 EndY=5 EndZ=0
    g6: ArcOfCircle CenterX=98 CenterY=19 CenterZ=0 NormalX=0 NormalY=0 NormalZ=1 AngleXU=0 Radius=12.7 StartAngle=4.71239 EndAngle=6.28319
    g7: LineSegment StartX=94.7 StartY=3 StartZ=0 EndX=8.3 EndY=3 EndZ=0
    g8-g12: Circle x5 (B-spline internal-alignment scaffolding for g13; pole/knot coordinates omitted)
    g13: BSplineCurve PolesCount=5 KnotsCount=3 Degree=3 IsPeriodic=0
    g14: GeomPoint X=98 Y=6.3 Z=0
    g15: GeomPoint X=96.3938 Y=4.71946 Z=0
    g16: GeomPoint X=94.7 Y=3 Z=0
    g17-g23: Circle x7 (B-spline internal-alignment scaffolding for g24; pole/knot coordinates omitted)
    g24: BSplineCurve PolesCount=7 KnotsCount=5 Degree=3 IsPeriodic=0
    g25-g29: GeomPoint x5 (B-spline internal-alignment scaffolding for g24; pole/knot coordinates omitted)
    g30: ArcOfCircle CenterX=98 CenterY=19 CenterZ=0 NormalX=0 NormalY=0 NormalZ=1 AngleXU=0 Radius=15.7 StartAngle=5.81226 EndAngle=6.28319
    g31: LineSegment StartX=110.7 StartY=19 StartZ=0 EndX=113.7 EndY=19 EndZ=0
  constraints (41):
    c: Horizontal(g0)
    c: Coincident(g1,g0)
    c: Block(g1)
    c: Horizontal(g2)
    c: Distance(g2) = 3
    c: Coincident(g3,g2)
    c: Vertical(g3)
    c: Coincident(g3,g0)
    c: Block(g4)
    c: Block(g2)
    c: Coincident(g5,g2)
    c: Coincident(g5,g4)
    c: Vertical(g5)
    c: Coincident(g6,g1)
    c: Block(g6)
    c: Coincident(g7,g4)
    c: Horizontal(g7)
    c: Block(g0)
    c: Block(g7)
    c: Block(g3)
    c: Coincident(g13,g6)
    c: Weight(g8) = 1
    c: Equal(g8, g9-g12) x4
    c: Coincident(g13,g7)
    c: InternalAlignment(g8-g12 -> g13) x5
    c: InternalAlignment(g14,g13)
    c: InternalAlignment(g15,g13)
    c: InternalAlignment(g16,g13)
    c: Block(g13)
    c: Weight(g17) = 1
    c: Equal(g17, g18-g23) x6
    c: Coincident(g24,g1)
    c: InternalAlignment(g17-g23 -> g24) x7
    c: InternalAlignment(g25-g29 -> g24) x5
    c: Block(g24)
    c: Coincident(g30,g24)
    c: Coincident(g31,g6)
    c: Coincident(g31,g30)
    c: Horizontal(g31)
    c: Block(g31)
    c: Block(g30)
FEATURE [Part::Extrusion] Extrude062  label="bottom014"
  Base = -> Sketch071
  Dir = (0,0,1)
  DirMode = 2
  FaceMakerClass = Part::FaceMakerBullseye
  LengthFwd = 71.4
  LengthRev = 0
  Placement = pos=(0,0,0.3) rot=(0,0,1;0rad)
  Solid = true
  Symmetric = false
FEATURE [Part::Fillet] Fillet054
  Base = -> Extrude062
  Edges = 1 edges r=2.4: [Edge17]
FEATURE [Part::Fillet] Fillet055  label="bottom015"
  Base = -> Fillet054
  Edges = 1 edges r=2.4: [Edge36]
FEATURE [Part::Cylinder] Cylinder055
  Angle = 360
  AttacherType = Attacher::AttachEngine3D
  Height = 10
  Placement = pos=(0,0,36.15) rot=(0,0,1;0rad)
  Radius = 4
FEATURE [Part::MultiFuse] Fusion131  label="removeToCreateHoleForPlugHousing002"
  Placement = pos=(70,19,36.15) rot=(0,1,0;1.5708rad)
  Shapes = -> [Cylinder054,Cylinder055]
FEATURE [Part::Cut] Cut056  label="Bottom001"
  Base = -> Fillet055
  Placement = pos=(9,0,0) rot=(0,0,1;0rad)
  Tool = -> Fusion131
FEATURE [Part::Cut] Cut057
  Base = -> Cut055
  Tool = -> Cut056
FEATURE [Sketcher::SketchObject] Sketch072  label="topSketch021"
  FullyConstrained = true
  sketch-geometry (4):
    g0: ArcOfCircle CenterX=105 CenterY=19 CenterZ=0 NormalX=0 NormalY=0 NormalZ=1 AngleXU=0 Radius=20.6155 StartAngle=5.54125 EndAngle=6.28319
    g1: ArcOfCircle CenterX=105 CenterY=19 CenterZ=0 NormalX=0 NormalY=0 NormalZ=1 AngleXU=0 Radius=13 StartAngle=5.54125 EndAngle=6.28319
    g2: LineSegment StartX=118 StartY=19 StartZ=0 EndX=125.616 EndY=19 EndZ=0
    g3: LineSegment StartX=114.583 StartY=10.2157 StartZ=0 EndX=120.197 EndY=5.06982 EndZ=0
  constraints (7):
    c: Block(g0)
    c: Block(g1)
    c: Coincident(g2,g1)
    c: Coincident(g2,g0)
    c: Horizontal(g2)
    c: Coincident(g3,g1)
    c: Coincident(g3,g0)
FEATURE [Part::Extrusion] Extrude063  label="bottomPlugHousingBit003"
  Base = -> Sketch072
  Dir = (0,0,1)
  DirMode = 2
  FaceMakerClass = Part::FaceMakerBullseye
  LengthFwd = 72
  LengthRev = 0
  Solid = true
  Symmetric = false
FEATURE [Part::Cylinder] Cylinder056
  Angle = 360
  AttacherType = Attacher::AttachEngine3D
  Height = 20
  Placement = pos=(0,0,36.15) rot=(0,0,1;0rad)
  Radius = 14.3
FEATURE [Part::Cylinder] Cylinder057
  Angle = 360
  AttacherType = Attacher::AttachEngine3D
  Height = 10
  Placement = pos=(0,0,36.15) rot=(0,0,1;0rad)
  Radius = 4
FEATURE [Part::Box] Box034  label="removeToCreteHoleForPlugHousing047"
  AttacherType = Attacher::AttachEngine3D
  Height = 28.6
  Length = 20
  Placement = pos=(106.15,0,21.7) rot=(0,0,1;0rad)
  Width = 19
FEATURE [Part::Cylinder] Cylinder058
  Angle = 360
  AttacherType = Attacher::AttachEngine3D
  Height = 20
  Placement = pos=(0,0,36.15) rot=(0,0,1;0rad)
  Radius = 14.3
FEATURE [Part::Cylinder] Cylinder059
  Angle = 360
  AttacherType = Attacher::AttachEngine3D
  Height = 10
  Placement = pos=(0,0,36.15) rot=(0,0,1;0rad)
  Radius = 4
FEATURE [Part::MultiFuse] Fusion134  label="removeToCreteHoleForPlugHousing046"
  Placement = pos=(70,19,36) rot=(0,1,0;1.5708rad)
  Shapes = -> [Cylinder058,Cylinder059]
FEATURE [Part::Cylinder] Cylinder060
  Angle = 360
  AttacherType = Attacher::AttachEngine3D
  Height = 20
  Placement = pos=(0,0,36.15) rot=(0,0,1;0rad)
  Radius = 14
FEATURE [Part::Cylinder] Cylinder061
  Angle = 360
  AttacherType = Attacher::AttachEngine3D
  Height = 10
  Placement = pos=(0,0,36.15) rot=(0,0,1;0rad)
  Radius = 4
FEATURE [Part::MultiFuse] Fusion135  label="removeToCreteHoleForPlugHousing048"
  Placement = pos=(70,19,36) rot=(0,1,0;1.5708rad)
  Shapes = -> [Cylinder060,Cylinder061]
FEATURE [Part::Box] Box035  label="removeToCreteHoleForPlugHousing049"
  AttacherType = Attacher::AttachEngine3D
  Height = 28.6
  Length = 20
  Placement = pos=(106.15,0,21.7) rot=(0,0,1;0rad)
  Width = 19
FEATURE [Part::MultiFuse] Fusion133  label="removeToCreteHoleForPlugHousing045"
  Placement = pos=(0,0,-28.3) rot=(0,0,1;0rad)
  Shapes = -> [Box035,Fusion134]
FEATURE [Part::MultiFuse] Fusion138  label="removeToCreteHoleForPlugHousing051"
  Placement = pos=(70,19,36) rot=(0,1,0;1.5708rad)
  Shapes = -> [Cylinder056,Cylinder057]
FEATURE [Part::MultiFuse] Fusion137  label="removeToCreteHoleForPlugHousing050"
  Placement = pos=(0,0,28.3) rot=(0,0,1;0rad)
  Shapes = -> [Box034,Fusion138]
FEATURE [Part::MultiFuse] Fusion132  label="removeToCreatePlugHousingBottomBit002"
  Shapes = -> [Fusion133,Fusion137]
FEATURE [Part::MultiFuse] Fusion136  label="removeToCreatePlugHousingBottomBit003"
  Shapes = -> [Fusion135,Fusion132]
FEATURE [Part::Cut] Cut058  label="bottomPlugHousingBit002"
  Base = -> Extrude063
  Placement = pos=(-0.09,0,0) rot=(0,0,1;0rad)
  Tool = -> Fusion136
FEATURE [Sketcher::SketchObject] Sketch073  label="bottomSketch003"
  FullyConstrained = true
  sketch-geometry (45):
    g0: LineSegment StartX=6.29999 StartY=8 StartZ=0 EndX=3.29999 EndY=8 EndZ=0
    g1: LineSegment StartX=3.29999 StartY=8 StartZ=0 EndX=3.29999 EndY=-6.03275e-07 EndZ=0
    g2: ArcOfCircle CenterX=8.29999 CenterY=5 CenterZ=0 NormalX=0 NormalY=0 NormalZ=1 AngleXU=0 Radius=2 StartAngle=3.14159 EndAngle=4.71239
    g3: LineSegment StartX=6.29999 StartY=8 StartZ=0 EndX=6.29999 EndY=5 EndZ=0
    g4: ArcOfCircle CenterX=105 CenterY=19 CenterZ=0 NormalX=0 NormalY=0 NormalZ=1 AngleXU=0 Radius=12.7 StartAngle=4.71239 EndAngle=5.94289
    g5-g11: Circle x7 (B-spline internal-alignment scaffolding for g12; pole/knot coordinates omitted)
    g12: BSplineCurve PolesCount=7 KnotsCount=5 Degree=3 IsPeriodic=0
    g13-g17: GeomPoint x5 (B-spline internal-alignment scaffolding for g12; pole/knot coordinates omitted)
    g18: ArcOfCircle CenterX=105 CenterY=19 CenterZ=0 NormalX=0 NormalY=0 NormalZ=1 AngleXU=0 Radius=15.7 StartAngle=5.81226 EndAngle=6.28319
    g19: BSplineCurve PolesCount=5 KnotsCount=3 Degree=3 IsPeriodic=0
    g20: LineSegment StartX=8.29999 StartY=3 StartZ=0 EndX=101.7 EndY=3 EndZ=0
    g21: LineSegment StartX=3.29999 StartY=-6.03275e-07 StartZ=0 EndX=105 EndY=-6.03275e-07 EndZ=0
    g22: LineSegment StartX=120.974 StartY=8.71251 StartZ=0 EndX=122.332 EndY=7.83778 EndZ=0
    g23: LineSegment StartX=105 StartY=-6.03274e-07 StartZ=0 EndX=113 EndY=-6.03274e-07 EndZ=0
    g24: ArcOfCircle CenterX=105 CenterY=19 CenterZ=0 NormalX=0 NormalY=0 NormalZ=1 AngleXU=0 Radius=20.6155 StartAngle=5.11091 EndAngle=5.71103
    g25: ArcOfCircle CenterX=117.7 CenterY=19 CenterZ=0 NormalX=0 NormalY=0 NormalZ=1 AngleXU=0 Radius=3 StartAngle=1.2e-15 EndAngle=2.10468
    g26: Circle CenterX=116.345 CenterY=16.3232 CenterZ=0 NormalX=0 NormalY=0 NormalZ=1 AngleXU=0 Radius=1
    g27: Circle CenterX=117.24 CenterY=15.7584 CenterZ=0 NormalX=0 NormalY=0 NormalZ=1 AngleXU=0 Radius=1
    g28: Circle CenterX=116.972 CenterY=14.7612 CenterZ=0 NormalX=0 NormalY=0 NormalZ=1 AngleXU=0 Radius=1
    g29: BSplineCurve PolesCount=3 KnotsCount=2 Degree=2 IsPeriodic=0
    g30: GeomPoint X=116.345 Y=16.3232 Z=0
    g31: GeomPoint X=116.972 Y=14.7612 Z=0
    g32: Circle CenterX=115.828 CenterY=17.157 CenterZ=0 NormalX=0 NormalY=0 NormalZ=1 AngleXU=0 Radius=1
    g33: Circle CenterX=115.841 CenterY=16.639 CenterZ=0 NormalX=0 NormalY=0 NormalZ=1 AngleXU=0 Radius=1
    g34: Circle CenterX=116.345 CenterY=16.3232 CenterZ=0 NormalX=0 NormalY=0 NormalZ=1 AngleXU=0 Radius=1
    g35: BSplineCurve PolesCount=3 KnotsCount=2 Degree=2 IsPeriodic=0
    g36: GeomPoint X=115.828 Y=17.157 Z=0
    g37: GeomPoint X=116.345 Y=16.3232 Z=0
    g38: LineSegment StartX=115.828 StartY=17.157 StartZ=0 EndX=115.828 EndY=20.8307 EndZ=0
    g39: Circle CenterX=115.828 CenterY=20.8307 CenterZ=0 NormalX=0 NormalY=0 NormalZ=1 AngleXU=0 Radius=1
    g40: Circle CenterX=115.831 CenterY=21.3396 CenterZ=0 NormalX=0 NormalY=0 NormalZ=1 AngleXU=0 Radius=1
    g41: Circle CenterX=116.173 CenterY=21.5825 CenterZ=0 NormalX=0 NormalY=0 NormalZ=1 AngleXU=0 Radius=1
    g42: BSplineCurve PolesCount=3 KnotsCount=2 Degree=2 IsPeriodic=0
    g43: GeomPoint X=115.828 Y=20.8307 Z=0
    g44: GeomPoint X=116.173 Y=21.5825 Z=0
  constraints (70):
    c: Horizontal(g0)
    c: Distance(g0) = 3
    c: Coincident(g1,g0)
    c: Vertical(g1)
    c: Block(g2)
    c: Block(g0)
    c: Coincident(g3,g0)
    c: Coincident(g3,g2)
    c: Vertical(g3)
    c: Block(g1)
    c: Block(g4)
    c: Coincident(g19,g4)
    c: Block(g19)
    c: Equal(g5, g6-g11) x6
    c: InternalAlignment(g5-g11 -> g12) x7
    c: InternalAlignment(g13-g17 -> g12) x5
    c: Block(g12)
    c: Coincident(g18,g12)
    c: Block(g18)
    c: Coincident(g20,g2)
    c: Coincident(g20,g19)
    c: Horizontal(g20)
    c: Distance(g20) = 93.4
    c: Coincident(g21,g1)
    c: Horizontal(g21)
    c: Distance(g21) = 101.7
    c: Horizontal(g23)
    c: Distance(g23) = 8
    c: Coincident(g24,g23)
    c: Block(g23)
    c: Coincident(g22,g24)
    c: Block(g24)
    c: Block(g22)
    c: Distance(g22) = 1.61553
    c: Coincident(g25,g18)
    c: Block(g25)
    c: Weight(g26) = 1
    c: Equal(g26,g27)
    c: Equal(g26,g28)
    c: Coincident(g29,g4)
    c: InternalAlignment(g26,g29)
    c: InternalAlignment(g27,g29)
    c: InternalAlignment(g28,g29)
    c: InternalAlignment(g30,g29)
    c: InternalAlignment(g31,g29)
    c: Block(g29)
    c: Weight(g32) = 1
    c: Equal(g32,g33)
    c: Equal(g32,g34)
    c: Coincident(g35,g29)
    c: InternalAlignment(g32,g35)
    c: InternalAlignment(g33,g35)
    c: InternalAlignment(g34,g35)
    c: InternalAlignment(g36,g35)
    c: InternalAlignment(g37,g35)
    c: Block(g35)
    c: Coincident(g38,g35)
    c: Vertical(g38)
    c: Block(g38)
    c: Coincident(g42,g38)
    c: Weight(g39) = 1
    c: Equal(g39,g40)
    c: Equal(g39,g41)
    c: Coincident(g42,g25)
    c: InternalAlignment(g39,g42)
    c: InternalAlignment(g40,g42)
    c: InternalAlignment(g41,g42)
    c: InternalAlignment(g43,g42)
    c: InternalAlignment(g44,g42)
    c: Block(g42)
FEATURE [Part::Extrusion] Extrude064  label="bottom016"
  Base = -> Sketch073
  Dir = (0,0,1)
  DirMode = 2
  FaceMakerClass = Part::FaceMakerBullseye
  LengthFwd = 71.4
  LengthRev = 0
  Placement = pos=(0,0,0.3) rot=(0,0,1;0rad)
  Solid = true
  Symmetric = false
FEATURE [Part::Revolution] Revolve157  label="removeToCreateScrewAndThreadedInsertHole063"
  Angle = 360
  Axis = (0,1,0)
  Base = (0,0,0)
  FaceMakerClass = Part::FaceMakerBullseye
  Placement = pos=(12.5,0,10) rot=(0,0,1;0rad)
  Solid = false
  Source = -> Face141
  Symmetric = false
FEATURE [Sketcher::SketchObject] Sketch074
  FullyConstrained = true
  Placement = pos=(117,19,0) rot=(0.57735,0.57735,0.57735;2.0944rad)
  sketch-geometry (48):
    g0: LineSegment StartX=-49.19 StartY=69.25 StartZ=0 EndX=-49.19 EndY=66.25 EndZ=0
    g1: LineSegment StartX=-49.19 StartY=63.5 StartZ=0 EndX=-49.19 EndY=60.5 EndZ=0
    g2: LineSegment StartX=-49.19 StartY=57.75 StartZ=0 EndX=-49.19 EndY=54.75 EndZ=0
    g3: LineSegment StartX=-49.19 StartY=52 StartZ=0 EndX=-49.19 EndY=49 EndZ=0
    g4: LineSegment StartX=-49.19 StartY=46.25 StartZ=0 EndX=-49.19 EndY=43.25 EndZ=0
    g5: LineSegment StartX=-49.19 StartY=40.5 StartZ=0 EndX=-49.19 EndY=37.5 EndZ=0
    g6: LineSegment StartX=-49.19 StartY=34.5 StartZ=0 EndX=-49.19 EndY=31.5 EndZ=0
    g7: LineSegment StartX=-49.19 StartY=28.75 StartZ=0 EndX=-49.19 EndY=25.75 EndZ=0
    g8: LineSegment StartX=-49.19 StartY=23 StartZ=0 EndX=-49.19 EndY=20 EndZ=0
    g9: LineSegment StartX=-49.19 StartY=17.25 StartZ=0 EndX=-49.19 EndY=14.25 EndZ=0
    g10: LineSegment StartX=-49.19 StartY=11.5 StartZ=0 EndX=-49.19 EndY=8.5 EndZ=0
    g11: LineSegment StartX=-49.19 StartY=5.75 StartZ=0 EndX=-49.19 EndY=2.75 EndZ=0
    g12: ArcOfCircle CenterX=-1.5 CenterY=67.75 CenterZ=0 NormalX=0 NormalY=0 NormalZ=1 AngleXU=0 Radius=1.5 StartAngle=4.71239 EndAngle=7.85398
    g13: ArcOfCircle CenterX=-1.5 CenterY=62 CenterZ=0 NormalX=0 NormalY=0 NormalZ=1 AngleXU=0 Radius=1.5 StartAngle=4.71239 EndAngle=7.85398
    g14: ArcOfCircle CenterX=-1.5 CenterY=56.25 CenterZ=0 NormalX=0 NormalY=0 NormalZ=1 AngleXU=0 Radius=1.5 StartAngle=4.71239 EndAngle=7.85398
    g15: ArcOfCircle CenterX=-11.49 CenterY=50.5 CenterZ=0 NormalX=0 NormalY=0 NormalZ=1 AngleXU=0 Radius=1.5 StartAngle=4.71239 EndAngle=7.85398
    g16: ArcOfCircle CenterX=-16.28 CenterY=44.75 CenterZ=0 NormalX=0 NormalY=0 NormalZ=1 AngleXU=0 Radius=1.5 StartAngle=4.71239 EndAngle=7.85398
    g17: ArcOfCircle CenterX=-18.2337 CenterY=39 CenterZ=0 NormalX=0 NormalY=0 NormalZ=1 AngleXU=0 Radius=1.5 StartAngle=4.71485 EndAngle=7.85398
    g18: ArcOfCircle CenterX=-16.2837 CenterY=27.25 CenterZ=0 NormalX=0 NormalY=0 NormalZ=1 AngleXU=0 Radius=1.5 StartAngle=4.71485 EndAngle=7.85398
    g19: ArcOfCircle CenterX=-18.2337 CenterY=33 CenterZ=0 NormalX=0 NormalY=0 NormalZ=1 AngleXU=0 Radius=1.5 StartAngle=4.71485 EndAngle=7.85398
    g20: ArcOfCircle CenterX=-11.49 CenterY=21.5 CenterZ=0 NormalX=0 NormalY=0 NormalZ=1 AngleXU=0 Radius=1.5 StartAngle=4.71239 EndAngle=7.85398
    g21: ArcOfCircle CenterX=-1.5 CenterY=4.25 CenterZ=0 NormalX=0 NormalY=0 NormalZ=1 AngleXU=0 Radius=1.5 StartAngle=4.71239 EndAngle=7.85398
    g22: ArcOfCircle CenterX=-1.5 CenterY=10 CenterZ=0 NormalX=0 NormalY=0 NormalZ=1 AngleXU=0 Radius=1.5 StartAngle=4.71239 EndAngle=7.85398
    g23: ArcOfCircle CenterX=-1.5 CenterY=15.75 CenterZ=0 NormalX=0 NormalY=0 NormalZ=1 AngleXU=0 Radius=1.5 StartAngle=4.71239 EndAngle=7.85398
    g24: LineSegment StartX=-49.19 StartY=69.25 StartZ=0 EndX=-1.5 EndY=69.25 EndZ=0
    g25: LineSegment StartX=-49.19 StartY=66.25 StartZ=0 EndX=-1.5 EndY=66.25 EndZ=0
    g26: LineSegment StartX=-49.19 StartY=63.5 StartZ=0 EndX=-1.5 EndY=63.5 EndZ=0
    g27: LineSegment StartX=-49.19 StartY=60.5 StartZ=0 EndX=-1.5 EndY=60.5 EndZ=0
    g28: LineSegment StartX=-49.19 StartY=57.75 StartZ=0 EndX=-1.5 EndY=57.75 EndZ=0
    g29: LineSegment StartX=-49.19 StartY=54.75 StartZ=0 EndX=-1.5 EndY=54.75 EndZ=0
    g30: LineSegment StartX=-49.19 StartY=52 StartZ=0 EndX=-11.49 EndY=52 EndZ=0
    g31: LineSegment StartX=-49.19 StartY=49 StartZ=0 EndX=-11.49 EndY=49 EndZ=0
    g32: LineSegment StartX=-49.19 StartY=46.25 StartZ=0 EndX=-16.28 EndY=46.25 EndZ=0
    g33: LineSegment StartX=-49.19 StartY=43.25 StartZ=0 EndX=-16.28 EndY=43.25 EndZ=0
    g34: LineSegment StartX=-49.19 StartY=40.5 StartZ=0 EndX=-18.2337 EndY=40.5 EndZ=0
    g35: LineSegment StartX=-49.19 StartY=37.5 StartZ=0 EndX=-18.23 EndY=37.5 EndZ=0
    g36: LineSegment StartX=-49.19 StartY=34.5 StartZ=0 EndX=-18.2337 EndY=34.5 EndZ=0
    g37: LineSegment StartX=-49.19 StartY=31.5 StartZ=0 EndX=-18.23 EndY=31.5 EndZ=0
    g38: LineSegment StartX=-49.19 StartY=28.75 StartZ=0 EndX=-16.2837 EndY=28.75 EndZ=0
    g39: LineSegment StartX=-49.19 StartY=25.75 StartZ=0 EndX=-16.28 EndY=25.75 EndZ=0
    g40: LineSegment StartX=-49.19 StartY=23 StartZ=0 EndX=-11.49 EndY=23 EndZ=0
    g41: LineSegment StartX=-49.19 StartY=20 StartZ=0 EndX=-11.49 EndY=20 EndZ=0
    g42: LineSegment StartX=-49.19 StartY=17.25 StartZ=0 EndX=-1.5 EndY=17.25 EndZ=0
    g43: LineSegment StartX=-49.19 StartY=14.25 StartZ=0 EndX=-1.5 EndY=14.25 EndZ=0
    g44: LineSegment StartX=-49.19 StartY=11.5 StartZ=0 EndX=-1.5 EndY=11.5 EndZ=0
    g45: LineSegment StartX=-49.19 StartY=8.5 StartZ=0 EndX=-1.5 EndY=8.5 EndZ=0
    g46: LineSegment StartX=-49.19 StartY=5.75 StartZ=0 EndX=-1.5 EndY=5.75 EndZ=0
    g47: LineSegment StartX=-49.19 StartY=2.75 StartZ=0 EndX=-1.5 EndY=2.75 EndZ=0
  constraints (120):
    c: Vertical(g0)
    c: Distance(g0) = 3
    c: Block(g0)
    c: Vertical(g1)
    c: Distance(g1) = 3
    c: Vertical(g2)
    c: Equal(g0,g2) = 3
    c: Block(g2)
    c: Vertical(g3)
    c: Equal(g1,g3) = 3
    c: Vertical(g4)
    c: Equal(g0,g4) = 3
    c: Block(g4)
    c: Vertical(g5)
    c: Equal(g1,g5) = 3
    c: Vertical(g6)
    c: Equal(g0,g6) = 3
    c: Block(g6)
    c: Vertical(g7)
    c: Equal(g1,g7) = 3
    c: Vertical(g8)
    c: Equal(g0,g8) = 3
    c: Block(g8)
    c: Vertical(g9)
    c: Equal(g1,g9) = 3
    c: Vertical(g10)
    c: Equal(g0,g10) = 3
    c: Block(g10)
    c: Vertical(g11)
    c: Equal(g1,g11) = 3
    c: Block(g12)
    c: Block(g13)
    c: Block(g14)
    c: Block(g15)
    c: Block(g16)
    c: Block(g17)
    c: Block(g18)
    c: Block(g19)
    c: Block(g20)
    c: Block(g21)
    c: Block(g22)
    c: Block(g23)
    c: Block(g11)
    c: Block(g9)
    c: Block(g7)
    c: Block(g5)
    c: Block(g3)
    c: Block(g1)
    c: Coincident(g24,g0)
    c: Coincident(g24,g12)
    c: Horizontal(g24)
    c: Coincident(g25,g0)
    c: Coincident(g25,g12)
    c: Horizontal(g25)
    c: Coincident(g26,g1)
    c: Coincident(g26,g13)
    c: Horizontal(g26)
    c: Coincident(g27,g1)
    c: Coincident(g27,g13)
    c: Horizontal(g27)
    c: Coincident(g28,g2)
    c: Coincident(g28,g14)
    c: Horizontal(g28)
    c: Coincident(g29,g2)
    c: Coincident(g29,g14)
    c: Horizontal(g29)
    c: Coincident(g30,g3)
    c: Coincident(g30,g15)
    c: Horizontal(g30)
    c: Coincident(g31,g3)
    c: Coincident(g31,g15)
    c: Horizontal(g31)
    c: Coincident(g32,g4)
    c: Coincident(g32,g16)
    c: Horizontal(g32)
    c: Coincident(g33,g4)
    c: Coincident(g33,g16)
    c: Horizontal(g33)
    c: Coincident(g34,g5)
    c: Coincident(g34,g17)
    c: Horizontal(g34)
    c: Coincident(g35,g5)
    c: Coincident(g35,g17)
    c: Horizontal(g35)
    c: Coincident(g36,g6)
    c: Coincident(g36,g19)
    c: Horizontal(g36)
    c: Coincident(g37,g6)
    c: Coincident(g37,g19)
    c: Horizontal(g37)
    c: Coincident(g38,g7)
    c: Coincident(g38,g18)
    c: Horizontal(g38)
    c: Coincident(g39,g7)
    c: Coincident(g39,g18)
    c: Horizontal(g39)
    c: Coincident(g40,g8)
    c: Coincident(g40,g20)
    c: Horizontal(g40)
    c: Coincident(g41,g8)
    c: Coincident(g41,g20)
    c: Horizontal(g41)
    c: Coincident(g42,g9)
    c: Coincident(g42,g23)
    c: Horizontal(g42)
    c: Coincident(g43,g9)
    c: Coincident(g43,g23)
    c: Horizontal(g43)
    c: Coincident(g44,g10)
    c: Coincident(g44,g22)
    c: Horizontal(g44)
    c: Coincident(g45,g10)
    c: Coincident(g45,g22)
    c: Horizontal(g45)
    c: Coincident(g46,g11)
    c: Coincident(g46,g21)
    c: Horizontal(g46)
    c: Coincident(g47,g11)
    c: Coincident(g47,g21)
    c: Horizontal(g47)
FEATURE [Part::Extrusion] Extrude065
  Base = -> Sketch074
  Dir = (1,0,0)
  DirMode = 2
  FaceMakerClass = Part::FaceMakerBullseye
  LengthFwd = 23
  LengthRev = 0
  Placement = pos=(-19,0,0) rot=(0,0,1;0rad)
  Solid = true
  Symmetric = false
FEATURE [Part::Fillet] Fillet056  label="removeToCreateVentalationHoles003"
  Base = -> Extrude065
  Edges = <same value as first occurrence — deduplicated (x6 in doc)>
  Placement = pos=(7,0.02,0) rot=(0,0,1;0rad)
FEATURE [Part::Revolution] Revolve158  label="removeToCreateScrewAndThreadedInsertHole065"
  Angle = 360
  Axis = (0,1,0)
  Base = (0,0,0)
  FaceMakerClass = Part::FaceMakerBullseye
  Placement = pos=(12.5,0,62) rot=(0,0,1;0rad)
  Solid = false
  Source = -> Face146
  Symmetric = false
FEATURE [Part::Revolution] Revolve159  label="removeToCreateScrewAndThreadedInsertHole066"
  Angle = 360
  Axis = (0,1,0)
  Base = (0,0,0)
  FaceMakerClass = Part::FaceMakerBullseye
  Placement = pos=(89.5,0,68.5) rot=(0,0,1;0rad)
  Solid = false
  Source = -> Face143
  Symmetric = false
FEATURE [Part::Revolution] Revolve160  label="removeToCreateScrewAndThreadedInsertHole067"
  Angle = 360
  Axis = (0,1,0)
  Base = (0,0,0)
  FaceMakerClass = Part::FaceMakerBullseye
  Placement = pos=(89.5,0,3.5) rot=(0,0,1;0rad)
  Solid = false
  Source = -> Face142
  Symmetric = false
FEATURE [Part::Revolution] Revolve161  label="removeToCreateScrewAndThreadedInsertHole068"
  Angle = 360
  Axis = (0,1,0)
  Base = (0,0,0)
  FaceMakerClass = Part::FaceMakerBullseye
  Placement = pos=(109.5,4.7,3.5) rot=(0,0,1;0rad)
  Solid = false
  Source = -> Face145
  Symmetric = false
FEATURE [Part::Revolution] Revolve162  label="removeToCreateScrewAndThreadedInsertHole069"
  Angle = 360
  Axis = (0,1,0)
  Base = (0,0,0)
  FaceMakerClass = Part::FaceMakerBullseye
  Placement = pos=(109.5,4.7,68.5) rot=(0,0,1;0rad)
  Solid = false
  Source = -> Face144
  Symmetric = false
FEATURE [Part::MultiFuse] Fusion141  label="removeToCreateScrewAndThreadedInsertHole064"
  Shapes = -> [Revolve162,Revolve161,Revolve160,Revolve159,Revolve158,Revolve157]
FEATURE [Part::Cylinder] Cylinder062
  Angle = 360
  AttacherType = Attacher::AttachEngine3D
  Height = 20
  Placement = pos=(0,0,36.15) rot=(0,0,1;0rad)
  Radius = 14
FEATURE [Part::Cylinder] Cylinder063
  Angle = 360
  AttacherType = Attacher::AttachEngine3D
  Height = 10
  Placement = pos=(0,0,36.15) rot=(0,0,1;0rad)
  Radius = 4
FEATURE [Part::MultiFuse] Fusion139  label="removeToCreteHoleForPlugHousing052"
  Placement = pos=(70,19,36) rot=(0,1,0;1.5708rad)
  Shapes = -> [Cylinder062,Cylinder063]
FEATURE [Part::Cut] Cut060  label="bottom017"
  Base = -> Extrude064
  Tool = -> Fusion139
FEATURE [Part::Cut] Cut061  label="bottom019"
  Base = -> Cut060
  Tool = -> Fusion141
FEATURE [Part::MultiFuse] Fusion140  label="bottom018"
  Shapes = -> [Cut061,Cut058]
FEATURE [Part::Cut] Cut059  label="bottom020"
  Base = -> Fusion140
  Tool = -> Fillet056
FEATURE [Part::Box] Box036  label="Cube021"
  AttacherType = Attacher::AttachEngine3D
  Height = 80
  Length = 26
  Placement = pos=(0,-1,-5) rot=(0,0,1;0rad)
  Width = 11
FEATURE [Part::Cut] Cut062  label="removeFromBottom002"
  Base = -> Cut057
  Tool = -> Box036
FEATURE [Part::Cut] Cut063
  Base = -> Cut059
  Tool = -> Cut062
FEATURE [Part::Cut] Cut064  label="pcbStands"
  Base = -> Fusion095
  Tool = -> Fusion127
FEATURE [Sketcher::SketchObject] Sketch075  label="topSketch022"
  FullyConstrained = true
  sketch-geometry (6):
    g0: LineSegment StartX=19 StartY=38 StartZ=0 EndX=117 EndY=38 EndZ=0
    g1: ArcOfCircle CenterX=19 CenterY=19 CenterZ=0 NormalX=0 NormalY=0 NormalZ=1 AngleXU=0 Radius=19 StartAngle=1.5708 EndAngle=3.14159
    g2: LineSegment StartX=117 StartY=38 StartZ=0 EndX=117 EndY=19 EndZ=0
    g3: LineSegment StartX=98 StartY=1.0161e-12 StartZ=0 EndX=5.22862e-06 EndY=1.0161e-12 EndZ=0
    g4: LineSegment StartX=5.22862e-06 StartY=19 StartZ=0 EndX=5.22862e-06 EndY=1.0161e-12 EndZ=0
    g5: ArcOfCircle CenterX=98 CenterY=19 CenterZ=0 NormalX=0 NormalY=0 NormalZ=1 AngleXU=0 Radius=19 StartAngle=4.71239 EndAngle=6.28319
  constraints (16):
    c: Horizontal(g0)
    c: Distance(g0) = 98
    c: Coincident(g1,g0)
    c: Block(g1)
    c: Coincident(g2,g0)
    c: Vertical(g2)
    c: Distance(g2) = 19
    c: Horizontal(g3)
    c: Coincident(g4,g1)
    c: Vertical(g4)
    c: Coincident(g3,g4)
    c: Block(g3)
    c: Coincident(g5,g2)
    c: Coincident(g5,g3)
    c: Block(g0)
    c: Block(g5)
FEATURE [Part::Extrusion] Extrude067  label="sideB003"
  Base = -> Sketch075
  Dir = (0,0,1)
  DirMode = 2
  FaceMakerClass = Part::FaceMakerBullseye
  LengthFwd = 3
  LengthRev = 0
  Placement = pos=(0,0,71.7) rot=(0,0,1;0rad)
  Solid = true
  Symmetric = false
FEATURE [Sketcher::SketchObject] Sketch076  label="topSketch023"
  FullyConstrained = true
  sketch-geometry (6):
    g0: LineSegment StartX=19 StartY=38 StartZ=0 EndX=117 EndY=38 EndZ=0
    g1: ArcOfCircle CenterX=19 CenterY=19 CenterZ=0 NormalX=0 NormalY=0 NormalZ=1 AngleXU=0 Radius=19 StartAngle=1.5708 EndAngle=3.14159
    g2: LineSegment StartX=117 StartY=38 StartZ=0 EndX=117 EndY=19 EndZ=0
    g3: LineSegment StartX=98 StartY=1.0161e-12 StartZ=0 EndX=5.22862e-06 EndY=1.0161e-12 EndZ=0
    g4: LineSegment StartX=5.22862e-06 StartY=19 StartZ=0 EndX=5.22862e-06 EndY=1.0161e-12 EndZ=0
    g5: ArcOfCircle CenterX=98 CenterY=19 CenterZ=0 NormalX=0 NormalY=0 NormalZ=1 AngleXU=0 Radius=19 StartAngle=4.71239 EndAngle=6.28319
  constraints (16):
    c: Horizontal(g0)
    c: Distance(g0) = 98
    c: Coincident(g1,g0)
    c: Block(g1)
    c: Coincident(g2,g0)
    c: Vertical(g2)
    c: Distance(g2) = 19
    c: Horizontal(g3)
    c: Coincident(g4,g1)
    c: Vertical(g4)
    c: Coincident(g3,g4)
    c: Block(g3)
    c: Coincident(g5,g2)
    c: Coincident(g5,g3)
    c: Block(g0)
    c: Block(g5)
FEATURE [Part::Extrusion] Extrude066  label="sideA003"
  Base = -> Sketch076
  Dir = (0,0,1)
  DirMode = 2
  FaceMakerClass = Part::FaceMakerBullseye
  LengthFwd = 3
  LengthRev = 0
  Placement = pos=(0,0,-2.7) rot=(0,0,1;0rad)
  Solid = true
  Symmetric = false
FEATURE [Part::MultiFuse] Fusion142  label="removeFromBottom003"
  Placement = pos=(2,0,0) rot=(0,0,1;0rad)
  Shapes = -> [Extrude066,Extrude067]
FEATURE [Part::Cut] Cut065  label="screwRetainers002"
  Base = -> Fusion096
  Tool = -> Fusion142
FEATURE [Sketcher::SketchObject] Sketch077
  FullyConstrained = true
  Placement = pos=(117,19,0) rot=(0.57735,0.57735,0.57735;2.0944rad)
  sketch-geometry (8):
    g0: LineSegment StartX=-49.19 StartY=63.5 StartZ=0 EndX=-49.19 EndY=60.5 EndZ=0
    g1: LineSegment StartX=-49.19 StartY=11.5 StartZ=0 EndX=-49.19 EndY=8.5 EndZ=0
    g2: ArcOfCircle CenterX=-1.5 CenterY=62 CenterZ=0 NormalX=0 NormalY=0 NormalZ=1 AngleXU=0 Radius=1.5 StartAngle=4.71239 EndAngle=7.85398
    g3: ArcOfCircle CenterX=-1.5 CenterY=10 CenterZ=0 NormalX=0 NormalY=0 NormalZ=1 AngleXU=0 Radius=1.5 StartAngle=4.71239 EndAngle=7.85398
    g4: LineSegment StartX=-49.19 StartY=63.5 StartZ=0 EndX=-1.5 EndY=63.5 EndZ=0
    g5: LineSegment StartX=-49.19 StartY=60.5 StartZ=0 EndX=-1.5 EndY=60.5 EndZ=0
    g6: LineSegment StartX=-49.19 StartY=11.5 StartZ=0 EndX=-1.5 EndY=11.5 EndZ=0
    g7: LineSegment StartX=-49.19 StartY=8.5 StartZ=0 EndX=-1.5 EndY=8.5 EndZ=0
  constraints (19):
    c: Vertical(g0)
    c: Distance(g0) = 3
    c: Vertical(g1)
    c: Block(g1)
    c: Block(g2)
    c: Block(g3)
    c: Block(g0)
    c: Coincident(g4,g0)
    c: Coincident(g4,g2)
    c: Horizontal(g4)
    c: Coincident(g5,g0)
    c: Coincident(g5,g2)
    c: Horizontal(g5)
    c: Coincident(g6,g1)
    c: Coincident(g6,g3)
    c: Horizontal(g6)
    c: Coincident(g7,g1)
    c: Coincident(g7,g3)
    c: Horizontal(g7)
FEATURE [Part::Extrusion] Extrude068
  Base = -> Sketch077
  Dir = (1,0,0)
  DirMode = 2
  FaceMakerClass = Part::FaceMakerBullseye
  LengthFwd = 10
  LengthRev = 0
  Solid = true
  Symmetric = false
FEATURE [Part::Fillet] Fillet057  label="removeFromtMoreFrontCaseScrewRetainers002"
  Base = -> Extrude068
  Edges = 4 edges r=1.49: [Edge6,Edge11,Edge18,Edge23]
  Placement = pos=(-12,0,0) rot=(0,0,1;0rad)
FEATURE [Sketcher::SketchObject] Sketch078
  FullyConstrained = true
  Placement = pos=(117,19,0) rot=(0.57735,0.57735,0.57735;2.0944rad)
  sketch-geometry (8):
    g0: LineSegment StartX=-49.19 StartY=69.25 StartZ=0 EndX=-49.19 EndY=66.25 EndZ=0
    g1: LineSegment StartX=-49.19 StartY=5.75 StartZ=0 EndX=-49.19 EndY=2.75 EndZ=0
    g2: ArcOfCircle CenterX=-1.5 CenterY=67.75 CenterZ=0 NormalX=0 NormalY=0 NormalZ=1 AngleXU=0 Radius=1.5 StartAngle=4.71239 EndAngle=7.85398
    g3: ArcOfCircle CenterX=-1.5 CenterY=4.25 CenterZ=0 NormalX=0 NormalY=0 NormalZ=1 AngleXU=0 Radius=1.5 StartAngle=4.71239 EndAngle=7.85398
    g4: LineSegment StartX=-49.19 StartY=69.25 StartZ=0 EndX=-1.5 EndY=69.25 EndZ=0
    g5: LineSegment StartX=-49.19 StartY=66.25 StartZ=0 EndX=-1.5 EndY=66.25 EndZ=0
    g6: LineSegment StartX=-49.19 StartY=5.75 StartZ=0 EndX=-1.5 EndY=5.75 EndZ=0
    g7: LineSegment StartX=-49.19 StartY=2.75 StartZ=0 EndX=-1.5 EndY=2.75 EndZ=0
  constraints (19):
    c: Vertical(g0)
    c: Distance(g0) = 3
    c: Block(g0)
    c: Vertical(g1)
    c: Block(g2)
    c: Block(g3)
    c: Block(g1)
    c: Coincident(g4,g0)
    c: Coincident(g4,g2)
    c: Horizontal(g4)
    c: Coincident(g5,g0)
    c: Coincident(g5,g2)
    c: Horizontal(g5)
    c: Coincident(g6,g1)
    c: Coincident(g6,g3)
    c: Horizontal(g6)
    c: Coincident(g7,g1)
    c: Coincident(g7,g3)
    c: Horizontal(g7)
FEATURE [Part::Extrusion] Extrude069
  Base = -> Sketch078
  Dir = (1,0,0)
  DirMode = 2
  FaceMakerClass = Part::FaceMakerBullseye
  LengthFwd = 10
  LengthRev = 0
  Solid = true
  Symmetric = false
FEATURE [Part::Fillet] Fillet058  label="removeFromtMoreFrontCaseScrewRetainers003"
  Base = -> Extrude069
  Edges = 4 edges r=1.49: [Edge6,Edge11,Edge18,Edge23]
  Placement = pos=(-4,0,0) rot=(0,0,1;0rad)
FEATURE [Part::Cut] Cut066
  Base = -> Cut065
  Tool = -> Fillet058
FEATURE [Part::Cut] Cut067  label="screwPillars"
  Base = -> Cut066
  Tool = -> Fillet057
FEATURE [Part::MultiFuse] Fusion143  label="bottom021"
  Shapes = -> [Cut031,Cut063]
FEATURE [Part::Cylinder] Cylinder
  Angle = 360
  AttacherType = Attacher::AttachEngine3D
  Height = 10
  Placement = pos=(20.65,12,4.68) rot=(1,0,0;1.5708rad)
  Radius = 2
FEATURE [Part::Cylinder] Cylinder064
  Angle = 360
  AttacherType = Attacher::AttachEngine3D
  Height = 10
  Placement = pos=(20.65,12,67.38) rot=(1,0,0;1.5708rad)
  Radius = 2
FEATURE [Part::Cylinder] Cylinder065
  Angle = 360
  AttacherType = Attacher::AttachEngine3D
  Height = 10
  Placement = pos=(77.15,12,67.38) rot=(1,0,0;1.5708rad)
  Radius = 2
FEATURE [Part::Cylinder] Cylinder066
  Angle = 360
  AttacherType = Attacher::AttachEngine3D
  Height = 10
  Placement = pos=(77.15,12,4.68) rot=(1,0,0;1.5708rad)
  Radius = 2
FEATURE [Part::MultiFuse] Fusion144  label="removeFromThreadedInsertHousing"
  Shapes = -> [Cylinder065,Cylinder064,Cylinder,Cylinder066]
FEATURE [Part::Cut] Cut068  label="pcbStands001"
  Base = -> Cut064
  Tool = -> Fusion144
FEATURE [Part::MultiFuse] Fusion145
  Shapes = -> [Cut068,Fusion143]
FEATURE [Part::MultiFuse] Fusion146
  Shapes = -> [Fusion145]
FEATURE [Part::MultiFuse] Fusion147  label="bottom022"
  Shapes = -> [Cut067,Fusion146]
FEATURE [Part::MultiFuse] Fusion148  label="casePillars005"
  Shapes = -> [Cut047,Fusion092]
FEATURE [Part::MultiFuse] Fusion149  label="bottom023"
  Shapes = -> [Fusion124,Fusion113,Fusion147]
FEATURE [Part::MultiFuse] Fusion150  label="topBits"
  Shapes = -> [Cut025,Fusion148,Cut030,Fillet034]
FEATURE [Part::Feature] Face149 .. Face152  x4 (patterned run collapsed; names and placements below)
  shape: bbox 3.2 x 1.5 x 2e-07 mm, 1 faces, 0 solids (baked)
FEATURE [Part::Feature] Face153
  shape: bbox 3.6 x 3.2 x 2e-07 mm, 1 faces, 0 solids (baked)
FEATURE [Part::Feature] Face154
  shape: bbox 3.6 x 3.2 x 2e-07 mm, 1 faces, 0 solids (baked)
FEATURE [Sketcher::SketchObject] Sketch079  label="topSketch024"
  FullyConstrained = true
  sketch-geometry (6):
    g0: LineSegment StartX=19 StartY=38 StartZ=0 EndX=117 EndY=38 EndZ=0
    g1: ArcOfCircle CenterX=19 CenterY=19 CenterZ=0 NormalX=0 NormalY=0 NormalZ=1 AngleXU=0 Radius=19 StartAngle=1.5708 EndAngle=3.14159
    g2: LineSegment StartX=117 StartY=38 StartZ=0 EndX=117 EndY=19 EndZ=0
    g3: LineSegment StartX=98 StartY=1.0161e-12 StartZ=0 EndX=5.22862e-06 EndY=1.0161e-12 EndZ=0
    g4: LineSegment StartX=5.22862e-06 StartY=19 StartZ=0 EndX=5.22862e-06 EndY=1.0161e-12 EndZ=0
    g5: ArcOfCircle CenterX=98 CenterY=19 CenterZ=0 NormalX=0 NormalY=0 NormalZ=1 AngleXU=0 Radius=19 StartAngle=4.71239 EndAngle=6.28319
  constraints (16):
    c: Horizontal(g0)
    c: Distance(g0) = 98
    c: Coincident(g1,g0)
    c: Block(g1)
    c: Coincident(g2,g0)
    c: Vertical(g2)
    c: Distance(g2) = 19
    c: Horizontal(g3)
    c: Coincident(g4,g1)
    c: Vertical(g4)
    c: Coincident(g3,g4)
    c: Block(g3)
    c: Coincident(g5,g2)
    c: Coincident(g5,g3)
    c: Block(g0)
    c: Block(g5)
FEATURE [Sketcher::SketchObject] Sketch080  label="topSketch025"
  FullyConstrained = true
  sketch-geometry (6):
    g0: LineSegment StartX=19 StartY=38 StartZ=0 EndX=117 EndY=38 EndZ=0
    g1: ArcOfCircle CenterX=19 CenterY=19 CenterZ=0 NormalX=0 NormalY=0 NormalZ=1 AngleXU=0 Radius=19 StartAngle=1.5708 EndAngle=3.14159
    g2: LineSegment StartX=117 StartY=38 StartZ=0 EndX=117 EndY=19 EndZ=0
    g3: LineSegment StartX=98 StartY=1.0161e-12 StartZ=0 EndX=5.22862e-06 EndY=1.0161e-12 EndZ=0
    g4: LineSegment StartX=5.22862e-06 StartY=19 StartZ=0 EndX=5.22862e-06 EndY=1.0161e-12 EndZ=0
    g5: ArcOfCircle CenterX=98 CenterY=19 CenterZ=0 NormalX=0 NormalY=0 NormalZ=1 AngleXU=0 Radius=19 StartAngle=4.71239 EndAngle=6.28319
  constraints (16):
    c: Horizontal(g0)
    c: Distance(g0) = 98
    c: Coincident(g1,g0)
    c: Block(g1)
    c: Coincident(g2,g0)
    c: Vertical(g2)
    c: Distance(g2) = 19
    c: Horizontal(g3)
    c: Coincident(g4,g1)
    c: Vertical(g4)
    c: Coincident(g3,g4)
    c: Block(g3)
    c: Coincident(g5,g2)
    c: Coincident(g5,g3)
    c: Block(g0)
    c: Block(g5)
FEATURE [Part::Extrusion] Extrude070  label="sideA004"
  Base = -> Sketch080
  Dir = (0,0,1)
  DirMode = 2
  FaceMakerClass = Part::FaceMakerBullseye
  LengthFwd = 3
  LengthRev = 0
  Placement = pos=(0,0,-2.7) rot=(0,0,1;0rad)
  Solid = true
  Symmetric = false
FEATURE [Sketcher::SketchObject] Sketch081
  FullyConstrained = true
  Placement = pos=(117,19,0) rot=(0.57735,0.57735,0.57735;2.0944rad)
  sketch-geometry (8):
    g0: LineSegment StartX=-49.19 StartY=63.5 StartZ=0 EndX=-49.19 EndY=60.5 EndZ=0
    g1: LineSegment StartX=-49.19 StartY=11.5 StartZ=0 EndX=-49.19 EndY=8.5 EndZ=0
    g2: ArcOfCircle CenterX=-1.5 CenterY=62 CenterZ=0 NormalX=0 NormalY=0 NormalZ=1 AngleXU=0 Radius=1.5 StartAngle=4.71239 EndAngle=7.85398
    g3: ArcOfCircle CenterX=-1.5 CenterY=10 CenterZ=0 NormalX=0 NormalY=0 NormalZ=1 AngleXU=0 Radius=1.5 StartAngle=4.71239 EndAngle=7.85398
    g4: LineSegment StartX=-49.19 StartY=63.5 StartZ=0 EndX=-1.5 EndY=63.5 EndZ=0
    g5: LineSegment StartX=-49.19 StartY=60.5 StartZ=0 EndX=-1.5 EndY=60.5 EndZ=0
    g6: LineSegment StartX=-49.19 StartY=11.5 StartZ=0 EndX=-1.5 EndY=11.5 EndZ=0
    g7: LineSegment StartX=-49.19 StartY=8.5 StartZ=0 EndX=-1.5 EndY=8.5 EndZ=0
  constraints (19):
    c: Vertical(g0)
    c: Distance(g0) = 3
    c: Vertical(g1)
    c: Block(g1)
    c: Block(g2)
    c: Block(g3)
    c: Block(g0)
    c: Coincident(g4,g0)
    c: Coincident(g4,g2)
    c: Horizontal(g4)
    c: Coincident(g5,g0)
    c: Coincident(g5,g2)
    c: Horizontal(g5)
    c: Coincident(g6,g1)
    c: Coincident(g6,g3)
    c: Horizontal(g6)
    c: Coincident(g7,g1)
    c: Coincident(g7,g3)
    c: Horizontal(g7)
FEATURE [Part::Extrusion] Extrude071  label="sideB004"
  Base = -> Sketch079
  Dir = (0,0,1)
  DirMode = 2
  FaceMakerClass = Part::FaceMakerBullseye
  LengthFwd = 3
  LengthRev = 0
  Placement = pos=(0,0,71.7) rot=(0,0,1;0rad)
  Solid = true
  Symmetric = false
FEATURE [Part::MultiFuse] Fusion152  label="removeFromBottom004"
  Placement = pos=(2,0,0) rot=(0,0,1;0rad)
  Shapes = -> [Extrude070,Extrude071]
FEATURE [Part::Extrusion] Extrude072
  Base = -> Sketch081
  Dir = (1,0,0)
  DirMode = 2
  FaceMakerClass = Part::FaceMakerBullseye
  LengthFwd = 10
  LengthRev = 0
  Solid = true
  Symmetric = false
FEATURE [Part::Fillet] Fillet059  label="removeFromtMoreFrontCaseScrewRetainers004"
  Base = -> Extrude072
  Edges = 4 edges r=1.49: [Edge6,Edge11,Edge18,Edge23]
  Placement = pos=(-12,0,0) rot=(0,0,1;0rad)
FEATURE [Sketcher::SketchObject] Sketch082
  FullyConstrained = true
  Placement = pos=(117,19,0) rot=(0.57735,0.57735,0.57735;2.0944rad)
  sketch-geometry (8):
    g0: LineSegment StartX=-49.19 StartY=69.25 StartZ=0 EndX=-49.19 EndY=66.25 EndZ=0
    g1: LineSegment StartX=-49.19 StartY=5.75 StartZ=0 EndX=-49.19 EndY=2.75 EndZ=0
    g2: ArcOfCircle CenterX=-1.5 CenterY=67.75 CenterZ=0 NormalX=0 NormalY=0 NormalZ=1 AngleXU=0 Radius=1.5 StartAngle=4.71239 EndAngle=7.85398
    g3: ArcOfCircle CenterX=-1.5 CenterY=4.25 CenterZ=0 NormalX=0 NormalY=0 NormalZ=1 AngleXU=0 Radius=1.5 StartAngle=4.71239 EndAngle=7.85398
    g4: LineSegment StartX=-49.19 StartY=69.25 StartZ=0 EndX=-1.5 EndY=69.25 EndZ=0
    g5: LineSegment StartX=-49.19 StartY=66.25 StartZ=0 EndX=-1.5 EndY=66.25 EndZ=0
    g6: LineSegment StartX=-49.19 StartY=5.75 StartZ=0 EndX=-1.5 EndY=5.75 EndZ=0
    g7: LineSegment StartX=-49.19 StartY=2.75 StartZ=0 EndX=-1.5 EndY=2.75 EndZ=0
  constraints (19):
    c: Vertical(g0)
    c: Distance(g0) = 3
    c: Block(g0)
    c: Vertical(g1)
    c: Block(g2)
    c: Block(g3)
    c: Block(g1)
    c: Coincident(g4,g0)
    c: Coincident(g4,g2)
    c: Horizontal(g4)
    c: Coincident(g5,g0)
    c: Coincident(g5,g2)
    c: Horizontal(g5)
    c: Coincident(g6,g1)
    c: Coincident(g6,g3)
    c: Horizontal(g6)
    c: Coincident(g7,g1)
    c: Coincident(g7,g3)
    c: Horizontal(g7)
FEATURE [Part::Extrusion] Extrude073
  Base = -> Sketch082
  Dir = (1,0,0)
  DirMode = 2
  FaceMakerClass = Part::FaceMakerBullseye
  LengthFwd = 10
  LengthRev = 0
  Solid = true
  Symmetric = false
FEATURE [Part::Fillet] Fillet060  label="removeFromtMoreFrontCaseScrewRetainers005"
  Base = -> Extrude073
  Edges = 4 edges r=1.49: [Edge6,Edge11,Edge18,Edge23]
  Placement = pos=(-4,0,0) rot=(0,0,1;0rad)
FEATURE [Part::Revolution] Revolve163  label="backCaseScrewRetainer004"
  Angle = 360
  Axis = (0,1,0)
  Base = (0,0,0)
  FaceMakerClass = Part::FaceMakerBullseye
  Placement = pos=(12.5,3,62) rot=(0,0,1;0rad)
  Solid = false
  Source = -> Face149
  Symmetric = false
FEATURE [Part::Revolution] Revolve164  label="frontCaseScrewRetainer006"
  Angle = 360
  Axis = (0,1,0)
  Base = (0,0,0)
  FaceMakerClass = Part::FaceMakerBullseye
  Placement = pos=(89.5,3,68.5) rot=(0,0,1;0rad)
  Solid = false
  Source = -> Face151
  Symmetric = false
FEATURE [Part::Revolution] Revolve165  label="frontCaseScrewRetainer007"
  Angle = 360
  Axis = (0,1,0)
  Base = (0,0,0)
  FaceMakerClass = Part::FaceMakerBullseye
  Placement = pos=(89.5,3,3.5) rot=(0,0,1;0rad)
  Solid = false
  Source = -> Face152
  Symmetric = false
FEATURE [Part::Revolution] Revolve166  label="backCaseScrewRetainer005"
  Angle = 360
  Axis = (0,1,0)
  Base = (0,0,0)
  FaceMakerClass = Part::FaceMakerBullseye
  Placement = pos=(12.5,3,10) rot=(0,0,1;0rad)
  Solid = false
  Source = -> Face150
  Symmetric = false
FEATURE [Part::Revolution] Revolve167  label="moreFrontCaseScrewRetainer006"
  Angle = 360
  Axis = (0,1,0)
  Base = (0,0,0)
  FaceMakerClass = Part::FaceMakerBullseye
  Placement = pos=(109.5,4.5,68.5) rot=(0,0,1;0rad)
  Solid = false
  Source = -> Face153
  Symmetric = false
FEATURE [Part::Revolution] Revolve168  label="moreFrontCaseScrewRetainer007"
  Angle = 360
  Axis = (0,1,0)
  Base = (0,0,0)
  FaceMakerClass = Part::FaceMakerBullseye
  Placement = pos=(109.5,4.5,3.5) rot=(0,0,1;0rad)
  Solid = false
  Source = -> Face154
  Symmetric = false
FEATURE [Part::MultiFuse] Fusion151  label="screwRetainers003"
  Shapes = -> [Revolve168,Revolve167,Revolve166,Revolve165,Revolve164,Revolve163]
FEATURE [Part::Cut] Cut069  label="screwRetainers004"
  Base = -> Fusion151
  Tool = -> Fusion152
FEATURE [Part::Cut] Cut070
  Base = -> Cut069
  Tool = -> Fillet060
FEATURE [Part::Cut] Cut071  label="screwPillars001"
  Base = -> Cut070
  Tool = -> Fillet059
FEATURE [Part::MultiFuse] Fusion153  label="bottom024"
  Shapes = -> [Fusion149,Cut071]
FEATURE [Part::Cylinder] Cylinder067
  Angle = 360
  AttacherType = Attacher::AttachEngine3D
  Height = 10
  Placement = pos=(20.65,12,4.68) rot=(1,0,0;1.5708rad)
  Radius = 2
FEATURE [Part::Cylinder] Cylinder068
  Angle = 360
  AttacherType = Attacher::AttachEngine3D
  Height = 10
  Placement = pos=(20.65,12,67.38) rot=(1,0,0;1.5708rad)
  Radius = 2
FEATURE [Part::Cylinder] Cylinder069
  Angle = 360
  AttacherType = Attacher::AttachEngine3D
  Height = 10
  Placement = pos=(77.15,12,67.38) rot=(1,0,0;1.5708rad)
  Radius = 2
FEATURE [Part::Cylinder] Cylinder070
  Angle = 360
  AttacherType = Attacher::AttachEngine3D
  Height = 10
  Placement = pos=(77.15,12,4.68) rot=(1,0,0;1.5708rad)
  Radius = 2
FEATURE [Part::MultiFuse] Fusion154  label="removeFromThreadedInsertHousing001"
  Shapes = -> [Cylinder069,Cylinder068,Cylinder067,Cylinder070]
FEATURE [Part::Cut] Cut072  label="bottom025"
  Base = -> Fusion153
  Tool = -> Fusion154
FEATURE [Image::ImagePlane] ImagePlane
  XSize = 339
  YSize = 72
FEATURE [Sketcher::SketchObject] Sketch083
  FullyConstrained = true
  MapMode = 5
  Support = -> [XY_Plane]
  sketch-geometry (338):
    g0: LineSegment StartX=-151.619 StartY=28.8932 StartZ=0 EndX=-140.819 EndY=28.8932 EndZ=0
    g1: LineSegment StartX=-151.619 StartY=24.0313 StartZ=0 EndX=-151.619 EndY=28.8932 EndZ=0
    g2: LineSegment StartX=-140.819 StartY=17.7713 StartZ=0 EndX=-151.619 EndY=17.7713 EndZ=0
    g3: LineSegment StartX=-151.619 StartY=17.7713 StartZ=0 EndX=-151.619 EndY=22.6313 EndZ=0
    g4: LineSegment StartX=-151.619 StartY=22.6313 StartZ=0 EndX=-145.128 EndY=22.6313 EndZ=0
    g5: LineSegment StartX=-145.128 StartY=24.0313 StartZ=0 EndX=-140.819 EndY=28.8932 EndZ=0
    g6: LineSegment StartX=-145.128 StartY=22.6313 StartZ=0 EndX=-140.819 EndY=17.7713 EndZ=0
    g7: ArcOfCircle CenterX=-155.157 CenterY=23.3323 CenterZ=0 NormalX=0 NormalY=0 NormalZ=1 AngleXU=0 Radius=6.92354 StartAngle=1.03434 EndAngle=5.24885
    g8: ArcOfCircle CenterX=-155.157 CenterY=23.3323 CenterZ=0 NormalX=0 NormalY=0 NormalZ=1 AngleXU=0 Radius=12.6269 StartAngle=1.28675 EndAngle=4.99643
    g9: LineSegment StartX=-151.619 StartY=35.4532 StartZ=0 EndX=-151.619 EndY=29.2832 EndZ=0
    g10: LineSegment StartX=-151.619 StartY=17.3813 StartZ=0 EndX=-151.619 EndY=11.2113 EndZ=0
    g11-g21: Circle x11 (B-spline internal-alignment scaffolding for g22; pole/knot coordinates omitted)
    g22: BSplineCurve PolesCount=11 KnotsCount=9 Degree=3 IsPeriodic=0
    g23-g31: GeomPoint x9 (B-spline internal-alignment scaffolding for g22; pole/knot coordinates omitted)
    g32-g49: Circle x18 (B-spline internal-alignment scaffolding for g50; pole/knot coordinates omitted)
    g50: BSplineCurve PolesCount=18 KnotsCount=16 Degree=3 IsPeriodic=0
    g51-g66: GeomPoint x16 (B-spline internal-alignment scaffolding for g50; pole/knot coordinates omitted)
    g67: LineSegment StartX=-117.124 StartY=30.093 StartZ=0 EndX=-117.603 EndY=26.5272 EndZ=0
    g68: LineSegment StartX=-117.603 StartY=17.8472 StartZ=0 EndX=-117.124 EndY=14.2659 EndZ=0
    g69: Ellipse CenterX=-109.671 CenterY=20.025 CenterZ=0 NormalX=0 NormalY=0 NormalZ=1 MajorRadius=3.34798 MinorRadius=2.71052 AngleXU=-1.56793
    g70: GeomPoint X=-109.666 Y=18.0598 Z=0
    g71: GeomPoint X=-109.677 Y=21.9902 Z=0
    g72: Ellipse CenterX=-109.671 CenterY=20.0123 CenterZ=0 NormalX=0 NormalY=0 NormalZ=1 MajorRadius=6.93002 MinorRadius=6.36273 AngleXU=-3.13976
    g73: GeomPoint X=-112.417 Y=20.0073 Z=0
    g74: GeomPoint X=-106.925 Y=20.0173 Z=0
    g75: Ellipse CenterX=-51.7682 CenterY=20.1463 CenterZ=0 NormalX=0 NormalY=0 NormalZ=1 MajorRadius=3.19279 MinorRadius=2.71052 AngleXU=-1.52774
    g76: GeomPoint X=-51.6955 Y=18.4606 Z=0
    g77: GeomPoint X=-51.8408 Y=21.832 Z=0
    g78: GeomPoint X=-54.5142 Y=20.1413 Z=0
    g79: GeomPoint X=-49.0221 Y=20.1513 Z=0
    g80: Ellipse CenterX=-51.7682 CenterY=20.1463 CenterZ=0 NormalX=0 NormalY=0 NormalZ=1 MajorRadius=6.93002 MinorRadius=6.36273 AngleXU=-3.13976
    g81: Ellipse CenterX=-22.8436 CenterY=20.1783 CenterZ=0 NormalX=0 NormalY=0 NormalZ=1 MajorRadius=3.31512 MinorRadius=2.71052 AngleXU=-1.60214
    g82: GeomPoint X=-22.9034 Y=18.2706 Z=0
    g83: GeomPoint X=-22.7838 Y=22.0861 Z=0
    g84: GeomPoint X=-25.5897 Y=20.1733 Z=0
    g85: GeomPoint X=-20.0976 Y=20.1833 Z=0
    g86: Ellipse CenterX=-22.8436 CenterY=20.1783 CenterZ=0 NormalX=0 NormalY=0 NormalZ=1 MajorRadius=6.93002 MinorRadius=6.36273 AngleXU=-3.13976
    g87: LineSegment StartX=-101.889 StartY=14.1107 StartZ=0 EndX=-97.7455 EndY=14.1107 EndZ=0
    g88: LineSegment StartX=-93.8155 StartY=14.1107 StartZ=0 EndX=-89.6755 EndY=14.1107 EndZ=0
    g89: LineSegment StartX=-85.7455 StartY=14.1107 StartZ=0 EndX=-81.6055 EndY=14.1107 EndZ=0
    g90: LineSegment StartX=-101.889 StartY=14.1107 StartZ=0 EndX=-101.889 EndY=25.9907 EndZ=0
    g91: LineSegment StartX=-101.889 StartY=25.9907 StartZ=0 EndX=-97.8594 EndY=25.9907 EndZ=0
    g92: LineSegment StartX=-97.8594 StartY=25.9907 StartZ=0 EndX=-97.8594 EndY=24.0907 EndZ=0
    g93: LineSegment StartX=-97.7455 StartY=14.1107 StartZ=0 EndX=-97.7455 EndY=19.9107 EndZ=0
    g94: LineSegment StartX=-89.6755 StartY=14.1107 StartZ=0 EndX=-89.6755 EndY=19.9107 EndZ=0
    g95: LineSegment StartX=-93.8155 StartY=14.1107 StartZ=0 EndX=-93.8155 EndY=21.0107 EndZ=0
    g96-g106: Circle x11 (B-spline internal-alignment scaffolding for g107; pole/knot coordinates omitted)
    g107: BSplineCurve PolesCount=11 KnotsCount=9 Degree=3 IsPeriodic=0
    g108-g116: GeomPoint x9 (B-spline internal-alignment scaffolding for g107; pole/knot coordinates omitted)
    g117: BSplineCurve PolesCount=11 KnotsCount=9 Degree=3 IsPeriodic=0
    g118-g125: Circle x8 (B-spline internal-alignment scaffolding for g126; pole/knot coordinates omitted)
    g126: BSplineCurve PolesCount=8 KnotsCount=6 Degree=3 IsPeriodic=0
    g127-g132: GeomPoint x6 (B-spline internal-alignment scaffolding for g126; pole/knot coordinates omitted)
    g133: BSplineCurve PolesCount=8 KnotsCount=6 Degree=3 IsPeriodic=0
    g134: LineSegment StartX=-85.7455 StartY=21.0107 StartZ=0 EndX=-85.7455 EndY=14.1107 EndZ=0
    g135: LineSegment StartX=-80.0879 StartY=14.1107 StartZ=0 EndX=-75.944 EndY=14.1107 EndZ=0
    g136: LineSegment StartX=-72.014 StartY=14.1107 StartZ=0 EndX=-67.874 EndY=14.1107 EndZ=0
    g137: LineSegment StartX=-63.944 StartY=14.1107 StartZ=0 EndX=-59.804 EndY=14.1107 EndZ=0
    g138: LineSegment StartX=-80.0879 StartY=14.1107 StartZ=0 EndX=-80.0879 EndY=25.9907 EndZ=0
    g139: LineSegment StartX=-80.0879 StartY=25.9907 StartZ=0 EndX=-76.0579 EndY=25.9907 EndZ=0
    g140: LineSegment StartX=-76.0579 StartY=25.9907 StartZ=0 EndX=-76.0579 EndY=24.0907 EndZ=0
    g141: LineSegment StartX=-75.944 StartY=14.1107 StartZ=0 EndX=-75.944 EndY=19.9107 EndZ=0
    g142: LineSegment StartX=-67.874 StartY=14.1107 StartZ=0 EndX=-67.874 EndY=19.9107 EndZ=0
    g143: LineSegment StartX=-72.014 StartY=14.1107 StartZ=0 EndX=-72.014 EndY=21.0107 EndZ=0
    g144-g148: Circle x5 (B-spline internal-alignment scaffolding for g149; pole/knot coordinates omitted)
    g149: BSplineCurve PolesCount=11 KnotsCount=9 Degree=3 IsPeriodic=0
    g150-g158: GeomPoint x9 (B-spline internal-alignment scaffolding for g149; pole/knot coordinates omitted)
    g159: BSplineCurve PolesCount=11 KnotsCount=9 Degree=3 IsPeriodic=0
    g160-g167: Circle x8 (B-spline internal-alignment scaffolding for g168; pole/knot coordinates omitted)
    g168: BSplineCurve PolesCount=8 KnotsCount=6 Degree=3 IsPeriodic=0
    g169-g174: GeomPoint x6 (B-spline internal-alignment scaffolding for g168; pole/knot coordinates omitted)
    g175: BSplineCurve PolesCount=8 KnotsCount=6 Degree=3 IsPeriodic=0
    g176: LineSegment StartX=-63.944 StartY=21.0107 StartZ=0 EndX=-63.944 EndY=14.1107 EndZ=0
    g177: LineSegment StartX=-59.804 StartY=14.1107 StartZ=0 EndX=-59.804 EndY=21.5868 EndZ=0
    g178: BSplineCurve PolesCount=4 KnotsCount=2 Degree=3 IsPeriodic=0
    g179: GeomPoint X=-59.804 Y=21.5868 Z=0
    g180: GeomPoint X=-60.2379 Y=24.0907 Z=0
    g181: LineSegment StartX=-81.6055 StartY=14.1107 StartZ=0 EndX=-81.6055 EndY=21.5868 EndZ=0
    g182: LineSegment StartX=-151.619 StartY=24.0313 StartZ=0 EndX=-145.128 EndY=24.0313 EndZ=0
    g183: Circle CenterX=-82.0394 CenterY=24.0907 CenterZ=0 NormalX=0 NormalY=0 NormalZ=1 AngleXU=0 Radius=1
    g184: Circle CenterX=-81.7131 CenterY=23.2736 CenterZ=0 NormalX=0 NormalY=0 NormalZ=1 AngleXU=0 Radius=1
    g185: Circle CenterX=-81.6055 CenterY=21.5868 CenterZ=0 NormalX=0 NormalY=0 NormalZ=1 AngleXU=0 Radius=1
    g186: BSplineCurve PolesCount=3 KnotsCount=2 Degree=2 IsPeriodic=0
    g187: GeomPoint X=-82.0394 Y=24.0907 Z=0
    g188: GeomPoint X=-81.6055 Y=21.5868 Z=0
    g189: Ellipse CenterX=-37.3522 CenterY=19.9515 CenterZ=0 NormalX=0 NormalY=0 NormalZ=1 MajorRadius=2.99755 MinorRadius=2.49 AngleXU=1.5708
    g190: GeomPoint X=-37.3522 Y=21.6203 Z=0
    g191: GeomPoint X=-37.3522 Y=18.2826 Z=0
    g192: ArcOfEllipse CenterX=-38.7647 CenterY=20.06 CenterZ=0 NormalX=0 NormalY=0 NormalZ=1 MajorRadius=6.30025 MinorRadius=5.3849 AngleXU=1.57276 StartAngle=5.50632 EndAngle=10.3035
    g193: GeomPoint X=-38.7711 Y=23.3304 Z=0
    g194: GeomPoint X=-38.7583 Y=16.7895 Z=0
    g195: LineSegment StartX=-34.6109 StartY=14.1107 StartZ=0 EndX=-30.8984 EndY=14.1107 EndZ=0
    g196: LineSegment StartX=-30.8984 StartY=14.1107 StartZ=0 EndX=-30.8984 EndY=31.1784 EndZ=0
    g197: LineSegment StartX=-30.8984 StartY=31.1784 StartZ=0 EndX=-34.9984 EndY=31.1784 EndZ=0
    g198: LineSegment StartX=-34.9984 StartY=24.5602 StartZ=0 EndX=-34.9984 EndY=31.1784 EndZ=0
    g199: LineSegment StartX=-34.6109 StartY=16.0476 StartZ=0 EndX=-34.6109 EndY=14.1107 EndZ=0
    g200: LineSegment StartX=-14.8781 StartY=14.1107 StartZ=0 EndX=-10.5106 EndY=14.1107 EndZ=0
    g201: LineSegment StartX=-14.8781 StartY=14.1107 StartZ=0 EndX=-14.8781 EndY=25.8504 EndZ=0
    g202: LineSegment StartX=-14.8781 StartY=25.8504 StartZ=0 EndX=-10.8534 EndY=25.8504 EndZ=0
    g203: LineSegment StartX=-10.8534 StartY=25.8504 StartZ=0 EndX=-10.8534 EndY=24.0923 EndZ=0
    g204: LineSegment StartX=-10.5106 StartY=14.1107 StartZ=0 EndX=-10.5106 EndY=19.7752 EndZ=0
    g205: LineSegment StartX=-5.96397 StartY=25.9304 StartZ=0 EndX=-5.96397 EndY=22.574 EndZ=0
    g206-g214: Circle x9 (B-spline internal-alignment scaffolding for g215; pole/knot coordinates omitted)
    g215: BSplineCurve PolesCount=9 KnotsCount=7 Degree=3 IsPeriodic=0
    g216-g222: GeomPoint x7 (B-spline internal-alignment scaffolding for g215; pole/knot coordinates omitted)
    g223-g232: Circle x10 (B-spline internal-alignment scaffolding for g233; pole/knot coordinates omitted)
    g233: BSplineCurve PolesCount=10 KnotsCount=8 Degree=3 IsPeriodic=0
    g234-g241: GeomPoint x8 (B-spline internal-alignment scaffolding for g233; pole/knot coordinates omitted)
    g242: LineSegment StartX=-1.58923 StartY=21.0696 StartZ=0 EndX=2.62034 EndY=21.0696 EndZ=0
    g243: LineSegment StartX=-1.55856 StartY=18.7342 StartZ=0 EndX=6.45946 EndY=18.7342 EndZ=0
    g244: LineSegment StartX=5.29231 StartY=17.386 StartZ=0 EndX=5.29231 EndY=14.3674 EndZ=0
    g245-g269: Circle x25 (B-spline internal-alignment scaffolding for g270; pole/knot coordinates omitted)
    g270: BSplineCurve PolesCount=25 KnotsCount=23 Degree=3 IsPeriodic=0
    g271-g293: GeomPoint x23 (B-spline internal-alignment scaffolding for g270; pole/knot coordinates omitted)
    g294-g304: Circle x11 (B-spline internal-alignment scaffolding for g305; pole/knot coordinates omitted)
    g305: BSplineCurve PolesCount=11 KnotsCount=9 Degree=3 IsPeriodic=0
    g306-g314: GeomPoint x9 (B-spline internal-alignment scaffolding for g305; pole/knot coordinates omitted)
    g315-g326: Circle x12 (B-spline internal-alignment scaffolding for g327; pole/knot coordinates omitted)
    g327: BSplineCurve PolesCount=12 KnotsCount=10 Degree=3 IsPeriodic=0
    g328-g337: GeomPoint x10 (B-spline internal-alignment scaffolding for g327; pole/knot coordinates omitted)
  constraints (252):
    c: Coincident(g1,g0)
    c: Horizontal(g0)
    c: Vertical(g1)
    c: Coincident(g2,g3)
    c: Coincident(g3,g4)
    c: Horizontal(g4)
    c: Horizontal(g2)
    c: Vertical(g3)
    c: Block(g1)
    c: Distance(g3) = 4.86
    c: Block(g4)
    c: Distance(g0) = 10.8
    c: Distance(g2) = 10.8
    c: Coincident(g5,g0)
    c: Coincident(g6,g4)
    c: Coincident(g6,g2)
    c: Block(g8)
    c: Block(g7)
    c: Coincident(g9,g8)
    c: Coincident(g9,g7)
    c: Vertical(g9)
    c: Coincident(g10,g7)
    c: Coincident(g10,g8)
    c: Vertical(g10)
    c: Weight(g11) = 1
    c: Equal(g11, g12-g21) x10
    c: InternalAlignment(g11-g21 -> g22) x11
    c: InternalAlignment(g23-g31 -> g22) x9
    c: Block(g22)
    c: Weight(g32) = 1
    c: Equal(g32, g33-g49) x17
    c: InternalAlignment(g32-g49 -> g50) x18
    c: InternalAlignment(g51-g66 -> g50) x16
    c: Block(g50)
    c: Coincident(g67,g50)
    c: Coincident(g67,g22)
    c: Coincident(g68,g22)
    c: Coincident(g68,g50)
    c: InternalAlignment(g70,g69)
    c: InternalAlignment(g71,g69)
    c: Block(g69)
    c: InternalAlignment(g73,g72)
    c: InternalAlignment(g74,g72)
    c: Block(g72)
    c: InternalAlignment(g76,g75)
    c: InternalAlignment(g77,g75)
    c: InternalAlignment(g78,g80)
    c: InternalAlignment(g79,g80)
    c: Block(g80)
    c: Coincident(g75,g80)
    c: Block(g75)
    c: InternalAlignment(g82,g81)
    c: InternalAlignment(g83,g81)
    c: InternalAlignment(g84,g86)
    c: InternalAlignment(g85,g86)
    c: Block(g86)
    c: Coincident(g81,g86)
    c: Block(g81)
    c: Horizontal(g87)
    c: Block(g87)
    c: Horizontal(g88)
    c: Distance(g88) = 4.14
    c: Horizontal(g89)
    c: Equal(g88,g89) = 4.14
    c: Block(g89)
    c: Block(g88)
    c: Coincident(g90,g87)
    c: Vertical(g90)
    c: Distance(g90) = 11.88
    c: Coincident(g91,g90)
    c: Horizontal(g91)
    c: Coincident(g92,g91)
    c: Vertical(g92)
    c: Distance(g91) = 4.03
    c: Distance(g92) = 1.9
    c: Coincident(g93,g87)
    c: Vertical(g93)
    c: Vertical(g94)
    c: Coincident(g94,g88)
    c: Distance(g93) = 5.8
    c: Distance(g94) = 5.8
    c: Vertical(g95)
    c: Coincident(g95,g88)
    c: Distance(g95) = 6.9
    c: Coincident(g107,g92)
    c: Weight(g96) = 1
    c: Equal(g96, g97-g106) x10
    c: InternalAlignment(g96-g106 -> g107) x11
    c: InternalAlignment(g108-g116 -> g107) x9
    c: Block(g107)
    c: Block(g117)
    c: Coincident(g126,g93)
    c: Weight(g118) = 1
    c: Equal(g118, g119-g125) x7
    c: Coincident(g126,g95)
    c: InternalAlignment(g118-g125 -> g126) x8
    c: InternalAlignment(g127-g132 -> g126) x6
    c: Coincident(g133,g94)
    c: Block(g126)
    c: Block(g133)
    c: Coincident(g134,g133)
    c: Coincident(g134,g89)
    c: Vertical(g134)
    c: Horizontal(g135)
    c: Block(g135)
    c: Horizontal(g136)
    c: Equal(g88,g136) = 4.14
    c: Horizontal(g137)
    c: Equal(g136,g137) = 4.14
    c: Block(g137)
    c: Block(g136)
    c: Coincident(g138,g135)
    c: Vertical(g138)
    c: Equal(g90,g138) = 11.88
    c: Coincident(g139,g138)
    c: Horizontal(g139)
    c: Coincident(g140,g139)
    c: Vertical(g140)
    c: Equal(g91,g139) = 4.03
    c: Equal(g92,g140) = 1.9
    c: Coincident(g141,g135)
    c: Vertical(g141)
    c: Vertical(g142)
    c: Coincident(g142,g136)
    c: Equal(g93,g141) = 5.8
    c: Equal(g94,g142) = 5.8
    c: Vertical(g143)
    c: Coincident(g143,g136)
    c: Equal(g95,g143) = 6.9
    c: Coincident(g149,g140)
    c: Equal(g96,g144) = 1
    c: Equal(g144, g145-g148) x4
    c: InternalAlignment(g144-g148 -> g149) x5
    c: InternalAlignment(g150-g158 -> g149) x9
    c: Block(g149)
    c: Block(g159)
    c: Coincident(g168,g141)
    c: Equal(g118,g160) = 1
    c: Equal(g160, g161-g167) x7
    c: Coincident(g168,g143)
    c: InternalAlignment(g160-g167 -> g168) x8
    c: InternalAlignment(g169-g174 -> g168) x6
    c: Coincident(g175,g142)
    c: Block(g168)
    c: Block(g175)
    c: Coincident(g176,g175)
    c: Coincident(g176,g137)
    c: Vertical(g176)
    c: Coincident(g177,g137)
    c: Vertical(g177)
    c: Coincident(g178,g177)
    c: Coincident(g178,g159)
    c: InternalAlignment(g179,g178)
    c: InternalAlignment(g180,g178)
    c: Block(g178)
    c: Vertical(g181)
    c: Coincident(g181,g89)
    c: Block(g5)
    c: Coincident(g182,g1)
    c: Coincident(g182,g5)
    c: Horizontal(g182)
    c: Coincident(g186,g117)
    c: Weight(g183) = 1
    c: Equal(g183,g184)
    c: Equal(g183,g185)
    c: Coincident(g186,g181)
    c: InternalAlignment(g183,g186)
    c: InternalAlignment(g184,g186)
    c: InternalAlignment(g185,g186)
    c: InternalAlignment(g187,g186)
    c: InternalAlignment(g188,g186)
    c: Block(g186)
    c: InternalAlignment(g190,g189)
    c: InternalAlignment(g191,g189)
    c: Block(g189)
    c: InternalAlignment(g193,g192)
    c: InternalAlignment(g194,g192)
    c: Block(g192)
    c: Horizontal(g195)
    c: Block(g195)
    c: Coincident(g196,g195)
    c: Vertical(g196)
    c: Block(g196)
    c: Distance(g195) = 3.71244
    c: Coincident(g197,g196)
    c: Horizontal(g197)
    c: Distance(g197) = 4.1
    c: Coincident(g198,g192)
    c: Coincident(g198,g197)
    c: Vertical(g198)
    c: Block(g198)
    c: Coincident(g199,g192)
    c: Coincident(g199,g195)
    c: Vertical(g199)
    c: Block(g199)
    c: Horizontal(g200)
    c: Block(g200)
    c: Coincident(g201,g200)
    c: Vertical(g201)
    c: Block(g201)
    c: Coincident(g202,g201)
    c: Horizontal(g202)
    c: Block(g202)
    c: Coincident(g203,g202)
    c: Vertical(g203)
    c: Block(g203)
    c: Coincident(g204,g200)
    c: Vertical(g204)
    c: Block(g204)
    c: Coincident(g215,g203)
    c: Weight(g206) = 1
    c: Equal(g206, g207-g214) x8
    c: Coincident(g215,g205)
    c: InternalAlignment(g206-g214 -> g215) x9
    c: InternalAlignment(g216-g222 -> g215) x7
    c: Coincident(g233,g204)
    c: Weight(g223) = 1
    c: Equal(g223, g224-g232) x9
    c: Coincident(g233,g205)
    c: InternalAlignment(g223-g232 -> g233) x10
    c: InternalAlignment(g234-g241 -> g233) x8
    c: Vertical(g205)
    c: Block(g205)
    c: Block(g215)
    c: Block(g233)
    c: Horizontal(g242)
    c: Horizontal(g243)
    c: Block(g242)
    c: Block(g243)
    c: Vertical(g244)
    c: Block(g244)
    c: Coincident(g270,g243)
    c: Weight(g245) = 1
    c: Equal(g245, g246-g269) x24
    c: Coincident(g270,g244)
    c: InternalAlignment(g245-g269 -> g270) x25
    c: InternalAlignment(g271-g293 -> g270) x23
    c: Coincident(g305,g242)
    c: Weight(g294) = 1
    c: Equal(g294, g295-g304) x10
    c: Coincident(g305,g242)
    c: InternalAlignment(g294-g304 -> g305) x11
    c: InternalAlignment(g306-g314 -> g305) x9
    c: Block(g305)
    c: Coincident(g327,g243)
    c: Weight(g315) = 1
    c: Equal(g315, g316-g326) x11
    c: Coincident(g327,g244)
    c: InternalAlignment(g315-g326 -> g327) x12
    c: InternalAlignment(g328-g337 -> g327) x10
    c: Block(g327)
    c: Block(g270)
FEATURE [PartDesign::Body] Body  label="CommodoreLogoAndText"
  Group = -> [Sketch083]
  Origin = -> Origin
FEATURE [Part::Extrusion] Extrude074  label="CommodoreLogoAndText001"
  Base = -> Sketch083
  Dir = (0,0,1)
  DirMode = 2
  FaceMakerClass = Part::FaceMakerBullseye
  LengthFwd = 10
  LengthRev = 0
  Solid = true
  Symmetric = false
FEATURE [Part::FeaturePython] Clone  label="CommodoreLogoAndTextScale"  # Draft clone (typed FeaturePython)
  AttacherType = Attacher::AttachEngine3D
  Fuse = false
  Objects = -> [Extrude074]
  Placement = pos=(111,5.37,-11.6) rot=(0,0,1;0rad)
  Scale = (0.62,0.62,1)
FEATURE [Part::Mirroring] Part__Mirroring  label="CommodoreLogoAndTextScale (Mirror #1)"
  Base = (0,0,0)
  Normal = (1,0,0)
  Placement = pos=(123.576,0,0) rot=(0,0,1;0rad)
  Source = -> Clone
FEATURE [Sketcher::SketchObject] Sketch084
  FullyConstrained = true
  MapMode = 5
  Support = -> [XY_Plane001]
  sketch-geometry (338):
    g0: LineSegment StartX=-151.619 StartY=28.8932 StartZ=0 EndX=-140.819 EndY=28.8932 EndZ=0
    g1: LineSegment StartX=-151.619 StartY=24.0313 StartZ=0 EndX=-151.619 EndY=28.8932 EndZ=0
    g2: LineSegment StartX=-140.819 StartY=17.7713 StartZ=0 EndX=-151.619 EndY=17.7713 EndZ=0
    g3: LineSegment StartX=-151.619 StartY=17.7713 StartZ=0 EndX=-151.619 EndY=22.6313 EndZ=0
    g4: LineSegment StartX=-151.619 StartY=22.6313 StartZ=0 EndX=-145.128 EndY=22.6313 EndZ=0
    g5: LineSegment StartX=-145.128 StartY=24.0313 StartZ=0 EndX=-140.819 EndY=28.8932 EndZ=0
    g6: LineSegment StartX=-145.128 StartY=22.6313 StartZ=0 EndX=-140.819 EndY=17.7713 EndZ=0
    g7: ArcOfCircle CenterX=-155.157 CenterY=23.3323 CenterZ=0 NormalX=0 NormalY=0 NormalZ=1 AngleXU=0 Radius=6.92354 StartAngle=1.03434 EndAngle=5.24885
    g8: ArcOfCircle CenterX=-155.157 CenterY=23.3323 CenterZ=0 NormalX=0 NormalY=0 NormalZ=1 AngleXU=0 Radius=12.6269 StartAngle=1.28675 EndAngle=4.99643
    g9: LineSegment StartX=-151.619 StartY=35.4532 StartZ=0 EndX=-151.619 EndY=29.2832 EndZ=0
    g10: LineSegment StartX=-151.619 StartY=17.3813 StartZ=0 EndX=-151.619 EndY=11.2113 EndZ=0
    g11-g21: Circle x11 (B-spline internal-alignment scaffolding for g22; pole/knot coordinates omitted)
    g22: BSplineCurve PolesCount=11 KnotsCount=9 Degree=3 IsPeriodic=0
    g23-g31: GeomPoint x9 (B-spline internal-alignment scaffolding for g22; pole/knot coordinates omitted)
    g32-g49: Circle x18 (B-spline internal-alignment scaffolding for g50; pole/knot coordinates omitted)
    g50: BSplineCurve PolesCount=18 KnotsCount=16 Degree=3 IsPeriodic=0
    g51-g66: GeomPoint x16 (B-spline internal-alignment scaffolding for g50; pole/knot coordinates omitted)
    g67: LineSegment StartX=-117.124 StartY=30.093 StartZ=0 EndX=-117.603 EndY=26.5272 EndZ=0
    g68: LineSegment StartX=-117.603 StartY=17.8472 StartZ=0 EndX=-117.124 EndY=14.2659 EndZ=0
    g69: Ellipse CenterX=-109.671 CenterY=20.025 CenterZ=0 NormalX=0 NormalY=0 NormalZ=1 MajorRadius=3.34798 MinorRadius=2.71052 AngleXU=-1.56793
    g70: GeomPoint X=-109.666 Y=18.0598 Z=0
    g71: GeomPoint X=-109.677 Y=21.9902 Z=0
    g72: Ellipse CenterX=-109.671 CenterY=20.0123 CenterZ=0 NormalX=0 NormalY=0 NormalZ=1 MajorRadius=6.93002 MinorRadius=6.36273 AngleXU=-3.13976
    g73: GeomPoint X=-112.417 Y=20.0073 Z=0
    g74: GeomPoint X=-106.925 Y=20.0173 Z=0
    g75: Ellipse CenterX=-51.7682 CenterY=20.1463 CenterZ=0 NormalX=0 NormalY=0 NormalZ=1 MajorRadius=3.19279 MinorRadius=2.71052 AngleXU=-1.52774
    g76: GeomPoint X=-51.6955 Y=18.4606 Z=0
    g77: GeomPoint X=-51.8408 Y=21.832 Z=0
    g78: GeomPoint X=-54.5142 Y=20.1413 Z=0
    g79: GeomPoint X=-49.0221 Y=20.1513 Z=0
    g80: Ellipse CenterX=-51.7682 CenterY=20.1463 CenterZ=0 NormalX=0 NormalY=0 NormalZ=1 MajorRadius=6.93002 MinorRadius=6.36273 AngleXU=-3.13976
    g81: Ellipse CenterX=-22.8436 CenterY=20.1783 CenterZ=0 NormalX=0 NormalY=0 NormalZ=1 MajorRadius=3.31512 MinorRadius=2.71052 AngleXU=-1.60214
    g82: GeomPoint X=-22.9034 Y=18.2706 Z=0
    g83: GeomPoint X=-22.7838 Y=22.0861 Z=0
    g84: GeomPoint X=-25.5897 Y=20.1733 Z=0
    g85: GeomPoint X=-20.0976 Y=20.1833 Z=0
    g86: Ellipse CenterX=-22.8436 CenterY=20.1783 CenterZ=0 NormalX=0 NormalY=0 NormalZ=1 MajorRadius=6.93002 MinorRadius=6.36273 AngleXU=-3.13976
    g87: LineSegment StartX=-101.889 StartY=14.1107 StartZ=0 EndX=-97.7455 EndY=14.1107 EndZ=0
    g88: LineSegment StartX=-93.8155 StartY=14.1107 StartZ=0 EndX=-89.6755 EndY=14.1107 EndZ=0
    g89: LineSegment StartX=-85.7455 StartY=14.1107 StartZ=0 EndX=-81.6055 EndY=14.1107 EndZ=0
    g90: LineSegment StartX=-101.889 StartY=14.1107 StartZ=0 EndX=-101.889 EndY=25.9907 EndZ=0
    g91: LineSegment StartX=-101.889 StartY=25.9907 StartZ=0 EndX=-97.8594 EndY=25.9907 EndZ=0
    g92: LineSegment StartX=-97.8594 StartY=25.9907 StartZ=0 EndX=-97.8594 EndY=24.0907 EndZ=0
    g93: LineSegment StartX=-97.7455 StartY=14.1107 StartZ=0 EndX=-97.7455 EndY=19.9107 EndZ=0
    g94: LineSegment StartX=-89.6755 StartY=14.1107 StartZ=0 EndX=-89.6755 EndY=19.9107 EndZ=0
    g95: LineSegment StartX=-93.8155 StartY=14.1107 StartZ=0 EndX=-93.8155 EndY=21.0107 EndZ=0
    g96-g106: Circle x11 (B-spline internal-alignment scaffolding for g107; pole/knot coordinates omitted)
    g107: BSplineCurve PolesCount=11 KnotsCount=9 Degree=3 IsPeriodic=0
    g108-g116: GeomPoint x9 (B-spline internal-alignment scaffolding for g107; pole/knot coordinates omitted)
    g117: BSplineCurve PolesCount=11 KnotsCount=9 Degree=3 IsPeriodic=0
    g118-g125: Circle x8 (B-spline internal-alignment scaffolding for g126; pole/knot coordinates omitted)
    g126: BSplineCurve PolesCount=8 KnotsCount=6 Degree=3 IsPeriodic=0
    g127-g132: GeomPoint x6 (B-spline internal-alignment scaffolding for g126; pole/knot coordinates omitted)
    g133: BSplineCurve PolesCount=8 KnotsCount=6 Degree=3 IsPeriodic=0
    g134: LineSegment StartX=-85.7455 StartY=21.0107 StartZ=0 EndX=-85.7455 EndY=14.1107 EndZ=0
    g135: LineSegment StartX=-80.0879 StartY=14.1107 StartZ=0 EndX=-75.944 EndY=14.1107 EndZ=0
    g136: LineSegment StartX=-72.014 StartY=14.1107 StartZ=0 EndX=-67.874 EndY=14.1107 EndZ=0
    g137: LineSegment StartX=-63.944 StartY=14.1107 StartZ=0 EndX=-59.804 EndY=14.1107 EndZ=0
    g138: LineSegment StartX=-80.0879 StartY=14.1107 StartZ=0 EndX=-80.0879 EndY=25.9907 EndZ=0
    g139: LineSegment StartX=-80.0879 StartY=25.9907 StartZ=0 EndX=-76.0579 EndY=25.9907 EndZ=0
    g140: LineSegment StartX=-76.0579 StartY=25.9907 StartZ=0 EndX=-76.0579 EndY=24.0907 EndZ=0
    g141: LineSegment StartX=-75.944 StartY=14.1107 StartZ=0 EndX=-75.944 EndY=19.9107 EndZ=0
    g142: LineSegment StartX=-67.874 StartY=14.1107 StartZ=0 EndX=-67.874 EndY=19.9107 EndZ=0
    g143: LineSegment StartX=-72.014 StartY=14.1107 StartZ=0 EndX=-72.014 EndY=21.0107 EndZ=0
    g144-g148: Circle x5 (B-spline internal-alignment scaffolding for g149; pole/knot coordinates omitted)
    g149: BSplineCurve PolesCount=11 KnotsCount=9 Degree=3 IsPeriodic=0
    g150-g158: GeomPoint x9 (B-spline internal-alignment scaffolding for g149; pole/knot coordinates omitted)
    g159: BSplineCurve PolesCount=11 KnotsCount=9 Degree=3 IsPeriodic=0
    g160-g167: Circle x8 (B-spline internal-alignment scaffolding for g168; pole/knot coordinates omitted)
    g168: BSplineCurve PolesCount=8 KnotsCount=6 Degree=3 IsPeriodic=0
    g169-g174: GeomPoint x6 (B-spline internal-alignment scaffolding for g168; pole/knot coordinates omitted)
    g175: BSplineCurve PolesCount=8 KnotsCount=6 Degree=3 IsPeriodic=0
    g176: LineSegment StartX=-63.944 StartY=21.0107 StartZ=0 EndX=-63.944 EndY=14.1107 EndZ=0
    g177: LineSegment StartX=-59.804 StartY=14.1107 StartZ=0 EndX=-59.804 EndY=21.5868 EndZ=0
    g178: BSplineCurve PolesCount=4 KnotsCount=2 Degree=3 IsPeriodic=0
    g179: GeomPoint X=-59.804 Y=21.5868 Z=0
    g180: GeomPoint X=-60.2379 Y=24.0907 Z=0
    g181: LineSegment StartX=-81.6055 StartY=14.1107 StartZ=0 EndX=-81.6055 EndY=21.5868 EndZ=0
    g182: LineSegment StartX=-151.619 StartY=24.0313 StartZ=0 EndX=-145.128 EndY=24.0313 EndZ=0
    g183: Circle CenterX=-82.0394 CenterY=24.0907 CenterZ=0 NormalX=0 NormalY=0 NormalZ=1 AngleXU=0 Radius=1
    g184: Circle CenterX=-81.7131 CenterY=23.2736 CenterZ=0 NormalX=0 NormalY=0 NormalZ=1 AngleXU=0 Radius=1
    g185: Circle CenterX=-81.6055 CenterY=21.5868 CenterZ=0 NormalX=0 NormalY=0 NormalZ=1 AngleXU=0 Radius=1
    g186: BSplineCurve PolesCount=3 KnotsCount=2 Degree=2 IsPeriodic=0
    g187: GeomPoint X=-82.0394 Y=24.0907 Z=0
    g188: GeomPoint X=-81.6055 Y=21.5868 Z=0
    g189: Ellipse CenterX=-37.3522 CenterY=19.9515 CenterZ=0 NormalX=0 NormalY=0 NormalZ=1 MajorRadius=2.99755 MinorRadius=2.49 AngleXU=1.5708
    g190: GeomPoint X=-37.3522 Y=21.6203 Z=0
    g191: GeomPoint X=-37.3522 Y=18.2826 Z=0
    g192: ArcOfEllipse CenterX=-38.7647 CenterY=20.06 CenterZ=0 NormalX=0 NormalY=0 NormalZ=1 MajorRadius=6.30025 MinorRadius=5.3849 AngleXU=1.57276 StartAngle=5.50632 EndAngle=10.3035
    g193: GeomPoint X=-38.7711 Y=23.3304 Z=0
    g194: GeomPoint X=-38.7583 Y=16.7895 Z=0
    g195: LineSegment StartX=-34.6109 StartY=14.1107 StartZ=0 EndX=-30.8984 EndY=14.1107 EndZ=0
    g196: LineSegment StartX=-30.8984 StartY=14.1107 StartZ=0 EndX=-30.8984 EndY=31.1784 EndZ=0
    g197: LineSegment StartX=-30.8984 StartY=31.1784 StartZ=0 EndX=-34.9984 EndY=31.1784 EndZ=0
    g198: LineSegment StartX=-34.9984 StartY=24.5602 StartZ=0 EndX=-34.9984 EndY=31.1784 EndZ=0
    g199: LineSegment StartX=-34.6109 StartY=16.0476 StartZ=0 EndX=-34.6109 EndY=14.1107 EndZ=0
    g200: LineSegment StartX=-14.8781 StartY=14.1107 StartZ=0 EndX=-10.5106 EndY=14.1107 EndZ=0
    g201: LineSegment StartX=-14.8781 StartY=14.1107 StartZ=0 EndX=-14.8781 EndY=25.8504 EndZ=0
    g202: LineSegment StartX=-14.8781 StartY=25.8504 StartZ=0 EndX=-10.8534 EndY=25.8504 EndZ=0
    g203: LineSegment StartX=-10.8534 StartY=25.8504 StartZ=0 EndX=-10.8534 EndY=24.0923 EndZ=0
    g204: LineSegment StartX=-10.5106 StartY=14.1107 StartZ=0 EndX=-10.5106 EndY=19.7752 EndZ=0
    g205: LineSegment StartX=-5.96397 StartY=25.9304 StartZ=0 EndX=-5.96397 EndY=22.574 EndZ=0
    g206-g214: Circle x9 (B-spline internal-alignment scaffolding for g215; pole/knot coordinates omitted)
    g215: BSplineCurve PolesCount=9 KnotsCount=7 Degree=3 IsPeriodic=0
    g216-g222: GeomPoint x7 (B-spline internal-alignment scaffolding for g215; pole/knot coordinates omitted)
    g223-g232: Circle x10 (B-spline internal-alignment scaffolding for g233; pole/knot coordinates omitted)
    g233: BSplineCurve PolesCount=10 KnotsCount=8 Degree=3 IsPeriodic=0
    g234-g241: GeomPoint x8 (B-spline internal-alignment scaffolding for g233; pole/knot coordinates omitted)
    g242: LineSegment StartX=-1.58923 StartY=21.0696 StartZ=0 EndX=2.62034 EndY=21.0696 EndZ=0
    g243: LineSegment StartX=-1.55856 StartY=18.7342 StartZ=0 EndX=6.45946 EndY=18.7342 EndZ=0
    g244: LineSegment StartX=5.29231 StartY=17.386 StartZ=0 EndX=5.29231 EndY=14.3674 EndZ=0
    g245-g269: Circle x25 (B-spline internal-alignment scaffolding for g270; pole/knot coordinates omitted)
    g270: BSplineCurve PolesCount=25 KnotsCount=23 Degree=3 IsPeriodic=0
    g271-g293: GeomPoint x23 (B-spline internal-alignment scaffolding for g270; pole/knot coordinates omitted)
    g294-g304: Circle x11 (B-spline internal-alignment scaffolding for g305; pole/knot coordinates omitted)
    g305: BSplineCurve PolesCount=11 KnotsCount=9 Degree=3 IsPeriodic=0
    g306-g314: GeomPoint x9 (B-spline internal-alignment scaffolding for g305; pole/knot coordinates omitted)
    g315-g326: Circle x12 (B-spline internal-alignment scaffolding for g327; pole/knot coordinates omitted)
    g327: BSplineCurve PolesCount=12 KnotsCount=10 Degree=3 IsPeriodic=0
    g328-g337: GeomPoint x10 (B-spline internal-alignment scaffolding for g327; pole/knot coordinates omitted)
  constraints (252):
    c: Coincident(g1,g0)
    c: Horizontal(g0)
    c: Vertical(g1)
    c: Coincident(g2,g3)
    c: Coincident(g3,g4)
    c: Horizontal(g4)
    c: Horizontal(g2)
    c: Vertical(g3)
    c: Block(g1)
    c: Distance(g3) = 4.86
    c: Block(g4)
    c: Distance(g0) = 10.8
    c: Distance(g2) = 10.8
    c: Coincident(g5,g0)
    c: Coincident(g6,g4)
    c: Coincident(g6,g2)
    c: Block(g8)
    c: Block(g7)
    c: Coincident(g9,g8)
    c: Coincident(g9,g7)
    c: Vertical(g9)
    c: Coincident(g10,g7)
    c: Coincident(g10,g8)
    c: Vertical(g10)
    c: Weight(g11) = 1
    c: Equal(g11, g12-g21) x10
    c: InternalAlignment(g11-g21 -> g22) x11
    c: InternalAlignment(g23-g31 -> g22) x9
    c: Block(g22)
    c: Weight(g32) = 1
    c: Equal(g32, g33-g49) x17
    c: InternalAlignment(g32-g49 -> g50) x18
    c: InternalAlignment(g51-g66 -> g50) x16
    c: Block(g50)
    c: Coincident(g67,g50)
    c: Coincident(g67,g22)
    c: Coincident(g68,g22)
    c: Coincident(g68,g50)
    c: InternalAlignment(g70,g69)
    c: InternalAlignment(g71,g69)
    c: Block(g69)
    c: InternalAlignment(g73,g72)
    c: InternalAlignment(g74,g72)
    c: Block(g72)
    c: InternalAlignment(g76,g75)
    c: InternalAlignment(g77,g75)
    c: InternalAlignment(g78,g80)
    c: InternalAlignment(g79,g80)
    c: Block(g80)
    c: Coincident(g75,g80)
    c: Block(g75)
    c: InternalAlignment(g82,g81)
    c: InternalAlignment(g83,g81)
    c: InternalAlignment(g84,g86)
    c: InternalAlignment(g85,g86)
    c: Block(g86)
    c: Coincident(g81,g86)
    c: Block(g81)
    c: Horizontal(g87)
    c: Block(g87)
    c: Horizontal(g88)
    c: Distance(g88) = 4.14
    c: Horizontal(g89)
    c: Equal(g88,g89) = 4.14
    c: Block(g89)
    c: Block(g88)
    c: Coincident(g90,g87)
    c: Vertical(g90)
    c: Distance(g90) = 11.88
    c: Coincident(g91,g90)
    c: Horizontal(g91)
    c: Coincident(g92,g91)
    c: Vertical(g92)
    c: Distance(g91) = 4.03
    c: Distance(g92) = 1.9
    c: Coincident(g93,g87)
    c: Vertical(g93)
    c: Vertical(g94)
    c: Coincident(g94,g88)
    c: Distance(g93) = 5.8
    c: Distance(g94) = 5.8
    c: Vertical(g95)
    c: Coincident(g95,g88)
    c: Distance(g95) = 6.9
    c: Coincident(g107,g92)
    c: Weight(g96) = 1
    c: Equal(g96, g97-g106) x10
    c: InternalAlignment(g96-g106 -> g107) x11
    c: InternalAlignment(g108-g116 -> g107) x9
    c: Block(g107)
    c: Block(g117)
    c: Coincident(g126,g93)
    c: Weight(g118) = 1
    c: Equal(g118, g119-g125) x7
    c: Coincident(g126,g95)
    c: InternalAlignment(g118-g125 -> g126) x8
    c: InternalAlignment(g127-g132 -> g126) x6
    c: Coincident(g133,g94)
    c: Block(g126)
    c: Block(g133)
    c: Coincident(g134,g133)
    c: Coincident(g134,g89)
    c: Vertical(g134)
    c: Horizontal(g135)
    c: Block(g135)
    c: Horizontal(g136)
    c: Equal(g88,g136) = 4.14
    c: Horizontal(g137)
    c: Equal(g136,g137) = 4.14
    c: Block(g137)
    c: Block(g136)
    c: Coincident(g138,g135)
    c: Vertical(g138)
    c: Equal(g90,g138) = 11.88
    c: Coincident(g139,g138)
    c: Horizontal(g139)
    c: Coincident(g140,g139)
    c: Vertical(g140)
    c: Equal(g91,g139) = 4.03
    c: Equal(g92,g140) = 1.9
    c: Coincident(g141,g135)
    c: Vertical(g141)
    c: Vertical(g142)
    c: Coincident(g142,g136)
    c: Equal(g93,g141) = 5.8
    c: Equal(g94,g142) = 5.8
    c: Vertical(g143)
    c: Coincident(g143,g136)
    c: Equal(g95,g143) = 6.9
    c: Coincident(g149,g140)
    c: Equal(g96,g144) = 1
    c: Equal(g144, g145-g148) x4
    c: InternalAlignment(g144-g148 -> g149) x5
    c: InternalAlignment(g150-g158 -> g149) x9
    c: Block(g149)
    c: Block(g159)
    c: Coincident(g168,g141)
    c: Equal(g118,g160) = 1
    c: Equal(g160, g161-g167) x7
    c: Coincident(g168,g143)
    c: InternalAlignment(g160-g167 -> g168) x8
    c: InternalAlignment(g169-g174 -> g168) x6
    c: Coincident(g175,g142)
    c: Block(g168)
    c: Block(g175)
    c: Coincident(g176,g175)
    c: Coincident(g176,g137)
    c: Vertical(g176)
    c: Coincident(g177,g137)
    c: Vertical(g177)
    c: Coincident(g178,g177)
    c: Coincident(g178,g159)
    c: InternalAlignment(g179,g178)
    c: InternalAlignment(g180,g178)
    c: Block(g178)
    c: Vertical(g181)
    c: Coincident(g181,g89)
    c: Block(g5)
    c: Coincident(g182,g1)
    c: Coincident(g182,g5)
    c: Horizontal(g182)
    c: Coincident(g186,g117)
    c: Weight(g183) = 1
    c: Equal(g183,g184)
    c: Equal(g183,g185)
    c: Coincident(g186,g181)
    c: InternalAlignment(g183,g186)
    c: InternalAlignment(g184,g186)
    c: InternalAlignment(g185,g186)
    c: InternalAlignment(g187,g186)
    c: InternalAlignment(g188,g186)
    c: Block(g186)
    c: InternalAlignment(g190,g189)
    c: InternalAlignment(g191,g189)
    c: Block(g189)
    c: InternalAlignment(g193,g192)
    c: InternalAlignment(g194,g192)
    c: Block(g192)
    c: Horizontal(g195)
    c: Block(g195)
    c: Coincident(g196,g195)
    c: Vertical(g196)
    c: Block(g196)
    c: Distance(g195) = 3.71244
    c: Coincident(g197,g196)
    c: Horizontal(g197)
    c: Distance(g197) = 4.1
    c: Coincident(g198,g192)
    c: Coincident(g198,g197)
    c: Vertical(g198)
    c: Block(g198)
    c: Coincident(g199,g192)
    c: Coincident(g199,g195)
    c: Vertical(g199)
    c: Block(g199)
    c: Horizontal(g200)
    c: Block(g200)
    c: Coincident(g201,g200)
    c: Vertical(g201)
    c: Block(g201)
    c: Coincident(g202,g201)
    c: Horizontal(g202)
    c: Block(g202)
    c: Coincident(g203,g202)
    c: Vertical(g203)
    c: Block(g203)
    c: Coincident(g204,g200)
    c: Vertical(g204)
    c: Block(g204)
    c: Coincident(g215,g203)
    c: Weight(g206) = 1
    c: Equal(g206, g207-g214) x8
    c: Coincident(g215,g205)
    c: InternalAlignment(g206-g214 -> g215) x9
    c: InternalAlignment(g216-g222 -> g215) x7
    c: Coincident(g233,g204)
    c: Weight(g223) = 1
    c: Equal(g223, g224-g232) x9
    c: Coincident(g233,g205)
    c: InternalAlignment(g223-g232 -> g233) x10
    c: InternalAlignment(g234-g241 -> g233) x8
    c: Vertical(g205)
    c: Block(g205)
    c: Block(g215)
    c: Block(g233)
    c: Horizontal(g242)
    c: Horizontal(g243)
    c: Block(g242)
    c: Block(g243)
    c: Vertical(g244)
    c: Block(g244)
    c: Coincident(g270,g243)
    c: Weight(g245) = 1
    c: Equal(g245, g246-g269) x24
    c: Coincident(g270,g244)
    c: InternalAlignment(g245-g269 -> g270) x25
    c: InternalAlignment(g271-g293 -> g270) x23
    c: Coincident(g305,g242)
    c: Weight(g294) = 1
    c: Equal(g294, g295-g304) x10
    c: Coincident(g305,g242)
    c: InternalAlignment(g294-g304 -> g305) x11
    c: InternalAlignment(g306-g314 -> g305) x9
    c: Block(g305)
    c: Coincident(g327,g243)
    c: Weight(g315) = 1
    c: Equal(g315, g316-g326) x11
    c: Coincident(g327,g244)
    c: InternalAlignment(g315-g326 -> g327) x12
    c: InternalAlignment(g328-g337 -> g327) x10
    c: Block(g327)
    c: Block(g270)
FEATURE [Part::Extrusion] Extrude075  label="CommodoreLogoAndText002"
  Base = -> Sketch084
  Dir = (0,0,1)
  DirMode = 2
  FaceMakerClass = Part::FaceMakerBullseye
  LengthFwd = 10
  LengthRev = 0
  Solid = true
  Symmetric = false
FEATURE [Part::FeaturePython] Clone001  label="CommodoreLogoAndTextScale001"  # Draft clone (typed FeaturePython)
  AttacherType = Attacher::AttachEngine3D
  Fuse = false
  Objects = -> [Extrude075]
  Placement = pos=(112.566,5.37,73.6) rot=(0,0,1;0rad)
  Scale = (0.62,0.62,1)
FEATURE [Part::Cut] Cut073  label="sideA005"
  Base = -> Extrude002
  Tool = -> Part__Mirroring
FEATURE [Part::Cut] Cut074  label="sideB005"
  Base = -> Extrude028
  Tool = -> Clone001
FEATURE [Sketcher::SketchObject] Sketch085
  FullyConstrained = true
  Placement = pos=(0,0,0) rot=(-1,0,0;4.71239rad)
  sketch-geometry (10):
    g0: LineSegment StartX=0 StartY=0 StartZ=0 EndX=-7 EndY=0 EndZ=0
    g1: LineSegment StartX=-7 StartY=10 StartZ=0 EndX=-6.5 EndY=10 EndZ=0
    g2: LineSegment StartX=0 StartY=10 StartZ=0 EndX=-0.5 EndY=10 EndZ=0
    g3: ArcOfCircle CenterX=-3.5 CenterY=10 CenterZ=0 NormalX=0 NormalY=0 NormalZ=1 AngleXU=0 Radius=3 StartAngle=3.14159 EndAngle=6.28319
    g4: LineSegment StartX=-7 StartY=0 StartZ=0 EndX=-10.5 EndY=0 EndZ=0
    g5: LineSegment StartX=0 StartY=0 StartZ=0 EndX=3.5 EndY=0 EndZ=0
    g6: ArcOfCircle CenterX=-10.5 CenterY=3.5 CenterZ=0 NormalX=0 NormalY=0 NormalZ=1 AngleXU=0 Radius=3.5 StartAngle=4.71239 EndAngle=6.28319
    g7: ArcOfCircle CenterX=3.5 CenterY=3.5 CenterZ=0 NormalX=0 NormalY=0 NormalZ=1 AngleXU=0 Radius=3.5 StartAngle=3.14159 EndAngle=4.71239
    g8: LineSegment StartX=-7 StartY=3.5 StartZ=0 EndX=-7 EndY=10 EndZ=0
    g9: LineSegment StartX=0 StartY=10 StartZ=0 EndX=0 EndY=3.5 EndZ=0
  constraints (26):
    c: Coincident(g0,g-1)
    c: Horizontal(g0)
    c: Distance(g0) = 7
    c: Horizontal(g1)
    c: Distance(g1) = 0.5
    c: Horizontal(g2)
    c: Distance(g2) = 0.5
    c: Coincident(g3,g1)
    c: Coincident(g3,g2)
    c: Block(g3)
    c: Coincident(g4,g0)
    c: Horizontal(g4)
    c: Distance(g4) = 3.5
    c: Coincident(g5,g0)
    c: Distance(g5) = 3.5
    c: Horizontal(g5)
    c: Coincident(g6,g4)
    c: Block(g6)
    c: Coincident(g7,g5)
    c: Block(g7)
    c: Coincident(g8,g6)
    c: Coincident(g8,g1)
    c: Vertical(g8)
    c: Coincident(g9,g2)
    c: Coincident(g9,g7)
    c: Vertical(g9)
FEATURE [Part::Extrusion] Extrude076  label="backRightCasePillarSideBracket"
  Base = -> Sketch085
  Dir = (0,-1,3e-16)
  DirMode = 2
  FaceMakerClass = Part::FaceMakerBullseye
  LengthFwd = 6.7
  LengthRev = 0
  Placement = pos=(16,11.5,0) rot=(0,0,1;0rad)
  Solid = true
  Symmetric = false
FEATURE [Sketcher::SketchObject] Sketch086
  FullyConstrained = true
  Placement = pos=(0,0,0) rot=(1,0,0;1.5708rad)
  sketch-geometry (10):
    g0: LineSegment StartX=0 StartY=0 StartZ=0 EndX=-7 EndY=0 EndZ=0
    g1: LineSegment StartX=-7 StartY=10 StartZ=0 EndX=-6.5 EndY=10 EndZ=0
    g2: LineSegment StartX=0 StartY=10 StartZ=0 EndX=-0.5 EndY=10 EndZ=0
    g3: ArcOfCircle CenterX=-3.5 CenterY=10 CenterZ=0 NormalX=0 NormalY=0 NormalZ=1 AngleXU=0 Radius=3 StartAngle=3.14159 EndAngle=6.28319
    g4: LineSegment StartX=-7 StartY=0 StartZ=0 EndX=-10.5 EndY=0 EndZ=0
    g5: LineSegment StartX=0 StartY=0 StartZ=0 EndX=3.5 EndY=0 EndZ=0
    g6: ArcOfCircle CenterX=-10.5 CenterY=3.5 CenterZ=0 NormalX=0 NormalY=0 NormalZ=1 AngleXU=0 Radius=3.5 StartAngle=4.71239 EndAngle=6.28319
    g7: ArcOfCircle CenterX=3.5 CenterY=3.5 CenterZ=0 NormalX=0 NormalY=0 NormalZ=1 AngleXU=0 Radius=3.5 StartAngle=3.14159 EndAngle=4.71239
    g8: LineSegment StartX=-7 StartY=3.5 StartZ=0 EndX=-7 EndY=10 EndZ=0
    g9: LineSegment StartX=0 StartY=10 StartZ=0 EndX=0 EndY=3.5 EndZ=0
  constraints (26):
    c: Coincident(g0,g-1)
    c: Horizontal(g0)
    c: Distance(g0) = 7
    c: Horizontal(g1)
    c: Distance(g1) = 0.5
    c: Horizontal(g2)
    c: Distance(g2) = 0.5
    c: Coincident(g3,g1)
    c: Coincident(g3,g2)
    c: Block(g3)
    c: Coincident(g4,g0)
    c: Horizontal(g4)
    c: Distance(g4) = 3.5
    c: Coincident(g5,g0)
    c: Distance(g5) = 3.5
    c: Horizontal(g5)
    c: Coincident(g6,g4)
    c: Block(g6)
    c: Coincident(g7,g5)
    c: Block(g7)
    c: Coincident(g8,g6)
    c: Coincident(g8,g1)
    c: Vertical(g8)
    c: Coincident(g9,g2)
    c: Coincident(g9,g7)
    c: Vertical(g9)
FEATURE [Part::Extrusion] Extrude077  label="backLeftCasePillarSideBracket001"
  Base = -> Sketch086
  Dir = (0,-1,3e-16)
  DirMode = 2
  FaceMakerClass = Part::FaceMakerBullseye
  LengthFwd = 6.7
  LengthRev = 0
  Placement = pos=(9,11.5,72) rot=(0,1,0;3.14159rad)
  Solid = true
  Symmetric = false
FEATURE [Sketcher::SketchObject] Sketch087
  FullyConstrained = true
  Placement = pos=(0,0,0) rot=(1,0,0;1.5708rad)
  sketch-geometry (8):
    g0: LineSegment StartX=0 StartY=4e-16 StartZ=0 EndX=-7 EndY=4e-16 EndZ=0
    g1: LineSegment StartX=-7 StartY=4e-16 StartZ=0 EndX=-10.5 EndY=4e-16 EndZ=0
    g2: LineSegment StartX=0 StartY=4e-16 StartZ=0 EndX=3.5 EndY=4e-16 EndZ=0
    g3: ArcOfCircle CenterX=-10.5 CenterY=3.5 CenterZ=0 NormalX=0 NormalY=0 NormalZ=1 AngleXU=0 Radius=3.5 StartAngle=4.71239 EndAngle=6.28319
    g4: ArcOfCircle CenterX=3.5 CenterY=3.5 CenterZ=0 NormalX=0 NormalY=0 NormalZ=1 AngleXU=0 Radius=3.5 StartAngle=3.14159 EndAngle=4.71239
    g5: ArcOfCircle CenterX=-3.5 CenterY=3.5 CenterZ=0 NormalX=0 NormalY=0 NormalZ=1 AngleXU=0 Radius=3 StartAngle=3.14159 EndAngle=6.28319
    g6: LineSegment StartX=-7 StartY=3.5 StartZ=0 EndX=-6.5 EndY=3.5 EndZ=0
    g7: LineSegment StartX=-0.5 StartY=3.5 StartZ=0 EndX=0 EndY=3.5 EndZ=0
  constraints (20):
    c: Coincident(g0,g-1)
    c: Horizontal(g0)
    c: Distance(g0) = 7
    c: Coincident(g1,g0)
    c: Horizontal(g1)
    c: Distance(g1) = 3.5
    c: Coincident(g2,g0)
    c: Distance(g2) = 3.5
    c: Horizontal(g2)
    c: Coincident(g3,g1)
    c: Block(g3)
    c: Coincident(g4,g2)
    c: Block(g4)
    c: Horizontal(g6)
    c: Coincident(g5,g6)
    c: Block(g5)
    c: Coincident(g6,g3)
    c: Coincident(g7,g5)
    c: Coincident(g7,g4)
    c: Horizontal(g7)
FEATURE [Part::Extrusion] Extrude078  label="frontBackLeftCasePillarSideBracket001"
  Base = -> Sketch087
  Dir = (0,-1,2e-16)
  DirMode = 2
  FaceMakerClass = Part::FaceMakerBullseye
  LengthFwd = 6.7
  LengthRev = 0
  Placement = pos=(93,11.5,0) rot=(0,0,1;0rad)
  Solid = true
  Symmetric = false
FEATURE [Sketcher::SketchObject] Sketch088
  FullyConstrained = true
  Placement = pos=(0,0,0) rot=(1,0,0;1.5708rad)
  sketch-geometry (8):
    g0: LineSegment StartX=0 StartY=4e-16 StartZ=0 EndX=-7 EndY=4e-16 EndZ=0
    g1: LineSegment StartX=-7 StartY=4e-16 StartZ=0 EndX=-10.5 EndY=4e-16 EndZ=0
    g2: LineSegment StartX=0 StartY=4e-16 StartZ=0 EndX=3.5 EndY=4e-16 EndZ=0
    g3: ArcOfCircle CenterX=-10.5 CenterY=3.5 CenterZ=0 NormalX=0 NormalY=0 NormalZ=1 AngleXU=0 Radius=3.5 StartAngle=4.71239 EndAngle=6.28319
    g4: ArcOfCircle CenterX=3.5 CenterY=3.5 CenterZ=0 NormalX=0 NormalY=0 NormalZ=1 AngleXU=0 Radius=3.5 StartAngle=3.14159 EndAngle=4.71239
    g5: ArcOfCircle CenterX=-3.5 CenterY=3.5 CenterZ=0 NormalX=0 NormalY=0 NormalZ=1 AngleXU=0 Radius=3 StartAngle=3.14159 EndAngle=6.28319
    g6: LineSegment StartX=-7 StartY=3.5 StartZ=0 EndX=-6.5 EndY=3.5 EndZ=0
    g7: LineSegment StartX=-0.5 StartY=3.5 StartZ=0 EndX=0 EndY=3.5 EndZ=0
  constraints (20):
    c: Coincident(g0,g-1)
    c: Horizontal(g0)
    c: Distance(g0) = 7
    c: Coincident(g1,g0)
    c: Horizontal(g1)
    c: Distance(g1) = 3.5
    c: Coincident(g2,g0)
    c: Distance(g2) = 3.5
    c: Horizontal(g2)
    c: Coincident(g3,g1)
    c: Block(g3)
    c: Coincident(g4,g2)
    c: Block(g4)
    c: Horizontal(g6)
    c: Coincident(g5,g6)
    c: Block(g5)
    c: Coincident(g6,g3)
    c: Coincident(g7,g5)
    c: Coincident(g7,g4)
    c: Horizontal(g7)
FEATURE [Part::Extrusion] Extrude079  label="frontFrontRightCasePillarSideBracket002"
  Base = -> Sketch088
  Dir = (0,-1,2e-16)
  DirMode = 2
  FaceMakerClass = Part::FaceMakerBullseye
  LengthFwd = 2
  LengthRev = 0
  Placement = pos=(106,11.5,72) rot=(0,1,0;3.14159rad)
  Solid = true
  Symmetric = false
FEATURE [Part::Chamfer] Chamfer
  Base = -> Extrude076
  Edges = 1 edges r=3: [Edge19]
FEATURE [Part::Chamfer] Chamfer002
  Base = -> Extrude077
  Edges = 1 edges r=3: [Edge7]
FEATURE [Part::Chamfer] Chamfer003  label="backLeftCasePillarSideBracket002"
  Base = -> Chamfer002
  Edges = 1 edges r=3.8: [Edge29]
FEATURE [Part::Chamfer] Chamfer004  label="backRightCasePillarSideBracket001"
  Base = -> Chamfer
  Edges = 1 edges r=3.8: [Edge24]
FEATURE [Sketcher::SketchObject] Sketch089
  FullyConstrained = true
  Placement = pos=(0,0,0) rot=(1,0,0;1.5708rad)
  sketch-geometry (8):
    g0: LineSegment StartX=0 StartY=4e-16 StartZ=0 EndX=-7 EndY=4e-16 EndZ=0
    g1: LineSegment StartX=-7 StartY=4e-16 StartZ=0 EndX=-10.5 EndY=4e-16 EndZ=0
    g2: LineSegment StartX=0 StartY=4e-16 StartZ=0 EndX=3.5 EndY=4e-16 EndZ=0
    g3: ArcOfCircle CenterX=-10.5 CenterY=3.5 CenterZ=0 NormalX=0 NormalY=0 NormalZ=1 AngleXU=0 Radius=3.5 StartAngle=4.71239 EndAngle=6.28319
    g4: ArcOfCircle CenterX=3.5 CenterY=3.5 CenterZ=0 NormalX=0 NormalY=0 NormalZ=1 AngleXU=0 Radius=3.5 StartAngle=3.14159 EndAngle=4.71239
    g5: ArcOfCircle CenterX=-3.5 CenterY=3.5 CenterZ=0 NormalX=0 NormalY=0 NormalZ=1 AngleXU=0 Radius=3 StartAngle=3.14159 EndAngle=6.28319
    g6: LineSegment StartX=-7 StartY=3.5 StartZ=0 EndX=-6.5 EndY=3.5 EndZ=0
    g7: LineSegment StartX=-0.5 StartY=3.5 StartZ=0 EndX=0 EndY=3.5 EndZ=0
  constraints (20):
    c: Coincident(g0,g-1)
    c: Horizontal(g0)
    c: Distance(g0) = 7
    c: Coincident(g1,g0)
    c: Horizontal(g1)
    c: Distance(g1) = 3.5
    c: Coincident(g2,g0)
    c: Distance(g2) = 3.5
    c: Horizontal(g2)
    c: Coincident(g3,g1)
    c: Block(g3)
    c: Coincident(g4,g2)
    c: Block(g4)
    c: Horizontal(g6)
    c: Coincident(g5,g6)
    c: Block(g5)
    c: Coincident(g6,g3)
    c: Coincident(g7,g5)
    c: Coincident(g7,g4)
    c: Horizontal(g7)
FEATURE [Part::Extrusion] Extrude080  label="frontBackLeftCasePillarSideBracket002"
  Base = -> Sketch089
  Dir = (0,-1,2e-16)
  DirMode = 2
  FaceMakerClass = Part::FaceMakerBullseye
  LengthFwd = 6.7
  LengthRev = 0
  Placement = pos=(86,11.5,72) rot=(0,1,0;3.14159rad)
  Solid = true
  Symmetric = false
FEATURE [Part::Box] Box037  label="backLeftCasePillarAngledSideBracket"
  AttacherType = Attacher::AttachEngine3D
  Height = 14
  Length = 3.4
  Placement = pos=(0,10.8,0) rot=(0,1,0;0.785398rad)
  Width = 4
FEATURE [Part::Box] Box038  label="backRightCasePillarAngledSideBracket"
  AttacherType = Attacher::AttachEngine3D
  Height = 14
  Length = 3.4
  Placement = pos=(9.9,10.8,62.1) rot=(0,1,0;-0.785398rad)
  Width = 4
FEATURE [Sketcher::SketchObject] Sketch090  label="topSketch026"
  FullyConstrained = true
  sketch-geometry (8):
    g0: ArcOfCircle CenterX=19 CenterY=19.1201 CenterZ=0 NormalX=0 NormalY=0 NormalZ=1 AngleXU=0 Radius=18.8799 StartAngle=1.5708 EndAngle=3.14793
    g1: LineSegment StartX=0.120501 StartY=19.0004 StartZ=0 EndX=0.120501 EndY=0.000382114 EndZ=0
    g2: LineSegment StartX=19 StartY=38 StartZ=0 EndX=124 EndY=38 EndZ=0
    g3: LineSegment StartX=0.120501 StartY=0.000382114 StartZ=0 EndX=105.121 EndY=0.000382114 EndZ=0
    g4: LineSegment StartX=124 StartY=38 StartZ=0 EndX=125.616 EndY=38 EndZ=0
    g5: LineSegment StartX=105.121 StartY=0.000382114 StartZ=0 EndX=106.736 EndY=0.000382114 EndZ=0
    g6: ArcOfCircle CenterX=106.616 CenterY=19 CenterZ=0 NormalX=0 NormalY=0 NormalZ=1 AngleXU=0 Radius=19 StartAngle=4.71873 EndAngle=6.28319
    g7: LineSegment StartX=125.616 StartY=38 StartZ=0 EndX=125.616 EndY=19 EndZ=0
  constraints (21):
    c: Block(g0)
    c: Coincident(g1,g0)
    c: Vertical(g1)
    c: Horizontal(g2)
    c: Distance(g2) = 105
    c: Coincident(g2,g0)
    c: Distance(g1) = 19
    c: Coincident(g3,g1)
    c: Horizontal(g3)
    c: Distance(g3) = 105
    c: Coincident(g4,g2)
    c: Horizontal(g4)
    c: Distance(g4) = 1.61553
    c: Horizontal(g5)
    c: Equal(g4,g5) = 1.61553
    c: Coincident(g5,g3)
    c: Block(g6)
    c: Coincident(g6,g5)
    c: Coincident(g7,g4)
    c: Coincident(g7,g6)
    c: Vertical(g7)
FEATURE [Part::Extrusion] Extrude081  label="sideB006"
  Base = -> Sketch090
  Dir = (0,0,1)
  DirMode = 2
  FaceMakerClass = Part::FaceMakerBullseye
  LengthFwd = 3
  LengthRev = 0
  Placement = pos=(-0.1205,0,72) rot=(0,0,1;0rad)
  Solid = true
  Symmetric = false
FEATURE [Sketcher::SketchObject] Sketch091  label="topSketch027"
  FullyConstrained = true
  sketch-geometry (8):
    g0: ArcOfCircle CenterX=19 CenterY=19.1201 CenterZ=0 NormalX=0 NormalY=0 NormalZ=1 AngleXU=0 Radius=18.8799 StartAngle=1.5708 EndAngle=3.14793
    g1: LineSegment StartX=0.120501 StartY=19.0004 StartZ=0 EndX=0.120501 EndY=0.000382114 EndZ=0
    g2: LineSegment StartX=19 StartY=38 StartZ=0 EndX=124 EndY=38 EndZ=0
    g3: LineSegment StartX=0.120501 StartY=0.000382114 StartZ=0 EndX=105.121 EndY=0.000382114 EndZ=0
    g4: LineSegment StartX=124 StartY=38 StartZ=0 EndX=125.616 EndY=38 EndZ=0
    g5: LineSegment StartX=105.121 StartY=0.000382114 StartZ=0 EndX=106.736 EndY=0.000382114 EndZ=0
    g6: ArcOfCircle CenterX=106.616 CenterY=19 CenterZ=0 NormalX=0 NormalY=0 NormalZ=1 AngleXU=0 Radius=19 StartAngle=4.71873 EndAngle=6.28319
    g7: LineSegment StartX=125.616 StartY=38 StartZ=0 EndX=125.616 EndY=19 EndZ=0
  constraints (21):
    c: Block(g0)
    c: Coincident(g1,g0)
    c: Vertical(g1)
    c: Horizontal(g2)
    c: Distance(g2) = 105
    c: Coincident(g2,g0)
    c: Distance(g1) = 19
    c: Coincident(g3,g1)
    c: Horizontal(g3)
    c: Distance(g3) = 105
    c: Coincident(g4,g2)
    c: Horizontal(g4)
    c: Distance(g4) = 1.61553
    c: Horizontal(g5)
    c: Equal(g4,g5) = 1.61553
    c: Coincident(g5,g3)
    c: Block(g6)
    c: Coincident(g6,g5)
    c: Coincident(g7,g4)
    c: Coincident(g7,g6)
    c: Vertical(g7)
FEATURE [Part::Extrusion] Extrude082  label="sideB007"
  Base = -> Sketch091
  Dir = (0,0,1)
  DirMode = 2
  FaceMakerClass = Part::FaceMakerBullseye
  LengthFwd = 3
  LengthRev = 0
  Placement = pos=(0,0,72) rot=(0,0,1;0rad)
  Solid = true
  Symmetric = false
FEATURE [Part::Cut] Cut075
  Base = -> Extrude081
  Placement = pos=(0.05,0,0) rot=(0,0,1;0rad)
  Tool = -> Extrude082
FEATURE [Sketcher::SketchObject] Sketch092  label="topSketch028"
  FullyConstrained = true
  sketch-geometry (8):
    g0: ArcOfCircle CenterX=19 CenterY=19.1201 CenterZ=0 NormalX=0 NormalY=0 NormalZ=1 AngleXU=0 Radius=18.8799 StartAngle=1.5708 EndAngle=3.14793
    g1: LineSegment StartX=0.120501 StartY=19.0004 StartZ=0 EndX=0.120501 EndY=0.000382114 EndZ=0
    g2: LineSegment StartX=19 StartY=38 StartZ=0 EndX=124 EndY=38 EndZ=0
    g3: LineSegment StartX=0.120501 StartY=0.000382114 StartZ=0 EndX=105.121 EndY=0.000382114 EndZ=0
    g4: LineSegment StartX=124 StartY=38 StartZ=0 EndX=125.616 EndY=38 EndZ=0
    g5: LineSegment StartX=105.121 StartY=0.000382114 StartZ=0 EndX=106.736 EndY=0.000382114 EndZ=0
    g6: ArcOfCircle CenterX=106.616 CenterY=19 CenterZ=0 NormalX=0 NormalY=0 NormalZ=1 AngleXU=0 Radius=19 StartAngle=4.71873 EndAngle=6.28319
    g7: LineSegment StartX=125.616 StartY=38 StartZ=0 EndX=125.616 EndY=19 EndZ=0
  constraints (21):
    c: Block(g0)
    c: Coincident(g1,g0)
    c: Vertical(g1)
    c: Horizontal(g2)
    c: Distance(g2) = 105
    c: Coincident(g2,g0)
    c: Distance(g1) = 19
    c: Coincident(g3,g1)
    c: Horizontal(g3)
    c: Distance(g3) = 105
    c: Coincident(g4,g2)
    c: Horizontal(g4)
    c: Distance(g4) = 1.61553
    c: Horizontal(g5)
    c: Equal(g4,g5) = 1.61553
    c: Coincident(g5,g3)
    c: Block(g6)
    c: Coincident(g6,g5)
    c: Coincident(g7,g4)
    c: Coincident(g7,g6)
    c: Vertical(g7)
FEATURE [Part::Extrusion] Extrude083  label="sideB008"
  Base = -> Sketch092
  Dir = (0,0,1)
  DirMode = 2
  FaceMakerClass = Part::FaceMakerBullseye
  LengthFwd = 3
  LengthRev = 0
  Placement = pos=(-0.1205,0,72) rot=(0,0,1;0rad)
  Solid = true
  Symmetric = false
FEATURE [Sketcher::SketchObject] Sketch093  label="topSketch029"
  FullyConstrained = true
  sketch-geometry (8):
    g0: ArcOfCircle CenterX=19 CenterY=19.1201 CenterZ=0 NormalX=0 NormalY=0 NormalZ=1 AngleXU=0 Radius=18.8799 StartAngle=1.5708 EndAngle=3.14793
    g1: LineSegment StartX=0.120501 StartY=19.0004 StartZ=0 EndX=0.120501 EndY=0.000382114 EndZ=0
    g2: LineSegment StartX=19 StartY=38 StartZ=0 EndX=124 EndY=38 EndZ=0
    g3: LineSegment StartX=0.120501 StartY=0.000382114 StartZ=0 EndX=105.121 EndY=0.000382114 EndZ=0
    g4: LineSegment StartX=124 StartY=38 StartZ=0 EndX=125.616 EndY=38 EndZ=0
    g5: LineSegment StartX=105.121 StartY=0.000382114 StartZ=0 EndX=106.736 EndY=0.000382114 EndZ=0
    g6: ArcOfCircle CenterX=106.616 CenterY=19 CenterZ=0 NormalX=0 NormalY=0 NormalZ=1 AngleXU=0 Radius=19 StartAngle=4.71873 EndAngle=6.28319
    g7: LineSegment StartX=125.616 StartY=38 StartZ=0 EndX=125.616 EndY=19 EndZ=0
  constraints (21):
    c: Block(g0)
    c: Coincident(g1,g0)
    c: Vertical(g1)
    c: Horizontal(g2)
    c: Distance(g2) = 105
    c: Coincident(g2,g0)
    c: Distance(g1) = 19
    c: Coincident(g3,g1)
    c: Horizontal(g3)
    c: Distance(g3) = 105
    c: Coincident(g4,g2)
    c: Horizontal(g4)
    c: Distance(g4) = 1.61553
    c: Horizontal(g5)
    c: Equal(g4,g5) = 1.61553
    c: Coincident(g5,g3)
    c: Block(g6)
    c: Coincident(g6,g5)
    c: Coincident(g7,g4)
    c: Coincident(g7,g6)
    c: Vertical(g7)
FEATURE [Part::Extrusion] Extrude084  label="sideB009"
  Base = -> Sketch093
  Dir = (0,0,1)
  DirMode = 2
  FaceMakerClass = Part::FaceMakerBullseye
  LengthFwd = 3
  LengthRev = 0
  Placement = pos=(0,0,72) rot=(0,0,1;0rad)
  Solid = true
  Symmetric = false
FEATURE [Part::Cut] Cut076
  Base = -> Extrude083
  Placement = pos=(0.05,0,-75) rot=(0,0,1;0rad)
  Tool = -> Extrude084
FEATURE [Part::MultiFuse] Fusion155  label="sideA006"
  Shapes = -> [Cut076,Cut073]
FEATURE [Part::MultiFuse] Fusion156  label="sideB010"
  Shapes = -> [Cut075,Cut074]
FEATURE [Sketcher::SketchObject] Sketch094
  FullyConstrained = true
  Placement = pos=(0,0,0) rot=(1,0,0;1.5708rad)
  sketch-geometry (8):
    g0: LineSegment StartX=0 StartY=4e-16 StartZ=0 EndX=-7 EndY=4e-16 EndZ=0
    g1: LineSegment StartX=-7 StartY=4e-16 StartZ=0 EndX=-10.5 EndY=4e-16 EndZ=0
    g2: LineSegment StartX=0 StartY=4e-16 StartZ=0 EndX=3.5 EndY=4e-16 EndZ=0
    g3: ArcOfCircle CenterX=-10.5 CenterY=3.5 CenterZ=0 NormalX=0 NormalY=0 NormalZ=1 AngleXU=0 Radius=3.5 StartAngle=4.71239 EndAngle=6.28319
    g4: ArcOfCircle CenterX=3.5 CenterY=3.5 CenterZ=0 NormalX=0 NormalY=0 NormalZ=1 AngleXU=0 Radius=3.5 StartAngle=3.14159 EndAngle=4.71239
    g5: ArcOfCircle CenterX=-3.5 CenterY=3.5 CenterZ=0 NormalX=0 NormalY=0 NormalZ=1 AngleXU=0 Radius=3 StartAngle=3.14159 EndAngle=6.28319
    g6: LineSegment StartX=-7 StartY=3.5 StartZ=0 EndX=-6.5 EndY=3.5 EndZ=0
    g7: LineSegment StartX=-0.5 StartY=3.5 StartZ=0 EndX=0 EndY=3.5 EndZ=0
  constraints (20):
    c: Coincident(g0,g-1)
    c: Horizontal(g0)
    c: Distance(g0) = 7
    c: Coincident(g1,g0)
    c: Horizontal(g1)
    c: Distance(g1) = 3.5
    c: Coincident(g2,g0)
    c: Distance(g2) = 3.5
    c: Horizontal(g2)
    c: Coincident(g3,g1)
    c: Block(g3)
    c: Coincident(g4,g2)
    c: Block(g4)
    c: Horizontal(g6)
    c: Coincident(g5,g6)
    c: Block(g5)
    c: Coincident(g6,g3)
    c: Coincident(g7,g5)
    c: Coincident(g7,g4)
    c: Horizontal(g7)
FEATURE [Part::Extrusion] Extrude085  label="frontLeftRightCasePillarSideBracket003"
  Base = -> Sketch094
  Dir = (0,-1,2e-16)
  DirMode = 2
  FaceMakerClass = Part::FaceMakerBullseye
  LengthFwd = 2
  LengthRev = 0
  Placement = pos=(113,11.5,0) rot=(0,1,0;0rad)
  Solid = true
  Symmetric = false
